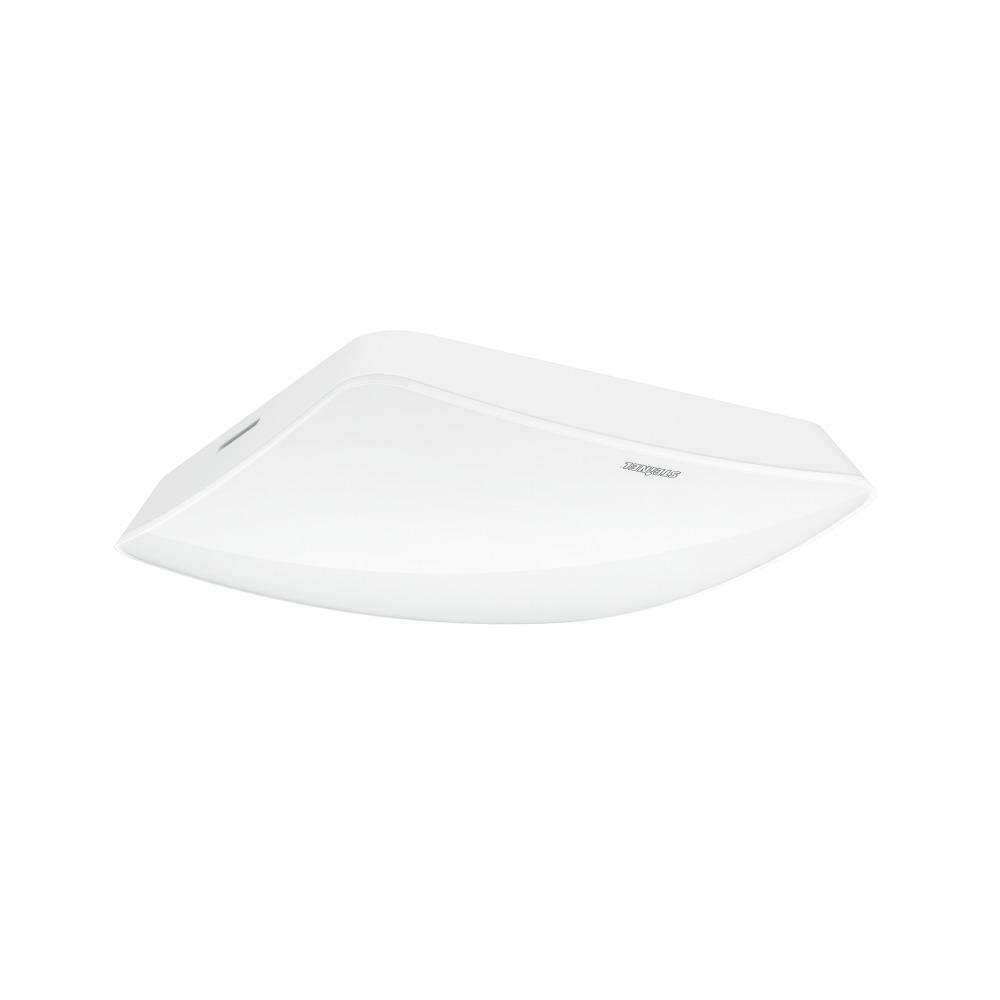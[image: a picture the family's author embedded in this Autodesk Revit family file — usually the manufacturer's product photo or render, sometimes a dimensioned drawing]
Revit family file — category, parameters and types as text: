
# Revit family: truepresence_056339
name_source: partatom
category: Electrical Fixtures
revit_build: Autodesk Revit 2016 (Build: 20151007_0715(x64)
units: mm (PartAtom-declared; Revit-internal decimal feet)

## family parameters
Cut with Voids When Loaded = No
Host = Face
Maintain Annotation Orientation = No
Part Type = Normal
Room Calculation Point = No
Round Connector Dimension = Use Diameter
Shared = No

## types (1)
- True Presence
    Apparent Load = 0 VA
    Default Elevation = 1800 mm
    Description = Type: Presence detector; Dimensions (L x W x H): 31 x 103 x 103 mm; Power supply, detail: KNX bus; Sensor Technology: High frequency; Application, place: Indoors; Application, room: classroom, lecture hall, one-person office, open-plan office, high-bay warehouse, production facilities, conference room / meeting room, hotel room, care room, duty room, recreation room, dining hall / staff restaurant, changing room, kitchenette, sports hall, reception / lobby, WC / washroom, warehouse, Indoors; Installation site: ceiling; Installation: Concealed wiring; HF-system: 7,2 GHz; Electronic scalability: Yes; Mechanical scalability: No; Mounting height: 2 – 12 m; Optimum mounting height: 2,8 m; Detection angle: 360 °; Angle of aperture: 360 °; Sneak-by guard: Yes; Capability of masking out individual segments: No; Reach, radial: Ø 15 m (177 m²); Reach, tangential: Ø 15 m (177 m²); Reach, presence: Ø 15 m (177 m²); True Presence reach: Ø 9 m (64 m²); Twilight setting TEACH: Yes; Twilight setting: 2 – 1000 lx; Time setting: 30 sec – 1092 min; Basic light level function: Yes; KNX functions: Photo-cell controller, Basic light level function, Light level, HVAC output, Constant-lighting control, Light output 4x, Air pressure, Humidity output, Presence output, Day / night function, Dewpoint, Temperature output; With bus coupling: Yes; Settings via: ETS software, Bluetooth, Bus; With remote control: No; Interconnection: Yes; IP-rating: IP20; Material: Plastic; Ambient temperature: 0 – 40 °C; Colour: white; Colour, RAL: 9010; Manufacturer's Warranty: 5 years; Version: KNX - concealed white; PU1, EAN: 4007841056339
    Height = 0 mm  [stored 0 ft]
    Length = 200 mm  [stored 0.656168 ft]
    Manufacturer = Steinel
    ModVariant = No
    Model = 056339
    Number of Poles = 1
    OnlyDefault = No
    Power Factor = 1
    Product Name = True Presence
    Product group = Presence detector
    ProductGroupID = 4
    RLX_Detail_Level = 1
    RLX_LegendID = 3.1
    RlxData = Q
eAHUvXeUVNXbrduAICAioiiCICJNzkjqql1FzhlEktAgOefQBAmSc46SkwoCCip2VRciZgXE
nHPOP0Uxct5n1VzfqW/cc++4/5wxzuE7T8/5znr32muvHehuOb+dK+3y5TT7c/lfJ1j3J783
ppftjy9v7eBdchu286SlzY4aCetwX9yGly9/nef6tKZjRg0YNrr/xGFjRrebNMrcsPGD8ufL
zaY3dksbnzYpbVBambRO5galTTBGp93tkoppNdPqptVLq2P/19A6KqU1stFv0xxSJ5nHssuX
v8tTKK3dsCFDJzYfNWzixEHj08rkYh8Fx6f1TxuY1u+/jcZI5f6XI9m8bNZXpLUfNGForsJu
BLff9P9Fd660K5T+ZAf//+fP/56+a92ux4xNSztpbnSutLQHSrYN3phUMbimz8zYQ8+2D/IU
PxBeXX167JposyD/XxnB3KFzYre8UzxIe6BQ8NnIVbGdO74Jj51xZ+jdTzbHWi/9JNyl9qlw
g5e3xO5qtSPcv0Hn8N7Ku2IFyk8NvzRncujhrXtidevND5f96fPQ1Px7Yj//1iGYV6NNRvO6
WbFlj3YIpuW6LlZjeFZs+fvtg5yuO2Obbp7u9xVnX+/b3N6aVDH+Re+Zfj5x5qP9xlL2G2O/
2lc2+9IcsplDj7vHhtPSPipX8M09sS8joexXJryWkfelpE9reD5WN2Nz7J3wI7FLzdvHxy2e
GGvY6Kb4zTddHc/XYVWsX7WK8Qln2sTrr53MHOK2Jm4OL3zWIF7spubxn26YHpvcf0140JH2
8VJ1JsYeGVYvKL2iRbzBz9NifatVDAbYts1s2+pDL4aKjusQr71uQmxV3QLZD2/pEL80bkJs
zV+fxrZ/9mTspr1bYm9s3RnrGLkjVqjIrti1X8+PDe79XfZzf++OfXJoauzEZ7OyN290xxKb
sz5POseiPESu/hD9GifMOBwv56xy7w1+X2H2pWMMOMYtf6+OrT3aPkivPdEfozvvNv941zNt
gk42/xnr68U7Tm4R/JUnK/ZAwV+yvx3XIZizdkKs5LBrQgO2dAjC4yfEug48Hi7RpH2wddlE
1i2YbNvebts+83qDYGXZ5sHsa6bH7HqL2/UW1/UWt+stxvVm10Pcrocw1wPnhGvsiye3xd61
frsGgi/tGrDrJ27XzxNcP3bNxO2aCXPN/PVTu/jMhw+EexUdEfv3ibbx14/vDx/t2jWWa36b
ePXH9oXzrg/FBv/RLr5/65nbyO99sq3z5Nd/3SY+vsUHMfI7j7eOB7++FyO/599WNk75OPmh
l1raOOlx8m/HNI1P21fP5ctaNImvXlnX5WR8Rj8Zn9HPGIxFzhiMRc4+2Tc5+2Tf5GOK5tnD
XMnxzFX94ZT+sO+38YOU8QM/vs0nSJlP4OdjWZAy/8DP38YIUo438Mdr+wxS1ifw62NzDGIT
1+5lnjbHoEfD43uZp/rd+tsc6Xfrr/ED+m2OjB/Qr/m43ObIfFyu+bucjM/o1/G6nDEYK2V9
XM4+2Te5rWE55sp+C755Wznmqn43V3Ktvx+f8+XH53y5XOfX5Tq/LmeNmSvjsMZ+/p9saRFf
cbJcYPuMvXOoSfymT2s536pWB3ftca1eKNUufmDThzF815pt7BquEMe32dws3j+7vvMoNTmf
04dnO7bHc50wrvKwz60/8P02TuDHMQ38+PZ54Pdr2wV+PjaeO7+MqdzdX+oPyDWO8xrfee3X
eRuP+TjP/ce4mqcbF6/jcrmO13nmy7j0tGuYEV+5JezW8OsHa8RPv9TUeVvj+C9bWjj/9pwd
sR/6tXa+6pTOGUUXt3H+4qYHwhNDyXyhnZOw+t/8sFbwyENNXM8HK8PB2WYZzhc83zQ4t7eG
8/9Y70qdx0vhVkHG8W/DnNMiM1oHC+pudP79RW2C+6v3eYL8q/6tg7eG7uBai51o2CqoMv87
52uubBnMeKNAnLxyvZbBuyevc/4/+VsGhx8u7nzN/7QIfq9Z0vk/3m4RfPZOKee/tjlwnGx7
ckaT4FKD2s4va5QRvL427Hz3L2sEp482dZ7r7mO7/uifdMvX4TdatnL+vgmrw0tWtHY+o8i1
2ZXs+UhPseBorEuFZG7rE2+qbYfEasULn27iep4aFo4vH5Xh/KXHm8YLv1HD+e+T17nz3/Vq
FV+09DN3vP/sbx3/fN5i56dNbxPP983cEPta9Fer+NR/ssP4r/9YEBtfeOF/+QEPL3L974QX
hgd/uPC/vO/hmxf7liUtt8DzHR3g+R4Lj+YV+HwCf6U8yneGbFfA4DPAF5RHr5JHCwn81fJo
YflrTP04+CKqUfYHeL4Lw6NFxXXKyPHXCzw91Cjb4NFiAs+41Cj7Bubre/A3qEZvFPji8uhN
Al/C4HO2LSnwHC81erMopYy8tMF2gL/FYH9lDD8f/K2q0bLyqD92/G2q0XKC77B9D768arSC
PFpR4CvJo5Xl0SoCX1UerSbw1ZXXMPVj4muqRmvJo1yDgK8tj9YRXL++h+vUj4nnWqVG/THi
86tGuUZuN+oa/nzh/TnF11ONlhH4+vIo6w541hrwrDXg/ZrjWWvAs9aAZ30Bz/oCnv3hUdYX
8A3kUdaX+TY0+AwyDD5DQ/LUePtG3n2GBgIfkUf5EQvwjeTRxgLfRB5tKvDN5NHmAt9CHm0p
8K3k0dYC30YebSvw7eTR9gLfQR7tKPCd5NHOAt9FHu0q8N3k0TsEvrs8eqfA95BHewp8L3m0
t8D3kUfvEvi+8mg/gc+UR/sL/AB59G6BHyiPDhL4wfLoEIEfKo8OE/jh8ugIgR8pj44S+NHy
6BiBHyuPjhP48fLoBINrlWuXaxTwE+VRrlHAc13yOdc8NeC5D/DoJIG/XR6dLPBT5FGuXcBz
vfL5TarJ8CVUo1MFvrg8Ok3gs+RRrmnAcx3z+Q2qyfDkgJ8u8Dz/qdHS8ijXPeBLyqNc94Cf
IY/OFHj+vqFGbzboxfs+slkCX1gevUfg+fubGp0t8HPk0e4C38Pgc74HoAZ8QXl0rsAXkEdz
yaPzBJ4/1Py5V+Dny6N9BT7T4E9ugxrw/P2CRxcIfG15dKHAL5JHuccAz33F5/z9RQ14csAv
Fvia8ih/L/IZOlTgq8ijwwV+iTy6VOCryaPVDXrxvo9smcBXlUeXC3wDeZT7FvDjDe7bFcY4
gefeR1fKU+NHSVfJU+NHSFfLU+OHSdfIU+PXqkb9cwy/TjU6SODXy6P+OYnfoBrtL/Ab5dF+
Ar9JHt0sj94l8Fvk0d4Cv1Ue3SaP9hT4++TR7fLonQK/Qx7dKXYpow+/WzW6R+xVRg/+Duk+
eWp8V+l+eWp8Z+kBeWr8QdVoR4G/Xx5tL/APyKMPyqNtBf6QPNpa4A/Loy0F/iF5tLnAH5FH
mwr8UXn0mDzaWOAflkejAv+IPBoI/HF5lHsD8OONscZoY7nAL1M2Up4av1Q6XJ77n+fFYiPT
mG8sMHjODDAWCjw5minP866Pca/AzzN6GHOMuQZZL4Mc8OQofXie3d2M2QJ/j4F2kafGz5J2
kqfGz5R2kG9n2saYbjQzphhTjVZGC2OawJOj9OEjxkRjktHEaGRMFnhylD78ceOEwbkA/Cp5
dILArxD4lQbbcn7ZBvCPyqOPCTzXNDXKtU7vwwafAZ5rC48eNbgeH5KnxnNN49FD8qgfB899
Qo36/XHf+fngeY5QozxfuF95bvAZ4LfLo/TtN/YY9AJ+tzzK84UenhV8Bvi9Bp/tNPy2ePbB
vnnu+bnhH1eN+rXFr1GNrjbo5fnJZ4DnOYtHN8mj6wR+ozy6QaxXRt9agzEA7/fHeWc+rxqp
f04/3ZLLKS3n+umJXw7VjqStrpI9tOiMRLMxlSMvTKoSCw+fkbglLY/rmfP5zES5Q+eDC8ur
ZD/ywKxEvypPBK/VrhIr+v2sxDeT0iNPrKqSvW73jMS06emuH//rusqR87vSwoxz08M2vv1h
/H8+qx8ZvezB0N7XpydK/JE7sn5llWzGfzp+PqCH8Vd3zg4OLqsSYvzKR3a6/I+69ySu+898
549MuCdBb/JP8r8Yep9danls9fo68ehj9yS+3Vw6e+PWnXG2LXZ3/4a3F/wt3iN9VuLzsz9m
31m4eM4DFWYmvsz3b+iRNuk5zPls2YoNhz5dOYc5F3qldHjqiNo5zHn21zeGnskIckpunJ74
q/Ct2Q+dSvb802Z/dvVjST8qq2b22zOb5JzrPj3RsHnZ7D1PtsxhbT/edn3253na53x7Pitx
Zlqp7OP/XHRz2FSuY8P8R5Jza7t3XvipfnXdnK+79sFw+V+rOv/W2r7hwqcaBBzLnMeeDN9/
ZlrAsff78lhoZbudQcpxBRyXjiXCsbzx4tHQ0ocqRziWGw6WDw2c1STC3O4/uSvUoVoQ4Viy
i6eHuk5Od/2b8p17fIqdP7bVcblttSbOf9326tjtWbUjrMlrXwyIvXJr0o/d2zD04qWLbg6T
/96bndkrObf9L0+MNRsy18358Ve+zn708Yg7luNPt8z56cy6hm59DtTO6Zc9LsSYwbHaOWN6
LcvAn59TNOeJTXXCL/acmdhQonjOnSPOhjhfowdmxw99d2UG10bT5jvjg/o8HmIdXl+1M352
eHPn9z60Mz6y3LmT5OrJTulxfm2P7HiPdQXcNXbnLWVyrtu/Njv97RmJostvzPlq9ZAY+2p/
tHbOxedfcPPJfLN+zo/9P8jmuv0pX/ucFQfqZ3BOGxnV068Ijg5uE6m5MCtxtnihYNqBjpEv
92UlRpWeG07xMeeHZCU+a5g33qVll8gfZ4Ynrt+4J6dUk4mR5u9VT4zdVD3R7Nz8yJSX9+Y8
tGJ4gnzf2evij/fLStB/vtTO2KpdWQnGaVl6WXjF3qQv/XPuoOSwZM+0J3ZH2nyb3HbjgurR
Yj8kx7ywc3g0/+C9bl8rBmZFf+t3lZvDzXuyoteV3uDmduP+rOjaQ7PdnNsOz4p2O5gWsN87
3h4eLVB2T4T5fHq5ejQ+sXqUea75d0/ku4eHR8mPHbw6aHF3VpT+PSt3hbvtyooyzzGHlsRO
7036+jcWiL8yKNmzavGenG7PJrf9eED1xJFra7gxOy4bnvj9nb1uX2uPTUg899XqSFaRL4LL
PbMSnz67P/zyF90i/y6enKi5cmr4vSOLI08VnZ74eejfIZ5nF4pnJS5dHBbbU65XJG/VyYnQ
prmxAc2WRRpsmJ7o2u5y7JetGZFflmUlavbPFWduF/4amfg6dDznrZ1XR5acq5go+2TVxC37
7o/89Em1xDtzqyU637oqsmDBgZyLr41IfD3/zkjZZUXiZ16Ynjh+R91I2kcXY7VXJdf/6B/r
YudPTk2MPDAu0v73NbG7rpnizmOjKnNDj/+S7D+2el7o7OFk/zcNloW3FZua2HbNjMhzH38c
/mJdMt+amS/osiTpw9+vjVwzf5Qb8+mfvw//9vOMROnPSkSKTL0vct9X/RMzQ49GrhuVHi30
c8Q9dz/6onK0YscqiVylDkQavzsy+toXyeO65sj0aIHMq+L/XKofef3o5GitlQ/GwoMWRVYF
E6MXS22IfVRyc+RI0enR3YfTYqzhNzdlRR+c1D3MGraoOjm6wK4H1vD4+unRAXY9sIZdlmdF
u5tnDRsXHxUtsf+RCGv4wdcVowMPVI2yhiVurh6d1bpalDV8sdGByHNPjIgy5rBviwTLX5ge
ZQ1Pdv49/ObK5LUxsMnG8JSTU6Os4aPNNoeHFp7iroeb+s/Kzvkl2V9/3fTsdw4n+0+uXhJ7
q9jUKGt45diPYg3XJ/PTB/LGTyxJ+jteWJszc8koN+ao81/Hvv/PjChreMvd9+U0PDQgWmDq
w5Fw2/KJ5RuDaI3CNSPxM5UTNcZVibKGO3NGJmbOOOGO69TCSCL/6huizQvsjryTVSfx6I91
oh0K/hYc//bKROkfW0br9T8YuXXggZyPvh0b/erRo8GPLabk/Nl6XPSpsSMjM77+O5Zr1bTo
3H/7R5bWnxm7It9MN4ch4yKxydGsKNfVjc8uCVe8anqU9b++6Z7w7y/OiPauWSZyw+0Fg8Ov
TYv+fbpPZNlLKyKr2492x1Kx54HI9jvGRFnzadNviD63KeLmtvqm26PvdErOrfcrLaPZD1/p
zsWO/OOiQ248EGnT78Gg88xx0Z9vmRhhbt8cyYr2sPPY5Mr2kRLtsqLffvStu7+ebTAzusXO
+wsbikU6NcqKnltdJcw8ZxeaHl13aLa7Ts7mtuOw5wbrqWeFe57UeCAr+qc9Wxhz48Ks6CXz
XCeD59i+brzBefvOO+r/9u7T164ly3luLHliVDTXujU5XANnPxwdHVbwQA7jf7U+Er1j7o2J
rPrbI7121om2fKFOgvV/8+v80fvmt3TX/O/b9kem/zs2Ub/wo8Hlp6ZGZtUal+AY8z1dICj6
YFaC+SzI/W548ITkc/LrXavD3TrOTGT/WDSydGR6eMGCaYmHtg6MlM2/OlbnxekJ7pfxR9bG
nt+Y/L6m7k/545X/nJbgGn4gc3nO8/NGu3vzoVMHcob2GZPI90fByJjniyUulIsmuE6q/Fon
MWBycp5dG7ZM7LyYP8F1MuDdsYmZQw7kMM8dGeMSt9ebmsM8B47PSjRd92GMdbh/9szEDUft
+rbzGzs9NVE3mjfGmqyoMCPx3Ix5Ya7V9c9MS5w7fjj8c2Y/972Vvv+J5jKT28hjXGHkNfKJ
K03ziwKmBY2rjELG1UZh4xqjiLjWtKi4zhSuN4oZNxg3GsWNm4wSRknjZqOUUdq4RZQxvdUo
a9xm+DEZH8oZ6UZ5o4JR0ahkVDaqGFVFNdPqRg2jplHLqG3UMW436hqMV8+obzQwGhoZRsgI
C76JZNG4CBsZjY0mRlODn8maGy1ES9NWorUptBFtTaGdaG8KHURHU+gkOptCF9HVFLqJO0yh
u7jTFHqInqbQS/Q2hT7iLlPoK/qZQqbobwoDxN2mA41BxmDDH98Q80ONYcZwY4ThjxEdaYwy
RhtjDI7XHys61hhnjDcmGBONScZkMcWUNZhqTDOyjOnGDGOmMctIXQfW4x5jtjHHmGvMM+41
5hsLDL8m6EJjkbHYWGKwPn5t0KXGMmO5scJYaawyVos1ppnGWmOdsd7YYGw0NhmbDdYOthhb
jW3GfcZ2I9PYYew0dhm7jT3GXoP97zP2GweMg8b9xgPGgwbn95Bx2HjIOGIcNY4ZDxuPiOOm
J4xHxWOmjxsnjSeMbCNmxI0cg/VOGKeMJ43TxlPGGeNpg/P2jPGs8ZzxvPGC8aLxktHWGGG8
bJw1zhnnjVeMlkYrw19XXGOQaXAtpl6jeI4RUq9tPOcc/P3AvQHMvZPR3uBaA3wbg3kB/sL/
xdTLZc/A3HaND5+ccfXi7CCt0KaGq65fHWQerxJ6/YUzwXOje4Rv23U4ONjlkfA/1/UJ3hqd
Hf6kx8Zg6tF/w9GJc4KbLxYJLqT1DY73LRRU6z0isKVIW/dk5yDt4PQG49+rFKStXN6w2Kd/
h+uvaBBh+zPHOkSod45rHCn/2bww46Ps/9Ki4uGyuTtE0Cdat4uMubgtxP4q5X0/zP7ea1si
mFm2RgRtnl054vdb5e1abh4L60SDnz4uGlS1fwOYdaRX8EH4Dqc5v70UfrjtuuDQ0wcalr3l
eDD5n7nhJWuzgztsn99seT5gP7t/eCood1Xx0Kxn8gYvHxnckOMnP7r1TKh0yVyhIhVLhul/
rE1NG6dCg5Vr7nTHWm/6zuB0u3fDq/atDOp0uikYcGlR8PO1tYJLaxYE9R6MBOsWznfzoS67
uK/7fGjZkcFD7YpHmF/vGQUj1GfSr4x0/n2Oyx/+dVfwyaR/gr+f2Rj89srXwbl3Dge5/sof
eb382aB699cCzsuKuz4Jehx+KShS8d3gzQUvBO13XRe5ff7ZYM7UUpGqW84GF56pFan0/csB
68z5u6pF8wj9PUe3jlz74fMB68s4x5bUj3A+WVfO54cfVYlwHvt/fj7gPGxcdS4Yf8NvYfbL
ejAf1i9X8XPBF3dOcPPk+B+tnSt5fu04WAeOi3UocuSqCOtw+vZCNq8OweGlWwOuA9aL42X9
OM4b3z7rxuP8cLzsn+vxsatedsp5Yr7LLp0Nnh7fNii54FwwpP/K4M+qNSIv59sc+qp4zcie
206GXmrUPNLqzLrQ+D9qREof+Cr079s1Iu2LFQq/Urakq1HqR078G/D5hgKXA+pS337i6p+H
furq3b+84+r/TH/X1e+sfM3VB8q+7urfmp922vLsaZe/9MYTTi/1eMLldQvtcHWXx7e7etml
Dq5G2V+fY4kw+/8q7ckwdf7Ct7r64N/lXJ2593SIzxvNfDHE56fONXB1ZqW2ri4/Kbn/yf8k
9/9X3mw3foVFyf0PCiX3P/fL5P6/697RfY4y3s2jTyX3F0/uf/bCsq6uOLm823+njU8n93fz
2eT+T0SS9TWdXb17Wyu3jsM+beXW9dCXzZyePtjM5Zm567t6zFv1kn0ZyfUfZsr+P/0suf7P
NEiuf7sSn7r5ldmUXP9Xyr7r6rIPJtf/pZPJ9X+zc3L971+Y3P+FF5P7b9SlWcT+HVc4e2tL
p426lIuEHtgS4nxzXfzeo0Sk9L9bQtdH87nr5Xz/fwPyBwt8EnC9tBr1iauvG/yO00+ffSuo
sHNx6KYXnnc11x81zwmut88ff9Xpud9fdZ+/0fsppzxXttXZHdrZLdvV3QftcMrzJ1J2f4jz
z355fowfdTDE82TlTQfdc+fLUgdC5/vnhPk885ZSTnnuMB7PobQuW0Odbnki5D635xPzyTyb
7uq8S5P7r1vpaTfPUV9mu+M6Py85j1Yrk/N4NrHSzXv/9RMD1ofrgfHurdEuYH1+Wvl7mONb
VTrh9n9peskw6/PRptKuHpsTc/sb++5ut/8u/du59eV5wnx4vhzptTmUWeO2kFObJ+OvqdDa
9fEc4ng2lG/u6i5V6zvlecX6cH3Qz3OM9eG5xvrw/GN9Ti9Nnrep25Lni+cg4/EcZH2arE+e
P55XzOdy+dfc8W0qmtz/0Y9bu3kua9PGXSfj73g74Lopuf0DpxeLfeZ0Spsr3edlCt2cvJ6W
1XTaYEjyOjt+NHmdfdEnOc5smyvjfLTjH6fPDazMvyUMP/fvw07rPZHHjXvy2S7J/S1Y6fTg
i7udnlp/yOnCJcecfnvFcaexZieczt/8qNOuBZ9wGnr2lNOHLj7tNPPsPrffVScuOW1QrJLb
b8WXjjvt1iyf67u7SA+nv65Y6/S2d086vbVncrwFx5Ljtb42uS6/9Eyuy9NffOr60sr+43TE
zwXcegwM3eI0357aTm/468XgnvYbgiXhxcHmoouDtBdfCH558GTAfs5vfSE48upzwTeRU4H9
+9tg+bang3+6JILCtZ8Prou/FGT93ddtNy4oGKzqcVXQbn/BgPmOKTovg/n/Wn9Xxh8dXgrW
v1YgGHfoxeDsvsfDjP/8uArhy72f5++pEPN/Y+muEMdTYXAQYr/lNl7O4HgHdX0og/V49e3n
M9Kav5Wx5pGj4VOrH8l4+vl/wqwXfbML/JFRfuyI8Ozg+4waSxeHWc9BXauHdh7LG2I/aU/l
CjW41CScOSEtdO/29mHW/aNqq0KzP2kZKlzs09Cplv9mFLzvzrB935PRr1Jbdxysw9FjbYNb
174UVOqzMmCN0vYcyRhXcnnAPN5psDtgfNaJebBOH31dO7SidCI4NXFt6Pi4M0HaX1+F7tn7
XDBwwC/h3t/a9vbHvnVzP3Pbt2/O5zEF8ivk0bwCn0/gr5RH8xtsV8DgM8AXlEevMgoZVxuF
jWsMsiKqrzUtapBfZ/hx8NcbbFvMuMFgn2Q3yqPFxU3K6MGXEHh6qFG2waMlBZ5xqVH2DczJ
9+BvVo2WEvjS8ugtAl/G4HO2vVXgy8qjt4lyyuhLN9gO8OUN9lfB8PPBV1SNVpJH/bHjK6tG
q4iqyujDVzOqGzWMmvJoLYGvLY/WkUdvF/i68mg9ga+vvIGpHxPfUDWaIY+GBD4sj3IBQ0QZ
fVHDj4lvpBrlmADf2OB4uWa5RpoYTY1mAt9c4FvIoy0FvpU82lrg2wg8P+MBvp3BuvMzIGsN
eNYc8B0M1ph+1rejQd5JHu1ssMbMoYvqrqbdDOZ7h8Fn0N2g506jh9FT4HvJo70Fvo88epfA
95VH+wl8pjzaX+AHyKN3C/xAeXSQMdgYYgyVR4cJ/HB5dITAj5RHRwn8aHl0jMCPlUfHCfx4
eXSCwE+URycZk40pxlR5dJrAZ8mj0wV+hjw6U+BnyaP3CPxseXSOwM+VR+cJ/L3y6HxjgbHQ
WCSPLhb4JfLoUoFfJo8uF/gV8uhKgV8lj64W+DXy6FqBXyePrjc2GBuNTfLoZoNrdYvRQ+C3
yqO9BJ7rks+3GdSAv08e3S7wO+TRnQK/Sx7NFHiuVz7fbVDvMfYa+1TvNz1gHFR2vzz6gMA/
KI8OFfjhBp8fMqgBTw74wwL/kDx6RB4dKfBH5dHRAn9MHn1Y4B+RR48b9OJ9H9kJgX9UHn3M
eNw4aTwhj2YLfEwenSrwWQafxw1qwOfIowmBPyWPPimPnhb4p+TRMwL/tDw6W+C5f/j8GYP6
WeM543nVL5i+aLyk7GV59KzAn5NHuccAv8Tg8/OqyfDkgH9F4C/Io6/Ko8sE/jV5dIXAvy6P
viHwb8qjbxn04n0f2dsC/448+q7xnvG+0VMe3Sjwm4zNxgcG9/R640NjrfQjeWr8aunH8tT4
ldJP5Knxy6WfylPjP1ONLhX4z+XRxQL/hTy6QOC/NOYbXxnzBP5reXSOwH8jj34rj94j8N/J
ozMF/nt59Ad5dLrA/yiP/iSPThP4n+XR/4hflNGH/1U1elH8powe/GTp7/KTTC8ZE6R/yFPj
x0n/lKfG/6UaHSPwf8ujowT+H3n0X3l0hMBflkeHCTw/aFCjg00An8sYZDa36d2mgM+jGu1v
GeCvUI3mlUf72eeAz6cavcsywF+pGu1tGeDzq0Z7WgZ47pF1xhrjXYF/W9kqeWr8G1Lubzz3
P8+LVwyeWU8bLxo8ZxYaZwX+JeNegz56ZhuzjDMCf9rIMmJGwiCbYZADnhylDz/VmGJkC/zj
xkRjvPGYwJ9QNlaeGv+wdLT8SNPhxmFjgLHLOGAMNYYYDwj8QWOgQR89fYytxnYj0+hr7BR4
cpQ+fAE7DwWNqwS+kDx6tcDb/wiGA3+NwbZFDLYB/LXyaFGBv04evd6gt5jBZ4C/QR690Shu
3CRPjS+hGi0pj/px8DerRv3+Spn388GXVo3eYpQxbjX4DPBl5VH6bjPKGfQCPl0eLW/QU8Hg
M8BXNPiskuG3xbMP9l3Z8HPDV1GN+rXFV1WNVjPorW7wGeBryKM15dFaAl9bHq0jbldGX13D
j4n3++O8Mx/+SNy9YnfTf/1bhf/5WfLfheR23cnvTXxfHm2f/Gx2FPVZyPUnx7vCPJ9dqYwe
n+EZjzqv4T8jw/ssbN735TPn+8no8VlAm8Zjf3x2DZFl9PgMT0ad36BuZPg+n0WVsU4FDPqf
UMYcfEY/21IXNKhPGmT0+YzPyaivMqh5tvg+n/E5GXUhw/f7Pp9dTZv68PQ/SmQZPT7Dk1EX
NqiPGb7PZ2VSMtaN/puUcRw+o59tqYsY1MUNMvp85teedSPz/fRRX6v8RlMy+nyGkqFFDbSY
4ft8hpKh1xno9Ybv8xlKhvK5V9/ns0b2mR+PDPx+mYOvbzBPn58XtT+O1J6K6uN4GYcev1as
Bxm1X2fODRl1CYN9kDE+9S0GGT0+K6nMz4H6ZmV+n2TpKX3sk55dyvy8yEop8/OiLp3Sx9zI
miijj7nRs02Znz/ZFmUcB/PgGMoYHAdz9tltyrieyMoYtxr0kTE36iMGGT0+K6vMz5/6kDL6
mC/Z4ZSMubHPA8qYi8/KKaNmvtT7lNHns73KWL8yBmvczPDnqIw5svIGWRn7yjFQtzB8n88q
KKNmvtQtlXEufeavK641MupKBuNRc1zUrQwy+nxWWRk1x0XdWhl9PquijJpjoG6jjD6fVVXm
j5O6bUofx0pWTRk1x0XdThnj+ay6MmqOi7qGMvp8FlFGH8dKT3tlfj3Iaiqjh2Ol7qiMPp/V
UkbNsVLXVkafz+oqo4/joqezMnp8VkeZP3bq21P6OH6y15XRx7HS86Yyenz2mjL2wXExj3PK
mJ/P6imj5lipX1ZGn8/qK6PmWKlfUkafzxooy6OMumFKRi9ZWJlfN3qeV8a2rBNZhjJqjp/6
jDL6fBZSllsZ9WlleU3ZL/sMlOVTRu2vDTKuGeqowb2Q376SUTcyyFhz1rOxsc4g4xnmsyYp
Gb30bVbGvU8fPU2VUbPu1F2U0eezZsrKKKNurowezgV1B2VlTH3WQhnPCDLqlsrKKqNupew2
ZdT+PueeZlvqNgbHy/1LRt3WICtvX8mo2xlk3G9k1P5+494io/ZzJuNYqDsabMs9Q0bdySCj
5vqh7mr4Pp/5e4v7g4z6bYM+1plrijVeY/jxfLY6JeM6Y/zlyhjLZ92UUXOdUaf2+ewO9VFz
7VGvVMZ4PuuuzF+f1Hem9HGNkvFzCnOmj2uUnlUGmb+OyXoo89cxdU9l9HEtk/GzE9vS18ig
J6LMX+9kvQz6GtnXxgZ1b4OMPp/x85rv4/qmJ6yMHp/1MU8fNdc89V0GGX0+42dA38c1T88m
Iuujx2d9lfn7grqfMvq4N8j4OZRt6eM+oCdDGT0+yzRPn79XqPsTWUYf90umwc9wvo/7hZ4G
yvw9RTbAoM/fU9R3K6OP+4qMn5F9H/cVPTsNMn/vkQ1U5u896kHK6OP+I+Pnd7alj/uPHv6t
Ipm/R8kGE1nm71HqIcro4z4l4+dB38d9Ss9BItvW38tkQ5X5e5l6mDL6uJ/J+H0C29LH/UwP
P3+S+XuebDiRZfRwP1OPMHyfz/jdk+/jHqeHn3fJ6PHZSCLLqLnHqUcZvs9nV2hb+rjH6eHn
Zfro8dloIsuoucepxxi+z2e5tS193M/08HM7ffT4bCyRZf45QD1OGX3c465H29LH/UzPCYNt
/XOAbLwy/xygnqCMPu5xsj+U0cc9Tg+/Y2A8/xwgm0hkmX8OUE9SRh/3PdlvyujjHqeH3y2w
LT0+m0xkmX8OUE9RRh/3PdkvyujjfqaH36uwLT0+m0pkmX8OUE9TRh/3PdnPyujLNOg5ZbAt
PZkGWZZBlmlf+xvU0w3f57MflGWacj/Tw++C6KPHZzOILPPPAeqZyujjHif7Thl93M/08Hsl
tvXPAbJZRJb55wD1Pcro4x4n+0YZfdzP9DynzD8HyGYr888B6jnK6OMen218ZbBf+rif6eF3
YGT+OUA2l8gyerifqecZvs9nXyijj3ucnvPK/HOA7F5l/jlAPT+lj/ue7FNl9HGP08Pv69gv
PT5bQGSZfw5QL1RGH/c92cfK6OMep4ff6bEtPT5bRGSZfw5QL1ZGH/c92YfK6ON+poffD7It
PT5bQmQZNfcz9VLD9/nsfWX0cT/T864y/xwgW6bMPweoG2u/9HGPk71nsI969jVkLDdWGD7j
HqdeTWR99PhspbKwMupVyiLKqEPab0NljLXGYLy69pXxqNcaPuM5Qr2OyPro8Zkf73Zl9Kw3
6CPjOUK9wSBjO58Fmgt9PFvo2WzQR4/PNiproox6U0pGL5n/3qeZebalp772cZMyxt9isI8S
9pU+6q2Gz3hWUW8jsj56fObHK66MnvsM+simGdTbDTK281lDzYU+nmn07DLoo8dnO5S1Uka9
MyWjl8x/79PGPNvuNHYbjHeDfSVj/NSMXuo9hu+brnqvMnp85r9/uUUZPfvUV1oZ9f6UrJ3q
A8qoGY8eP15J8+T0HDSYC1kHg/p+w2czVB9WRo/PHlBGzbOZ+kFl9PnMf59TyjJ66fHjkdFH
dshgvzfbVzLqhwyfzVJ9RBk9PuN3/PQVVkbPUSJl96g+poztfMZ/K6DvamX0PEykbLY56kcM
MrabbZDx3xx83xxz9DxKZH2z7avPjhNZ1l0Z9QkiZbPNkfnvkXqYZ1t6+O8V9F1lX8kY/zGD
rKB9JaN+3PDZXNUnldHjMz9eAWX0PKE+dkUfdXZKxt9F1DFl9PiM/17DfvlKRk+cQtm9qnOU
0eMz/juP75tvjp4niWxbenyWUNZXGfWplIxeMv89UqZ5tj1l8N+vGC+3fSVj/NMGWR37Skb9
lOGzBarPKKPHZ3682sroeVp9ZPxdSf2MMrbzGf/NjH3Qx9+L9DxvkNHjs2eVDVRG/VxKRi+Z
/x5psHm2pecFg/Fq2Vcyxk/N6KV+0fB9i1W/pIwen5XTnGsqo+dl9dVQRn02JRuq+pwyasaj
x49XxTw5PecN5kI23KB+xfDZEtWvK6PHZxeUUS81qF9VRp/P/PdD1Syjlx4/Hhl9ZK8Z7Le6
fSWjfsPw2TLVbyqjx2dltVZVldHzlvrIlqt+Wxnb+ayMtm2gjJ531Ec2VvW7yqjZlh7/vRR9
4w16+O+6zHmCfV1hvGc0UTYuJXvfPH1jlFF/QGQZ2600qJtqW/p89qF5+kYpo/7IIKNnlfGR
4belz2cfm6dvhDLqT4gso2e1QT1K+6XPZ5+ap2+YMurPiCyjZ41Bfbe2pc9nn5unj3qtQT0y
pc9nX1hO3xD7Skb9pUFGvc6gHqFt6fPZV+bpG6SM+msiy+hZb1AP17b0+ewb8/TdrYz6WyLL
6NlgUPtt6fPZd+bp66+M+nsiy+jZaFAP037p89kP5unrp4z6RyLL6NlkUA/VtvT57Cfz9FFv
NqgHp/T57GfL6bvLvpJR/8cgo95iUA/StvT57Bfz9PVWRv0rkWX0bDWoB2pb+nx20Tx91NsM
6n4pfT77zXL6etpXMurfDTLq+wzqbtqWPp9dMk8f9XaD+s6UPp/9YTl9d9pXMuo/DTLqHQZ1
d21Ln8/+Mk8f9U6Dum9Kn8/+tpw+6l0G9V0pfT77x3L6qHcb1L1S+nz2r+X0Ue8xqHum9Pns
suX0Ue81qPuk9PksTdkd6qPOpYyefQa135Y+n/nfLXVVRp1H29Kz36DurYw+n12hrLMy6rzK
6DlgUPdI6fNZPmXUBw3qO1L6fOZ/N9dRfdT8mzDWhZ77Deouyujzmf89YXtl1Ml/lzI7Ss8D
BnUrbUufz65SRv2gQd05pc9n/nebbdVHzb+FYn70HDKoOymjz2f+96ytlVFfoz56DhvUHZTR
5zP/O9+WyqivVR89DxnU7ZXR5zP/++fmyqj590/MmZ4jBnU7ZfT5zP8uvKky6mLqo+eoQe23
pc9nN6iP+phB3VYZfT7zv79vrIyaf+PF/Oh52KBuo6xxSub/W0JUGTX/Boxt2e4Rg7q1Mvp8
5v+7RqCM+mb10XPcoG6mjD6f+f/G0kAZtf+eYbwyavcPoGwuoy1bbvC9hv9ehWyZQe1/PzRS
GbX/fohsqUF9m8GxZdrXBUa61RWVDbB6ocH3tf57ZTL6qH1fH6vvNSpZVlnbks0zqKsq62H1
XKOK1f73u73UR0819ZHRR+37ulk92+BnMv9zHtk9BrX//XgXZdT+Z0myWQa1/718J2XU/udV
spkGtf85uZnVUw1+35FhsFYt7Os0g987+N9lkNFH7fsiVk8y+N1QRNs2snqyEbba/96HjD5q
38d1ccLgfPvrhevAZ4003ipl1KOU0UdO1ljZBGXUTZStUEbdVBnXKftgn81Tskcto/bXPT0+
a6E+6scM6pbK6PNZf2U8E+mlp3NKRh+Zf57yjCWj7qK+h61mW+bh71/uaTJq/zw4qoy6o7bl
2UTOs8U/13jWkVH75yTPTjJqvy0Z+6DuZHAd8Hwmo/bHwd8pzJn5dlXffVaTU/vvQcjoI+um
vm3KqP33Qzss4+84/m7rqz4yxiPz35dsV0bt97HHsv0Gf3/6v3/JGI+sp8Fx7FZG3UvZLmXU
dyljW/5OZyz/vcBO9dHj58f3dRwbx5CpbckeN6gHKqPHZ/7a4Hohox6gvjXKqEemZPSS3a1s
tdVk1P5e2KJt2ecg9W1WRj1Y2SZl1EOUrbOMnHpoSsb8yEakZBsto2dYSrbBMurhytZazbZs
548j1+XLf/xy+fKH9d7kxYffXt7xrcmfxl+XE/8SNVzxaYMVe6by1f2/JV9WXPFX4s/LK/+8
vPzPy/f8a00t/rmcUt5z8fKHbM6fX/o5ufyjkx37v+68t+Xa3cOyrm+5tkyptCXdCnQp02bd
JxXTri9wYbf75yY2O/dn06LtjR7ZUroxxaJkZF//97xM8L+G/381/3O/N6f0sKpuZVOy/27z
WflSEx77eWfnKuxeAJnWyLLyassvRf7PerXihhnJX1Ucsrlf+1mjeO037guv7HVfg7z958QM
599sF7G8VEBuGrfa+ZPpofgTrSo5X2ZznbjhvGVx+8z5Rdc2iXd84dM9KWPG5MPsA9/yy8du
oy85/n1h5oHXfFyP5qAeNwfntS/nNQfnNTf13xfzY3IcjMX4HAfHo32Zv8/ti2Nie3KOiXHx
HBP7w9t8g0ZBlX141smvVdWPT5TjM3LGs/06j/q11X7V4+bjvMZ3Xvt1XvNRv1sf51Nf2Zb6
mqoL/zaJX7VyR3hthTLZa2s0i9v/NMJt+K/qNomfzHkthu+T2ch6bonjnykcip88X915lJqc
z+nDsx3b4+1/lmEP4yoP+9z6g//qP1898OOYBn58+zzw+7XtAj8fGy+olb/qPsZU7uav/oBc
4zhv4zG+89pvMs95jfk4b6+cLMe4mifz9/0cVzJPHq/zzJdx6d98XRA/+UjN4J9tu7Nz3xCJ
N9hXK9j48YvZlsXtM5dbFrfPXP5py1vjH09o4vJO5crG98xs6vL5Bd+MzerQzOXDa74Ve75X
c5fbOSm3vX0LlzfJHFRub5+Wvj+c0h/2/TZ+kDJ+4MdnjinzCfx8yFLmH/j5MwZjcVyMYXN1
+2WfNtcwOfu0uYY5XuYYm3jdPnLmaK/u20eu/lhKf4xc48dTxo+Taz4uZ46sHbnm73LmyFqT
63hdzhxtri5njrZvlzNHm6vLeaWgzdXltrZ7bK6+n/X3/ay/H5/z5ceP+/F1fl2u8+v6bf5c
Dy5njn7+jMG51/HGOffMn31y7rU+cc49OXPktYLkzJF7k3ytvZr105a73Pr/Ur6FjbPbrX+3
21vGY2l7wrXKX8w+0bhVvOL7e8KD614TO5LV2o2DT31dXepr7PpNaBmvN+OdGD2pr7qruLq5
jXNbnDz1dXipr8l7vUSjeINFdVxP6qv0yPiMbVNft8d4jEue+ko+9s88yFNf28c54hjIU1/t
l/rKP9s27LdNfS2g7Svw+0p9dWDqKwVtnoGfZ+prBy0L/HGlvprQxgv8mqS+vjD1tYaprztM
fQ1i6usRU1+baHMP/PoPWtgsiKXdFuc8Xj+kRdCp+9sxd05TXrmY+ipGW5tg5emLe1mf1Nc1
pr7GUeO76yH1VY86loBtU18HmfqaSK2D60l9laTWzeWpr5vUmrs89ZWUOkcuT31t5f6tzcpx
DMwh9dWWqa+81LXhelJfi6lryeWpr87Utefy1Ndrcp6ZN/tKfXXpyOLR+OMbagess2ncauc5
D5wPcs4D5wPPc/j+Ea18Hva59Qe+n/H8OKgfX+fXbavz6+5ZxmuS+flexld/XPNhHOc1vvM2
H/brPM80297nzNP3M3/ndVzOMx414/N5yvUW99cb4/H8oef/63WW/hWWqa+2TH73+v/8nxPK
bR/kMa4Q+LwCz3fH/LnS8N9L4/mumBotIPAF5dGrDHoLGXwG+Kvl0cICf43AFxH4aw36ihp+
HLzfx3Xm/Rzw16tGixlkNxjUgL9RHi1u0HeT4cfBl1CN+mPHl1SN8rMGvaUMPgN8aXn0FoEv
I4/eKsoqo+82w4+D9/vgXDCHcka6wXkDPD+p4P1PLGadr4CxPyjnAfCcA8BXlEdZa8BXkkdZ
f8BXlkf9OcJXUY3684ivqhr15xpfTTXKuQR8dXmU8wt4riXA15BHObeArymPco4BX0se5XwD
vrY8yjUA+DryqL9m8LerRrleAF9XHuVaADzXAeDryaNcB4CvL4+WEfgG8qi/TvANVaNcN4DP
kEf99YYPqUa5ngAflke5xgDP9Qz4QB7l+gN8RB7l+QD4qDzqnyH4RqpR/5zBN1aNNhH4pvIo
v1oFfHN5tIXAt5RHWwl8a3m0jcC3lUfbCXx7ebSDwHeURzsJfGd5tIvAd5VHuwn8HfJod4G/
Ux7tIfA95dFeAt9bHu0j8HfJo30Fvp88minw/eXRAQJ/tzw6UOAHyaODBX6IPDpU4IfJo8MF
foQ8OlLgR8mjowV+jDw6VuDHyaPjBX6CPDpR4CfJo5MFPl0enSLwU+XRaQKfJY9ON+jF+z6y
GQI/Ux6dJfD3yKOz5dE5Aj9XHp0n8PfKo/MFfoE8ulDgF8mjiwV+iTy6VB5dJvDL5dEVAr9S
Hl0lj64W+DXy6FqBXyePrhf4DfLoRrFJGX34zarRLWKrMnrw21Sj9wn8dnm0j8D3Mthuh0Ef
4HfKo7sEfrc8ukce3Svw++TR/QJ/QB49KI/eL/APyKMPCvwhefSwwD8kjx4R+KPy6DGBf1ge
fUQePS7wJ+TRRwX+MXn0cYE/KY8+IfDZ8mg5I7dxhTw1nv50Y5JRXuAnyKMVBJ77nBqtKPA8
F6jRSgI/Sh6tLPAj5NEqAs9zihqtKvBD5NFqAj9IHq0u8HfLozUEnucsNVpT4PvJo7UE/i55
tLbA95ZH6wh8T3n0doG/Ux6tK/B3yKP1BL6rPFpf4DvLow0EvqM82lDg28ujGQLfVh4NCXxr
eTQs8C3l0UDgm8ujEYFvKo9GBb6xPNrI4BqMGf66xcdVo/46x+eoRv19gU+oRv19hD+lGj0m
8E/Ko0cE/rQ8eljgn5JHHxT4M/Lo/QL/tDzqnz/4Z1SjewX+WXl0l8Bvl0d5Lq411hvPCfx9
8mhfge9jrDbY5nmBZ1tqNFPg2XaFwTYvCDy91OgAgc80lhls86LA00uNDhR4tl1ssM1LAk8v
NTpY4Nl2ocE2Lws8vdToUIFn2/kG25wVeHqp0eECz7bzDLY5J/D0UqMjBZ5t5xhsc17g6aVG
Rws8284y2OYVgaeXGh0r8Gw7w2CbCwJPLzU6XuDZdprBNq8KPL3U6ESBZ9uYcYXRRDRTRo7n
HkNbyFPjc6St5Knx3GNoG3lq/ClpO3lq/JPSDvLUeO4xtJM8Nf4paRd5avwZaTd5ajz3GNpd
nhr/jNHL2G5wX5H1MMgBT47Sh59sTDH82uJZb3Iy1jbbOGGUE/jX5NF0gc8S+Nfl0ekCP1Pg
7xH4BfLovQb7PWmcEPjH5B8xZR+Af1gefUPgj8qjDxmHjAfkqfEHVaMH5FE/Dn6fanSP2K2M
PvybqlE/NzzHxuc7DWrA75BHlwv8Vnl0izy6UuA3y6ObxEZl9OE3qEZXCfwagV9nsO+lhp8b
folqlPkDfpE86s/TXPP+POJnGzzD/td/Zkf/2+smk6+VdK9r/DLl1ZOTDmYlhvbs6V7v+OO3
0xOREXNivHovWjYr0efnXHFe6/Zlyispv600NvHND3Nz2hcaE9mZOTqxOdf+nFFPV45Undo8
ka98kUS71zZGFuatnRjya60ErwK858EiiSk3NHf5qkUHcurePDpB/wNV5+dcfmdMgnFSX2G5
r1/e+LgyWe51imOm7IxN/TL5ekS9JtK92rJrz1HhrgeSr0F85MzS8PJvkj2ffvx7uG16ctvU
V15GH5oXeeqasW5fH0X3RZrNTc7hrnJFov2nJedW6s9a0QuXk3NuVKx5tMLh5LEUqzM62ibf
AXeMEy+Oid4z6l537KmvyKxSKiv6H3uNHWtV5Ovp0ZvstXesoV6X6db2voNZ0cP22kRedXfl
d9OjG+31efR8XTYr2tlesce2qa/U/KDs2OjGsvMirM/uEaOjXU7vi7BuG7OaR0+ULRJlnVtO
qB3tuaBWlHU+91CRaIHrm7v80rz9kc9aj47SX+iPeyMVPxkTZZzUV3AePpgvOHVL8vWCRevt
Cvf8MvkKRb021L2ac+uk4bFZB5KvSrw639LYgW+SPU93vBj7Pj25beorO7/4eF7Oofxj3b4e
a7Y/54dumsOtRRIvT0/OreiyWokNo2q7OV8o2jwx+WjyWK7I2z2RceMfkVXfzYmkvu4z9TWg
qa8KTX2FaOprRlNfP5r6WtLUV5emvtI09bWnqa9DTX1NauqrVFNfsZr6GtbU17OmvrZV95q7
BhqvyUoc7vK9uwZ6xqYmWl+cG+a1fXV3zkjsHFrQ/htieuT1JdMT31e7L7whEkTq956caH3V
PbHIn0sivbKzEiuuOB/jNYWprwXcelffxPs/bckZ9tFzkXd+6Ji484vCiYvDqkVq/Z6euKFi
eqJMvnOR198qkej3R3N7ZWmTyK0Htuc8MWFAgldbXqy5IuetFaPdfdGiX5H46XuT99TeZ6+O
/3H19ERWueaRYnl2xrYXTb6KNHxxTWx3LXut4GvDIlfm1A0veSX5GsRbfp0RftReucrrVr98
4KvwjyeSr1NMfc3ioHObI6+u7JtgnhsHF47++G9H99rnUtvSo7d/np646aWXI0evbRZtMPxm
9yrG/q/cHV1UYUdO7KsH/ttrH1NfB2lPwKh/9ulVle61kp/Zq0Fz2z3IK2gfD2VF19grKbm/
uteeHn3FXlXJcfV+bHJ0od2DvOq0xgm7f+3VlqzthRZZ0a52P/Ia2dRXYV71113RCz9sjlzq
/mLk42OdonX/vtrdX32LlY+eH5EeZf4TzpWMHrm6eZTxN1+xIzJr94Bo43rHIgNarIx0HzTa
3Rclil8b9Lg3eU/NqlkoeKTG9Cjn5dVe+8MNYlOii3fOjtz70LJwyYzk/bWoWGbslPUw5gO3
L4k1CaZEf5h3b6TZtb/E7L2uUa6T1NeJZvbbkjP7y7uizPPzF65OLD7aKcr18Pfx9ESfl5Lz
XJHePBE5VtKNWXDHwES9fYsjtWOPR9b8PSbxXsN73TOnXcaIRPVpByK8ltSvsa13IpcV/yeS
2+aVx0CvEHlN8xlXGvmNAkZB4yqjkHG1Udi4xihiXGsUNa4zrjeKGTcYNxrFjZuMEkZJ42aj
lFHauMUoY9xqlDVuM/geLt0ob1QwKhqVjMpGFaOqUc2obtQwahq1jNpGHeN2o65Rz6hvNDAa
GhlGSIRNIRD0AycMuDmAfUAj0dgUmgjmCE1FM1PguKC5aGEKLQXrAq1Ea1NgLaGNaGsKfM8O
nAtoL/z56mC1h6yj0cnobHQxuhp+227m7zC6G3cafK/d0+hl9Db6GHcZfY1+RqbR3/BzHmD+
bmOgMcgYbAwxhhrDjOECzxqUkfo18TrC8pHGKGO0McYYa4wzWNPxxgRjojHJmGxMMaYa04ws
Y7oxw+D79VnGPQbncbYxx5hrzDPuNeYbC4yFBmvFOoFfS78+fq392vtz4c+NP1etbFvw6+LP
LecZ/Ln3x9vMMvDXCscI/lriuoJGoropRIW/Njk+8Neuv5a5tr33n/lev60fy4/dyLYBv28/
Fz83P1c/d39MXjnOVPwaePVr49WvmVe/ll79Gnv1a+/VnxOv/lx5zW/zScWfW6//O9Yo9Zzi
r0hhkfn/W+H/K8fc3PYz/qNPB689tixYtm2+vc5qfjB55JngverHHQ2GnAmeeut0sOPzk8Fr
hRMO/L2vng7OdXgm2DynjduO11ltMNBiy9oE1+a6MlQo/Ht4Uu4SIcbHM+67idphxi7ZrmmI
cVaenhRi3NtnPxZiP2c/vCLMXNjuLeul76NfmobYbrZljHOqQN4w29W0bdguc/jkENt9dPDK
EPNhHhwH81jV+hl3bE/ZHNiesRmPOTA+x8f2zIXxmAvjc3zsi+12FWnM7ZU2pH8Npxk9opEN
5dPDZ16tEvno5O+hR7dVcXWdj290NcrnHSpe4XTPmj8D+ta9/VFA3v+fD129ttS7rn6+51uu
3vbH664eGr3gauZC/4GHYq5mjtTXXHXC1RwD9cuTtiT77dioOW72h1JzHGiZnqfC5Bw3daMP
qria46X+6I33Q3zOOrj65BRXbyiQnMew+5PzeCVvcv/bKyX3v3Jscv8bHk7un3PAOO5c2LjX
V0juv2Kz5P6/Wp/cf6fjyf2ft3PH/tLmJfffqWpy/2WKJve/6elmbh0/WdPUre8/NZu4+sRT
UVdvuyN5PiZNru3q4luS52PdB8nzgTL+kfTk+Ri0PHk+ur+WPB+3XUqej6Xdkueh76/J81A5
I3ke6j2X3P+c9cn9b6uT3P+Nhcn3hQa0aWb7nRKq9eh5O+4poby3v2Lrvi/U9+43nT73zRsu
/7Hkh65+4/AHrt705x+urn3sD1cn57kvlJz3lNB7idpu/BWfcVxTQmdrNXL1e0MbuXrqVcn9
P9Uyuf+0tS3sfE0JNbrY3c7fvlCjsWedfvTFMy4/eqGcrfO+0Ff9b7XzPiX066W4q/u8GnN1
8nztc+eNz/vk2ermd7rdVje/Kz454erSnR519fotcVdXuS7H1acyWrr9lDmT3O+pjGddzetA
2e9bS5P7/e7qHFd3+yq53+R1us9dr+x3S/7kfu1ViG7cpl8m99vnjuR+X9uR3O/w4sn9jslO
rnvThsl1v29oct2v/Cm57tVvTa779Y8k1/2Ny8l1H/toct2T9+u+UPL+nRI6X7CqW+f9Faq6
dX6/MXV66JG+Ls9Qf8Yzf5R0z4ORD+dzuuc2N27GU9t/46/nNLufWJ+MZ4e+7+pH33jT6Tv/
cn3ty7h6xQVXtzlxztXJ+2xfRpvpT7n8i7I5TlfVesx9/sCOx1x99jO3PhlZXVe7WuuXMXZz
V1dnvpzLaZn7nmCdMxr88iDfNqQ1eKCEq8c2vNHVP/3zGn9dppV5jfttX8apG+a6+qNSFVzd
4wru+30ZvJaTvjV9kvPpUjU5nxFbkvPhOcTnRd952GnjLcec7ixxxOmNVR5wuvLD5Lwb5Dxq
46aHKm2gTg/9m7nTfT6eVwnaH12HGUP+097VZ+zVhuQVFyWPp2L0fle3mp08ntnXJI8nc9cb
yfmfnpM8rsnl3XFcOu3uk4yjeVq68zTrzmZOf3vD3U8ZuQsnn+8Xq9XhvGcUrFPNfa77MaPt
0eKu3v1DHqcDSyfP86K7k+d19yvJ83zk2+T5TT7Hbd32JM9voaPJ8/tD/uT+b+6V3P/hBe65
Eipd57xbh9rj33Aai37g9MUh7CfdPQ/QJgWYX3roqx3MOz1U+N7k9jtr1rPjTA/NvivhtPjP
pew8p4dOHc52qudw6MmlOW68zGPJvtlvJbfLX7K063v8dLJff2+EhmxNnp/JTyXPV9rq5Pbj
piTn2adBct5/NkvOt8Co5Hz191+o7qZngp21cwKu2wUrn3Pcb75IroVBx3wLg22J54O6jdfZ
9xAvBF9+2svlvWrkC+LFXwh4hfWlsc8HByYeDbPtKLtmGWfuwekZ3Bcj7RWX1TJPB01XPRXM
uzEe5K7ybPBD+vKg4K/PBw2bt3Svky7+XT63nxkTvwnzumiue8Ya2/RpN7fMrH6hEYNOB40u
vpHBGLNtbOaX9nLRjHO17JrsvKhhxWuWumvwxSItA8aruymffb6m4fZNF8P0jZh7MMz99VG1
Ihmz74pm5O81J5zWvVvGC/V7h9kf8519oW9GPKNlOO3o4Ix64SCc9sOIjG/s70D2x3FxH375
6Tvu/lt8oW8o017LOb7T6RD3sW3fkPv8nTyHG/JcCD07O7SgzLOBvULYXeP2LZz7ud6+jXO/
e8ijGvXfp+LzCnw+gz9XGmwPeL6vxqMFBL6gPHqVQW8hg88Af7U8Wljg+f0B4P33/Hh+n0Af
v1Pw4+D9Pvg9g58Dnt85UKPFDDJ+/0ANeH4GwaP8ToI+fi/hx8HzOwpq1B87vqRq9GaD3lIG
nwG+tDzqf+bDl1GN3irKKqPvNsOPg/f74Fwwh3JGuuF/JsNXUI1WFPhK8mhlga8i8FXl0WoC
z8+E1GgNga8pj/J7FsDXNuoYtxv+50x8PdVofYHn9zDUaEOBz5BHuWgBz0Mc8NxkeJSHLOD5
eRaPNhL4xvJoE4FvavAzGj+/+jnj+RmWGm0p8K3k0dYC30Ye9T+L4tsJfHt5tIPAd5RHOwl8
Z3m0i8B3NboZdxjdBf5OebSHwPeUR3sJfG95tI/A3yXwfeXRfgKfKY/6awPfXzU6QODvNgYa
g4zBAj9EHh1qDDOGGyPk0ZECP0oeHS3wY+TRsQI/Th4dL/AT5NGJAj9JHp0s8FPk0anGNCPL
mC6PzhD4mfLoLIG/Rx6dLfBz5NG5Aj9PHr1X4OfLowsEfqE8ushYbDDPJfLoUoFfJo8uF/gV
8uhKgV8lj64W+DXy6FqBXyePrhf4DfLoRmOTsdnYIo9uFfht8uh9Ar9dHt0h8Dvl0V0Cv1se
3SPw6fLoXoHfJ4/uF/gD8uhBg1687yO7X+AfkEcfFPhD8uhhefQhgT8ijx41jhkPG4/Io8cF
/oQ8+qjAPyaPPi7wJ+XRJ+TRbIGPyaNxgc+RRxPy6CmBf1IePW08ZZwxnpZHnxH4Z+XR58Tz
yujDv6AafVG8pIwe/Muq0bMCf04eXSDw3F9sd96gD/CvyKMXBP5VefQ1efR1gX9DHn1T4N+S
R9+WR08J/Dvy6LvGe8b7xgfy6IcC/5E8+rHAfyKPfirwn8mjn8ujXwj8l/LoVwL/tTz6jcB/
K49+ZzDn740f5NFyRnljsDw1nt50Y7dRQeB3yqOVBH67PFpV4LfJo9UFfos8WlPgN8ujtY3b
jQ3GOnm0nsDzXKNGGwj8Knk0Q+BXyKOBwC+TR6MCv0QebSzwWfJoU6O5sdCYL4+2EPh58mgr
gZ8jj7YR+Hvk0fYCP1Me7Sjw/D1HjXYWeOZHjXY17jCmGJPk0TsFfoI82lPgx8mjvQV+jDza
V+BHyaOZAj9CHu0v8MPl0bsNrsEfDa7D74yfjJ/l0W8E/j/yqL8v8L+oRr8Q+F/l0U8F/qI8
+rHA/yaPfijwv8ujzPNd45Lxhzx6SuD/lEffFPi/5NHXBf5vefSCwJ+TR182njKeMf4R+LPy
6CKBX2CcMk4b/wr8ZXl0qcAvNuLGKcP/0IVnW2p0ucCzbbbBNrnsc8DTi0dXmgCebR832Ca3
1YCnF4+uthrwbPeowTZ5rAY8vXh0rdWAZ7vjBttcYTXg6cWj660GPNsdM9gmr9WApxePbrQa
8Gz3kHHUyGc14K+UR7daDfhNpg8abJPfasCzHR69z2rAs939BtsUsBrw9OLRHVYDnu32G2xT
0GrA04tHd1kNeLb70RhsDDWGGSMN7jfA/ywdLU+N5x5Dx8pT47nH0PHy1HjuMXSiPDX+onSy
PDX+N+lUeWo899s0Y4ZxSeC5x9BZ8tR47jF0tjw1/i/jXuOcwX0125hrkAOeHKUPv8fYa/i1
xbPe5GSs61WmhYyrBb6wPHqNwBcR+Gvl0aICf53AXy/w/E8MUqP8zwiy3xsN9gd4/icC8TcZ
7APwJeRR/if+AM//tB8eLWWUNm6Rp8aXUY3eKo/6cfBlVaO3iXLK6MOnq0b93PAcG5+XN6gB
X0EerSjwleTRyvJoFYGvKo9WE9WV0YevoRrlf44P8LUEnv8dJvZdx/Bzw5+0806NMn/A3y6P
+vNU17w/j/h6Bn8k7vd9djVGqXO7T/xns6OUPqvoPkv25TFPf7oyenyW7E++6vUKy/1n7APv
s4+1LdvlNVA+ow/1WSaRZXyez+CzPgYZPT7rqwy50uCzyhTWx1x9Rj8ZdX6DuqDh+3zG52TU
BQzf7/t8VoI29TEO/dcSWUaPz/Bk1FcZ1BmG7/NZUWXsr5BBfxVljO0z+tmW+mqDuppBRp/P
+JyMurDh+32fz4rQpr5rzPl+Mnp8Vpc29bGN/4yMHp/VoU19rAef1SCyjB6f1VLGOBw7n9VX
xnH4zK8p60FG3dBgvP/B3psAynaVVcIVEgYjyBQEFSQoo8BhD2efvTcGeBfCPIZJJiUJhDCE
KQnzFGYIo4DITBhlUEQc2hkcUFpt21n//v37p1vbRtsBFREVSK+1zz6keHkvuedS975dVSvw
3apvvW+f2lW16qz97ZHv/dow4qfAiPHznTA+EuPjSTA+Xgc2xU0YH4nxkf/Ox7vAprgJu17F
eJ1vhRG/fcVYZsL4yLJ8vC6Mj4dg02tMGB+J8ZHX5uMdYVPchJ1aMb7et8GI361ifL8TxkeW
5SP5yccbwIgxbsIm7vL3wee074AxbnpO/8YVYxx92vUrNj2n/5CKMY4+7SYVm+rAety9YnwN
+rTvrNj0nP49K8Y4+rQbVmx6Tv/kijGOPu27K8a4k6vdu2JTGeI3qtj0nP59K8Y4+rTvqtj0
nP5pFWMcfdoDljDWgfagirF+EzZ9pvz8iNH/Phg/++Pxd/rsHlYx/js/y5vCXnAcwfF+OmE3
I1QxxjLufxACthzzFxW7Ah4Zw3I3rxgfiNG/BR2UnWLo/6+K8YHliH0PHcTxfkWM/i1hxHiv
IUb/VjBi9Hl9+v8bNsVN2K0rxvsPMfpdxaZ60f/rijGO9SA23V94byBG38D4GlNd6f+fijGO
9SVmK8b7DzH6rmLTe6L/dxVjHN8XMV+xq1eMfl+x6b3T/4eKMY7vn1ioGO9/xOgPFaPP90//
HyvGuAmLFeN9jxj9VDH6/Ezo/3PFGDdhuWInVoz+bSv2zRWj/70VYzl+nvT/pWKMm7BTKnbt
itG/XcUYw8+Y/r9WjHETdvuK8f5IjP4dKkaf3wX9f6sY4ybsUMWuWzH6OxWbvkP6/1ExxvE7
I3bHivE+Soz+nSpGn98j/a9UjHETdmrFeL8nRv/OFaPP75b+xRVj3ITdpWLXqRj9u1aMMeQA
/eOOIzgeCz5hdyMEjPdTYvTvDiPGeycx+veAEaNP/tBnzjnFTdg9CSGO90li9O8FI0afnKJ/
xVqWcRN2bzxn3Mn4S4z+fWDE6JN79K9cy568hN0Xzxl3o4rRvx8hYCxHPtJn3jjFTdhphBDH
+y0x+veHEaNP3tJnjjLFTdgDCCGO92xi9B8IIzbxnT7zqSmOnCf2IEKI+278JUb/wTBi9Ml5
+levZRk3Yd+H54z7jorRfwghYNfHX8bRfyiMGH3+XuizfT/FTdjDCCHuePwlRv/hMGL0+Rui
z3xuipuwRxBC3JXwlxj974cRo8/fGn3mEFPchP0AIcRdEX+J0X8kjBj9QzD6zAenuEN4Rux0
GLET8PcQ7HTYGTBih/B3B0Z/Ksu4CTsTzxlH/44w+o+CTdebsDOOGzHG3QnGGOarjGPMhD2a
EDD6/O3SPws2xU3YmbUs4/h7ZgzzKcYxZsIeQwgYff6e6Z8Nm+Im7NG1LOP4G2cM82/GMWbC
HksIGH3+xuk/DjbFTdhjalnG8XfPGOb5jGPMhD2eEDD6vBfQfwJsipuwx9ayjOO9gDHMlxnH
mAk7hxAw+rw/0H8ibIqbsMfXsozj/YEx7CNgHGMm7EmEgNHnPYP+k2FT3ISdU8syjvcMxpxY
McZM2FPwnGXp8z5C/6kwYoybsCfVsozjfYQx7NtiHGMm7FxCwOjz3kL/PNgUN2FPqWUZx3sL
Y9i3xjjGTNj5hIDR572F/tNgU9yEnVvLMo73G8acUDHGTNjT8Zxl6fMeRP8ZMGKMm7Dza1nG
8R7EmCtUjDET9kw8Z1n6vC/RfxaMGOMm7Bm1LON4ryoxFWPMhD0bz1mWPu9V9J8DI8a4CXtW
Lcs43r8Y81UY4xgzYc+tGH3ev+g/r2KMm7BfrRjjeE9jzJcrxpgJe37F6POeRv8FFWPchLFv
hXVhHO9pjPl3GDHGTNgFhIDRP53PYC+ETXGn8xmMRyJMcWfgGWO+RAhlT8ffCXsRIWD0z4TR
fzFsipuwU44bMcY9CsaYLxJCWcZM2EsqRv/RMPovrRjjJuxQvR7jzqoxX6hxjJmwl1WMPu99
9F9eMcZN2Kn1eow7u8b8U41jzIS9omL0ee+j/8qKMW7C7lavx7jH1ZjP1zjGTNiFFaPPex/9
V1WMcRN2r3o9xj2hxvx9jWPMhL26YvR576P/mooxbsLuV6/HuCfWmL+tcYyZsNdWjP6TYPRf
VzHGTdgD6/UY9+Qa8zc1jjET9vqK0X8KjP4PVoxxE8ZjDcgNxj0VxpjPwYgxZsLeUDH658Lo
v7FijJuwR9TrMe68GvNXNY4xE/amitE/H0b/hyrGuAk7vV6PcU+rMX9Z4xgzYW+uGP2nw+j/
cMUYN2HPrde7CTDGMuYvYHy/xBhH7C2wCXtG9d9aMcZM2LOXrvdM4Ix5Z41jzIS9rWL0nwWj
//aKMW7CnlOvx7hn15jpeoyZsHfgOetH/zkw+i+qZRk3Ye/C8+l9MJbXuqDGMea5MMa8G8Y4
lp0wHlFBjHHPgzHmxRVjzIRdhOeMo/982EWw98CIMW7CHlrLMu4FMMa8pGKMmbD34jnL0r8A
Rv+jS3ET9j7gjKP/Qhj998OI8XoT9qBa9gJgL4IxZroeYybsA3jOsvRfDKP/QRgxxk3YafV6
jHsJjDEfqRhjJuxH8Jxl6b8URv9DMGKMm7B717KMexmMMS+rGGMm7MN4zrL0Xw6j/xEYMcZN
2N1rWca9AsaYD1eMMRP2UTxnWfqvhNH/URgxxk3YnWtZxl0IY8yHKsaYCfsxPGdZ+q+C0f/g
UtyEfQw44+i/Gkb/x2HEeL0J26llGfcaGGM+UDHGTNjH8Zxl6b8WRv8nYMQYN2G3q2UZ9zoY
Y95ZMcZM2CfwnGXpvx5G/71LcRP2k8AZR/8HYfR/CkaM15uwXMsy7g0wxryvYoyZsJ/Gc5al
/0YY/Z+BEWPchHEcZ4p7E54x5v0VY8yE/Sc8Zxz9H4LR/1kYMcZNmK1lGfdmGGOm6zFmwn4O
z1mW/g/D6L+nlmXchP08njOO/ltg9C9aipuwXwDOOPpvhdF/91LchP0icMbRfxuM/ruW4ibs
l4Azjv7bYfTfsRQ3Yb8MnHH03wGj/2swYnwfE/bJitF/J4z+p2BT3IRxnI4Y494F+xSM43nE
GDNhv0II2CMqRv9XCVWMscSmNubD8JxlGfP0ej3W+d0w1vftFePrTtiv4zmvR/8iGP23LsVN
2KeBM47+e2D0fwNGjNebsOl9XATsvTDGvKVejzET9pt4zrL03wej/6aluAn7DHDG0X8/jP5/
hhHj9SaMY6RT3AfwjDFvrBhjJuy38Jxx9D8Io//bMGKMmzCOxU5xP4JnjHlDxRgzYb+D54yj
/yEY/dcvxU3YfwHOOPofhtH/XRgxXm/COB48xX0EzxjzuooxZsL+K54zjv5HYfR/D0aMcRN2
81qWcT8KY8xrK8aYCft9PGdZ+j8Go/8HMGKMm7Cb1rKM+xiMMdP1GDNhf4jnLEv/x2H0/whG
jHETduN6PcZ9HMaY11SMMRP2x3jOsvR/Akb/T2DEGDdh31XLMu4TMMa8umKMmbA/xXOWpf+T
MPoXLsVN2J8BZxz9n4LR/39gxHi9CTu5lmXcT8MY88qKMWbC/huesyz9n4HR/39hxBg3YZzb
MMX9JzxjzCsqxpgJ+3M8Zxz9n4XR//9gxBg3YdevZRn3czDGTNdjzIT9dzxnWfo/D6P//8OI
MW7COB9jivsFPGPMyyvGmAn7LJ4z7sb4S+yzsOfVOGKMJfY/YYw7AX+J/w/YMsY4+pwzwrib
4u/TYH8B+0vYhJ1X/f9VsZvhkRj9v1rCnlr9/12xm+ORGP3PLWFPrv5fV+wWeCRG/2+WsCdW
//9U7HvwSIz+3y5hT6j+31XslngkRv/vl7DHVf8fKnYrPBKj//kl7Ozq/2PFbo1HYvT/aQk7
q/r/XLEOj8Tof2EJe1T1/6Vit8EjMfpfXMLOqP6/VszgkRj9Ly1hj6z+v1XM4pEY/X9fwr6/
+v9RMYdHYvS/vIQ9vPpfqZjHIzH6X13CHlr9iyvW45FY8SuHiH0f/x3+NHYSKkZ/6uci9iAY
/eNr2aFi9E9Ywh4AnP4VKxbhE6N/pSXsNGD0p7GOBJ8Y/avUOGL3hdGfxjVyxehP/ZjE7g2j
P41h3LZi9K8K4++D2D1h9Kfxiu+tGP1vqXHE7g6jP41NnFIx+teoccTuCqM/jTncrmL0p35q
YneG0Z/GF25fMfonwVg/YneC0Z/GEu5QMfpTvzyxHRj95b7/XwTG+8MZMF6P94wJ+7aK0f8l
GP1HLcVN2HRf472OGH3OCeP16P8yjP5ZFWPchE33WN53idG/QY2j/0kY/bMrxrgJm+731ABi
9G9Y4+h/Ckb/cRVj3IRN2vMTFaN/oxrHmF+B0X9CxRg3YZNe/njF6H93jWPMr8LoP7FijJuw
Sbt/rGL0b1LjGPNrMPpPrhjjJuymFftoxejfrGKM+XUY/acuxU3YzSv24RpH/xYVY8ynYfTP
W4qbsKl99cEaR/+WNY4xvwGj/7SKMW7Cpjbh+ytG/9Y1jjG/CaP/zIoxbsK6ir2nYvRvU7F3
VYz+1G4nxlhiU5v6h+B/Bsb8a8oh3riEDcDJ03dWjDG+Yj8AjDj9KV8gxusRSzWO1/vPMOaM
0/V+cAm7bY1jOcYxJlbsdPjE6U/XI8Y4YqfUOF7vt2DMc6frvXYJu32NYznGMeZ7K3YmfOL0
p+sRYxyxQzWO1/tt2O3gT9d79RJ2xxrHcoxjzB0q9mj4xOlP1yPGOGKn1jhe73dgO/Cn671y
CbtLjWM5xjHmThV7DHzi9KfrEWMcsbvVOF7vv8DuDH+63suXsHvUOJZjHGPuWrHHwidOf7oe
McYRu1eN4/V+F3Z3+NP1XrqE3afGsRzjGHPPij0ePnH60/WIMY7Y/Wocr/dfYfeGP13vxUvY
/WscyzGOMfet2DnwidOfrkeMccQeWON4vd+DnQZ/ut4Ll7AH1ziWYxxjHlCxJ8EnTn+6HjHG
EXtIjXsh/N+HPQj+dL3nL2EPq3EsxzjGfF/FngKfOP3pesQYR+wRNY7X+wPYQ+FP13vuEvYD
NY7lGMeYh1fsXPjE6U/XI8Y4YqfXOF7vD2HfD3+63rOWsOfUOJZjHGMeWbHz4ROnP12PGOOI
PbfG3RE+9ZZ6fGbFTq0Y/UctYdRW+o+u2F3gE6N/1hL2y8DoP6Zid4NPjP7ZSxg1k/5jK3YP
+MToTxpK7FMw+o+vcfeqGP0nLGG/Apz+ORW7D3xi9CdtJEbdo/+kGne/itF/8hJGjaP/lIrd
Hz4x+pPmEft1GP1za9wDK0b/vCWM2kX//Io9GD4x+pOWEfsNGP1n1LiHwadGPR3+syr2kBrH
mGcuYYyjP8U9Az6/82cDm/jy9CVs4sFPA/sF2PMQ9/J6vRvDJ07s+RWj/0cw+q9cipuwF1Ts
JjWO/gUVe3bF6L+wYiz3xzD6P7wUN2Evqthzahz9F1fseRWj/5KKvaBi9F9asZdVjP6Hl+KI
E3vZEvYSYPQ/UjG+35+D8TN5RcV+Ej7rzfd/YcU+UTH6r1rC/gQ4/VdXjOUm7M0V+3jFGPOa
in2sYvR/sGIfAUb8tfBfV7EPVYz+6yv2IxWjP5Ulxtel/4Ya94GK0X9jxd5XMfpvqth7K0b/
h5awPwVO/y0V4/UnbHpvfL/E6E/fL79bYvR/pJa9qGK81lsr9u6K0X9bxV4DjDj9ty9hvB6x
DyxhbwfGmHcsYW8DRv+dFXsdy8Hov2sJeysw+u9ewt4CjP5FS9gPA6P/niXszcDov7dir4dP
jP77KvaGitF/f8VeBYzvg+/hgxW7sGL0p8+KGD9D+h+qca+oGP1ljr8IOLn80Rp33Al/vbjf
CX9w2kWfOe6iq/zBe7/8uov/9WL+Hyeof5VHpuP//3Hxu9978wsv9f8vfPXifywnqOPvC77y
yfeixPgfntzg06dd/zdPu/5dn8r/f5r/P+k3X/sXNx8Pa//Yhy78yM0v/Aj+lv+/90MXfted
TzuJ/3/pmTd/0Ql3v/lrT37Qi05aXPPG97jmX1/l/lc9CTWe/jvnve8/9Ku/faMd+nyH43+X
nIQ+IUd+3L+4Gxz5BY+CXgn4eAL7GLB/9TpKBSo8vu414F188eeOv9riAc964plPPufUc894
xuOedPbTf8sWijA5+Zc/uvbtP/zOm96ez69Ygk+swXc541FnHc/LXczlM5//4n1+6fHv+Hm2
Hxb/8PJzTll+ftEd/vi2h+OIv90Uw+dnvu0+t2MMrzM9p3/iBXwNvASW3iy/Bur1Sz/6zzdk
m2Pxz2f9xC8+9i475fk/vPxvf+ETb7vP9Px7p+eIOWWKQdnbTWWX68Frja/HF7xiue7n3vWG
U6bX+MLf/kN5/qp8u19cfv7Bu9661J31mJ5//bWuQHcxXYvPjxx35QWufcoUx+fT67D+R8OX
Y6brsuz0nK83/Xfi9KQ8Xnzx3x1/wuJO93rwPfmF42f/df96lSXvpf/ytkO0JQiUsGwfLn7m
n79yykf+cdzk7HD/scdRNi+4w2inl59vJRdDd/HfuMDrkkBea3EI/4ddALsI9inYZ2ELXP8a
sJNhBnYIdj8YX/cpsAtgr4C9HvYW2EWwD8E+DvtZ2Kdgn4H9HuzPYJ+FfQ72ediXYJybegLs
KrCrwq4BOwl2Pdj1YSfDbgy7OexWMAPrYQl2CuwQ7FTY3WD3gt0P9kDYQ2CPgJ0OezTssbBz
YE+BnQ97Juy5sAtgL4K9BPYy2CtgF8JeDXst7PWwN8DeBHsz7C2wt8HeAXsX7CLYe2Hvh30Q
9iHYR2A/CvsY7OOwT8B+CvYzsJ+F/TzsF2G/DPsU7Fdhvw77DdhnYL8F+x3Y78J+D/YHsD+C
/Qnsz2D/DfbnsP8O+yzsf8L+EvZXsM/B/gb2t7C/h30e9k+wL8C+CPsS7N9hX4Z9Fcb+xuNg
V4AdDzsBdkXYlWBXhl0F9k2wE2HfDLsq7Gqwb4FdHXYN2DVh14JdG3YS7Dqwb4VdF3Y92LfB
vh32HbDrw24A+07YDWEnw24E+y7Yd8NuDLsJ7Kawm8FuDrsF7Htgt4TdCnZrWAe7DczALMzB
PKyHBdgAi7AEy7Dbwr4XdgrsdrDbwziX+RBsB3ZH2J1gp8LuDLsL7K6wu8HuDrsH7J6we8Hu
DbsP7L6w+8FOg90f9gDYA2EPgj0Y9n2wh8AeCnsY7OGwR8C+H/YDsEfCToedATsT9ijYo2Fn
wR4DOxv2WNjjYI+HPQF2DuyJsCfBngx7CuypsHNh58HOhz0N9nTYM2DPhD0L9mzYc2DPhT0P
9nzYC2AX3GlxAWzxQjzCFi/CI2zxYjzCFi/BI2zxUjzCFi/DI2zxcjzCFq/AI2zxSjzCFhfi
EbZ4FR5hi1fjEbZ4DR5hi9fiEbZ4HR5hi9fjEbb4QTzCFm/AI2zxRjzCFm/CI2zxQ3iELd6M
R9jih/EIW7wFj7DFW/EIW7wNj7DF2/EIW7wDj7DFO/EIW7wLj7DFu/EIW1yER9jiPXiELd6L
R9jifXiELd6PR9jiA3iELT6IR9jiR/AIW3wIj7DFh/EIW3wEj7DFR/EIW/woHmGLH8MjbPEx
PMIWP45H2OLjeIQtfgKPsMUn8Ahb/CQeYeU/3Z91f74CuHA87ATYFWFXgl0ZdhXYN8FOhH0z
7Kqwq8G+BXZ12DVg14RdC3Zt2Emw68C+FXZd2PVg3wb7dth3wK4PuwHsO2E3hJ0MuxHsu2Df
Dbsx7Cawm8JuBrs57Baw74HdEnYr2K1hHew2MAOzMAfzsB526s4Hrnzqzpu/89SdPz/11J2X
PfvUnY988tSdM0+6887vPfPOO9f/uzvvnPfUu+xc9Up33bnRR++688XT77bzJze7+861FvfY
ueLf3GPnmn91z533fOFeO7f81vvs3Pqe9925zZvut/Ppfzxt53WPfsBO+rsH7jzz1Q/eue6d
HrLzN9d82M6f/tvDd/7kP74f7YzTv85u+8BH7OS3PHjnLcNpO391s3vtXHDWXXee+dd33Hnu
x26/82s/ftudL39u2Dn0YL9zlS/cZucGn7zVzpt+6hY7v/77N925/Uk33vnMs26085DFDXeu
/sHr7/SP+/Yde7fr7bxu51t3vviAk3Zu+vxr7Xzpl6+x8/DrXH3ntAuutvP5r37zziNef+LO
7/hv2nnx566884c/dqWd6734iju/cPYJO/bhx+984RFX2HnNOcftXPjKxc7xZ1986CZ/9JVD
n37olw+d8q//fujvP/pvh+79jC8dGu8B+tv2JyBOi9NtM3R+7cRpcXo+a9ouIU6L020zdH7t
xGlxej5r2i4hTovTbTN0fu3EaXF6PmvaLiFOi9NtM3R+7cRpcXo+a9ouIU6L020zdH7txGlx
ej5r2i4hTovTbTN0fu3EaXF6PmvaLiFOi9NtM3R+7cRpcXo+a9ouIU6L020zdH7txGlxej5r
2i4hTovTbTN0fu3EaXF6PmvaLiFOi9NtM3R+7cRpcXo+a9ouIU6L020zdH7txGlxej5r2i4h
TovTbTN0fu3EaXF6PmvaLiFOi9NtM3R+7cRpcXo+a9ouIU6L020zdH7txGlxej5r2i4hTovT
bTN0fu3EaXF6PmvaLiFOi9NtM3R+7cRpcXo+a9ouIU6L020zdH7txGlxej5r2i4hTovTbTN0
fu3EaXF6PmvaLiFOi9NtM3R+7cRpcXo+a9ouIU6L020zdH7txGlxej5r2i4hTovTbTN0fu3E
aXF6PmvaLiFOi9NtM3R+7cRpcXo+a9ouIU6L020zdH7txGlxej5r2i4hTovTbTN0fu3EaXF6
PmvaLiFOi9NtM3R+7cRpcXo+a9ouIU6L020zdH7txGlxej5r2i4hTovTbTN0fu3EaXF6Pmva
LiFOi9NtM3R+7cRpcXo+a9ouIU6L020zdH7txGlxej5r2i4hTovTbTN0fu3EaXF6PmvaLiFO
i9NtM3R+7cRpcXo+a9ouIU6L020zdH7txGlxej5r2i4hTovTbTN0fu3EaXF6PmvaLiFOi9Nt
M3R+7cRpcXo+a9ouIU6L020zdH7txGlxej5r2i4hTovTbTN0fu3EaXF6PmvaLiFOi9NtM3R+
7cRpcXo+a9ouIU6L020zdH7txGlxej5r2i4hTovTbTN0fu3EaXF6PmvaLiFOi9NtM3R+7cRp
cXo+a9ouIU6L020zdH7txGlxej5r2i4hTovTbTN0fu3EaXF6PmvaLiFOi9NtM3R+7cRpcXo+
a9ouIU6L020zdH7txGlxej5r2i4hTovTbTN0fu3EaXF6PmvaLiFOi9NtM3R+7cRpcXo+a9ou
IU6L020zdH7txGlxej5r2i4hTovTbTN0fu3EaXF6PmvaLiFOi9NtM3R+7cRpcXo+a9ouIU6L
020zdH7txGlxej5r2i4hTovTbTN0fu3EaXF6PmvaLiFOi9NtM3R+7cRpcXo+a9ouIU6L020z
dH7txGlxej5r2i4hTovTbTN0fu3EaXF6PmvaLiFOi9NtM3R+7cRpcXo+a9ouIU6L020zdH7t
xGlxej5r2i4hTovTbTN0fu3EaXF6PmvaLiFOi9NtM3R+7cRpcXo+a9ouIU6L020zdH7txGlx
ej5r2i4hTovTbTN0fu3EaXF6PmvaLiFOi9NtM3R+7cRpcXo+a9ouIU6L020zdH7txGlxej5r
2i4hTovTbTN0fu3EaXF6PmvaLiFOi9NtM3R+7cRpcXo+a9ouIU6L020zdH7txGlxej5r2i4h
TovTbTN0fu3EaXF6PmvaLiFOi9NtM3R+7cRpcXo+a9ouIU6L020zdH7txGlxej5r2i4hTovT
bTN0fu3EaXF6PmvaLiFOi9NtM3R+7cRpcXo+a9ouIU6L020zdH7txGlxej5r2i4hTovTbTN0
fu3EaXF6PmvaLiFOi9NtM3R+7cRpcXo+a9ouIU6L020zdH7txGlxej5r2i4hTovTbTN0fu3E
aXF6PmvaLiFOi9NtM3R+7cRpcXo+a9ouIU6L020zdH7txGlxej5r2i4hTovTbTN0fu3EaXF6
PmvaLiFOi9NtM3R+7cRpcXo+a9ouIU6L020zdH7txGlxej5r2i4hTovTbTN0fu3EaXF6Pmva
LiFOi9NtM3R+7cRpcXo+a9ouIU6L020zdH7txGlxej5r2i4hTovTbTN0fu3EaXF6PmvaLiFO
i9NtM3R+7cRpcXo+a9ouIU6L020zdH7txGlxej5r2i4hTovTbTN0fu3EaXF6PmvaLiFOi9Nt
M3R+7cRpcXo+a9ouIU6L020zdH7txGlxej5r2i4hTovTbTN0fu3EaXF6PmvaLiFOi9NtM3R+
7cRpcXo+a9ouIU6L020zdH7txGlxej5r2i4hTovTbTN0fu3EaXF6PmvaLiFOi9NtM3R+7cRp
cXo+a9ouIU6L020zdH7txGlxej5r2i4hTovTbTN0fu3EaXF6PmvaLiFOi9NtM3R+7cRpcXo+
a9ouIU6L020zdH7txGlxej5r2i4hTovTbTN0fu3EaXF6PmvaLiFOi9NtM3R+7cRpcXo+a9ou
IU6L020zdH7txGlxej5r2i4hTovTbTN0fu3EaXF6PmvaLiFOi9NtM3R+7cRpcXo+a9ouIU6L
020zdH7txGlxej5r2i4hTovTbTN0fu3EaXF6PmvaLiFOi9NtM3R+7cRpcXo+a9ouIU6L020z
dH7txGlxej5r2i4hTovTbTN0fu3EaXF6PmvaLiFOi9NtM3R+7cRpcXo+a9ouIU6L020zdH7t
xGlxej5r2i4hTovTbTN0fu3EaXF6PmvaLiFOi9NtM3R+7cRpcXo+a9ouIU6L020zdH7txGlx
ej5r2i4hTovTbTN0fu3EaXF6PmvaLiFOi9NtM3R+7cRpcXo+a9ouIU6L020zdH7txGlxej5r
2i4hTovTbTN0fu3EaXF6PmvaLiFOi9NtM3R+7cRpcXo+a9ouIU6L020zdH7txGlxej5r2i4h
TovTbTN0fu3EaXF6PmvaLiFOi9NtM3R+7cRpcXo+a9ouIU6L020zdH7txGlxej5r2i4hTovT
bTN0fu3EaXF6PmvaLiFOi9NtM3R+7cRpcXo+a9ouIU6L020zdH7txGlxej5r2i4hTovTbTN0
fu3EaXF6PmvaLiFOi9NtM3R+7cRpcXo+a9ouIU6L020zdH7txGlxej5r2i4hTovTbTN0fu3E
aXF6PmvaLiFOi9NtM3R+7cRpcXo+a9ouIU6L020zdH7txGlxej5r2i4hTovTbTN0fu3EaXF6
PmvaLiFOi9NtM3R+7cRpcXo+a9ouIU6L020zdH7txGlxej5r2i4hTovTbTN0fu3EaXF6Pmva
LiFOi9NtM3R+7cRpcXo+a9ouIU6L020zdH7txGlxej5r2i4hTovTbTN0fu3EaXF6PmvaLiFO
i9NtM3R+7cRpcXo+a9ouIU6L020zdH7txGlxej5r2i4hTovTbTN0fu3EaXF6PmvaLiFOi9Nt
M3R+7cRpcXo+a9ouIU6L020zdH7txGlxej5r2i4hTovTbTN0fu3EaXF6PmvaLiFOi9NtM3R+
7cRpcXo+a9ouIU6L020zdH7txGlxej5r2i4hTovTbTN0fu3EaXF6PmvaLiFOi9NtM3R+7cRp
cXo+a9ouIU6L020zdH7txGlxej5r2i4hTovTbTN0fu3EaXF6PmvaLiFOi9NtM3R+7cRpcXo+
a9ouIU6L020zdH7txGlxej5r2i4hTovTbTN0fu3EaXF6PmvaLiFOi9NtM3R+7cRpcXo+a9ou
IU6L020zdH7txGlxej5r2i4hTovTbTN0fu3EaXF6PmvaLiFOi9NtM3R+7cRpcXo+a9ouIU6L
020zdH7txGlxej5r2i4hTovTbTN0fu3EaXF6PmvaLiFOi9NtM3R+7cRpcXo+a9ouIU6L020z
dH7txGlxej5r2i4hTovTbTN0fu3EaXF6PmvaLiFOi9NtM3R+7cRpcXo+a9ouIU6L020zdH7t
xGlxej5r2i4hTovTbTN0fu3EaXF6PmvaLiFOi9NtM3R+7cRpcXo+a9ouIU6L020zdH7txGlx
ej5r2i4hTovTbTN0fu3EaXF6PmvaLiFOi9NtM3R+7cRpcXo+a9ouIU6L020zdH7txGlxej5r
2i4hTovTbTN0fu3EaXF6PmvaLiFOi9NtM3R+7cRpcXo+a9ouIU6L020zdH7txGlxej5r2i4h
TovTbTN0fu3EaXF6PmvaLiFOi9NtM3R+7cRpcXo+a9ouIU6L020zdH7txGlxej5r2i4hTovT
bTN0fu3EaXF6PmvaLiFOi9NtM3R+7cRpcXo+a9ouIU6L020zdH7txGlxej5r2i4hTovTbTN0
L7W7+OL3ffabFg84/6zHPemsc652oj/5aicamB/419LS9OyOZz3jrLOf9qSzz3viWec8+qxz
T77zuY8547zzACDqfnc6+X73v+/Jd7//yac9aOeBD8TTu50K2Bjj+4wnDzz3aWed/JRzzzrv
rCc96qxHnn/WeecDPPWM85/2RDxaU17iKH/5b8tWKsVSFZ/8nXPOOfusM88942mPeux5Z5/z
5ceec8YTn3LW1U6MloWfSeMf08WAh6lweeHqT5hjWAnNrPoUQpgfTw/jJQZYhCUY48rr2FIb
hlrGWgbb8oIMt4y3LGBZwvHSjiUcSziWcCzhWMKxhGMJxxKOJTxLeJbwpTos4VnCs4RnCc8S
niU8S/Qs0bNEzxJ9eQcs0bNEzxI9S/QsUb6qwBKBJQJLBJYILBFYIrBEYInAEoGvUbgysMTA
EgNLDCwxsMTAEgNLDCwxsETka0SWiCwRWSKyRPlyIktElogsEVmisDCxRGKJxBKJJRJfI7FE
YonEEoklMl8js0RmicwSmSUyS2SWyCyRWaJ80xMPWcYaFrKGpaxhMWtYzhoWtIYlrWFRa/hq
tn79pawtZUcGjBQYOWBL2ZEFIw0KD2whgi1MsIUKtnDBFjLYwgZb6GALH2whhC2MsIUStnDC
FlJYX+pcaGELL2whhi3MsIUatnDDFnLYwg5b6GELP2xf3m9hiC0UsYUjtpDEFpbYQhNbeGIL
UWxhii1UsYUrtpDFFrbYQhdb+GLHm0thjC2UsYUztpDGFtbYQhtbeGMLcWxhji3UsYU7tpDH
FvbYQh87/rgLgWxhkC0UsoVD9VZWWGQLjWzhkS1EsoVJtlDJFi7ZQiZb2GQLnWzhky2EsoVR
tlDKFk7ZQipbWGULrWzhlSt3NmfIDVd45QqvXOGVK7xyhVeu8MoVXrnCK1d45cp9xRVeucIr
V3jlCq9c4ZUrvHKFV268v4w3mHqHISfdeI8ZbzLjXWa8zYz3mfFGU3jlCq9c4ZUrvHKFV67w
yhVeucIrV3jlCq9c4ZUrvHKFV67wyhVeucIrV3jlCq9c4ZUrvHKFV67wyhVeucIrV3jlCq9c
4ZUrvHKFV67wyhVeucIrV3jlCq9c4ZUrvHKFV67wyhVeucIrV3jlCq9c4ZUrvHKFV67wyhVe
ucIrV3jlCq9c4ZUrNydXeOUKr1zhlSu8coVXrvDKFV65witXeOUKr1zhlSu8coVXrvDKFV65
witXeOUKr1zhlS+88oVXvvDKF175witfeOULr3zhlS+88oVXvvDKF175witfeOULr3zhlS+8
8oVXvvDKF175witfeOXL/coXXvnCK1945QuvfOGVL7zyo4KNEjZqWBUx3q/8KGOjjo1CNirZ
KGWFV77wyhde+cIrX3jlC6984ZUvvPKFV77wamyA+MIrX3jlC6984ZUvvPKFV77wyhde+cIr
X3hFISm/XdYTxrtjUTY8Fs3BY9GAElgUoAhAuQ+XW2lRjnLzL7pRZIMl1ALAJ8jPSi0AfAhq
Aex7C8B1tTWFR0j9YKD6fmwc8J9iPwzZRuDlxwpoGJJFayz1cWwOAYo5o6UV0A4a20mA8hAz
7sY5T+Vw0+zj0EPlwtg0cx3uWzkHP6BtMbYYAUXjU4yDx71ovG10vYEexZhNHpuerut9yjGg
6GDGdiigmFGLgFqYsXnpugAxjg76YvLYcgIEH+KJVsbYcnLdAHVFMyqwGuXmBCihPYFbuTGj
plvXxd7jXZuEdzQ2/lyXTI5QdZQdxrYVoGR6NFZx7dpMcl0OAZ8m7sa4fLnP+c7g/cYY0WId
Jcv6DiwP0OiIdk9tl3Zo2JhgQo6pvkXfQbEy2p5oetT2psdHk6GKvUUtxmaY7wIajvggTISM
lnusx3vMPvoYDd5Y+Uw93lDq84CCZmxToRIp+pygeyb3Y1N+bPHyR3jJM5SMJgwQQ7zi+M2i
Fqg/vrCU89gAwcVMDAnqH/FljO1PfIZ4Mz0+oGhr4xtf2oCvx0CHQh5b6K6zCZTAp9ajrVFe
1nZgH75rg7ffj9mF7QaQC8kH6GbGr9aCE/jQ8a4DPp3yJm2HRmMIeOOQ/bE5a7qco8GHP8Qw
fhLIfUEOfEeGBBrzmA5UD2mIaCfXpqzpejSekHuA9GnMCgx+Gnh5tHjxcY/NedPh20DzMGU7
jFlS7vDB47XxVQ8gdUnB8IKoOOqaocjlLeZuCGZIPdoHJqUi7hlfYxzQLMRng2h+ELnzeMv4
7GOEEJemXMYPz/T40shy8LpEIc+IOeHnGfpQflS5A2fBGnwX+Jfy2aQu4/NFruM9PpvSCEwd
KpDQqCOdQ2nBJLCEXxki+Rb54SR88gZtVuMjPtrSKkv4UeGHH1ATfJulSZQ6fDJoW+JiCekK
3zYg/PzxVaC5gd8Hf2kJP39UEcTPPb6N8fKoAO4j+C2Ag6VJkvAtZtwOClFB4FIQpMI1Mr4x
EyuE36bBnasPCbcmfhIJPzS0WxJuU/i5lEZj7FAftMjwkwLtS1sTEH9O+LIz7jGlmRzxO8bt
AF8EiDjeOQDh/eAmF0EDsAKXB2TwZZfPKiO+QLi94beB9iK+yNJEZOtH1u5ngFu7xE/iJ/GT
+K1C/ErmK/GT+K2F6Ev8lPkhuZP4SfzWU/yYhyHNu5zMj4nlnjI/ZpHK/DY0g5X4Sfwkfur2
VLenuj3XIltbZTeyxE/iJ/GT+K1I/Nan23McptOQ34YmdbvRSGmftE/aJ+3bOu3TfJd256Hs
RrhWESPxk/hJ/CR+Er8j93pqyG+DM0OJn8RP4rfV4jcuMljNSoeD7/Xc3XyXUcO00kHZ3nLG
KPGT+En8tlr8xlVxqxG/sqVMgysd9jzZcyyoZX4bORdG4ifxk/hJ/FbU7Snx0xr39ckuJX4S
P4mfxE/id+QxP2V+GvPT7mba3axopHY3K9t0anez9drdTN2ey2Ndej5mp8r8lPkp81Pmt7aZ
3z5PeNFsT2V+yvyU+Snz077W2tda+1qvz5je5WW4yvyU+SnzU+a3tpnfeM7D5W3tqaUOlycE
2/jvEj+Jn8RP4rfh4qcxv20Ut8t7zxI/iZ/ET+In8dNsz41cy3dZAijxk/hJ/CR+KxK/g9/h
Rd2emzMGd1lCtR//JvGT+En8tlr82CWog9x1kPv2iajET+In8dtq8dvz9mZ9Uc0Qg+1DNP3g
nD34HV72eanDERa5M9fE8bbGOR+H4FxOYTweKQ59GLTDy/qIqMRP4ifxk/itqNtT4ifxk/jl
IWZvTM6GbSdIrLexR9PI9UPwbK0R6m3OwQ82RcO2E6FofIoR7aevRfXGoUsiZpONH4N6n3IM
KDoYw9YnyvUxu5iD9c7YCgXnh+gcrz3UOgT4LiCmH+rrDS5I/PAJ+i5Fn5O3zuTecORm/BjL
Z3nJH99phxft8NIbH9N67fCyyqUOyvz2Y/ztWFwTwuHIjPJoExax2hR8rNrgQuyHIduoRe5a
5F40UuIn8WtK/A6+25OvqG7PYyFWq35NiZ8yP2V+6vZcUbenZnuq21Pdnur2ZDKdQ0Ae7fse
nbulL9F3Bt28MUbrksslv/addTY4oM4gjFm47xz6H4MJOabas+s7b2K2mFXgne1rwd5kl/ve
2iHn0pXsu2AH5O3BRJdNyeh9N7jso0fKlpytUbFPfR5Q0KCbc3xFdXu68tmbbjBDSEO02Mgq
lx5f0/VuwDeC7nZ8bsr8msr8+HWkTju8rDor2obrKfNT5qfMT5nfijK/g5/wsjvxY7smdssn
ubPNB4RNSTR0slY6rE/CtipdlvZJ+6R90r6t074k8du6DV0OF02Jn8RP4ifxk/hpd7OtE0OJ
n8RP4ifxk/hJ/CR+WumAaSEeIwHGOF/XgMTeD1rpUDRSKx003+Uy5rtosqcme67P2KEyP2V+
yvyU+a0o8zt48Tv4ZX5s/WiZ3+HjZ+voS/wkfhI/id+KxG99Jntqwsv6ZGj7JawSP4mfxE/i
t+Hit8rdzbTBy36J0UFfV+In8ZP4SfwkfprwogkvmvCiCS9lL5pLdrO+5Jn2tdYGL66/jAkv
6vbUhJf16U5V5qfMT5mfMr8VZX4HP+Flrxu8aMxvfURqv7pDJX4SP4mfxG9F4nfwmd/uZnte
enezvYufZnvulxgd9HUlfhI/iZ/Eb23Fb3eZ3yonvEj8Dlqk9uv1JH4SP4mfxE/ipwkvmvCi
CS+a8KIJLzrRCMcExT7H3rhofQyRHYepw5nWaznhZZWZn5Y67FcmdtDXVeanzE+ZnzK/FWV+
mvCi2Z7rM5FG4ifxk/hJ/FYkfgc/4WV3Y36rnPCizO+gM7T9ej2Jn8RP4ifx23DxW2W3pya8
7JcYHfR1JX4SP4mfxE/ipwkvmvCiCS+a8KIJL5rwslkTXlbZ7anM76AztP16PWV+yvyU+Snz
U+anzE+ZnzI/ZX7K/JT57S3z02xPzfbUbM88xOyNydmwxwH5pbexj0Pv+iF4zpci1Nucgx9s
iiZXKBqfYhy8/1oUVhoNOcZssvFjUO9TjgFFB2PKpsuu62N2MQfrnbEVCs4P0Tlee6h1CPBd
QEw/1NcbXFDmp8xPmZ8yP2V+yvyU+SnzU+anzG9vmV+rSx0023O/xs3W+boa81Pmp8xPmd+G
Z36rnPCidX7rLHjLdZf4SfwkfhK/DRe/VWZ+Er9lAVnn5xI/iZ/ET+K3IvHThBdNeNGEF014
4ZSeHEIK3vc9pvWUgTTfGUzwiTFal1wus258Z50NDqgzCOOcHt85C8eEHFOd0+M7b2K2/eC8
s30t2Jvsct9bO+RcJhH5LtjBY+aPiS4bNndxrcFlH32MBoOZNSr2qc8DCho3TjXyXYo+J4+X
zb3RmJ/G/PY25teq+K0y89M6v3XO9pbrrsxPmZ8yP2V+K8r8Wp3wssoxP4nfsoCs83OJn8RP
4ifxW1vxY19G6kzKBvPU+5Cs80zzAGG5VEypj+goyRK/dRap/aq7xE/iJ/GT+K1I/Frt9lyl
+GnCy36J0UFfV+In8ZP4SfxWJH7b0O0p8Ttokdqv15P4SfwkfhK/DRe/VU54kfjtlxgd9HUl
fhI/iZ/ET+Kn7c20vZm2N9P2ZlrqoKUOe1vqoG5PrfPTOj+t89M6Pxuxy3gsqw1dh53IY296
G60dFzNiN/IB+44bz/WMvu5ZbhP2OsfqyN5FXzYot1223MTcYJljb3hvtbYbsGu6NaHHksRx
z3Lb9d6mhNWNAasg2S+FKGdSCFjg6E1I5VqmyzkaLLIcYhhXPJouYtdzrMU03Bm9rLE03WCA
DNFG1KWW692AlZfYUB3rIznT3ZrO8eVt9lhWGUpjwXRYdelQjWwHW/Zgzx0WWOK1saRzwG7t
XJyZ8YKoOOqafT++xdwNwQyp924wKXm+xYzlmnFwWB0aDKJZidx5vGUThhg9asdK5M5F02Nx
Jrdvx4btBbJ4yzk5n0IfyhLO3GEbd6wOxXeBfymfTeoyPl/bYz4kPpthnByJCiSHT3qIQ3C8
fOpiz68MkXyL/HASPnnjehSM+Ggzv7PUBXyYfUBN8G3aVsVP3Z4H3aW4Dq+nbk91e6rbU+Kn
bk91e6rbU92e6vZUt6cyv71lflrqoG5PdXuq21Pdnur2VLcnOqhL5yj6u3v0QHt0kQ61v5S7
/hns65d7dEKPvarod/XouR7QJRvD2PeK/fZwvGfZhw/785VroS8d18joqDaxQvMXubNaEf3S
6CZHF3fGkaFDncaZQg7ofkb3+3gQaERW7PA+ckTnN/rCS8Fk0MVdeogz4guE00oDDiLF9Uyy
bAWsQ8/fNtdRvZ7q9VSvp3o9N7zXU2vct1nkjvbeJX4SP4mfxG/rxE+J39YnptI+aZ+0T9q3
4dqnuZ5HS362GZf4SfwkfhI/iZ+G/LYuE5T4SfwkfhK/tRU/zj65/DMdlPltc4Z3tPcu8ZP4
SfwkfisSPy100GTP9ZnkKvGT+En8JH4SP3V7qttTS9y1xF1L3LXEfbOWuK+y25NLDbHyT8v8
1l4slfkp81Pmp8xvRZmfdvZUt6e6PbW/i/Z30f4uW7e/S6tjfqvM/LTBy9EmkKwbrsxPmZ8y
P2V+G575aYOXdROmg6ivxE/iJ/GT+En8NOFl7cfw5gqmxE/iJ/GT+G24+Knbc64wbEO8xE/i
J/GT+En8lPkp89NSBy110FIHLXXYrKUOex7zG1NGnWi0kcKozE+ZnzI/ZX5rm/ntbnuzPYvf
WFDiJ/Hj7H03DMla51MfezaLCOGYR4sjKG2f+75CWuqgpQ5a6rB1Sx1aXecn8duGMby571GZ
nzI/ZX7K/NY28xuPdp9/jnvSeX4bmc3NEUCJn8RP4ifxk/hpwsvWiaHET+In8dtq8WOXYFqR
+B38Di+7G/PTUoc5GdG2xEr8JH4Sv60WPwrD+orf7ro99yx+Y0FNeNnIrFDiJ/GT+En81jbz
22fx02xPNI02NROU+En8JH4Sv60TP8132VhN261WS/ukfdI+ad+KtK/VlQ577vVU4qfEbxgM
aUCp1DI/fgzJ5Oh6CucQ6yeTkumtc/2QbeJNAFE5hBS87/vgh7Jriu+MH2yM0brkMhuf1nfW
2eCAOoOwEXIWjgk5JmPKyknfeROz7QfnHZZTjlG9yQ4rKy1qkTnuj2sFO/iYg4kuG/7iAQ0O
q818jAY719So2Kc+DyhonKnXStHn5PGyuTfa4EUbvKzLBi+7m+8yalhOWI3c4ycF2u9ypYOG
/HAT2W0mtW5xyvyU+RWJlPi50vAwHdp5QeK3LuKnIb/NFaf9FlOJn8RP4qduT3V7apnfxmZ4
RxNRiZ/ET+In8VuR+B38Mj9lfsr8jiZul4dL/CR+Ej+J39qKn8b8JH6XJ3JH+3eJn8RP4ifx
W5H4aban95iVZpJlDny0m67wNj4biZ/ET+In8VuR+K1Pt6eW+W29Nkv7pH3SPmnf1mnfLlc6
jEsktLnZRgqlxE/iJ/GT+En8NNlzIwXusnqYJX4SP4mfxG9F4nfwQ36a79LG8NlliUyr/ybx
k/hJ/CR+ayt+u1vpsOcNXtTtucHzdiR+Ej+Jn8Rvw8VPW3u2mn0dy3pJ/CR+Er+tFj8mN6s6
ze/guz2V+anbc68CKvGT+En8tlr8mBVJ/AZNeNGEF2NxDEEsO/3jBIcQ+wGHFEQd6jAk7APv
Tc92MloMOtQhj8d8+A4nWeAkCZ9yBl346eDkihiSwzpfY/tYjpZwXcQJFT1OvYjWjidXuA4n
VLhkPA+v8H78WG2yOeMojN5FXw6zsB3YF3I2ONOiN+WsDNsNA863MKHH+RND+T5s13ucpIGj
LAKOvCgnV9gOG/eHgNMsvAmpXMt0OUeDEzWGGMbjLUwX84BdrCV+a9vtubsJL3vu9hwLaqnD
RgqjMj9lfsr8JH5rK3676/bcs/hpwgtapXvtVmy9nMRP4ifxk/hJ/NTtubEidzQRlvhJ/CR+
Er8NF78xgdvDWbbK/JT5acxPY35FI3EefBi8DTg6XmN+vc1+8HEc6TSdyc5h6DHbwRqOYeYu
4x8xXpTckGIZR88YZMRgJcYns+/HYc3cDcEMqfcO2yEnz2HN3AUMs7s+YDwU0RywzJ3HMCc+
+xg9TtplZ1/uXDR9Tj5i6NQ59uzlzmKYMyfnU+iD4ch97jBOPTiP8Vf8SxkPTV3GmKrtjfcY
Dx1YcNMnvKjb82jZzzbjyvyU+SnzU+a3tpnfPk94UeaHptGmCqTET+In8ZP4rUj8Wj3UQd2e
mypg38j7kvhJ/CR+Er8Vid/BL3I/+MyPXc4Ra53Qxx2H4FxOYTweKQ49hgR0nN/aZIoSP4mf
xE/iJ/Hb9WxPid83km21VFbiJ/GT+En81lb8Dn6dn8SvJQH7Ruoi8ZP4baX4lamQVlu8rP10
z4Pv9+Qrqt/zG1GdVspK/aR+W6l+vIVJ/Fa91qHVGS9a69CK4LRUD4mfxE/ip35P9XvuetBP
mV9LAvaN1EXiJ/GT+En8Nlz8tNbhGxGJTS0r8ZP4Sfwkfmsrfhrz29xV6PstuhI/iZ/ET+K3
tuK3u+meyvz2W0jW8foSP4mfxE/ityLxO/gJL7vL/CR+6yhO+11niZ/ET+In8VuR+B38Fi/K
/NTtuVeRlPhJ/CR+Wy1+zIpWdazDwWd+exW/cUuy7J3th2jzsOvJnlrkvletaa2ctE/aJ+3b
au3bhiON9tzrOa4PxLFUQ8w5usHFpJUOrYnYXusj8ZP4Sfwkfhve66k17nsViE0uJ/GT+En8
JH4rEr9Wez0vLX577vVU4rcpeijtk/ZJ+6R9W6d9SeK3NicP7ZfYSvwkfhI/id+Gi9+eh/zG
ghry20ihlPhJ/CR+Er8Vid82LHTQZM/9ysQO+roSP4mfxE/it+Hid+khv713e0r8Dlqk9uv1
JH4SP4mfxG9F4rc+810kfloaL/GT+En8JH4rEr9Wuz1Xmflptud+ZWIHfV2Jn8RP4ifxk/jt
eoMXid9Bi9R+vZ7ET+In8ZP4ra34UYpSZ1I2xqY+JOs80zxA3oeYUh9tn7Nme+6XgKzzdSV+
Ej+Jn8RvbcVvdzt7rrLbUxNe1lnwlusu8ZP4SfwkfhI/dXtu5Fq+ZbE7/LnET+In8ZP4bbj4
rbLbU5nf4SKyrr7ET+In8ZP4bbj4rbLbUxNe1lXsDq+3xE/iJ/HbavFjVrR9p/ntfZ2fxO9w
EVlXX+In8ZP4bbX4jZMjU++TiyEPcQhunEUS+xx746L1McRRIofBuL43PqYQsi+qGWKwfYim
H5yzB7/IXbM9tVh9r+Ir8ZP4Sfy2WvxWmfmtzyL3PR/qoCG/vWpNa+WkfdI+ad9Wa98qE79W
tW+V813U69maiO21PhI/iZ/ET+K3dfNdlPht3cKGwzVS2iftk/ZJ+7ZO+zTdRSOFEj+Jn8RP
4rci8Tv46S7jzJzL29xMCx0Oz3rk47bnOkdmlEebMJfLpuAj+wQKFPthyDYCZ685oWFIFtvn
Ycu8fioYc7beYcpX7vsahTlj2RuT81TO29jHoXf9EDw7zXEp39ucgx9siqa+oI/GpxgH7Mo3
RWG22ZBjzCYbTi5DOcxKy5iVlsNgTH29PmYXc0AtjK1QcH6IzvHaQ617gO8CYvqhvt7ggsQP
H6rvUvQ5eetM7g1vYePHWD7LS/74LkYTBm/DMH2zvuuts/jCUs4ulJK+MzEkl2zElxErSfCF
YeJgb6O1vn4dnB2YjA8G0wbrV2sTKJFD6F305WVtB/bhuzbeoDhHlKztBpDLmgC6mfGrteCE
TclEF5ztC71s5wwmJEYfvQmpXMt0OUcTQS9MTyxBposgR0gSvxWJX6tDfhI/id2lM92icKOm
QL0kfq4bkrPeO2vMuEEuPqHYe0g+Wpcesjl+WMnk6HoKJ2aGVyjh3u6g7hn34RHCbRxNCd/3
kPhJFyD2uP9al1wuCuw7iEdwQJ1BGAv6zkGFKAoxVX33He7+2UIvULW+FuxNdmhvWNQil5u5
7wJ0CK0AyEA2RXZ8N7gMBYBq4Y3VqNinPg8oaCB24ytK/Fz57E2Hdl5IQ7QRQlxFs3cDvhE0
uvC5MdWwBk1GaK/NHh/3KPmmw7fhoMHZDra003KHDx7Ci696QIuOH3SG2kK1QZDs+1HfczcE
M2CdgRtMSp7Myfga4+DAmmAQzUrkzkPv0fCI0aN2rETuHJYXoMXCJh4adQWy0Puc0DYNfShf
be7AWbAGDRH8S2kYpC6jcWGxXsGjYTCw4KpW+bUqfvxqY5cTWsc9flKgvbo9Ly0G2yaQEj9l
fkVuJX4Sv298lV+r4qfMb9uEbTfvV+In8ZP4qdtzw7s9lfntRgy2LUbiJ/GT+En8Nlz8lPlt
m7Dt5v1K/CR+Ej+Jn8RPBxpt3bo/iZ/ET+In8Vtb8eMUrn08x31MGTFpCROMMcVtcJgGVSbP
JIPZTWUX1JwC5zLFDpPZMRPaY1aawUxnQLvJPhRz7D4niZ/ET+In8VuR+PGWnzrMg3UDtrvG
7EpoxghhpRPmHHushxrqfticBG0wzTn3WHjCQbmE6atYiMSZz1huE8YVfJiOjJVPZVoypiuX
KKyfwTUyVjeZUYouX/xW2e3JSsRO4nfsRGtVDQaJn8RP4ifxW5H4abanMr/1EUWJn8RP4ifx
23Dx02zPVWVLm3QdiZ/ET+In8dtw8Vtlt6fG/DZFACV+Ej+Jn8RP4qfZnls3QUfiJ/GT+En8
Nlz8Lt3tOU7QzNwsEFvZZWwfPNSUDpM3A7aZwx6z46bAmNyiyZ6bkuwtvw9pn7RP2ift23Dt
U6/n8k1fz8c5ORI/iZ/ET+K3IvE7+JUO4+IHnWgkQZs/yVTiJ/GT+En8JH7q9tSQn47z04lG
5fClcpjPYX90nJ9ONHI9jkKKOCmxLlXHWnbbB5ythMMZrZb5aZnf/AzsWGWtyvyU+SnzU+a3
4ZnfCue7aH+XY6VVq35daZ+0T9on7VuR9h184re7nT1XOd9F4rdqETpW15P4Sfy2UvzG8+sN
zlUfcGy71G9t1U8TXtanm/FYqdzRXlfqJ/XbSvVjymAlfiYMTIvS2orfwad+dTWgDnVY+wky
Ej+Jn8RPmd/ait/uMr9Lj/klLXJfe/E6Wka3W1ziJ/GT+En8Nlz8Vjnop8xvt+LSepzET+In
8ZP4Sfy0zm/rMkGJn8RP4ifxk/hJ/CR+WuSuRe5a5J6w1zEOCc9lkb/psK+xs673qdci9+1a
5D72l2pj640URmV+yvyU+SnzW9vMb3ezPTXhpfXxt2NRP4mfxE/iJ/FbW/Hb3WxPTXg5FuLS
+mtK/CR+Ej+J34rEr9VTHZT5tS5Ex6J+Ej+Jn8RP4rci8Tv4/c12l/lJ/I6FuLT+mhI/iZ/E
T+K3IvE7+Mxvd2N+6vZsXYiORf0kfhI/iZ/Eb23Fb3eZn8TvWIhL668p8ZP4SfwkfhI/rfPb
yOUMlyXAEj+Jn8RP4rci8Wt1zG+VmR9zzdglbWy99mIp8ZP4SfwkfhI/ZX5rL2aXleUd6d8k
fhI/iZ/Eb0Xi1+qElz3P9hxTRu3wspHCKPGT+En8JH5rK36a8KLDbI+U1e0Gk/hJ/CR+Er8V
id82jPnpSKPdCMs6xEj8JH4SP4nfisTv4Ls9lfkp89ur0Er8JH4SP4nf2orf7ha573nMbyyo
MT+N+Z1IqRyGZK3D6S6x52gwoZiz9S7YPvflDBhAeYjZG5OzIX0Q5G3s49C7fgiehCXU25yD
H2yKJlcoGp9iHLz/WlRv3JBjzCYbPwbhaJkcA4oOxtTX62NGLQJqYWyFgvNDdI7XHmodAnwX
ENMP9fUGFyR+Ej+J39qKnzI/ZX7K/CR+J1rfBTt4tAJMdNmUtonvBpd99DEaHFRYmh2+iziX
Lg+9tcaNzQ7fpehz8hZ+b9h5NbYhSkPikj8oGU0YvA3D1KzxXW8dXhQNkuxCKek7E0NyyUa0
RGJtIaG1EnvT22itr22RfkDbxPhgQva1XWNxhh5aNaF30ZeXtV22bOgYb1CcQ0rWdgNaVtYE
tLXM2K6xXe9tSnjXwdm+vEnbOZNCwBv3JqRyLdPlHE1E2yqG8ZMwXUTLKCSJ39aJH1u/scse
fMHZjRnt64G8wQK+FHJIpHMeW82AcJ4jGvgRpzrikMcxSsv81j4ZZN425W/BpmHQWbY6y1ba
p7NsT0xoIbG54qL1MUS2VxJaHWa7zrLl25b44UPYa3LVcjmJn3o91eupxG/rEr+0u8yPiYHE
T+KHT4BSqSE/fgzJoBOkp3AOpVFMKKFTz2FMM6MDbvyw0H+Xgvd9j4HNqUMQQ5zoeLMuuVzG
HX2HXsPggDqDMBb0nUP3I3sDY6qjmr5Dt19GD41jP00t2JvsMMpqUYtc+zPV66lez5wwIh/6
UDq0c4cBbrAGPdAh5tIjnLqMXmXbG+/RIzzw/p5WJH4Hv9KBvE+dSdmgz6oPCbMRxjeEdxdi
wswE/FzymMDlhDkBPX5S6OyX+G1mNjcn01Tmp8xPmZ8yv7UVv73Od9ld4neEXk++IHJBDfmt
fU+otE/aJ+2T9m2d9u0y8TuC+Gm+y5zkquVYiZ/ET+In8dtw8dtzr6fED3luywL2jdRN4ifx
k/hJ/CR+WumwsSJ3NIGU+En8JH4SvxWJHyd1pQ7LL90QsDgzWayOGyHscIEFlx77YAyZSzoT
drjAlBxM9Mo91lwyw0rYLAMbUHDuF1aahnEwD8tOseNFWY6KZaolCktHcY2MXS1MrJDmuxzt
Bi/86JmrxE/iJ/GT+K1I/A5+sude57tozO/oorAtginxk/hJ/CR+KxK/VjO/cbXeHlY6HGHM
T7M9N0UcJX4SP4mfxG9F4tdq5qcJL5siWKt8HxI/iZ/ET+K34eK3ysxPSx1WKUDH8loSP4mf
xE/ityLx24ZuT4nfsRSsVb62xE/iJ/GT+G24+Knbc5WisSnXkvhJ/CR+Er8NF79VdntqwovE
T0fZal/rIps6za9sWW467DLucKhgtoMtpy5nHBaHYw17bGE+4HxmLnjLOD4QxxBi4/Ps+/HA
wtwNwQyp924wCafIlahg4+CwG3owiOZRhLnzOMAQu1DH6EMaeAPOWBZnehzByAObcURzgSwO
MNS+1mWr6+V9rSV+myJYq3wfyvyU+SnzU+a3tpnfPh/qcISlDhrzW6UAHctrSfwkfhI/id+K
xO/glzrsTvxWmflJ/I6lYK3ytSV+Ej+Jn8RvbcVPO7xop5a9CqLET+In8ZP4Sfy0sbU2tsZx
yMGXwfmiixGnQGeMvg+Gvd+EdJC7DnK3AUfHj4zwnSa8aMJLwNSbwTl78N2eu8v8tNRhr9nR
JpdT5qfMT5mfMj9lfsr8lPkp80vOeu8wr9x5jpOjeYDTWJDv4tgUj/btCCWctKKlDkU2lfkp
81Pmd2Ls4tCHwXsc2mSSJSc2OWvahPemzE+ZnzI/ZX4ryvx4y9+o8/y01GGDRVziJ/GT+En8
ViR+rY75aanDJmRqq34PEj+Jn8RP4ifx05jf1nXTSvwkfhI/id+Gi59me646a9qE60n8JH4S
P4nfhoufuj03QaxW/R4kfhI/iZ/ET+Knbk91e2qpg5Y6lKn7PEvAHvbHdzHiZAGvRe6dC33u
bfYDDm7QUodjt9RBe3tqScVeM0Jlfsr8lPkp81tR5qelDlrntz5iLPGT+En8JH4rEr+DX+qw
u8xPE172mh1tcjmJn8RP4ifxW1vxO/i9PfmKsUsGJxfHITiXU+A5xdrhZe3GDCV+Ej+Jn8Rv
w8VvlbM9JX6bkg1K/CR+Ej+Jn8RPsz3XLnP7RkVY4ifxk/hJ/FYkfprwogkvmvCSh4gzEMx0
6pvrvI09tj13/RA8B6mhuh5TxXPwg03RsNecUDQ+xYi90b8W1Rs35BizycaPQb1POQYUHYwp
c/Fd18fsYg7WOzNOz3ddcH6IzvHaQz2KIcB3ATH9UF9vcEHiJ/HbavHjjyOtSPwOfsLL7sb8
VtntybuXxvy+0ayrhfLK/CR+Er+tFj8Kg8QPDeyhyhomsISEBjb+K81mKF3v0JjHIWaDi0lj
fi0I1yrqIPGT+En8JH7K/HYtfsr8ViE8LVxD4ifxk/hJ/DZc/Fa5zk+ZXwvCtYo6SPwkfhI/
id/aih/zsNSZlA02ZuxDss6P/bgG8wZiSn20PbovyzhdTpgU0CdjjEOBEfIOJ69Hm4/S7TkO
FqrbcyNngkr8JH4SP4nf2orf7ia87Fn8xoISP4kf52O6YUgWzSs0qXo2iwhhLBhNqoAmVl9n
XzrN9uQnk0NIwfu+x5zWsvux7wxmt8YYrUsulymnvrPOBgfUGYTxI/Wds3BMyBHN1PKR+s6b
mNFIdWyq1oK9yQ4fubUDvoCxYLDYaTkHE1025evx3eCyjx47UmPH7hoV+9TnAQXRBK7XStHn
5PGyuTelqoftaV1roY2tebe1Rhtbh8zJ16kLET/8aWPrg1/qsM+Z3xHEj6+o2Z6r6HY81tdQ
5qfMT5mfMr8Nz/zG3ss9dHseQfw05nesRWtVry/xk/hJ/CR+Gy5+o4atRvyU+a1KfI71dSR+
Ej+Jn8Rvw8Xv0pnf7ua7KPFDH++x1qj9en1pn7RP2iftW5H2HfyQ3+7mu1xa+3Y52fMI4qfE
b7/E6KCvK/GT+En8JH4rEj/tbqatPdcnU5T4SfwkfhI/id+uN3jRfJeDztD26/UkfhI/iZ/E
b8PFT/Nd9ktA1vm6Ej+Jn8RP4ifx23XmpzG/dRa85bpL/CR+Ej+J34aL354nvIwFv26DF4nf
soCs83OJn8RP4ifx2zrx2/NKB2nfOuvdct2lfdI+aZ+0b+u0Tysd1mdS5rJgrfK5xE/iJ/GT
+En8NOS3sWvZjyaYEj+Jn8RP4ifxk/hJ/HAmVsCpANy4Hqc1hNgPQ7ZxGAwnCxPSmQ78GJLJ
0fUUziHWTyYl01vnenxeiWt9EaUzHfrIGQP4KCIOqOjxAUVrx4MrXIcDKlwynmdXeJ4PgCib
bM741HoXfTlFwnZgX8jZ4EiL3pSP1XbDgOMtTMARImYoH77teo8PHSdZBJx4wUEZazuc2BYC
DrPwJqRyLdPlHA0O1BhwDEEJMl3Mw4BzN0wfsyuXMh2oHhIOeIuoSy3XuwGnbPQ4yAQzH3h1
nekQjnimwzascdcyv6NlUuuG44bj6u0JJxIliJzEz1mPU4Nw3mU5FJM37t5D8nH6pTf9pHQS
v7E55DsoPk5R8ilntJWoDDi1KYbkko3GSvwgl8kNKZYGZYbaQrUh1Nn3o77nbghmSL13g0nJ
Uz5yF9DedDgGKxhEU4Fz56H3Jgwxekgzb8AZJ4mZHqdQRbQhXPkV585C73PCeWOhD+WsqtyB
szgGC98F/qU0DFKX0biwPQ57RcNg4M8/bXjmx19t7LSttcb5lgVa4qduz6JXOs1PmZ9Djo2O
jOCorQltPibrkEkfQ+neSMi5jeuhmhFJ9ZFO89uGzE+zPZcFZJ2fS/wkfhI/dXtueOY3rtZb
zvy00mHrhvgO12lpn7RP2ift23Dt23Ov5yiaX7fEXUN+h4vIuvoSP4mfxE/it7bixz7I1GE4
3mCyQh+SHQfqAXkfYko9xjYxg0pDfvgE1lWk9qveEj+Jn8RP4rci8dNpfjrQaH1EVuIn8ZP4
SfxWJH4HP99Fmd/6iM1+ZXB7va7ET+In8ZP4bbj47XnMbyz4dWN+muy5V7FprZzET+In8ZP4
bbj4rXLMTxNeWhOxvdZH4ifxk/hJ/CR+u97dTOK3V7FprZzET+K3leJXdj/BLmXa3kw7vPTY
yy4Pu1Y/9Xu2pmJ7rY/UT+q3lerHW5jEb1u2N1tlv6fEb69i01o5iZ/ET+Knfs+17fccd2K7
vIV+e57xcoRV7hK/1kRsr/WR+En8JH4Svw0XP2V+exWITS4n8ZP4SfwkfhI/jflt3RYwEj+J
n8RP4ifxk/hJ/HSeX9J5fpwMUs5xPeyP72LECXDehgHny3IgBYf36Ty/coqh6Ux2DmfqZjtY
w8N5c5dxGJDO8+PumzjFuMe5wj5YHPbMDyd1vseRg8ENucfRwuRSwgGFweM84gFnDcYwjuY5
HJwJwhk8mjRCOCQS18g4ftjECu3bmJ9WueOL2dSuT2V+yvyU+SnzU+anzG9jRe5o4i3xk/hJ
/CR+Gy5+e57tqcxPmR9OcCYNKJXDkCwODsFhIT3nUBGKOVt0V+DwkL70kwHCidDZGzN1jrnO
o98jDr3rh+DLGitAvcVpI36wKY5rjgFF41NEP4f/WhTOksYC1JjR7cHuErxe71PGmdM5DMbU
1+vRBxJzQC3M2F/nuuD8EJ3jtYda9wDfoWPFoOtlvNTggsRP4ifxW5H4tXqsg8TvaNnPNuPK
/CR+Ej+J34rE7+CPddjdOr9LL3XQSe5b18t5uM5L+6R90j5p39pqHzuR9vEwW61xx+d7uGhs
ii/xk/hJ/CR+ayt+u0v89tzrKfGT+GnIb0iYTe0xWDiOFSZMwHY9hXOIE5QMJv1jTDPbxN4f
tCtyCCl4TunG8CMh3xkMccYYrUsul3FH31lnObs7OoOwMcpZOCbkmOqopu+8iRnTxJ13GFod
o3rMrccoK+aJY8x1hIIdPMY+TXTZlBFZ3w0OE+49lihgCUeNin3q84CCnEA+FkzR5+Txshmz
zAkdtsihuFrpgHUL/HBM5wIGuG32+LiDVjqEiF+Gc7bVIb9L93omdXtubEa328xUmZ8yvyLK
Ej9XGh6mw9SukLDPf0w2F8k3Xe8GNEcwzwqNBolfb3xMIdTVeiFiotskfusz5Ld38SMBYpcM
1nTGITiXUxiFFNP5sATWo4VqUmkG7PYmrLhj07Uq8ZP4SfzU7bm23Z77PObHBhGUDq0fzGiP
aAOhSSTxwyewCYIt8ZP4SfwkfisSv4Pv9tyd+I0alhOWQvUYSUBv/94zP4nfJggf34PET+In
8ZP4ra347W7Ci8b8NkWwVvk+JH4SP4mfxG9F4rcNY37K/FYpQMfyWhI/iZ/ET+K3IvE7+G5P
ZX6bMf52LERQ4ifxk/hJ/NZW/PZ5zE/r/DZkcsuRxFXiJ/GT+En8ViR+6vbUUof1yUQlfhI/
iZ/Eb23Fb3eZ354nvCjzU+anHV60w0vRSJ1lq0XuW77IXRNejtSFuI6YMj9lfsr8lPkp8zvy
WbbK/JT5KfNT5qfMT9ub4T7g+svI/LZhtqe2N1vHLO9IdVbmp8xPmZ8yv7XN/Ha31EE7vBzp
5r/tmMRP4ifxk/htuPjtecKL9vZUt6e6PdXtqW5PdXteXrdnq0sdlPlte5Z3pPevzE+ZnzI/
ZX4bnvlJ/I508992TOIn8ZP4SfxWJH6tTnjZs/hptqe6PdXtqW5PdXuq23Nduz015rftWd6R
3r8yP2V+yvyU+a0o89OYn7Y30/ZmGScfe2NyNuxxgMR6G/s49K4fguceCYR6m3Pwg03R5ApF
41OMg/dfi+qNG3KM2WTjx6DepxwDig7G9BWK2cUccFalsRUKzg/ROV57qHUI8F1ATD/U1xtc
kPhJ/CR+Gy5+yvyOlPlsO6bMT+In8ZP4bbj4acxv24XuSO9f4ifxk/hJ/FYkfq1OeFHmd6Sb
/7ZjEj+Jn8RP4rci8dOYn8b8NOanMT+OauYQUvC+7zGyyUax9Z3BGGeM0brkchl49J11Njig
ziBsjHIWjgk5pjqs6TtvYrb94LyzfS3Ym+xy31s75FzGUX0X7OAx+Gmiy4bNXbzi4LKPHscx
JGdrVOxTnwcUNG4cbfVdij4nj5fNvSlVLUOnh/3xnU510KkOl7G3Z6vit8rMT3t7bkrGqMxP
mZ8yP2V+a5v5sTmXOpOyMTb1IVnnqXSAMGkuptRHtBXznsf8xoKpd5jAl6MbXEwSP4lfH/uS
WrgO8ywz5lkGsKyvUy2dMj9lfjZi6m2sJMH03Nib3kZrx/TWdUhjXTKeGa6vE3ltwgRg5Mu9
i75QyXbZcmavQeLbGyYW1nYD7kTWBNDNjBN5bdd7mxLy3YC8uKS3tnMmhYCU15uQyrVMh/uX
Qdo9xDDmwKaLmAqM7Nz0mC5csm7TDQbIEG1EXWo53PuQi2OWMTJmZX6Xkfm1Oua3SvEjvWKX
jHM+DsG5nAJ7YmKHyewB89TRPWOS5SexKSKxqe9DmZ8yP2V+Er8Nz/xW2e0p8dsUMZT4Sfwk
fhI/id+RD7M9QrenxE/ip25P11M4h1i6y1yHbrfeOqziz+iBY/+cJryo2zOiyxVzmwbs3MC+
sYx+VvTXgiDZ92PPbu6GYIbUe4fesuTJnIx5S3FwmCYVDKLZ95o7j55eE4YYPTpl2feaMd5g
esxS4lYO2LyhQBY9vTk5n0Ifylym3GFLB0yTQhc0/qV0Cacuo1vZovfSo0t4YMG0tuLHT+Ly
x/yU+W2KYK3yfSjzU+anzE+Z34aL3yrH/DThZZUCdCyvJfGT+En8JH4SP3V7bt0EHYmfxE/i
J/Fbkfitz2zPcYJm5qpZzOzN2D54qIN5mLwZ0P2MWcfjpsCY2bm80kFDfscyWVvla0v7pH3S
PmnfirSv1TXuq+z1lPitUoCO5bUkfhI/iZ/Eb23Fj1Kk+S5aUrgXEZX4SfwkfhK/tRU/TfaU
8O1F+FhG4ifxk/hJ/DZc/NTtuVeB2ORyEj+Jn8RP4re24qduT2V+exVoiZ/ET+In8Vtb8dvn
bs9xcbxme27kKgiJn8RP4ifxW1vx213mp27PvWZHm1xO4ifxk/hJ/FYkfuuzzC9pnd9GZnNz
xFriJ/GT+En8ViR+ra7z09aec0RhW2IlfhI/iZ/ET+K36x1etLXnpoijxE/iJ/GT+K2t+O1u
zE+Z36YI1irfh8RP4ifxk/hJ/Had+VFudZD7KkXoWF1L4ifx20rxK2fdWYPj9YYhJKmf1E/q
t3UzYKR+Ur+tVD824CV+23KYrdY6HKv0quXXlfhJ/CR+yvzWNvPb6yp3LXXYukTvcB2W9kn7
pH1brX1MitLWad/e1/lptufhIrKuvsRP4ifx22rx40zITRe/VfZ6SvzWVewOr7fET+In8ZP4
bXjmt0rx02zPw0VkXX2Jn8RP4ifx23Dx0zq/dRWo/ay3xE/iJ/GT+En8tNJh6ybASPwkfhK/
rRY/TXgZos3DrsVPY377mY0d5LUlfhI/id9Wi992TnjRSoetS/QO11Vpn7RP2ift27peT2mf
tM91jg2/ooE2DYOxKfhIZhQo9sOQbQTOvhFCw5CsdT71sZ8Kxpytd8H2ue9rVB5i9sbkPJXz
NvZx6F0/BF+21nCd723OwQ82xXGrKUDR+BTj4P3Xonrj0CERs8nGjxfvfcoxoOhgTH29PmYX
c0AtjK1QcH6IzvHaQ617gO8CYvqhvsHBBWmftE/atyLta/U0P013OTzpkV8VblI6iR/UfUjO
eu+sMc5XdY+9h+SbBDnvq44mk6PrKZxDnKBkeuug7tkmnmqGa+WATSO973tIPO8L1ncGYh9j
tC65XBTYd9bZ4IA6g7Axylk4JuSYqr77zpuYbT84VK2vBXuTHdobFrXIpUHhu2AHNF2CiS6b
UnvfDS776GM0eGM1KvapzwMKGjc2O3yXos/J42Vzb0pVSxvisD++w2XC4G3AK47NGt/hTeNF
0SDJLkxvMobkko1oicTpM8Sb6fEBRWvHN+k6vBmXjOf79LVdYxPaQ/jUehd9eW3boemFho7B
2+9N+VhtN6BlZU1AW8uM7Rrb9R4fOt51wKdT3qTtnEkh4I1j/65UrmW6nKPBhz/EMH4S2tgT
3ya/oE1f5cf3GLuc0Dru8ZMC7bXE/WrK/JT5QToCE9B6/5X4SfxCwgyICCGuotm7Ac0R9Dig
0cDZDtgR1FF7bQZt4ij5pkNTxEGDsx1s6aTIHVodEF60cwZ0Z7DFkrGNNlQbQp19P+p77oZg
htR7N5iUPPU9ow0TB4cmUzCIZiVy56H3kKoYPWrHSuTORdOjxcL+DfRoFMhC73NCx0zoQ2nX
5A4NNjSZ0BDBv5SGQeoyGhe2N95vy8aeEj9lepcW+9K3iZ9NeVTmp8xPmR96+CV+TAZjz2Qd
Mkl9Z5dEQs5tXA/VjEiqM1uLqQtIo/sAGUYebw/+HHem+alDImcwYNOHhBGZMZWFtIeYMDqD
jpLM2u8p8xtVEw0YdDagr2dwaBKVayWDlk4cgnM5BbZrYodRHfSKeHTPGPR6AJLgtP0ZSPw0
5le6Y9Xt6UqXs+kkfo6JpcQPHfClVx1H90n8NlHIJX4SP4mfJrysaMLLwWd+o05fXua3525P
ZX4bnMFK/CR+Ej+J39aJ39hTmTl9bN4Kd/V6bkoSKO2T9kn7pH1bp317n+wp8ZP4aZmfVjoU
2dRKh7K+Q5M9j8l8l33u9RwnymjIbyPn7ijzU+anzE+ZnzK/XW/sqcxPmZ8yP2V+yvy0zO8Y
r3RQ5tf2aoKWhVKZnzI/ZX7K/FaU+bEDOHVY/e8GiCI2VMHquBHC5obYa8djSeBQ1wdy3yOD
nY1yj+12xlWELmLvQW52hE2Gwihr2HEImx2WnYiwQ1G5FnYNwjUyNjQ0sUL7NtlT3Z6a7Kmt
PbW7WdFI7W7GG7A2eGlmjfvuMr9Rw1azu5m6PVvO5ubUTZmfMj9lfsr8VpT5bdwyP2V+yvyU
+SnzU+anrT3b291MmZ/G/OZke8uxyvyU+SnzU+a34Znfnrs9j7DBC+UWG55pa8+1X/4g8ZP4
Sfwkfhsufnve3Uzdnur2VLenuj3V7aluz/a6PTn9ZB8PdZD4SfwkfhI/iZ/Erz3x292YnzK/
5bEuPR/HSdXtqW5PdXuq23Ntuz13l/mtUvw05rcp4inxk/hJ/CR+exE/HjC/JmfZSvw2RbBW
+T4kfhK/rRQ/w51HsFg94rzSkKR+e1G/Jk5y312/556ne2rQT4N+GvTToF8RSW3xwruttnhZ
sy1eVpn6aYuXVaZfx/JaSv2U+m1l6sdbmDI/b8JAYUgbnvntWfzGgjrTaO0X9R1JZCV+Ej+J
n7o9JX4602gjBe5IojdhEj+Jn8RP4rfh4qcxv+mGr8dL9oOT+En8JH4Svw0Xvz13e2rCiya8
aMKLJrwUjdSEF0146Y2PazbhRZmfMr5LMr7ps1Dmp8xPmZ8yP2V+GvPTmJ+xKfhy/nLRxdgP
Q7ZRmZ8yP2V+2t9sXfc3U+Y3ZTt6vCQDVOanzE+ZnzK/FWV+sSyb6HPvhhADjk4fSjs6db2N
vY/eB9sPeVwd7/s+mOCG3AdrqU6pczF4B8j2JoZx+bozSMm8NXg0aYRsH3GNHLMzsUImZYNm
ex+SdX5cu2HwYjGlPto+Z435SfQuEb3ps5D4SfwkfhK/FYnf+hzlzh1+Ype9gxpHmwf1eqrX
U72eyVmPn4QxYxMSrQO0WQf1eqrXU72e7fV67vPG1lrjrsmeGvKT+En8JH6XJ36t9nruechP
4ifxk/hJ/CR+Er91FT8N+U3DXHq8ZOhPQ34a8tOQn4b8NnzIb8+Z31jw67b25KSb2CXjnI9D
cC6nMI4fxqEPg/cYQzTJMgeW0LT9GUj8JH4SP4nf2orfPo/5HUH8dKjDpoi6xE/iJ/GT+K1I
/A5+zG934rfKzE/iJ/HrY8+edKpnzNlieQ7W0/Q83ZlQxvoeb0zOhrwD4rHOB/0Crh+CJ30I
9RYLcPxgUxyPFgUUjU8R63r816J6g5VAMWYs8+HyIJTrfcpYQ5TDYEx9vR5rfmIOqIWxFQrO
D9E5XnuodQjwHRYSGSw1Gi81uCDxw4fquxR9Tt5iNRWWWPHDKR/jYX98p93NtLvZZexudvDi
N6780zK/TRGkg3wfFKpw8gL/XfDJK/BhccEd+Pfiw//76sX8t0/Srrr074zlf8fBlouM17ng
kxeXciXkUn+uUstM//Cdt+Azvv5ovCZt8svTXf257wKve+UHLM5fnLV43OJJ+HsOEdrVz12c
sXj04pFAz1g8Ef/yyIVZhMWw8PhfZsSJU8Rh+HQFPh6/g2jDZ9c6D9c4E1c5UqkOr/to1AJx
33Knxc7i1MNerVs8fvGUxdn892vfD1d4MqKftngCStijRzL6cLvODl7pHFyJdWFNnrZ41OKx
i/OAnLP4ysWPxV++26fg31H6ipN33nSd45+5eObiZHpXqI98fvV+4YDGRY+/Fu/XLD2GqWwr
j8efh8/ta9/zymp1XLnS1RcnHIF5xx0F+8vnj/8w/ft1D4v7HH9jF338B6596Ov/oeCLhXlZ
xT/PuGP6363w6teaUYO3IHYH9nrYFUu5Q4deUh7Hewd+y588H/4ROHyZWLlE/cOyl/ffNS4v
4Cj/fsUr8R+m7+3BS1H3KM8vuTst35W6pbjy9AaHA/CPw3/jRwLn+AsWJ1+B7/jE8/HLfNJh
v/ZD/5e694ySqmq3tgEFSSKiKIIgIg1IzqGrdhU5ZxRJQoPknEMTJEjOOUpOKkgQUOyqLkTM
Cog5Y87pURQj332tmuu8dcYXxvfnjPG+jHP1nPese6+99tqB7pbzbOsob/CHp6T/c1WOXDly
z8xZKHlNNrS4gj5K7cr5X2fs/+/18z/Td72b26jROXKcNDfSFvXhEm2CNydUCK7rNT326HPt
gquK7QuvrDo1dl20aZD3r/Rg9uBZsdveLRbkeLhg8NnwFbHt274Jj552T+i9TzbGWi3+JNy5
5qlw/Vc2xe5tuS3ct36n8O6KO2L5yk0OvzxrYujo5l2xOnXnhsv89Hloct5dsZ9/ax/MqdY6
vVmdzNiSE+2DKTlviFUbmhlb+kG7ILvL9tiGW6f6fcXZ1wc2t7cnVIh/0XO6n0+c+Wi/sZT9
xtiv9pXFvjSHLObQ7b7R4Rw5LpbN/9au2JeRUNar415Pz/1y0udocD5WJ31j7N3wY7HLzdrF
xywcH2vQ8Jb4rbdcG8/TfkWsT5UK8XFnWsfrrZ7IHOK2Jm4OL35WP170lmbxn26aGpvYd1V4
wKF28ZK1xsceG1I3KLWsebz+z1NivatUCPrZtk1t26qDL4WKjGkfr7lmXGxFnXxZRze1j18e
My626q9PY1s/eyp2y+5NsTc3b491iNwdK1h4R+z6r+fGBvb8Luv5v3fGPjkwOXb8sxlZG9e7
Y4nNWntVGseiPESu/hD9GifMOBwv56xiz3V+X2H2pWMMOMZNf6+MrT7cLkirOd4fozvvNv94
lzOtg442/2lr68Y7TGwe/HVVZuzh/L9kfTumfTBr9bhYiSHXhfptah+Ex46Ldel/LFy8cbtg
85LxrFsw0batbds++0b9YHmZZsHM66bG7HqL2/UW1/UWt+stxvVm10Pcrocw1wPnhGvsi6e2
xN6zfrsGgi/tGrDrJ27Xz5NcP3bNxO2aCXPN/PVT2/j0o/vCPYoMi/37ZJv4G8f2hg936RLL
Obd1vOrje8K514ZiA/9oG9+7+cwd5A881cZ58hu/bh0f2/zDGPk9x1rFg1/fj5Hf/29LG6dc
nPzAyy1snLQ4+bejmsSn7Knr8iXNG8dXLq/jcjI+o5+Mz+hnDMYiZwzGImef7JucfbJv8lFF
rtrFXMnxzFX94ZT+sO+38YOU8QM/vs0nSJlP4OdjWZAy/8DP38YIUo438Mdr+wxS1ifw62Nz
DGLjV+9mnjbHoFuDY7uZp/rd+tsc6Xfrr/ED+m2OjB/Qr/m43ObIfFyu+bucjM/o1/G6nDEY
K2V9XM4+2Te5rWFZ5sp+8791R1nmqn43V3Ktvx+f8+XH53y5XOfX5Tq/LmeNmSvjsMZ+/p9s
ah5fdrJsYPuMvXugcfyWT2s437JGe3ftca1eKNk2vm/DRzF8l+qt7RouH8e33tg03jernvMo
NTmf04dnO7bHc50wrvKwz60/8P02TuDHMQ38+PZ54Pdr2wV+PjaeO7+MqdzdX+oPyDWO8xrf
ee3XeRuP+TjP/ce4mqcbF6/jcrmO13nmy7j0tG2QHl++KezW8OtHqsVPv9zEeVvj+C+bmjv/
zqxtsR/6tHK+8qRO6UUWtnb+0oaHw+NDyXy+nZOw+t/6qEbw2KONXc+Hy8PB2abpzuc/3yQ4
t7ua8/9Y73Kdx8vhlkH6sW/DnNPC01oF8+qsd/6DBa2Dh6r2epL8q76tgrcHb+Naix1v0DKo
NPc756svbxFMezNfnLxi3RbBeydvcP4/eVsEB48Wc776f5oHv1cv4fwf7zQPPnu3pPNf2xw4
TrY9Oa1xcLl+TeeXNEwP3lgddr7rl9WC04ebOM9197Fdf/RPuO3r8JstWjr/4LiV4UXLWjmf
Xvj6rDvt+UhP0eBwrHP5ZG7rE2+ibQfFasQLnW7sep4eEo4vHZHu/OUnmsQLvVnN+e+T17nz
3/VoGV+w+DN3vP/sbRX/fM5C56dMbR3P883sEPta8FfL+OR/ssL4r/+YFxtbaP5/+X5HF7j+
d8PzwwM/mv9f3vfwzQvfB/JTMeCvEnh+HqBG+bYO8HwDCfhr5FG+Q2O7fAafAT6/PFpAHuWn
bMBfK48Wkr/O1I+D5zteapT9AZ7vwvAo38nDDYbvwd8o8HxOjbINHi0q8IxLjbJvYK6+B3+T
apSffwBfTB69ReCLG3zOtiUEnuOlRm8VfHvte0qZZzvA32awr9KGnw/+dtVoGXnUHzv+DtVo
WZGmjD58OdVoeXmU78QBzy8y8GhFebSSwFeWR6sIPD9L0FfN8GPiq6tGa8ij/prE11SN1hJc
u76Ha9SPiec6pUb9OuDzqka5TmobdQx/vvD+nOLrqkZLC3w9eZR1BzxrDXjWGvB+zfGsNeBZ
a8CzvoBnfQHP/vAo6wv4+vIo68t8Gxh8BukGn6EheWq8fSPvPkMDgY/Io/yIDviG8mgjgW8s
jzYR+KbyaDOBby6PthD4lvJoK4FvLY+2Efi28mg7gW8vj3YQ+I7yaCeB7yyPdhH4u+TRuwW+
qzx6j8B3k0e7C3wPebSnwPeSR+8V+N7yaB+Bz5BH+wp8P3n0PoHvL48OEPiB8ugggR8sjw4R
+KHy6DCBHy6PjhD4kfLoKIEfLY+OEfix8ug4g2uVa5drFPDj5VGuUcBzXfI51zw14LkP8OgE
ga8tj04U+EnyKNcu4Lle+fwW1WT44qrRyQJfTB6dIvCZ8ijXNOC5jvn8JtVkeHLATxV4nv/U
aCl5lOse8CXkUa57wE+TR6cLPH/fUKO3GvTifR/ZDIEvJI/eL/D8/U2NzhT4WfJoV4HvZvB5
AYMa8Pnl0dkCn08ezSmPzhF4/lDz5wGBnyuP9hb4DIM/uQxqwPP3Cx6dJ/A15dH5Ar9AHuUe
Azz3FZ/z9xc14MkBv1Dgq8uj/L3IZ+hgga8kjw4V+EXy6GKBryKPVjXoxfs+siUCX1keXSrw
9eVR7lvAjzW4b5cZYwSeex9dLk+NHyFdIU+NHyZdKU+NHyJdJU+NX60a9c8x/BrV6ACBXyuP
+uckfp1qtK/Ar5dH+wj8Bnl0ozx6r8Bvkkd7CvxmeXSLPNpd4B+UR7fKo/cI/DZ5dLvYoYw+
/E7V6C6xWxk9+Lule+Sp8V2ke+Wp8Z2k++Sp8ftVox0E/iF5tJ3APyyPPiKPthH4A/JoK4E/
KI+2EPhH5dFmAn9IHm0i8Ifl0SPyaCOBPyqPRgX+MXk0EPhj8ij3BuDHGqONkcZSgV+ibLg8
NX6xdKg89z/Pi4VGhjHXmGfwnOlnzBd4cjRDnuddL+MBgZ9jdDNmGbMNsh4GOeDJUfrwPLvv
MmYK/P0G2lmeGj9D2lGeGj9d2l6+rWlrY6rR1JhkTDZaGs2NKQJPjtKHjxjjjQlGY6OhMVHg
yVH68MeM4wbnAvAr5NFxAr9M4JcbbMv5ZRvAn5BHHxd4rmlqlGud3qMGnwGeawuPHja4Hh+V
p8ZzTePRA/KoHwfPfUKN+v1x3/n54HmOUKM8X7hfeW7wGeC3yqP07TV2GfQCfqc8yvOFHp4V
fAb43QafbTf8tnj2wb557vm54Z9Qjfq1xa9Sja406OX5yWeA5zmLRzfIo2sEfr08uk6sVUbf
aoMxAO/3x3lnPq8ZqX9OP9OCyylH9o1TE78cqBnJsbJS1uAi0xJNR1WMvDihUiw8dFrithxX
uZ5Zn09PlD1wPriwtFLWYw/PSPSp9GTwes1KsSLfz0h8MyEt8uSKSllrdk5LTJma5vrxv66p
GDm/I0eYcW45auPbH8b/57N6kZFLHgntfmNqovgfuSJrl1fKYvxn4ucDehh/ZaesYP+SSiHG
r3hou8v/qHN/4ob/zHX+0Lj7E/Qm//BfLP2fmYmskktjK9fWikcfvz/x7cZSWes3b4+zbdH7
+jaonf+3eLe0GYnPz/6YdU+hYtkPl5+e+DLPv6HHWqdlM+ezZSo0GPxMxWzmXPDVUuHJw2pm
M+eZX98cejY9yC6xfmrir0K3Zz16KtnzT+u9WVWPJP2IzOpZ70xvnH2u69REg2ZlsnY91SKb
tf14y41Zn1/VLvvb85mJM1NKZh3755Kbw4ayHRrkPZScW5vdc8JP96nj5nzD9Y+Ey/1a2fm3
V/cOFzpVP+BYZj3+VPihM1MCjr3Pl0dCy9tuD1KOK+C4dCwRjuXNlw6HFj9aMcKx3LS/XKj/
jMYR5vbQyR2h9lWCCMeSVSwt1GVimuvfkOfcE5Ps/LGtjsttqzVx/us218ZqZ9aMsCavf9Ev
9urtST96d4PQS5cvuTlM/Ht3VkaP5Nz2vjI+1nTQbDfnJ179OuvEExF3LMeeaZH905k1Ddz6
7KuZ3SdrTIgxgyM1s0f1WJKOPz+rSPaTG2qFX+o+PbGueLHse4adDXG+RvbPih/47pp0ro0m
zbbHB/R6IsQ6vLFie/zs0GbO7350e3x42XMnydWTldLj/OpuWfFua/K5a+ye20pn37B3dVba
O9MSRZbenP3VykEx9tXucM3sSy+86OaT8Va97B/7fpjFdftTnnbZy/bVS+ecNjSqpl0dHB7Y
OlJ9fmbibLGCwZR9HSJf7slMjCg1O5ziY84Pykx81iB3vHOLzpE/zgxN3Lh+V3bJxuMjzd6v
mhi9oWqi6bm5kUmv7M5+dNnQBPmeszfEn+iTmaD/fMntsRU7MhOM06LUkvCy3Ulf6udcQYkh
yZ4pT+6MtP42ue36eVWjRX9Ijnlh+9Bo3oG73b6W9c+M/tangJvDrbsyozeUWufmdvPezOjq
AzPdnNsMzYzetT9HwH7vfmdoNF+ZXRHm8+mVqtH4+KpR5rnq312R744OjZIf2X9t0Py+zCj9
u5bvCN+1IzPKPEcdWBQ7vTvp692cL/7qgGTPioW7su96Lrntx/2qJg5dX82N2WHJ0MTv7+52
+1p9ZFzi+a9WRjILfxFc6Z6Z+PS5veFXvrgr8u/CiYnqyyeH3z+0MPJ0kamJnwf/HeJ5dqFY
ZuLypSGxXWV7RHJXnpgIbZgd69d0SaT+uqmJLm2vxH7ZnB75ZUlmonrfnHHmduGv4YmvQ8ey
395+bWTRuQqJMk9VTty256HIT59USbw7u0qi0+0rIvPm7cu+9PqwxNdz74mUWVI4fubFqYlj
d9eJ5Lh4KVZzRXL9D/+xJnb+5OTE8H1jIu1+XxW797pJ7jw2rDQ79MQvyf4jK+eEzh5M9n9T
f0l4S9HJiS3XTYs8//HH4S/WJPPNGXmCzouSPvz96sh1c0e4MZ/5+fvwbz9PS5T6rHik8OQH
Iw9+1TcxPXQicsOItGjBnyPuuXvxi4rRCh0qJXKW3Bdp9N7w6OtfJI/rukNTo/kyCsT/uVwv
8sbhidEayx+JhQcsiKwIxkcvlVwXu1hiY+RQkanRnQdzxFjDb27JjD4yoWuYNWxeeWJ0nl0P
rOGxtVOj/ex6YA07L82MdjXPGjYqNiJafO9jEdbww68rRPvvqxxlDYvfWjU6o1WVKGv4UsN9
keefHBZlzCHfFg6Wvjg1yhqe7PR7+K3lyWujf+P14UknJ0dZwxNNN4YHF5rkrodb+s7Iyv4l
2V9vzdSsdw8m+0+uXBR7u+jkKGt4zeiLsQZrk/npfbnjxxcl/d0vrs6evmiEG3PE+a9j3/9n
WpQ1vO2+B7MbHOgXzTf5aCTcplxi6fogWq1Q9Uj8TMVEtTGVoqzh9uzhienTjrvjOjU/ksi7
8qZos3w7I+9m1kqc+LFWtH3+34Jj316TKPVji2jdvvsjt/ffl33x29HRr04cDn5sPin7z1Zj
ok+PHh6Z9vXfsZwrpkRn/9s3srje9NjVeaa7OQwaE4lNjGZGua5ufm5RuEKBqVHW/8Ymu8K/
vzQt2rN66chNtfMHB1+fEv37dK/IkpeXRVa2G+mOpUL3fZGtd4+KsuZTpt4UfX5DxM1t5S21
o+92TM6t56stollHr3HnYlveMdFBN++LtO7zSNBp+pjoz7eNjzC3bw5lRrvZeWx8TbtI8baZ
0W8vfuvur+fqT49usvP+4rqikY4NM6PnVlYKM8+ZBadG1xyY6a6Ts7nsOOy5wXrqWeGeJ9Ue
zoz+ac8Wxlw/PzN62TzXycBZtq+bb3LevvOO+r+xe/W2a8lynhuLnhwRzblmVTbXwNmPRkaH
5N+XzfhfrY1E7559cyKz3tZIj+21oi1erJVg/d/6Om/0wbkt3DX/+5a9kan/jk7UK3QiuPL0
5MiMGmMSHGOeZ/IFRR7JTDCfebneCw8cl3xOfr1jZfiuDtMTWT8WiSwenhaeN29K4tHN/SNl
8q6M1XppaoL7Zeyh1bEX1ie/r6nzU954xT+nJLiGH85Ymv3CnJHu3nz01L7swb1GJfL8kT8y
6oWiiQtlowmuk0q/1kr0m5icZ5cGLRLbL+VNcJ30e290YvqgfdnMc1v6mETtupOzmWf/sZmJ
Jms+irEOD82cnrjpsF3fdn5jpycn6kRzx1iTZeWnJZ6fNifMtbr22SmJc8cOhn/O6OO+t0qu
58xoTjO5jKuMq43cRh5xjWlekc80v1HAKGhcaxQyrjMKi+tNi4gbTOFGo6hxk3GzUcy4xShu
lDBuNUoapYzbRGnT240yxh2GH5PxoayRZpQzyhsVjDuNikYlo7KoYlrVqGZUN2oYNY1aRm2j
jsF4dY16Rn2jgZFuhIyw4JtIFo2LsKHRyGhsNDH4mayZ0Vy0MG0pWplCa9HGFNqKdqbQXnQw
hY6ikyl0Fl1M4S5xtyl0FfeYQjfR3RR6iJ6m0Evcawq9RR9TyBB9TaGfuM+0vzHAGGj44xtk
frAxxBhqDDP8MaLDjRHGSGOUwfH6Y0VHG2OMscY4Y7wxwZgoJpmyBpONKUamMdWYZkw3Zhip
68B63G/MNGYZs405xgPGXGOe4dcEnW8sMBYaiwzWx68NuthYYiw1lhnLjRXGSrHKNMNYbawx
1hrrjPXGBmOjwdrBJmOzscV40NhqZBjbjO3GDmOnscvYbbD/PcZeY5+x33jIeNh4xOD8HjAO
Go8ah4zDxhHjqPGYOGZ63DghHjd9wjhpPGlkGTEjbmQbrHfCOGU8ZZw2njbOGM8YnLdnjeeM
540XjBeNl4yXjTbGMOMV46xxzjhvvGq0MFoa/rriGoMMg2sx9RrFc4yQem3jOefg7wfuDWDu
HY12Btca4FsbzAvwF/4Ppm5Oewbmsmt86MT0axdmBTkKbmiw4saVQcaxSqE3XjwTPD+yW/iO
HQeD/Z0fC/9zQ6/g7ZFZ4U+6rQ8mH/43HB0/K7j1UuHgQo7ewbHeBYMqPYcFthQ51jzVKcix
f2r9se/fGeRYvrRB0U//DtdbVj/C9meOtI9Qbx/TKFLuszlhxkfZ/+UFxcJlcrWPoE+2ahsZ
dWlLiP3dmfuDMPt7v03xYHqZahG0WVbFiN9vpXdquHnMrxUNfvq4SFDZ/g1g5qEewYfhu51m
//Zy+GibNcGBZ/Y1KHPbsWDiP7PDi1ZnBXfbPr/Z9ELAfnb+8HRQtkCx0IxncwevHBrYgOMn
P7z5TKhUiZyhwhVKhOl/vHV1G6d8/eWr7nHHWnfq9uB02/fCK/YsD2p1vCXod3lB8PP1NYLL
q+YFdR+JBGvmz3XzoS6zsLf7fHCZ4cGjbYtFmF/Pafkj1GfSrol0+n2Wy4/+uiP4ZMI/wd/P
rg9+e/Xr4Ny7B4Ocf+WNvFHubFC16+sB52XZvZ8E3Q6+HBSu8F7w1rwXg3Y7bojUnns2mDW5
ZKTyprPBhWdrRO78/pWAdeb8FWjeLEJ/95GtItd/9ELA+jLOkUX1IpxP1pXz+dHFShHOY9/P
zwech/UrzgVjb/otzH5ZD+bD+uUsdi744p5xbp4c/4maOZPn146DdeC4WIfChwpEWIfTtQva
vNoHBxdvDrgOWC+Ol/XjOG9+56wbj/PD8bJ/rsfHC7zilPPEfJdcPhs8M7ZNUGLeuWBQ3+XB
n5WrRV7JszH0VbHqkV13nAy93LBZpOWZNaGxf1SLlNr3Vejfd6pF2hUtGH61TAlXo9SPHf83
4PN1+a4E1CW//cTVPw/+1NU7f3nX1f+Z+p6r313+uqv3lXnD1b81O+20xdnTLn/5zSedXu72
pMvrFNzm6s5PbHX1ksvtXY2yv15HEmH2/1WOp8LUeQvd7ur9f5d1dcbu0yE+bzj9pRCfnzpX
39UZd7ZxdbkJyf1P/Ce5/79yZ7nxyy9I7n9AKLn/2V8m9/9d1w7uc5Txbh15Krm/eHL/M+eX
cXWFieXc/juufya5v1vPJvd/PJKsr+vk6p1bWrp1HPJpS7euB75s6vT0/qYuz8hVz9Wj3q6b
7EtPrv8QU/b/6WfJ9X+2fnL92xb/1M2v9Ibk+r9a5j1Xl3kkuf4vn0yu/1udkuv/0Pzk/i+8
lNx/w85NI/bvuMJZm1s4bdi5bCT08KYQ55vr4vduxSOl/t0UujGax10v5/v+G5A/ku+TgOul
5YhPXH3DwHedfvrc20H57QtDt7z4gqu5/qh5TnC9ff7Ea07P/f6a+/zNnk875bmypdbO0Pa7
slzddcA2pzx/ImX2hjj/7Jfnx9gR+0M8T5bfst89d74suS90vm92mM8zbivplOcO4/EcytF5
c6jjbU+G3Of2fGI+GWfTXJ17cXL/de58xs1zxJdZ7rjOz0nOo+Xy5DyeSyx389574/iA9eF6
YLwHqrUNWJ+flv8e5vhWlEq4/V+eWiLM+lzcUMrVo7Njbn+j39vp9t+5b1u3vjxPmA/Pl0M9
NoYyqt0RcmrzZPxV5Vu5Pp5DHM+6cs1c3blyPac8r1gfrg/6eY6xPjzXWB+ef6zP6cXJ8zZ5
S/J88RxkPJ6DrE/jtcnzx/OK+Vwp97o7vg1Fkvs//HErN88lrVu762Ts3e8EXDcltn7o9FLR
z5xOan2N+7x0wVuT19OS6k7rD0peZ8cOJ6+zL3olx5lpc2Wci9v+cfp8/4r8W8Lw8/8edVr3
yavcuCef65zc37zlTve/tNPpqbUHnM5fdMTpt1cfcxpretzp3I0nnHbJ/6TT0HOnnD566Rmn
GWf3uP2uOH7Zaf2id7r9Vnj5mNO7muZxffcV7ub012Wrnd7x3kmnt3dPjjfvSHK8Vtcn1+WX
7sl1eeaLT11fjjL/OB32cz63Hv1DtznNs6um05v+eim4v926YFF4YbCxyMIgx0svBr88cjJg
P+c3vxgceu354JvIqcD+/W2wdMszwT+dE0Ghmi8EN8RfDjL/7u22GxPkD1Z0KxC03Zs/YL6j
isxJZ/6/1tuR/kf7l4O1r+cLxhx4KTi754kw478wpnz4Ss8X+HsqxPzfXLwjxPGUHxiE2G/Z
9VfSOd4BXR5NZz1ee+eF9BzN3k5f9djh8KmVj6U/88I/YdaLvpn5/kgvN3pYeGbwfXq1xQvD
rOeALlVD24/kDrGfHE/nDNW/3DicMS5H6IGt7cKs+8UqK0IzP2kRKlT009CpFv+m53/wnrB9
35Pe58427jhYh8NH2gS3r345uLPX8oA1yrHrUPqYEksD5vFu/Z0B47NOzIN1uvh1zdCyUong
1PjVoWNjzgQ5/voqdP/u54P+/X4J9/zWtrc/9q2b+5nbvn1z/ipTIL9aHs0t8HkE/hp5NK/B
dvkMPgN8fnm0gFHQuNYoZFxnkBVWfb1pEYP8BsOPg7/RYNuixk0G+yS7WR4tJm5RRg++uMDT
Q42yDR4tIfCMS42yb2BOvgd/q2q0pMCXkkdvE/jSBp+z7e0CX0YevUOUVUZfmsF2gC9nsL/y
hp8PvoJq9E551B87vqJqtJKorIw+fBWjqlHNqC6P1hD4mvJoLXm0tsDXkUfrCnw95fVN/Zj4
BqrRdHk0JPBheZQLGCLK6Isafkx8Q9UoxwT4RgbHyzXLNdLYaGI0FfhmAt9cHm0h8C3l0VYC
31rg+RkP8G0N1p2fAVlrwLPmgG9vsMb0s74dDPKO8mgngzVmDp1VdzG9y2C+dxt8Bl0Neu4x
uhndBb6HPNpT4HvJo/cKfG95tI/AZ8ijfQW+nzx6n8D3l0cHGAONQcZgeXSIwA+VR4cJ/HB5
dITAj5RHRwn8aHl0jMCPlUfHCfx4eXSCMdGYZEyWR6cIfKY8OlXgp8mj0wV+hjx6v8DPlEdn
CfxseXSOwD8gj8415hnzjQXy6EKBXySPLhb4JfLoUoFfJo8uF/gV8uhKgV8lj64W+DXy6Fpj
nbHe2CCPbjS4VjcZ3QR+szzaQ+C5Lvl8i0EN+Afl0a0Cv00e3S7wO+TRDIHneuXznQb1LmO3
sUf1XtN9xn5lD8mjDwv8I/LoYIEfavD5AYMa8OSAPyjwj8qjh+TR4QJ/WB4dKfBH5NGjAv+Y
PHrMoBfv+8iOC/wJefRx4wnjpPGkPJol8DF5dLLAZxp8HjeoAZ8tjyYE/pQ8+pQ8elrgn5ZH
zwj8M/LoTIHn/uHzZw3q54znjRdUv2j6kvGyslfk0bMCf04e5R4D/CKDz8+rJsOTA/5Vgb8g
j74mjy4R+Nfl0WUC/4Y8+qbAvyWPvm3Qi/d9ZO8I/Lvy6HvG+8YHRnd5dL3AbzA2Gh8a3NNr
jY+M1dKL8tT4ldKP5anxy6WfyFPjl0o/lafGf6YaXSzwn8ujCwX+C3l0nsB/acw1vjLmCPzX
8ugsgf9GHv1WHr1f4L+TR6cL/Pfy6A/y6FSB/1Ee/UkenSLwP8uj/xG/KKMP/6tq9JL4TRk9
+InS3+UnmF42xkn/kKfGj5H+KU+N/0s1Okrg/5ZHRwj8P/Lov/LoMIG/Io8OEXh+0KBGB5oA
PqcxwGwu0/tMAX+VarSvZYC/WjWaWx7tY58DPo9q9F7LAH+NarSnZYDPqxrtbhnguUfWGKuM
9wT+HWUr5Knxb0q5v/Hc/zwvXjV4Zj1jvGTwnJlvnBX4l40HDPromWnMMM4I/Gkj04gZCYNs
mkEOeHKUPvxkY5KRJfBPGOONscbjAn9c2Wh5avxR6Uj54aZDjYNGP2OHsc8YbAwyHhb4/UZ/
gz56ehmbja1GhtHb2C7w5Ch9+Hx2HvIbBQS+oDx6rcDb/wiGA3+dwbaFDbYB/PXyaBGBv0Ee
vdGgt6jBZ4C/SR692Shm3CJPjS+uGi0hj/px8LeqRv3+Spr388GXUo3eZpQ2bjf4DPBl5FH6
7jDKGvQCPk0eLWfQU97gM8BXMPjsTsNvi2cf7Lui4eeGr6Qa9WuLr6warWLQW9XgM8BXk0er
y6M1BL6mPFpL1FZGXx3Dj4n3++O8Mx/+SNy9YnfTf/1bhf/1WfLfheRy3cnvTXzfVdo++dnM
KOqzkOtPjne1eT67Rhk9PsMzHnVuw39GhvdZ2Lzvy2PO95PR47OANo3H/vjsOiLL6PEZnow6
r0Hd0PB9PosqY53yGfQ/qYw5+Ix+tqXOb1CfNMjo8xmfk1EXMKh5tvg+n/E5GXVBw/f7Pp9d
S5v68PSfILKMHp/hyagLGdRHDN/ns9IpGetG/y3KOA6f0c+21IUN6mIGGX0+82vPupH5fvqo
r1d+sykZfT5DydAiBlrU8H0+Q8nQGwz0RsP3+QwlQ/ncq+/zWUP7zI9HBn6/zMHXN5mnz8+L
2h9Hak8F9XG8jEOPXyvWg4zarzPnhoy6uME+yBif+jaDjB6flVDm50B9qzK/T7K0lD72Sc8O
ZX5eZCWV+XlRl0rpY25kjZXRx9zo2aLMz59skzKOg3lwDKUNjoM5++wOZVxPZKWN2w36yJgb
9SGDjB6flVHm5099QBl9zJfsYErG3NjnPmXMxWdllVEzX+o9yujz2W5lrF9pgzVuavhzVNoc
WTmDrLR95Riomxu+z2fllVEzX+oWyjiXPvPXFdcaGfWdBuNRc1zULQ0y+nxWURk1x0XdShl9
PqukjJpjoG6tjD6fVVbmj5O6TUofx0pWRRk1x0XdVhnj+ayqMmqOi7qaMvp8FlFGH8dKTztl
fj3Iqiujh2Ol7qCMPp/VUEbNsVLXVEafz+ooo4/joqeTMnp8VkuZP3bq2il9HD/ZG8ro41jp
eUsZPT57XRn74LiYxzllzM9ndZVRc6zUryijz2f1lFFzrNQvK6PPZ/WVXaWMukFKRi9ZWJlf
N3peUMa2rBNZujJqjp/6jDL6fBZSlksZ9WlluU3ZL/sMlOVRRu2vDTKuGeqowb2Q176SUTc0
yFhz1rORscYg4xnms8YpGb30bVTGvU8fPU2UUbPu1J2V0eezpspKK6NupowezgV1e2WlTX3W
XBnPCDLqFsrKKKNuqewOZdT+PueeZlvq1gbHy/1LRt3GICtnX8mo2xpk3G9k1P5+494io/Zz
JuNYqDsYbMs9Q0bd0SCj5vqh7mL4Pp/5e4v7g4z6HYM+1plrijVeZfjxfLYyJeM6Y/ylyhjL
Z3cpo+Y6o07t89nd6qPm2qNerozxfNZVmb8+qe9J6eMaJePnFOZMH9coPSsMMn8dk3VT5q9j
6u7K6ONaJuNnJ7alr6FBT0SZv97Jehj0NbSvjQzqngYZfT7j5zXfx/VNT1gZPT7rZZ4+aq55
6nsNMvp8xs+Avo9rnp4NRNZHj896K/P3BXUfZfRxb5Dxcyjb0sd9QE+6Mnp8lmGePn+vUPcl
sow+7pcMg5/hfB/3Cz31lfl7iqyfQZ+/p6jvU0Yf9xUZPyP7Pu4rerYbZP7eI+uvzN971AOU
0cf9R8bP72xLH/cfPfxbRTJ/j5INJLLM36PUg5TRx31Kxs+Dvo/7lJ79RLatv5fJBivz9zL1
EGX0cT+T8fsEtqWP+5kefv4k8/c82VAiy+jhfqYeZvg+n/G7J9/HPU4PP++S0eOz4USWUXOP
U48wfJ/Prta29HGP08PPy/TR47ORRJZRc49TjzJ8n89yaVv6uJ/p4ed2+ujx2Wgiy/xzgHqM
Mvq4x12PtqWP+5me4wbb+ucA2Vhl/jlAPU4ZfdzjZH8oo497nB5+x8B4/jlANp7IMv8coJ6g
jD7ue7LflNHHPU4Pv1tgW3p8NpHIMv8coJ6kjD7ue7JflNHH/UwPv1dhW3p8NpnIMv8coJ6i
jD7ue7KfldGXYdBzymBbejIMskyDLMO+9jWopxq+z2c/KMsw5X6mh98F0UePz6YRWeafA9TT
ldHHPU72nTL6uJ/p4fdKbOufA2QziCzzzwHq+5XRxz1O9o0y+rif6XlemX8OkM1U5p8D1LOU
0cc9PtP4ymC/9HE/08PvwMj8c4BsNpFl9HA/U88xfJ/PvlBGH/c4PeeV+ecA2QPK/HOAem5K
H/c92afK6OMep4ff17Ffenw2j8gy/xygnq+MPu57so+V0cc9Tg+/02Nbeny2gMgy/xygXqiM
Pu57so+U0cf9TA+/H2Rbeny2iMgyau5n6sWG7/PZB8ro436m5z1l/jlAtkSZfw5QN9J+6eMe
J3vfYB917WvIWGosM3zGPU69ksj66PHZcmVhZdQrlEWUUYe03wbKGGuVwXh17CvjUa82fMZz
hHoNkfXR4zM/Xm1l9Kw16CPjOUK9ziBjO58Fmgt9PFvo2WjQR4/P1itrrIx6Q0pGL5n/3qep
ebalp572cYsyxt9ksI/i9pU+6s2Gz3hWUW8hsj56fObHK6aMngcN+simGNRbDTK281kDzYU+
nmn07DDoo8dn25S1VEa9PSWjl8x/79PaPNtuN3YajHeTfSVj/NSMXupdhu+bqnq3Mnp85r9/
uU0ZPXvUV0oZ9d6UrK3qfcqoGY8eP14J8+T07DeYC1l7g/ohw2fTVB9URo/PHlZGzbOZ+hFl
9PnMf59T0jJ66fHjkdFHdsBgv7faVzLqRw2fzVB9SBk9PuN3/PQVUkbPYSJl96s+ooztfMZ/
K6DvWmX0HCVSNtMc9WMGGdvNNMj4bw6+b5Y5ek4QWd9M++qzY0SWdVVGfZxI2UxzZP57pG7m
2ZYe/nsFfQXsKxnjP26Q5bevZNRPGD6brfqkMnp85sfLp4yeJ9XHruijzkrJ+LuIOqaMHp/x
32vYL1/J6IlTKHtAdbYyenzGf+fxfXPN0fMUkW1Lj88Synoroz6VktFL5r9HyjDPtqcM/vsV
4+Wyr2SMf9ogq2VfyaifNnw2T/UZZfT4zI9XUxk9z6iPjL8rqZ9VxnY+47+ZsQ/6+HuRnhcM
Mnp89pyy/sqon0/J6CXz3yMNNM+29LxoMF4N+0rG+KkZvdQvGb5voeqXldHjs7Kac3Vl9Lyi
vmrKqM+mZINVn1NGzXj0+PEqmSen57zBXMiGGtSvGj5bpPoNZfT47IIy6sUG9WvK6POZ/36o
imX00uPHI6OP7HWD/Va1r2TUbxo+W6L6LWX0+KyM1qqyMnreVh/ZUtXvKGM7n5XWtvWV0fOu
+shGq35PGTXb0uO/l6JvrEEP/12XOY+zr8uM943GysakZB+Yp2+UMuoPiSxju+UGdRNtS5/P
PjJP3whl1BcNMnpWGBcNvy19PvvYPH3DlFF/QmQZPSsN6hHaL30++9Q8fUOUUX9GZBk9qwzq
+7QtfT773Dx91KsN6uEpfT77wnL6BtlXMuovDTLqNQb1MG1Ln8++Mk/fAGXUXxNZRs9ag3qo
tqXPZ9+Yp+8+ZdTfEllGzzqD2m9Ln8++M09fX2XU3xNZRs96g3qI9kufz34wT18fZdQ/EllG
zwaDerC2pc9nP5mnj3qjQT0wpc9nP1tO3732lYz6PwYZ9SaDeoC2pc9nv5inr6cy6l+JLKNn
s0HdX9vS57NL5umj3mJQ90np89lvltPX3b6SUf9ukFE/aFDfpW3p89ll8/RRbzWo70np89kf
ltN3j30lo/7TIKPeZlB31bb0+ewv8/RRbzeoe6f0+exvy+mj3mFQ35vS57N/LKePeqdB3SOl
z2f/Wk4f9S6DuntKn8+uWE4f9W6DuldKn89yKLtbfdQ5ldGzx6D229LnM/+7pS7KqK/StvTs
Nah7KqPPZ1cr66SMOrcyevYZ1N1S+nyWRxn1foP67pQ+n/nfzXVQHzX/Jox1oechg7qzMvp8
5n9P2E4ZdfLfpcyM0vOwQd1S29LnswLKqB8xqDul9PnM/26zjfqo+bdQzI+eAwZ1R2X0+cz/
nrWVMurr1EfPQYO6vTL6fOZ/59tCGfX16qPnUYO6nTL6fOZ//9xMGTX//ok503PIoG6rjD6f
+d+FN1FGXVR99Bw2qP229PnsJvVRHzGo2yijz2f+9/eNlFHzb7yYHz1HDerWyhqlZP6/JUSV
UfNvwNiW7R4zqFspo89n/r9rBMqob1UfPccM6qbK6POZ/28s9ZVR++8Zxiqjdv8AyuYy0rKl
Bt9r+O9VyJYY1P73Q8OVUfvvh8gWG9R3GBxbhn2dZ6RZXUFZP6vnG3xf679XJqOP2vf1svoB
407LKmpbsjkGdWVl3ayebVSy2v9+t4f66KmiPjL6qH3fXVbPNPiZzP+cR3a/Qe1/P95ZGbX/
WZJshkHtfy/fURm1/3mVbLpB7X9Obmr1ZIPfd6QbrFVz+zrF4PcO/ncZZPRR+76I1RMMfjcU
0bYNrZ5ohK32v/cho4/a93FdHDc43/564TrwWUONt0IZ9Qhl9JGTNVI2Thl1Y2XLlFE3UcZ1
yj7YZ7OU7IRl1P66p8dnzdVH/bhB3UIZfT7rq4xnIr30dErJ6CPzz1OesWTUndV31Gq2ZR7+
/uWeJqP2z4PDyqg7aFueTeQ8W/xzjWcdGbV/TvLsJKP225KxD+qOBtcBz2cyan8c/J3CnJlv
F/U9aDU5tf8ehIw+srvUt0UZtf9+aJtl/B3H32291UfGeGT++5Ktyqj9PnZZttfg70//9y8Z
45F1NziOncqoeyjboYz6XmVsy9/pjOW/F9iuPnr8/Pi+jmPjGDK0LdkTBnV/ZfT4zF8bXC9k
1P3Ut0oZ9fCUjF6y+5SttJqM2t8Lm7Qt+xygvo3KqAcq26CMepCyNZaRUw9OyZgf2bCUbL1l
9AxJydZZRj1U2Wqr2Zbt/HHkvHLlj1+uXPmo7lu8Y/XbK9u+NfnT+OtK4l+iBss+rb9s12S+
uv9b9GWFZX8l/ryy/M8rS/+8cv+/1tT8nysp5f2XrnzE5vz5pY+TKz862bb36067W6zeOSTz
xharS5fMseiufJ1Lt17zSYUcN+a7sNP9cxObnfuzYcHWho9tKtWIYkEysq//My8T/K/h/1/N
/9rvrSk9rKpb2ZTsv9s8Vr7cmMd+7pk5C7mXMuZoaNmdassrRf73erXiumnJX1UcsLlf/1nD
eM03Hwwv7/Fg/dx9Z8UM599qG7G8ZEBuGrfa+ZNpofiTLe90vvTGWnHDecvi9pnzC65vHO/w
4qe7UsaMyYfZB77Fl4/fQV9y/AfDzAOv+bgezUE9bg7Oa1/Oaw7Oa27qfzDmx+Q4GIvxOQ6O
R/sy/6DbF8fE9uQcE+PiOSb2h7f5Bg2DSnvwrJNfq8ofHy/LZ+SMZ/t1HvVrq/2qx83HeY3v
vPbrvOajfrc+zqe+si31NVUX/m0cL7B8W3h1+dJZq6s1jdv/NMId+K/qNI6fzH49hu+V0dB6
bovjny0Uip88X9V5lJqcz+nDsx3b4+1/lmEX4yoP+9z6g//qP1818OOYBn58+zzw+7XtAj8f
Gy+okbfyHsZU7uav/oBc4zhv4zG+89pvMs9+nfk4b6+cLMu4mifz9/0cVzJPHq/zzJdx6d94
QxA/+Vj14J8tO7Ny3RSJ199TI1j/8UtZlsXtM5dbFrfPXP5pi9vjH49r7PKOZcvEd01v4vK5
+d+KzWjf1OVDq78de6FHM5fbOSm7tV1zlzfOGFB2d68Wvj+c0h/2/TZ+kDJ+4MdnjinzCfx8
yFLmH/j5MwZjcVyMYXN1+2WfNtcwOfu0uYY5XuYYG3/DHnLmaK/u20Ou/lhKf4xc48dTxo+T
az4uZ46sHbnm73LmyFqT63hdzhxtri5njrZvlzNHm6vLeaWgzdXltra7bK6+n/X3/ay/H5/z
5ceP+/F1fl2u8+v6bf5cDy5njn7+jMG51/HGOffMn31y7rU+cc49OXPktYLkzJF7k3y1vZr1
0xY73Pr/Uq65jbPTrf9dtVvEYzl2hWuUu5R1vFHLeIUPdoUH1rkudiizlRsHn/q6utTX2PUZ
1yJed9q7MXpSX3VXYWUzG+eOOHnq6/BSX5P3RvGG8foLarme1FfpkfEZ26a+bo/xGJc89ZV8
7J95kKe+to9zxDGQp77aL/WVf7Zt2G+b+lpA21fg95X66sDUVwraPAM/z9TXDloW+ONKfTWh
jRf4NUl9fWHqaw1TX3eY+hrE1Ncjpr420eYe+PUfML9pEMtxR5zzeOOg5kHHru/E3DlNeeVi
6qsYbW2C5acv7WZ9Ul/XmPoaR43vrofUVz3qWAK2TX0dZOprIrUOrif1VZJaN5envm5Sa+7y
1FdS6hy5PPW1lXs3Ny3LMTCH1Fdbpr7yUteG60l9LaauJZenvjpT157LU1+vyXlm3uwr9dWl
w4tF40+sqxmwzqZxq53nPHA+yDkPnA88z+GHhrX0edjn1h/4fsbz46B+fJ1ft63Or7tnGa9x
xue7GV/9cc2HcZzX+M7bfNiv8zzTbHufM0/fz/yd13E5z3jUjM/nKddb3F9vjMfzh57/r9dZ
+ldYpr7aMvnd6//9f04ol31wlXG1wOcWeL475s81hv9eGs93xdRoPoHPL48WMOgtaPAZ4K+V
RwsJ/HUCX1jgrzfoK2L4cfB+HzeY93PA36gaLWqQ3WRQA/5mebSYQd8thh8HX1w16o8dX0I1
ys8a9JY0+AzwpeTR2wS+tDx6uyijjL47DD8O3u+Dc8EcyhppBucN8OXkUf8HX14FynkAPOcA
8BXkUdYa8Pz0g0dZf8BXlEf9OcJXUo3684ivrBr15xpfRTXKuQR8VXmU8wt4riXAV5NHObeA
ry6Pco4BX0Me5XwDvqY8yjUA+FryqL9m8LVVo1wvgK8jj3ItAJ7rAPB15VGuA8DXk0dLC3x9
edRfJ/gGqlGuG8Cny6P+esOHVKNcT4APy6NcY4DnegZ8II9y/QE+Io/yfAB8VB71zxB8Q9Wo
f87gG6lGGwt8E3mUX60Cvpk82lzgW8ijLQW+lTzaWuDbyKNtBb6dPNpe4DvIox0FvpM82lng
u8ijdwn83fJoV4G/Rx7tJvDd5dEeAt9THu0l8PfKo70Fvo88miHwfeXRfgJ/nzzaX+AHyKMD
BX6QPDpY4IfIo0MFfpg8OlzgR8ijIwV+lDw6WuDHyKNjBX6cPDpe4CfIoxMFPk0enSTwk+XR
KQKfKY9ONejF+z6yaQI/XR6dIfD3y6Mz5dFZAj9bHp0j8A/Io3MFfp48Ol/gF8ijCwV+kTy6
WB5dIvBL5dFlAr9cHl0hj64U+FXy6GqBXyOPrhX4dfLoerFBGX34jarRTWKzMnrwW1SjDwr8
Vnm0l8D3MNhum0Ef4LfLozsEfqc8ukse3S3we+TRvQK/Tx7dL48+JPAPy6OPCPwBefSgwD8q
jx4S+MPy6BGBPyqPPiaPHhP44/LoCYF/XB59QuBPyqNPCnyWPFrWyGVcLU+Npz/NmGCUE/hx
8mh5gec+p0YrCDzPBWr0ToEfIY9WFPhh8mglgec5RY1WFvhB8mgVgR8gj1YV+Pvk0WoCz3OW
Gq0u8H3k0RoCf688WlPge8qjtQS+uzxaW+DvkUfrCPzd8mhdge8ij9YT+E7yaH2B7yCPNhD4
dvJousC3kUdDAt9KHg0LfAt5NBD4ZvJoROCbyKNRgW8kjzY0uAZjhr9u8XHVqL/O8dmqUX9f
4BOqUX8f4U+pRo8I/FPy6CGBPy2PHhT4p+XRRwT+jDz6kMA/I4/65w/+WdXoboF/Th7dIfBb
5VGei6uNtcbzAv+gPNpb4HsZKw22eUHg2ZYazRB4tl1msM2LAk8vNdpP4DOMJQbbvCTw9FKj
/QWebRcabPOywNNLjQ4UeLadb7DNKwJPLzU6WODZdq7BNmcFnl5qdKjAs+0cg23OCTy91Ohw
gWfbWQbbnBd4eqnRkQLPtjMMtnlV4OmlRkcLPNtOM9jmgsDTS42OFXi2nWKwzWsCTy81Ol7g
2TZmXG00Fk2VkeO5x9Dm8tT4bGlLeWo89xjaWp4af0raVp4a/5S0vTw1nnsM7ShPjX9a2lme
Gn9Gepc8NZ57DO0qT41/1uhhbDW4r8i6GeSAJ0fpw080Jhl+bfGsNzkZa5tlHDfKCvzr8mia
wGcK/Bvy6FSBny7w9wv8PHn0AYP9njSOC/zj8o+Zsg/AH5VH3xT4w/Loo8YB42F5avx+1eg+
edSPg9+jGt0ldiqjD/+WatTPDc+x8fl2gxrw2+TRpQK/WR7dJI8uF/iN8ugGsV4Zffh1qtEV
Ar9K4NcY7Hux4eeGX6QaZf6AXyCP+vM027w/j/iZBs+w/+c/M6P/7XWTyddKutc1fpny6skJ
+zMTg7t3d693/PHbqYnIsFkxXr0XLZOZ6PVzzjivdfsy5ZWU3945OvHND7Oz2xUcFdmeMTKx
Mefe7BHPVIxUntwskadc4UTb19dH5ueumRj0a40ErwK8/5HCiUk3NXP5igX7suvcOjJB/8OV
52ZfeXdUgnFSX2G5p0/u+JjSme51iqMmbY9N/jL5ekS9JtK92rJL9xHhLvuSr0F87Mzi8NJv
kj2ffvx7uE1actvUV15GH50Tefq60W5fF6N7Ik1nJ+dwb9nC0b5TknMr+WeN6IUryTk3LNos
Wv5g8liK1hoZbZ1nnzvG8ZdGRe8f8YA79tRXZFYqmRn9j73GjrUq/PXU6C322jvWUK/LdGv7
4P7M6EF7bSKvurvmu6nR9fb6PHq+LpMZ7WSv2GPb1FdqflhmdHR9mTkR1mfnsJHRzqf3RFi3
9ZnNosfLFI6yzi3G1Yx2n1cjyjqfe7RwNN+NzVx+ec7eyGetRkbpL/jHA5EKn4yKMk7qKzgP
7s8TnLot+XrBInV3hLt/mXyFol4b6l7NuXnC0NiMfclXJV6bZ3Fs3zfJnmc6XIp9n5bcNvWV
nV98PCf7QN7Rbl+PN92b/cNdmsPthROvTE3OrciSGol1I2q6OV8o0iwx8XDyWK7O3TWRfvMf
kRXfzYqkvu4z9TWgqa8KTX2FaOprRlNfP5r6WtLUV5emvtI09bWnqa9DTX1NauqrVFNfsZr6
GtbU17OmvrZV95q7Bhqtykwc7Py9uwa6xyYnWl2aHea1fXW2T0tsH5zf/htiWuSNRVMT31d5
MLwuEkTq9ZyYaFXg/ljkz0WRHlmZiWVXn4/xmsLU1wJuvrd34oOfNmUPufh85N0fOiTu+aJQ
4tKQKpEav6clbqqQliid51zkjbeLJ/r80cxeWdo4cvu+rdlPjuuX4NWWl6ovy3572Uh3XzTv
Uzh++oHkPbX7uWvjf1w7NZFZtlmk6FXbY1uLJF9FGr60Krazhr1W8PUhkWuy64QXvZp8DeJt
v04Ln7BXrvK61S8f/ir84/Hk6xRTX7M44NzGyGvLeyeY5/qBhaI//tvBvfa55Ja0aO3P0xK3
vPxK5PD1TaP1h97qXsXY99X7ogvKb8uOffXwf3vtY+rrIO0JGPXPPr2q0r1W8jN7NWguuwd5
Be0ToczoKnslJfdX15pTo6/aqyo5rp6PT4zOt3uQV51WO273r73akrW90Dwz2sXuR14jm/oq
zAJ/3Ru98MPGyOWuL0U+PtIxWufva9391btouej5YWlR5j/uXInooWubRRl/49XbIjN29os2
qnsk0q/58kjXASPdfVG82PVBtweS99SM6gWDx6pNjXJeXuuxN1w/Nim6cPvMyAOPLgmXSE/e
XwuKZsROWQ9jPlx7UaxxMCn6w5wHIk2v/yVm73WNcp2kvk40o8+m7Jlf3htlnp+/eG1i4eGO
Ua6Hv4+lJXq9nJznsrRmiciREm7M/Nv6J+ruWRipGXsisurvUYn3Gzzgnjlt04clqk7ZF+G1
pH6Nbb0TOa3435FcNq+rDPRqkds0j3GNkdfIZ+Q3ChgFjWuNQsZ1RmHjeqOIcYNxo1HUuMm4
2Shm3GIUN0oYtxoljVLGbUZp43ajjHGHwfdwaUY5o7xRwbjTqGhUMiobVYyqRjWjulHDqGnU
MmobdYy6Rj2jvtHASDdCImwKgaAfOGHAzQHsAxqKRqbQWDBHaCKamgLHBc1Ec1NoIVgXaCla
mQJrCa1FG1Pge3bgXEA74c9Xe6s9ZB2MjkYno7PRxfDb3mX+bqOrcY/B99rdjR5GT6OXca/R
2+hjZBh9DT/nfubvM/obA4yBxiBjsDHEGCrwrEFpqV8Tr8MsH26MMEYao4zRxhiDNR1rjDPG
GxOMicYkY7Ixxcg0phrTDL5fn2Hcb3AeZxqzjNnGHOMBY64xz5hvsFasE/i19Ovj19qvvT8X
/tz4c9XStgW/Lv7ccp7Bn3t/vE0tA3+tcIzgryWuK2goqppCVPhrk+MDf+36a5lr23v/me/1
2/qx/NgNbRvw+/Zz8XPzc/Vz98fkleNMxa+BV782Xv2aefVr6dWvsVe/9l79OfHqz5XXvDaf
VPy59fo/sUap5xR/dQoLzP+fCv+vHLNz2c/4J54JXn98SbBky1x7ndXcYOLwM8H7VY856g86
Ezz99ulg2+cng9cLJRz4B147HZxr/2ywcVZrtx2vs1pnoEWXtA6uz3lNqGD49/CEXMVDjI9n
3PcSNcOMXaJtkxDjLD89IcS4tWc+HmI/Zz+6Osxc2O5t66Xv4i9NQmw30zLGOZUvd5jtqts2
bJcxdGKI7S7uvybEfJgHx8E8VrR61h3b0zYHtmdsxmMOjM/xsT1zYTzmwvgcH/tiux2FG3F7
5RjUt5rT9G7RyLpyaeEzr1WKXDz5e+jElkqurvXxza5G+bx9haud7lr1Z0DfmncuBuR9//nI
1atLvufqF7q/7eotf7zh6sHRC65mLvTvezTmauZIfV2B467mGKhfmbAp2W/HRs1xsz+UmuNA
S3c/FSbnuKkbfljJ1Rwv9cU3PwjxOevg6pOTXL0uX3IeQx5KzuPV3Mn9b70zuf/lo5P7X3c0
uX/OAeO4c2Hj3lg+uf8KTZP7/2ptcv8djyX3f97OHfvLMSe5/46Vk/svXSS5/w3PNHXr+Mmq
Jm59/6ne2NXHn466esvdyfMxYWJNVxfblDwfaz5Mng+U8Q+lJc/HgKXJ89H19eT5uONy8nws
vit5Hnr/mjwPFdOT56Hu88n9z1qb3P+WWsn931yIfE+oX+umtt9JoRonzttxTwrlrv2qrfue
UO/73nL6/DdvuvzHEh+5+s2DH7p6w59/uLrmkT9cnZznnlBy3pNC7ydquvGXfcZxTQqdrdHQ
1e8PbujqyQWS+3+6RXL/OVY3t/M1KdTwUlc7f3tCDUefdXrxi2ddfvhCWVvnPaGv+t5u531S
6NfLcVf3ei3m6uT52uPOG5/3umqzm9/ptpvd/K7+5LirS3U84eq1m+KurnRDtqtPpbdw+yl9
JrnfU+nPuZrXgbLftxcn9/vdtdmuvuur5H6T1+ked72y3015k/u1VyG6cZt8mdxvr7uT+319
W3K/Q4sl9zsqK7nuTRok1/3Bwcl1v+an5LpXvT257jc+llz3N68k1330ieS6J+/XPaHk/Tsp
dD5/ZbfOe8tXduv8QSPqtNBjvV2erv70Z/8o4Z4Hw4/mcbrrDjdu+tNbf+Ov5xx2P7E+6c8N
/sDVJ958y+m7/3J97Um/dtkFV7c+fs7VyftsT3rrqU+7/Isy2U5X1Hjcff7wtsddffYztz7p
mV1Wulrrlz56YxdXZ7yS02npB59kndPr//II3zbkqP9wcVePbnCzq3/653X+usxR+nXutz3p
p26a7eqLJcu7utvV3Pd70nktJ32reiXn07lycj7DNiXnw3OIz4u8e9Rpo01HnG4vfsjpzZUe
drr8o+S862efsHHTQneuo04L/Zux3X0+llcJ2h9dh+mD/tPO1Wfs1YbkFRYkj6dC9CFXt5yZ
PJ6Z1yWPJ2PHm8n5n56VPK6J5dxxXD7t7pP0w1e1cOdpxj1Nnf72pruf0nMVSj7fL1WpxXlP
z1+rivtc92N6m8PFXL3zh6uc9i+VPM8L7kue152vJs/zoW+T5zf5HLd125U8vwUPJ8/vD3mT
+7+1R3L/B+e550qoVK3zbh1qjn3TaSz6odOXBrGfNPc8QBvnY35poa+2Me+0UKEHkttvr17X
jjMtNPPehNNiP5e085wWOnUwy6mew6GnFme78TKOJPtmvp3cLm+JUq7vidPJfv29ERq0OXl+
Jj6dPF85Via3HzMpOc9e9ZPz/rNpcr75RiTnq7//QnU2PBtsr5kdcN3OW/684yHzhXPODzrk
mR9sSbwQ1Gm0xr6HeDH48tMeLu9RLU8QL/ZiwCusL49+Idg3/nCYbUfYNcs4s/dPTee+GG6v
uKyScTposuLpYM7N8SBXpeeCH9KWBvl/fSFo0KyFe510se/yuP1MG/9NmNdFc90z1ugmz7i5
ZWT2CQ0bcDpoeOnNdMaYaWMzvxyvFEk/V8OuyU4LGlS4brG7Bl8q3CJgvDob8tjnqxps3XAp
TN+w2fvD3F8XqxROn3lvND1vj1nhHF3vSn+xXs8w+2O+My/0To+ntwjnODwwvW44COf4YVj6
N/Z3IPvjuLgPv/z0XXf/LbzQO5Rhr+Uc2/F0iPvYtm/Aff7uVQcb8FwIPTczNK/0c4G9Qthd
4/YtnPu53r6Nc797uEo16r9PxecW+DwGf64x2B7wfF+NR/MJfH55tIBBb0GDzwB/rTxaSOD5
/QHg/ff8eH6fQB+/U/Dj4P0++D2DnwOe3zlQo0UNMn7/QA14fgbBo/xOgj5+L+HHwfM7CmrU
Hzu+hGr0VoPekgafAb6UPOp/5sOXVo3eLsooo+8Ow4+D9/vgXDCHskaa4X8mw5dXjVYQ+Dvl
0YoCX0ngK8ujVQSenwmp0WoCX10e5fcsgK9p1DJqG/7nTHxd1Wg9gef3MNRoA4FPl0e5aAHP
Qxzw3GR4lIcs4Pl5Fo82FPhG8mhjgW9i8DMaP7/6OeP5GZYabSHwLeXRVgLfWh71P4vi2wp8
O3m0vcB3kEc7CnwnebSzwHcx7jLuNroK/D3yaDeB7y6P9hD4nvJoL4G/V+B7y6N9BD5DHvXX
Br6varSfwN9n9DcGGAMFfpA8OtgYYgw1hsmjwwV+hDw6UuBHyaOjBX6MPDpW4MfJo+MFfoI8
OlHgJ8mjk40pRqYxVR6dJvDT5dEZAn+/PDpT4GfJo7MFfo48+oDAz5VH5wn8fHl0gbHQYJ6L
5NHFAr9EHl0q8Mvk0eUCv0IeXSnwq+TR1QK/Rh5dK/Dr5NH1xgZjo7FJHt0s8Fvk0QcFfqs8
uk3gt8ujOwR+pzy6S+DT5NHdAr9HHt0r8Pvk0f0GvXjfR/aQwD8sjz4i8Afk0YPy6KMCf0ge
PWwcMY4aj8mjxwT+uDx6QuAfl0efEPiT8uiT8miWwMfk0bjAZ8ujCXn0lMA/JY+eNp42zhjP
yKPPCvxz8ujz4gVl9OFfVI2+JF5WRg/+FdXoWYE/J4/OE3juL7Y7b9AH+Ffl0QsC/5o8+ro8
+obAvymPviXwb8uj78ijpwT+XXn0PeN94wPjQ3n0I4G/KI9+LPCfyKOfCvxn8ujn8ugXAv+l
PPqVwH8tj34j8N/Ko98ZzPl74wd5tKxRzhgoT42nN83YaZQX+O3y6J0Cv1UerSzwW+TRqgK/
SR6tLvAb5dGaRm1jnbFGHq0r8DzXqNH6Ar9CHk0X+GXyaCDwS+TRqMAvkkcbCXymPNrEaGbM
N+bKo80Ffo482lLgZ8mjrQX+fnm0ncBPl0c7CDx/z1GjnQSe+VGjXYy7jUnGBHn0HoEfJ492
F/gx8mhPgR8lj/YW+BHyaIbAD5NH+wr8UHn0PoNr8EeD6/A74yfjZ3n0G4H/jzzq7wv8L6rR
LwT+V3n0U4G/JI9+LPC/yaMfCfzv8ijzfM+4bPwhj54S+D/l0bcE/i959A2B/1sevSDw5+TR
V4ynjWeNfwT+rDy6QODnGaeM08a/An9FHl0s8AuNuHHK8D904dmWGl0q8GybZbBNTvsc8PTi
0eUmgGfbJwy2yWU14OnFoyutBjzbnTDY5iqrAU8vHl1tNeDZ7pjBNldbDXh68ehaqwHPdkcM
tsltNeDpxaPrrQY82z1qHDbyWA34a+TRzVYDfoPpIwbb5LUa8GyHRx+0GvBs95DBNvmsBjy9
eHSb1YBnu70G2+S3GvD04tEdVgOe7X40BhqDjSHGcIP7DfA/S0fKU+O5x9DR8tR47jF0rDw1
nnsMHS9Pjb8knShPjf9NOlmeGs/9NsWYZlwWeO4xdIY8NZ57DJ0pT43/y3jAOGdwX800Zhvk
gCdH6cPvMnYbfm3xrDc5GetawLSgca3AF5JHrxP4wgJ/vTxaROBvEPgbBZ7/iUFqlP8ZQfZ7
s8H+AM//RCD+FoN9AL64PMr/xB/g+Z/2w6MljVLGbfLU+NKq0dvlUT8Ovoxq9A5RVhl9+DTV
qJ8bnmPj83IGNeDLy6MVBP5OebSiPFpJ4CvLo1VEVWX04aupRvmf4wN8DYHnf4eJfdcy/Nzw
J+28U6PMH/C15VF/nuqY9+cRX9fgj8T9vs+uxih1LveJ/2xmlNJnFdxnyb6rzNOfpowenyX7
k696vdpy/xn7wPvsY23LdrkNlM/oQ32WQWQZn+cx+KyXQUaPz3orQ64x+KwihfUxV5/RT0ad
16DOb/g+n/E5GXU+w/f7Pp8Vp019jEP/9USW0eMzPBl1AYM63fB9PiuijP0VNOivpIyxfUY/
21Jfa1BXMcjo8xmfk1EXMny/7/NZYdrUd505309Gj8/q0KY+tvGfkdHjs1q0qY/14LNqRJbR
47MayhiHY+ezeso4Dp/5NWU9yKgbGIzHsd9gkIcNMtbXZygZeqOBFjV8n89QMpTP0eaG7/NZ
MWWMc5NBHlHGNj5D2Ra92UAbGn4fPkPJUMZGGxu+z2dNlbG/Wwzylso4Xp+hbItyfaIlDTL6
fOavXe4PPJQw6POeuqwy+qjhVmXeU3dTRh81pCnzc2AerZSxD2oopcx76jbK6KOG25R5T11a
GX3UcIcy+kqLdsr8Nv8Xe28CKN1Rl3l3SAIhbAngDhqUJQgcajl1qgpZ3gthFSFhk01JgBCW
ACEJqwhhh7CKiIAsISyyKCIu4w7ujqLjrt+M33zM6DjguOCIO5LveerUIc2b903uufS9b3X3
8yb/213/+6/T1d3PPb/616k6Rf8tqm96zvIDq49xLNO+sfqm5yyfVX2MY5n24CUf20B7aPWx
fZNv+kz5+dHH8rfD+Nkfj5/TZ/fI6uPv+VneGvbC4+gcz6eT7zZ0VR9jGfc/6IJvOebPq+9a
eGQM651efXygj+XbsoC6UwzL/6v6+MB69H0zC4jj+Yo+lm8Ho4/nGvpYvj2MPpZ5fJb/N2yK
m3x3qD6ef+hjuau+qV0sf6b6GMd20DedX3huoI9lA+NrTG1l+f9UH+PYXvps9fH8Qx/Lrvqm
98Ty31Qf4/i+6PPVd6PqY7mvvum9s/x31cc4vn/6QvXx/Ecfy0P1scz3z/LfVx/jJl+sPp73
6GM5VR/L/ExY/ofqY9zky9V3cvWxfKfqu171sfwt1cd6/DxZ/sfqY9zku3P13aT6WL5L9TGG
nzHL/1x9jJt8d60+nh/pY/lu1ccyvwuW/7X6GDf5DlXfV1UfyzvVN32HLP979TGO3xl9d68+
nkfpY/ke1ccyv0eW/6P6GDf5zqg+nu/pY/me1ccyv1uWr6g+xk2+e1XfV1Qfy/euPsZQAywf
dxyd47bgk+8+dMHH8yl9LN8XRh/PnfSxfD8YfSxTPywz55ziJt+30oU4nifpY/n+MPpYpqZY
PrHWZdzk+zY8Z9xp+Ekfyw+A0ccytcfydWrd05Z8D8Rzxt2i+lg+ky74WI96ZJl54xQ3+c6i
C3E839LH8oNg9LFM3bLMHGWKm3wPpgtxPGfTx/JDYPRNemeZ+dQUR83T91C6EPdN+Ekfyw+D
0ccyNc/yjWpdxk2+b8dzxn1d9bH8cLrguxl+Mo7lR8DoY5l/Lyyzfz/FTb5H0oW44/GTPpYf
BaOPZf4Nscx8boqbfI+mC3HXxk/6WP4OGH0s82+NZeYQU9zk+066EHciftLH8mNg9LF8CMYy
88Ep7hCe0Xc2jL4T8PMQ7GzYOTD6DuHnDozlqS7jJt9j8ZxxLN8dxvLjYNPxJt85x40+xt0D
xhjmq4xjzOR7PF3wscy/XZbPhU1xk++xtS7j+PfMGOZTjGPM5HsCXfCxzL9nls+DTXGT7/G1
LuP4N84Y5t+MY8zkeyJd8LHMv3GWnwSb4ibfE2pdxvHvnjHM8xnHmMn3ZLrgY5nnApafApvi
Jt8Ta13G8VzAGObLjGPM5DufLvhY5vmB5afCprjJ9+Ral3E8PzCGYwSMY8zkexpd8LHMcwbL
T4dNcZPv/FqXcTxnMObk6mPM5LsAz1mXZZ5HWH4GjD7GTb6n1bqM43mEMRzbYhxjJt+FdMHH
Ms8tLF8Em+Im3wW1LuN4bmEMx9YYx5jJdzFd8LHMcwvLz4RNcZPvwlqXcTzfMOaE6mPM5HsW
nrMuyzwHsfxsGH2Mm3wX17qM4zmIMdeqPsZMvufgOeuyzPMSy8+F0ce4yffsWpdxPFeVmOpj
zOR7Hp6zLss8V7H8XTD6GDf5nlvrMo7nL8Z8AcY4xky+51cfyzx/sfzd1ce4yfdL1cc4ntMY
8/nqY8zke0H1scxzGssvrD7GTT6OrbAtjOM5jTH/BqOPMZPvErrgY/lsPoO9CDbFnc1nMG6J
MMWdg2eM+Re6UPds/Jx8L6YLPpYfC2P5JbApbvLd+bjRx7jHwRjzT3ShLmMm30urj+XHw1h+
WfUxbvIdqsdj3Lk15nM1jjGT7+XVxzLPfSy/ovoYN/nOqMdj3Hk15v/WOMZMvldWH8s897H8
qupj3OS7Tz0e455UYz5b4xgz+S6tPpZ57mP51dXHuMl3/3o8xj2lxvxtjWPM5HtN9bHMcx/L
r60+xk2+M+vxGPfUGvPXNY4xk+911cfy02Asv776GDf5HlKPx7in15i/qnGMmXxvqD6WL4Cx
/D3Vx7jJx20NqA3GPQPGmE/D6GPM5Htj9bF8IYzl760+xk2+R9fjMe6iGvOXNY4xk+9N1cfy
xTCWv6/6GDf5zq7HY9wza8xf1DjGTL43Vx/Lz4Kx/P3Vx7jJ9/x6vFvBx1jG/DmM75c+xtH3
Ftjke3Ytv7X6GDP5nrd0vOfAz5h31DjGTL63VR/Lz4Wx/APVx7jJ9131eIx7Xo2ZjseYyfd2
PGf7WP4uGMsvrnUZN/neiefT+2Asj3VJjWPM82GMeReMcaw7+bhFBX2M+24YY15SfYyZfJfh
OeNYfgHsMti7YfQxbvI9otZl3AthjHlp9TFm8l2O56zL8iUwlj+8FDf53gM/41h+EYzl98Lo
4/Em30Nr3UvgezGMMdPxGDP53ofnrMvyS2Asvx9GH+Mm31n1eIx7KYwxH6o+xky+H8Rz1mX5
ZTCWPwCjj3GT79tqXca9HMaYl1cfYybfB/GcdVl+BYzlD8HoY9zku2+ty7hXwhjzwepjzOT7
MJ6zLsuvgrH8QzD6GDf57lnrMu5SGGM+UH2MmXw/jOesy/KrYSy/fylu8n0Efsax/BoYyz8C
o4/Hm3w7tS7jXgtjzPuqjzGT76N4zrosvw7G8o/C6GPc5LtLrcu418MY847qY8zk+xiesy7L
b4CxfPlS3OT7MfgZx/L3wFj+cRh9PN7ky7Uu494IY8x7qo8xk+8n8Jx1Wf5eGMs/CaOPcZOP
13GmuDfhGWPeW32MmXz/Cc8Zx/L3wVj+KRh9jJt8ttZl3JthjJmOx5jJ99N4zrosfz+M5XfX
uoybfD+D54xj+S0wli9bipt8Pws/41h+K4zldy3FTb6fg59xLL8NxvI7l+Im38/DzziWfwDG
8tuX4ibfL8DPOJbfDmP5l2H08X1Mvo9XH8vvgLH8CdgUN/l4nY4+xr0T9gkYr+fRx5jJ94t0
wffo6mP5l+iqPsbSN/UxH4nnrMuYZ9Xjsc3vgrG9P1B9fN3J9yt4zuOxfBmM5bcuxU2+X4Wf
cSy/G8byr8Ho4/Em3/Q+LoPvchhj3lKPx5jJ9+t4zrosvwfG8puW4ibfb8DPOJbfC2P5P8Po
4/EmH6+RTnHvwzPGfG/1MWby/SaeM47l98NY/i0YfYybfLwWO8X9IJ4x5o3Vx5jJ90k8ZxzL
H4Cx/IaluMn32/AzjuUPwlj+HRh9PN7k4/XgKe5DeMaY11cfYybff8FzxrH8YRjLvwujj3GT
7/Ral3E/BGPM66qPMZPv9/CcdVn+YRjLvw+jj3GT79a1LuM+AmPMdDzGTL4/wHPWZflHYCz/
IYw+xk2+W9bjMe6jMMa8tvoYM/n+CM9Zl+UfhbH8xzD6GDf5vrHWZdzHYIx5TfUxZvL9CZ6z
Lss/BmP50qW4yfen8DOO5R+Hsfz/wOjj8SbfabUu434CxphXVR9jJt9/xXPWZfknYSz/Nxh9
jJt8nNswxf0nPGPMK6uPMZPvz/CccSz/FIzl/xdGH+Mm381qXcb9NIwx0/EYM/n+O56zLss/
A2P5/4PRx7jJx/kYU9zP4hljXlF9jJl8n8Jzxt0SP+n7FOy7axx9jKXvf8IYdwJ+0v8/YMs+
xrHMOSOMuzV+PhP257C/gE2+i2r5f1XfbfBIH8t/ueR7Ri3/7+o7HY/0sfzpJd/Ta/kz1Xdb
PNLH8l8t+Z5ay/+n+r4Zj/Sx/NdLvqfU8t9U3+3wSB/Lf7vke1It/1313R6P9LH82SXfebX8
99V3BzzSx/L/XfKdW8v/UH0dHulj+XNLvsfV8j9W3x3xSB/L/7TkO6eW/7n6DB7pY/lflnyP
qeV/rT6LR/pY/rcl33fU8r9Xn8MjfSx/fsn3qFr+j+rzeKSP5S8s+R5Ry1dUX49H+kq5aoi+
b+fvUZ6unYTqY3ka56LvoTCWj691h+pj+YQl34PhZ/nE6oso08fytZd8Z8HH8nStI6FMH8sn
1Tj6HghjebqukauP5Wkck75vg7E8XcO4U/WxfH0Y/z7o+1YYy9P1im+pPpZvWOPouy+M5ena
xJ2rj+VTahx994axPF1zuEv1sTyNU9N3TxjL0/WFu1YfyzeFsX303QPG8nQt4W7Vx/I0Lk/f
Dozl5bH/n4OP54dzYDwezxmT72uqj+Wfh7H8uKW4yTed13iuo49lzgnj8Vj+BRjL51Yf4ybf
dI7leZc+lm9e41j+OIzl86qPcZNvOt+TAfSx/A01juVPwFh+UvUxbvJN7PnR6mP5FjWOMb8I
Y/kp1ce4yTfx8keqj+VvqnGM+SUYy0+tPsZNvondP1x9LN+qxjHml2EsP736GDf5bl19H64+
lm9TfYz5FRjLz1iKm3ynV98HaxzLt60+xvwqjOWLluIm39S/en+NY/l2NY4xvwZj+ZnVx7jJ
N/UJ31t9LN+hxjHm12EsP6f6GDf5uup7d/WxfMfqe2f1sTz12+ljLH1Tn/r7UP4NGPOvKYf4
3iXfAD91+o7qY4yvvu+Ej36Wp3yBPh6PvlTjeLz/DGPOOB3ve5Z8d6pxrMc4xsTqOxtl+lme
jkcf4+i7c43j8X4Txjx3Ot7rlnx3rXGsxzjGfEv1PRZl+lmejkcf4+g7VON4vN+C3QXl6Xiv
WfLdvcaxHuMYc7fqezzK9LM8HY8+xtF3Ro3j8T4J20F5Ot6rlnz3qnGsxzjG3KP6noAy/SxP
x6OPcfTdp8bxeL8NuyfK0/FeseS7X41jPcYx5t7V90SU6Wd5Oh59jKPv/jWOx/sd2H1Rno73
siXfA2oc6zGOMd9afU9GmX6Wp+PRxzj6zqxxPN5/gX0bytPxXrLke1CNYz3GMeaB1Xc+yvSz
PB2PPsbR95Aax+P9LuwslKfjvWjJ97Aax3qMY8yDq+9pKNPP8nQ8+hhH38Nr3ItQ/j3YQ1Ge
jveCJd8jaxzrMY4x3159F6BMP8vT8ehjHH2PrnE83u/DHoHydLznL/m+s8axHuMY86jquxBl
+lmejkcf4+g7u8bxeH8A+w6Up+M9d8n3XTWO9RjHmMdU38Uo08/ydDz6GEff82vc3VEmb8nj
x1bfGdXH8uOWfGQry4+vvnuhTB/L5y75fgE+lp9QffdBmT6Wz1vykZksP7H67ocyfSxPDKXv
EzCWn1zj7l99LD9lyfeL8LN8fvU9AGX6WJ7YSB+5x/LTatyZ1cfy05d8ZBzLF1Tfg1Cmj+WJ
efT9CozlC2vcQ6qP5YuWfGQXyxdX38NQpo/liWX0/RqM5WfXuEeiTEY9C+XnVt/DaxxjnrPk
YxzLU9yzUeZ3/jz4Jr08a8k36eAn4PtZ2Hcj7hX1eLdEmX76XlB9LP8hjOVXLcVNvhdW361q
HMuXVN/zqo/lF1Uf6/0RjOXvX4qbfC+uvu+qcSy/pPq+u/pYfmn1vbD6WH5Z9b28+lj+4FIc
/fS9fMn3UvhY/lD18f3+NIyfySur78dQZrv5/i+tvo9VH8uvXvL9Mfwsv6b6WG/yvbn6Plp9
jHlt9X2k+lj+nur7EHz0vw7l11ffB6qP5TdU3w9WH8tTXfr4uiy/sca9r/pY/t7qe0/1sfym
6ru8+lj+viXfn8DP8luqj8effNN74/ulj+Xp++V3Sx/LP1jrXlZ9PNZbq+9d1cfy26rvtfDR
z/IPLPl4PPret+T7AfgY8/Yl39vgY/kd1fd61oOx/M4l31vhY/ldS763wMfyZUu+74eP5Xcv
+d4MH8uXV98bUKaP5fdU3xurj+X3Vt+r4eP74Ht4f/VdWn0sT58VffwMWf5AjXtl9bG8rPEX
w08tf7jGHXfCZxZnnvD7Z132G8dddtLvX/7511/xz1fwf+yg/gVumY7///2Kd11++qVX+f9z
X7ji78sO6vj5wv/4+OWoMf7Dk5v/6lk3+/WzbnbvZ/D/X+X/N/311/356eNm7R/5wKUfOv3S
D+Fn+f/yD1z6jfc866b8/2WPPf3FJ9z39Ned9tAX33Rx6i3vd+pnTnrQ9W+KFk//zr/8vYd+
6bduscMy3+H478qd0CfPkR/3L+7mR37Bo3ivDf+4A/sYsH/tOkoDqnt83VNQOumSZ/2mLYpg
LvKPf3iTu37wHbe+K5+fuDj5kuMZfwXXx3z2nx7w809++8+wg7D4u1ecf+fl55fd7Y/udLgf
8XeZYvj8sW97wF0Yw+NMz1keXwMvgbU1y6+Blvz8D/3DN7BTsfiHc3/05554r53y/O9e8dc/
+7G3PWB6/i3Tc8TceYpB3btMdZfbwWNd+Z5OLMf99DvfeOfpNT73139Xnr863+Xnlp+//953
KG1nO6bnX3qsa7G4mI7F50eOu84Cx77zFMfn0+uw/UfzL8dMx2Xd6Tlfb/p38vSkPJ5SgIu/
5y/xnrRUetk/vu0QbcmFL9+y47f4yX/4jzt/6O/Hu5cdXn7iceThJXcb7ezyd1llxNBd/BtX
bl0ZyGMtDuF/2CWwy2CfgH0KtsDxT4GdBjOwQ7AzYXzdC2CXwF4JewPsLbDLYB+AfRT2U7BP
wH4D9ruwP4V9CvZp2Gdh/wLjpNMTYCfBrg87BXZT2FfDbgY7DXZL2Omw28MMrIcl2J1hh2Bn
wO4Duz/sTNhDYA+HPRp2NuzxsCfCzoddALsY9hzY82GXwF4Meyns5bBXwi6FvQb2OtgbYG+E
vQn2ZthbYG+DvR32TthlsMth74W9H/YB2IdgPwT7COyjsI/Bfhz2k7Cfgv0M7OdgvwD7BOyX
YL8C+zXYb8B+E/ZJ2O/Afhf2+7A/hP0x7E9h/xX2Z7D/DvsU7H/C/gL2l7BPw/4K9tewv4V9
FvZ/YZ+D/RPsX2D/Bvs87AswDiQeB7sW7HjYCbATYdeGXQd2Euy6sJNh14NdH3YD2A1hN4Kd
AjsVdmPYTWA3hX0F7CthXwX7atjXwL4W9nWwm8FuDvt62DfAToPdAvaNsG+C3RJ2K9itYbeB
nQ67LeybYbeD3R52B1gHuyPMwCzMwTyshwXYAIuwBMuwO8G+BXZn2F1gd4VxkvIh2A7s7rB7
wM6A3RN2L9i9YfeB3Rd2P9i3wu4P+zbYA2APhJ0JOwv2INiDYQ+BPRT2MNi3wx4OewTskbBH
wR4N+w7Yd8IeAzsbdg7ssbDHwR4POxf2BNh5sCfCngR7MuwpsPNhT4U9DfZ02AWwZ8AuhF0E
uxj2TNizYM+GPQf2XNjzYN8Fez7su2EvgL0Qdsk9FpfAFi/CI2zxYjzCFi/BI2zxUjzCFi/D
I2zxcjzCFq/AI2zxSjzCFq/CI2xxKR5hi1fjEbZ4DR5hi9fiEbZ4HR5hi9fjEbZ4Ax5hi+/B
I2zxRjzCFt+LR9jiTXiELb4Pj7DFm/EIW3w/HmGLt+ARtngrHmGLt+ERtvgBPMIWb8cjbPEO
PMIW78QjbPEuPMIWl+ERtng3HmGLy/EIW7wHj7DFe/EIW7wPj7DF+/EIW/wgHmGLD+ARtvgg
HmGLD+ERtvgwHmGLH8IjbPHDeIQtPoJH2OJH8AhbfBSPsMWP4hG2+BgeYYsfwyOs/NP5Wefn
a0ELx8NOgJ0IuzbsOrCTYNeFnQy7Huz6sBvAbgi7EewU2KmwG8NuArsp7CtgXwn7KthXw74G
9rWwr4PdDHZz2NfDvgF2GuwWsG+EfRPslrBbwW4Nuw3sdNhtYd8Mux3s9rA7wDrYHWEGZmEO
5mE97Iyd913njJ03f/0ZO392xhk7L3/eGTsf+vgZO4+96T13fvc599y52d/cc+eiZ9xr5/rX
vvfOLT58751/Ovs+O398m/vu3Hhxv50T/+p+O6f+5bfuvPtz99+53Vc+YOcO3/rAnTu+6cyd
X/37s3Ze//gH76S/ecjOc17zsJ2vusfDd/7q1Efu/Mm/Pmrnj//9O9DPOPtL7E4PefROfsvD
dt4ynLXzl7e5/84l59575zmfufvO8z9y151f/pE77Xz+08POoYf5nZM+d8edm3/89jtv+vHb
7vzK79165643veXObzz3FjsPX3zDzo3ef7Od/klfu2Pv89U7r9/5yp1/evBNd279ghvv/Msv
nLLzqK+40c5Zl9xg57NfuN7Oo99w8s4n/XV3XvLp6+z8wQ9fe+erX3Lizs+ed8KOfdTxO597
9LV2Xnv+cTuXvmqxc/x5Vxy61R/+x6FffcTnD935n//t0N9++F8Pfduz/+XQeA7Qz7Y/AWla
mm5bofNbJ01L0/NV03YNaVqabluh81snTUvT81XTdg1pWppuW6HzWydNS9PzVdN2DWlamm5b
ofNbJ01L0/NV03YNaVqabluh81snTUvT81XTdg1pWppuW6HzWydNS9PzVdN2DWlamm5bofNb
J01L0/NV03YNaVqabluh81snTUvT81XTdg1pWppuW6HzWydNS9PzVdN2DWlamm5bofNbJ01L
0/NV03YNaVqabluh81snTUvT81XTdg1pWppuW6HzWydNS9PzVdN2DWlamm5bofNbJ01L0/NV
03YNaVqabluh81snTUvT81XTdg1pWppuW6HzWydNS9PzVdN2DWlamm5bofNbJ01L0/NV03YN
aVqabluh81snTUvT81XTdg1pWppuW6HzWydNS9PzVdN2DWlamm5bofNbJ01L0/NV03YNaVqa
bluh81snTUvT81XTdg1pWppuW6HzWydNS9PzVdN2DWlamm5bofNbJ01L0/NV03YNaVqabluh
81snTUvT81XTdg1pWppuW6HzWydNS9PzVdN2DWlamm5bofNbJ01L0/NV03YNaVqabluh81sn
TUvT81XTdg1pWppuW6HzWydNS9PzVdN2DWlamm5bofNbJ01L0/NV03YNaVqabluh81snTUvT
81XTdg1pWppuW6HzWydNS9PzVdN2DWlamm5bofNbJ01L0/NV03YNaVqabluh81snTUvT81XT
dg1pWppuW6HzWydNS9PzVdN2DWlamm5bofNbJ01L0/NV03YNaVqabluh81snTUvT81XTdg1p
WppuW6HzWydNS9PzVdN2DWlamm5bofNbJ01L0/NV03YNaVqabluh81snTUvT81XTdg1pWppu
W6HzWydNS9PzVdN2DWlamm5bofNbJ01L0/NV03YNaVqabluh81snTUvT81XTdg1pWppuW6Hz
WydNS9PzVdN2DWlamm5bofNbJ01L0/NV03YNaVqabluh81snTUvT81XTdg1pWppuW6HzWydN
S9PzVdN2DWlamm5bofNbJ01L0/NV03YNaVqabluh81snTUvT81XTdg1pWppuW6HzWydNS9Pz
VdN2DWlamm5bofNbJ01L0/NV03YNaVqabluh81snTUvT81XTdg1pWppuW6HzWydNS9PzVdN2
DWlamm5bofNbJ01L0/NV03YNaVqabluh81snTUvT81XTdg1pWppuW6HzWydNS9PzVdN2DWla
mm5bofNbJ01L0/NV03YNaVqabluh81snTUvT81XTdg1pWppuW6HzWydNS9PzVdN2DWlamm5b
ofNbJ01L0/NV03YNaVqabluh81snTUvT81XTdg1pWppuW6HzWydNS9PzVdN2DWlamm5bofNb
J01L0/NV03YNaVqabluh81snTUvT81XTdg1pWppuW6HzWydNS9PzVdN2DWlamm5bofNbJ01L
0/NV03YNaVqabluh81snTUvT81XTdg1pWppuW6HzWydNS9PzVdN2DWlamm5bofNbJ01L0/NV
03YNaVqabluh81snTUvT81XTdg1pWppuW6HzWydNS9PzVdN2DWlamm5bofNbJ01L0/NV03YN
aVqabluh81snTUvT81XTdg1pWppuW6HzWydNS9PzVdN2DWlamm5bofNbJ01L0/NV03YNaVqa
bluh81snTUvT81XTdg1pWppuW6HzWydNS9PzVdN2DWlamm5bofNbJ01L0/NV03YNaVqabluh
81snTUvT81XTdg1pWppuW6HzWydNS9PzVdN2DWlamm5bofNbJ01L0/NV03YNaVqabluh81sn
TUvT81XTdg1pWppuW6HzWydNS9PzVdN2DWlamm5bofNbJ01L0/NV03YNaVqabluh81snTUvT
81XTdg1pWppuW6HzWydNS9PzVdN2DWlamm5bofNbJ01L0/NV03YNaVqabluh81snTUvT81XT
dg1pWppuW6HzWydNS9PzVdN2DWlamm5bofNbJ01L0/NV03YNaVqabluh81snTUvT81XTdg1p
WppuW6HzWydNS9PzVdN2DWlamm5bofNbJ01L0/NV03YNaVqabluh81snTUvT81XTdg1pWppu
W6HzWydNS9PzVdN2DWlamm5bofNbJ01L0/NV03YNaVqabluh81snTUvT81XTdg1pWppuW6Hz
WydNS9PzVdN2DWlamm5bofNbJ01L0/NV03YNaVqabluh81snTUvT81XTdg1pWppuW6HzWydN
S9PzVdN2DWlamm5bofNbJ01L0/NV03YNaVqabluh81snTUvT81XTdg1pWppuW6HzWydNS9Pz
VdN2DWlamm5bofNbJ01L0/NV03YNaVqabluh81snTUvT81XTdg1pWppuW6HzWydNS9PzVdN2
DWlamm5bofNbJ01L0/NV03YNaVqabluh81snTUvT81XTdg1pWppuW6HzWydNS9PzVdN2DWla
mm5bofNbJ01L0/NV03YNaVqabluh81snTUvT81XTdg1pWppuW6HzWydNS9PzVdN2DWlamm5b
ofNbJ01L0/NV03YNaVqabluh81snTUvT81XTdg1pWppuW6HzWydNS9PzVdN2DWlamm5bofNb
J01L0/NV03YNaVqabluh81snTUvT81XTdg1pWppuW6HzWydNS9PzVdN2DWlamm5bofNbJ01L
0/NV03YNaVqabluh81snTUvT81XTdg1pWppuW6HzWydNS9PzVdN2DWlamm5bofNbJ01L0/NV
03YNaVqabluh81snTUvT81XTdg1pWppuW6HzWydNS9PzVdN2DWlamm5bofNbJ01L0/NV03YN
aVqabluh81snTUvT81XTdg1pWppuW6HzWydNS9PzVdN2DWlamm5bofNbJ01L0/NV03YNaVqa
bluh81snTUvT81XTdg1pWppuW6HzWydNS9PzVdN2DWlamm5bofNbJ01L0/NV03YNaVqabluh
81snTUvT81XTdg1pWppuW6HzWydNS9PzVdN2DWlamm5bofNbJ01L0/NV03YNaVqabluh81sn
TUvT81XTdg1pWppuW6HzWydNS9PzVdN2DWlamm5bofNbJ01L0/NV03YNaVqabluh81snTUvT
81XTdg1pWppuW6HzWydNS9PzVdN2DWlamm5bofNbJ01L0/NV03YNaVqabluh81snTUvT81XT
dg1pWppuW6HzWydNS9PzVdN2DWlamm5bofNbJ01L0/NV03YNaVqabluh81snTUvT81XTdg1p
WppuW6HzWydNS9PzVdN2DWlamm5bofNbJ01L0/NV03YNaVqabluh81snTUvT81XTdg1pWppu
W6HzWydNS9PzVdN2DWlamm5bofNbJ01L0/NV03YNaVqabluh81snTUvT81XTdg1pWppuW6Hz
WydNS9PzVdN2DWlamm5bofNbJ01L0/NV03YNaVqabluh81snTUvT81XTdg1pWppuW6HzWydN
S9PzVdN2DWlamm5bofNbJ01L0/NV03YNaVqabluh81snTUvT81XTdg1pWppuW6HzWydNS9Pz
VdN2DWlamm5bofNbJ01L0/NV03YNaVqabluh81snTUvT81XTdg1pWppuW6HzWydNS9PzVdN2
DWlamm5bofNbJ01L0/NV03YNaVqabluh81snTUvT81XTdg1pWppuW6HzWydNS9PzVdN2DWla
mm5bofNbJ01L0/NV03YNaVqabluh81snTUvT81XTdg1pWppuW6HzWydNS9PzVdN2DWlamm5b
ofNbJ01L0/NV03YNaVqabluh81snTUvT81XTdg1pWppuW6HzWydNS9PzVdN2DWlamm5bofNb
J01L0/NV03YNaVqabluh81snTUvT81XTdg1pWppuW6HzWydNS9PzVdN2DWlamm5bofNbJ01L
0/NV03YNaVqabluh81snTUvT81XTdg1pWppuW6HzWydNS9PzVdN2DWlamm5bofNbJ01L0/NV
03YNaVqabluh81snTUvT81XTdg1pWppuW6HzWydNS9PzVdN2DWlamm5bofNbJ01L0/NV03YN
aVqabluh81snTUvT81XTdg1pWppuW6F7ad0VV1z+qesuHnzxuU962rnn3+Bkf9oNTjYwP/Cn
paXp2d3Pffa55z3zaedd9NRzz3/8uReeds8Ln3DORRfBgagz73HamQ964Gn3fdBpZz105yEP
wdP7nAG3Mcb3GU8ecuEzzz3tggvPvejcpz3u3MdcfO5FF8N5xjkXP/OpeLSmvMRRfvJ3y1Ya
xVrVP5V3zj//vHMfe+E5z3zcEy867/zPP/H8c556wbk3ODlaVn4OjT9MFwMfrlp/Op7jr0tk
Zsv5lL+im59OD+MRBliEJRjjysvY0hiGWsZaBltGW4ZbxltWsKzheGhXjs0ajjUcazjWcKzh
WMOxhmMNzxqeNXxpDmt41vCs4VnDs4ZnDc8aPWv0rNGzRl/eAWv0rNGzRs8aPWuUbyqwRmCN
wBqBNQJrBNYIrBFYI7BG4GsUqQysMbDGwBoDawysMbDGwBoDawysEfkakTUia0TWiKxRvpvI
GpE1ImtE1igiTKyRWCOxRmKNxNdIrJFYI7FGYo3M18iskVkjs0ZmjcwamTUya2TWKN/0JEPW
sYaVrGEta1jNGtazhhWtYU1rWNUavpqtX3+pa0vdUQGjBEYNjCIYVTDKoOjAFiHYogTrSt2i
BVvEYIsabJGDLXqwRRC2KMIWSdiiCVtEYX1pc5GFLbqwRRi2KMMWadiiDVvEYYs6bJGHLfqw
fXm/RSG2SMQWjdgiEltUYotMbNGJLUKxRSm2SMUWrdgiFlvUYotcbNGLHc8tRTG2SMYWzdgi
GltUY4tsbNGNLcKxRTm2SMcW7dgiHlvUY4t8bNGPLQKyRUG2SMgWDdUzWVGRLTKyRUe2CMkW
JdkiJVu0ZIuYbFGTLXKyRU+2CMoWRdkiKVs0ZYuobFGVLbKyRVeunNicoTZc0ZUrunJFV67o
yhVduaIrV3Tliq5c0ZUr5xVXdOWKrlzRlSu6ckVXrujKFV258fwynmDqGYa6cuM5ZjzJjGeZ
8TQznmfGE03RlSu6ckVXrujKFV25oitXdOWKrlzRlSu6ckVXrujKFV25oitXdOWKrlzRlSu6
ckVXrujKFV25oitXdOWKrlzRlSu6ckVXrujKFV25oitXdOWKrlzRlSu6ckVXrujKFV25oitX
dOWKrlzRlSu6ckVXrujKFV25oitXdOWKrlzRlSu6ckVXrpycXNGVK7pyRVeu6MoVXbmiK1d0
5YquXNGVK7pyRVeu6MoVXbmiK1d05YquXNGVK7pyRVe+6MoXXfmiK1905YuufNGVL7ryRVe+
6MoXXfmiK1905YuufNGVL7ryRVe+6MoXXfmiK1905YuufNGVL+crX3Tli6580ZUvuvJFV77o
yo8EGxE2MqxCjOcrP2Js5NgIspFkI8qKrnzRlS+68kVXvujKF135oitfdOWLrnzR1dj/8EVX
vujKF135oitfdOWLrnzRlS+68kVXvuiKICl/u2wnjGfHQjY8FubgsTCgBBYClJN4OQ+XU2kh
RwFH4UbBBmuoB4BPkJ+VegD4ENQD2PcegOtqbwqPQP1gQH0/dg74q9gPQ0b3YRh7eXANQ7IW
cOvj2B2CK+aMnlZAP2jsJ8GVh5hxNs55qoeTZh+HHpQLY9fMdThv5Rz8gL7F2GOEKxqfYhw8
zkXjaaPrDXgUYzZ57Hq6rvcpx4Cqgxn7oXDFjFYEtMKM3UvXBcA4OvDF5LHnBBfKgCd6GWPP
yXUD6IpuVGAzyskJroT+BE7lxoxMt66Lvce7NgnvaOz8uS6ZHEF11B3GvhVcyfTorOLYtZvk
uhwCPk2cjXH4cp7zncH7jTGixzoiy/oOKg9gdES/p/ZLO3RsTDAhx1Tfou9ArIy+J7oetb/p
8dFkULG3aMXYDfNdQMcRH4SJwGg5x3q8x+yjj9HgjZXP1OMNpT4PqGjGPhUakaLPCdwzuR+7
8mOPl3+EVz5DzWjCABjiFcdvFq1A+/GFpZzHDggOZmJIoH/ElzH2P/EZ4s30+ICirZ1vfGkD
vh4DDoU89tBdZxMkgU+tR1+jvKztoD581wZvvx+zC9sNEBeSD8jNjF+thSbwoeNdB3w65U3a
Dp3GEPDGgf2xO2u6nKPBhz/EMH4SSH0hDnxHhgIa85gOUg9piOgn166s6Xp0npB7QPRpzAoM
/jTw8ujx4uMeu/Omw7eB7mHKdhizpNzhg8dr46seIOqSguEF0XC0NYPI5S3mbghmSD36Byal
AveMrzEO6Bbis0E0P4jcebxlfPYxAsSlK5fxh2d6fGlUOXRdopBnxJzw5xn6UP6ocgfNQjX4
LvCb8tmkLuPzRa7jPT6b0glMHRqQ0KmjnEPpwSSohF8ZIvkW+eEkfPIGfVbjIz7a0itL+KPC
H35AS/Btli5R6vDJoG+JgyWkK3zbcOHPH18Fuhv4++BfWsKfP5oI4ece38Z4eDQA5xH8LUCD
pUuS8C1mnA6KUCHgUhGiwjEyvjETqwt/mwZnrj4knJr4SST8oaHfknCawp9L6TTGDu1Bjwx/
UpB96WvCxT8nfNkZ55jSTY74O8bpAF8EhDieOeDC+8FJLkIGUAUOD5fBl10+q4z44sLpDX8b
6C/iiyxdRPZ+ZO1+Bji1C36Cn+An+K0CfiXzFfwEv7WAvuCnzA/JneAn+K0n/JiHIc27hsyP
ieWeMj9mkcr8NjSDFfwEP8FPw54a9tSw51pka6scRhb8BD/BT/BbEfzWZ9hzvEynS34bmtTt
hpFin9gn9ol9W8c+zXdpdx7KbsC1ihjBT/AT/AQ/we/Io5665LfBmaHgJ/gJflsNv3GRwWpW
Ohz8qOfu5ruMDNNKB2V7yxmj4Cf4CX5bDb9xVdxq4FduKdPgSoc9T/YcK2qZ30bOhRH8BD/B
T/Bb0bCn4Kc17uuTXQp+gp/gJ/gJfke+5qfMT9f8dHcz3d2sMFJ3Nyu36dTdzdbr7mYa9ly+
1qXnY3aqzE+ZnzI/ZX5rm/nt84QXzfZU5qfMT5mfMj/d11r3tdZ9rdfnmt41ZbjK/JT5KfNT
5re2md+4z8M13dpTSx2uCQTb+HvBT/AT/AS/DYefrvltI9yu6T0LfoKf4Cf4CX6a7bmRa/mu
DoCCn+An+Al+K4Lfwd/hRcOem3MN7upAtR+/E/wEP8Fvq+HHIUFt5K6N3LcPooKf4Cf4bTX8
9nx7s75QM8Rg+xBNPzhnD/4OL/u81OEIi9yZa2J7W+Ocj0NwLqcwbo8Uhz4MusPL+kBU8BP8
BD/Bb0XDnoKf4Cf45SFmb0zOhn0nINbb2KNr5PohePbW6OptzsEPNkXDvhNd0fgUI/pPX4zq
jcOQRMwmGz8G9T7lGFB1MIa9T9TrY3YxB+udsdUVnB+iczz2UNsQUHYBMf1QX29wQfDDJ+i7
FH1O3jqTe8MrN+PHWD7LK3/4Tnd40R1eeuNjWq87vKxyqYMyv/24/nYsjglwOCqjPNqERaw2
BR8rG1yI/TBkG7XIXYvcCyMFP8GvKfgd/LAnX1HDnscCVqt+TcFPmZ8yPw17rmjYU7M9Neyp
YU8NezKZziEgj/Z9j8HdMpboO4Nh3hijdcnlkl/7zjobHLzOIIxZuO8cxh+DCTmmOrLrO29i
tphV4J3ta8XeZJf73toh5zKU7LtgB+TtwUSXTcnofTe47KNHypacrVGxT30eUNFgmHN8RQ17
uvLZm24wQ0hDtLiRVS4jvqbr3YBvBMPt+NyU+TWV+fHrSJ3u8LLqrGgbjqfMT5mfMj9lfivK
/A5+wsvu4Md+TeyWd3Jnnw8ediXR0cla6bA+CduquCz2iX1in9i3dexLgt/W3dDlcGgKfoKf
4Cf4CX66u9nWwVDwE/wEP8FP8BP8BD+tdMC0EI8rAcY4X9eAxN4PWulQGKmVDprvcjXzXTTZ
U5M91+faoTI/ZX7K/JT5rSjzO3j4HfwyP/Z+tMzv8Otn61gW/AQ/wU/wWxH81meypya8rE+G
tl9gFfwEP8FP8Ntw+K3y7ma6wct+weigjyv4CX6Cn+An+GnCiya8aMKLJryUe9FceTfrK5/p
vta6wYvrr2bCi4Y9NeFlfYZTlfkp81Pmp8xvRZnfwU942esNXnTNb30gtV/DoYKf4Cf4CX4r
gt/BZ367m+151bub7R1+mu25XzA66OMKfoKf4Cf4rS38dpf5rXLCi+B30JDar9cT/AQ/wU/w
E/w04UUTXjThRRNeNOFFOxphm6DY59gbF62PIXLgMHXY03otJ7ysMvPTUof9ysQO+rjK/JT5
KfNT5reizE8TXjTbc30m0gh+gp/gJ/itCH4HP+Fld9f8VjnhRZnfQWdo+/V6gp/gJ/gJfhsO
v1UOe2rCy37B6KCPK/gJfoKf4Cf4acKLJrxowosmvGjCiya8bNaEl1UOeyrzO+gMbb9eT5mf
Mj9lfsr8lPkp81Pmp8xPmZ8yP2V+e8v8NNtTsz012zMPMXtjcjYccUB+6W3s49C7fgie86Xo
6m3OwQ82RZOrKxqfYhy8/2IUVhoNOcZssvFjUO9TjgFVB2PKTZdd18fsYg7WO2OrKzg/ROd4
7KG2IaDsAmL6ob7e4IIyP2V+yvyU+SnzU+anzE+ZnzI/ZX57y/xaXeqg2Z77dd1snY+ra37K
/JT5KfPb8MxvlRNetM5vnYG33HbBT/AT/AS/DYffKjM/wW8ZIOv8XPAT/AQ/wW9F8NOEF014
0YQXTXjhlJ4cQgre9z2m9ZQLab4zmOATY7QuuVxm3fjOOhscvM4gjHN6fOcsCibkmOqcHt95
E7PtB+ed7WvF3mSX+97aIecyich3wQ4eM39MdNmwu4tjDS776GM0uJhZo2Kf+jygonHjVCPf
pehz8njZ3Btd89M1v71d82sVfqvM/LTOb52zveW2K/NT5qfMT5nfijK/Vie8rPKan+C3DJB1
fi74CX6Cn+C3tvDjWEbqTMoG89T7kKzzTPPgwnKpmFIfMVCSBb91htR+tV3wE/wEP8FvRfBr
ddhzlfDThJf9gtFBH1fwE/wEP8FvRfDbhmFPwe+gIbVfryf4CX6Cn+C34fBb5YQXwW+/YHTQ
xxX8BD/BT/AT/HR7M93eTLc30+3NtNRBSx32ttRBw55a56d1flrnp3V+NuIu47GsNnQd7kQe
e9PbaO24mBF3Ix9w33HjuZ7R13uW24R7nWN1ZO+iLzcot122vIm5wTLH3vDcam034K7p1oQe
SxLHe5bbrvc2JaxuDFgFyXEpRDmTQsACR29CKscyXc7RYJHlEMO44tF0EXc9x1pMwzujlzWW
phsMPEO0EW2p9Xo3YOUlbqiO9ZGc6W5N5/jyNnssqwyls2A6rLp0aEa2gy33YM8dFljitbGk
c8Dd2rk4M+MF0XC0Nft+fIu5G4IZUu/dYFLyfIsZyzXj4LA6NBhEsxG583jLJgwxerSOjcid
i6bH4kzevh03bC8ui7eck/Mp9KEs4cwdbuOO1aH4LvCb8tmkLuPztT3mQ+KzGcbJkWhAcvik
hzgEx8OnLvb8yhDJt8gPJ+GTN65HxYiPNvM7S13Ah9kHtATfpm0Vfhr2POghxXV4PQ17athT
w56Cn4Y9NeypYU8Ne2rYU8Oeyvz2lvlpqYOGPTXsqWFPDXtq2FPDnhigLoOjGO/uMQLtMUQ6
1PFS3vXP4L5+uccg9DiqinFXj5HrAUOyMYxjr7jfHrb3LPfhw/35yrEwlo5jZAxUm1hd8xe5
s1kR49IYJscQd8aWoUOdxplCDhh+xvD7uBFoRFbs8D5yxOA3xsJLxWQwxF1GiDPiiwu7lQZs
RIrjmWTZC1iHkb9tbqNGPTXqqVFPjXpu+Kin1rhvM+SO9t4FP8FP8BP8tg5+Svy2PjEV+8Q+
sU/s23D2aa7n0ZKfbfYLfoKf4Cf4CX665Ld1maDgJ/gJfoLf2sKPs0+ueU8HZX7bnOEd7b0L
foKf4Cf4rQh+WuigyZ7rM8lV8BP8BD/BT/DTsKeGPbXEXUvctcRdS9w3a4n7Koc9udQQK/+0
zG/tYanMT5mfMj9lfivK/HRnTw17athT93fR/V10f5etu79Lq9f8Vpn56QYvR5tAsm5+ZX7K
/JT5KfPb8MxPN3hZNzAdRHsFP8FP8BP8BD9NeFn7a3hzgSn4CX6Cn+C34fDTsOdcMGxDvOAn
+Al+gp/gp8xPmZ+WOmipg5Y6aKnDZi112PM1vzFl1I5GGwlGZX7K/JT5KfNb28xvd7c32zP8
xoqCn+DH2ftuGJK1zqc+9uwW0YVtHi22oLR97vvq0lIHLXXQUoetW+rQ6jo/wW8bruHNfY/K
/JT5KfNT5re2md+4tfv8fdyT9vPbyGxuDgAFP8FP8BP8BD9NeNk6GAp+gp/gt9Xw45BgWhH8
Dv4OL7u75qelDnMyom2JFfwEP8Fvq+FHMKwv/HY37Lln+I0VNeFlI7NCwU/wE/wEv7XN/PYZ
fprtia7RpmaCgp/gJ/gJflsHP8132Vim7ZbVYp/YJ/aJfStiX6srHfY86qnET4nfMBjKgKjU
Mj9+DMnk6HqCc4j1k0nJ9Na5fsg28SSAqBxCCt73ffBDuWuK74wfbIzRuuQyO5/Wd9bZ4OB1
BmGjy1kUTMgxGVNWTvrOm5htPzjvsJxyjOpNdlhZadGKzOv+OFawg485mOiy4V88XIPDajMf
o8Gda2pU7FOfB1Q0ztRjpehz8njZ3Bvd4EU3eFmXG7zsbr7LyLCcsBq5x58UZL/LlQ665IeT
yG4zqXWLU+anzK8gUvBzpeNhOvTzguC3LvDTJb/NhdN+w1TwE/wEPw17athTy/w2NsM7GkQF
P8FP8BP8VgS/g1/mp8xPmd/R4HZNfsFP8BP8BL+1hZ+u+Ql+1wS5o/1e8BP8BD/Bb0Xw02xP
7zErzSTLHPhoJ1352/hsBD/BT/AT/FYEv/UZ9tQyv61ns9gn9ol9Yt/WsW+XKx3GJRK6udlG
glLwE/wEP8FP8NNkz40E3NWNMAt+gp/gJ/itCH4Hf8lP813auHx2dZBp9XeCn+An+Al+awu/
3a102PMNXjTsucHzdgQ/wU/wE/w2HH66tWer2dexbJfgJ/gJflsNPyY3q9rN7+CHPZX5adhz
rwAV/AQ/wW+r4cesSPAbNOFFE16MxTYEsdzpHzs4hNgP2KQgalOHIeE+8N707Cejx6BNHfK4
zYfvsJMFdpLwKWfIhZ8Odq6IITms8zW2j2VrCddF7FDRY9eLaO24c4XrsEOFS8Zz8wrvx4/V
JpsztsLoXfRlMwvbQX0hZ4M9LXpT9sqw3TBgfwsTeuw/MZTvw3a9x04a2MoiYMuLsnOF7XDj
/hCwm4U3IZVjmS7naLCjxhDDuL2F6WIecBdrwW9thz13N+Flz8OeY0UtddhIMCrzU+anzE/w
W1v47W7Yc8/w04QX9Er3OqzYej3BT/AT/AQ/wU/DnhsLuaNBWPAT/AQ/wW/D4TcmcHvYy1aZ
nzI/XfPTNb/CSOwHHwZvA7aO1zW/3mY/+Dhe6TSdyc7h0mO2gzW8hpm7jF/ielFyQ4rlOnrG
RUZcrMT1yez78bJm7oZghtR7h9shJ8/LmrkLuMzu+oDroYjmBcvceVzmxGcfo8dOuxzsy52L
ps/JR1w6dY4je7mzuMyZk/Mp9MHwyn3ucJ16cB7XX/Gbcj00dRnXVG1vvMf10IEVN33Ci4Y9
j5b9bLNfmZ8yP2V+yvzWNvPb5wkvyvzQNdpUQAp+gp/gJ/itCH6tbuqgYc9NBdiX874EP8FP
8BP8VgS/g1/kfvCZH4ecI9Y6YYw7DsG5nMK4PVIcelwS0HZ+a5MpCn6Cn+An+Al+u57tKfh9
OdlWS3UFP8FP8BP81hZ+B7/OT/BrCWBfTlsEP8FvK+FXpkJa3eJl7ad7Hvy4J19R455fDnVa
qSv6iX5bST+ewgS/Va91aHXGi9Y6tAKcltoh+Al+gp/GPTXuueuLfsr8WgLYl9MWwU/wE/wE
vw2Hn9Y6fDmQ2NS6gp/gJ/gJfmsLP13z29xV6PsNXcFP8BP8BL+1hd/upnsq89tvkKzj8QU/
wU/wE/xWBL+Dn/Cyu8xP8FtHOO13mwU/wU/wE/xWBL+Dv8WLMj8Ne+4VkoKf4Cf4bTX8mBWt
aluHg8/89gq/8ZZk2TvbD9HmYdeTPbXIfa+saa2e2Cf2iX1bzb5t2NJoz6Oe4/pAbEs1xJyj
G1xMWunQGsT22h7BT/AT/AS/DR/11Br3vQJik+sJfoKf4Cf4rQh+rY56XhV+ex71VOK3KTwU
+8Q+sU/s2zr2JcFvbXYe2i/YCn6Cn+An+G04/PZ8yW+sqEt+GwlKwU/wE/wEvxXBbxsWOmiy
535lYgd9XMFP8BP8BL8Nh99VL/ntfdhT8DtoSO3X6wl+gp/gJ/itCH7rM99F8NPSeMFP8BP8
BL8Vwa/VYc9VZn6a7blfmdhBH1fwE/wEP8FP8Nv1DV4Ev4OG1H69nuAn+Al+gt/awo8oSp1J
2Rib+pCs80zz4PI+xJT6aPucNdtzvwCyzscV/AQ/wU/wW1v47e7Onqsc9tSEl3UG3nLbBT/B
T/AT/AQ/DXtu5Fq+Zdgd/lzwE/wEP8Fvw+G3ymFPZX6HQ2Rdy4Kf4Cf4CX4bDr9VDntqwsu6
wu7wdgt+gp/gt9XwY1a0fbv57X2dn+B3OETWtSz4CX6C31bDb5wcmXqfXAx5iENw4yyS2OfY
GxetjyGOiBwG4/re+JhCyL5QM8Rg+xBNPzhnD36Ru2Z7arH6XuEr+Al+gt9Ww2+Vmd/6LHLf
86YOuuS3V9a0Vk/sE/vEvq1m3yoTv1bZt8r5Lhr1bA1ie22P4Cf4CX6C39bNd1Hit3ULGw5n
pNgn9ol9Yt/WsU/TXXSlUPAT/AQ/wW9F8Dv46S7jzJxrurmZFjocnvWojNOe6xyVUR5twlwu
m4KPHBMortgPQ7YRfo6a0zUMyeL2ebhlXj9VjDlb7zDlK/d9jcKcseyNyXmq523s49C7fgie
g+Y4lO9tzsEPNkVTX9BH41OMA+7KN0VhttmQY8wmG04uQz3MSsuYlZbDYEx9vT5mF3NAK4yt
ruD8EJ3jsYfa9oCyC4jph/p6gwuCHz5U36Xoc/LWmdwbnsLGj7F8llf+8F2MJgzehmH6Zn3X
W2fxhaWcXSg1fWdiSC7ZiC8jVpHgC8PEwd5Ga339Ojg7MBkfDKYN1q/WJkgih9C76MvL2g7q
w3dtvEF1XlGythsgLmsC5GbGr9ZCEzYlE11wti/ysp0zmJAYffQmpHIs0+UcTYS8MD2xBJku
QhwhCX4rgl+rl/wEP8HuqpluIdzIFNBL8HPdkJz13lljxhvk4hOKvQfy0bv0wOb4YSWTo+sJ
TswMr66Ec7sD3TPOw6MLp3F0JXzfA/ETFwB7nH+tSy4XAvsO8AgOXmcQxoq+c6AQoRBT5bvv
cPbPFrxA0/pasTfZob9h0YpcTua+C+AQegHAQDYFO74bXAYBQC28sRoV+9TnARUNYDe+ouDn
ymdvOvTzQhqijQBxhWbvBnwj6HThc2OqYQ26jGCvzR4f94h80+HbcGBwtoMt/bTc4YMHePFV
D+jR8YPOoC2oDYFk3498z90QzIB1Bm4wKXkqJ+NrjIODaoJBNBuROw/eo+MRo0fr2IjcOSwv
QI+FXTx06orLgvc5oW8a+lC+2txBs1ANOiL4TekYpC6jc2GxXsGjYzCw4qpW+bUKP361scsJ
veMef1KQvYY9rwqDbQOk4KfMr+BW8BP8vvxVfq3CT5nftoFtN+9X8BP8BD8Ne274sKcyv93A
YNtiBD/BT/AT/DYcfsr8tg1su3m/gp/gJ/gJfoKfNjTaunV/gp/gJ/gJfmsLP07h2sd93MeU
EZOWMMEYU9wGh2lQZfJMMpjdVO6CmlPgXKbYYTI7ZkJ7zEozmOkM126yD8Ucu89J8BP8BD/B
b0Xw4yk/dZgH6wbc7hqzK8GM0YWVTphz7LEeaqj3w+YkaINpzrnHwhNelEuYvoqFSJz5jOU2
YVzBh+nIWPlUpiVjunKJwvoZHCNjdZMZUXTN8FvlsCcbETvB79hBa1UdBsFP8BP8BL8VwU+z
PZX5rQ8UBT/BT/AT/DYcfprtuapsaZOOI/gJfoKf4Lfh8FvlsKeu+W0KAAU/wU/wE/wEP832
3LoJOoKf4Cf4CX4bDr+rDnuOEzQzbxaIW9ll3D54qCkdJm8G3GYO95gdbwqMyS2a7Lkpyd7y
+xD7xD6xT+zbcPZp1HP5pK/n45wcwU/wE/wEvxXB7+BXOoyLH7SjkYA2f5Kp4Cf4CX6Cn+Cn
YU9d8tN2ftrRqGy+VDbzOeyHtvPTjkaux1ZIETsl1qXqWMtu+4C9lbA5o9UyPy3zm5+BHaus
VZmfMj9lfsr8NjzzW+F8F93f5VixatWvK/aJfWKf2Lci9h184re7O3uucr6L4LdqCB2r4wl+
gt9Wwm/cv95gX/UB27aLfmtLP014WZ9hxmNFuaO9rugn+m0l/ZgyWMHPhIFpUVpb+B186ldX
A2pTh7WfICP4CX6CnzK/tYXf7jK/q17zS1rkvvbwOlpGt1u/4Cf4CX6C34bDb5UX/ZT57RYu
rccJfoKf4Cf4CX5a57d1maDgJ/gJfoKf4Cf4CX5a5K5F7lrknnCvY2wSnssif9PhvsbOut6n
Xovct2uR+zheqhtbbyQYlfkp81Pmp8xvbTO/3c321ISX1q+/HYv2CX6Cn+An+K0t/HY321MT
Xo4FXFp/TcFP8BP8BL8Vwa/VXR2U+bUOomPRPsFP8BP8BL8Vwe/g72+2u8xP8DsWcGn9NQU/
wU/wE/xWBL+Dz/x2d81Pw56tg+hYtE/wE/wEP8FvbeG3u8xP8DsWcGn9NQU/wU/wE/wEP63z
28jlDFcHYMFP8BP8BL8Vwa/Va36rzPyYa8Yu6cbWaw9LwU/wE/wEP8FPmd/aw+zqsrwj/U7w
E/wEP8FvRfBrdcLLnmd7jimj7vCykWAU/AQ/wU/wW1v4acKLNrM9Ula3G5/gJ/gJfoLfiuC3
Ddf8tKXRbsCyDjGCn+An+Al+K4LfwQ97KvNT5rdX0Ap+gp/gJ/itLfx2t8h9z9f8xoq65qdr
ficTlcOQrHXY3SX2vBpMV8zZehdsn/uyBwxceYjZG5OzoXwQ5G3s49C7fgiegqWrtzkHP9gU
Ta6uaHyKcfD+i1G9cUOOMZts/BiErWVyDKg6GFNfr48ZrQhohbHVFZwfonM89lDbEFB2ATH9
UF9vcEHwE/wEv7WFnzI/ZX7K/AS/k63vgh08egEmumxK38R3g8s++hgNNios3Q7fRexLl4fe
WuPGbofvUvQ5eYtybzh4NfYhSkfiyh+oGU0YvA3D1K3xXW8dXhQdkuxCqek7E0NyyUb0RGLt
IaG3EnvT22itr32RfkDfxPhgQva1X2Oxhx56NaF30ZeXtV227OgYb1Cdl5Ss7Qb0rKwJ6GuZ
sV9ju97blPCug7N9eZO2cyaFgDfuTUjlWKbLOZqIvlUM4ydhuoieUUiC39bBj73f2GUPvWDv
xoz+9UDdYAFfCjkkyjmPvWa4sJ8jOvgRuzpik8cxSsv81j4ZZN425W/BpmHQXrbay1bs0162
Jyf0kNhdcdH6GCL7Kwm9DrNde9nybQt++BD2mly1XE/w06inRj2V+G1d4pd2l/kxMRD8BD98
AkSlLvnxY0gGgyA9wTmUTjFdCYN6Dtc0Mwbgxg8L43cpeN/3uLA5DQjiEicG3qxLLpfrjr7D
qGFw8DqDMFb0ncPwI0cDY6pXNX2HYb+MERrHcZpasTfZ4SqrRStyHc/UqKdGPXPCFfnQhzKg
nTtc4IZqMAIdYi4jwqnLGFW2vfEeI8IDz+9pRfA7+JUO1H3qTMoGY1Z9SJiNML4hvLsQE2Ym
4M8ljwlcTpgT0ONPCoP9gt9mZnNzMk1lfsr8lPkp81tb+O11vsvuEr8jjHryBZEL6pLf2o+E
in1in9gn9m0d+3aZ+B0BfprvMie5ajlW8BP8BD/Bb8Pht+dRT8EPeW7LAPty2ib4CX6Cn+An
+Gmlw8ZC7miAFPwEP8FP8FsR/DipK3VYfumGgMWZyWJ13OjCHS6w4NLjPhhD5pLOhDtcYEoO
JnrlHmsumWEl3CwDN6Dg3C+sNA3jxTwsO8UdL8pyVCxTLVFYOopjZNzVwsTq0nyXo53g5T96
5ir4CX6Cn+C3Ivgd/GTPvc530TW/o0NhW4Ap+Al+gp/gtyL4tZr5jav19rDS4QjX/DTbc1Pg
KPgJfoKf4Lci+LWa+WnCy6YAa5XvQ/AT/AQ/wW/D4bfKzE9LHVYJoGN5LMFP8BP8BL8VwW8b
hj0Fv2MJrFW+tuAn+Al+gt+Gw0/DnquExqYcS/AT/AQ/wW/D4bfKYU9NeBH8tJWt7mtdsKnd
/Moty02Hu4w7bCqY7WDLrssZm8VhW8MetzAfsD8zF7xlbB+IbQhx4/Ps+3HDwtwNwQyp924w
CbvIlahg4+BwN/RgEM2tCHPnsYEh7kIdow9p4Ak4Y1mc6bEFIzdsxhbNxWWxgaHua11udb18
X2vBb1OAtcr3ocxPmZ8yP2V+a5v57fOmDkdY6qBrfqsE0LE8luAn+Al+gt+K4HfwSx12B79V
Zn6C37EE1ipfW/AT/AQ/wW9t4ac7vOhOLXsFouAn+Al+gp/gpxtb68bW2A45+HJxvnAxYhfo
jKvvg+HoN13ayF0buduAreNHRfhOE1404SVg6s3gnD34Yc/dZX5a6rDX7GiT6ynzU+anzE+Z
nzI/ZX7K/JT5JWe9d5hX7jyvk6N7gN1YkO9i2xSP/u3oSthpRUsdCjaV+SnzU+Z3cuzi0IfB
e2zaZJKlJjY5a9qE96bMT5mfMj9lfivK/HjK36j9/LTUYYMhLvgJfoKf4Lci+LV6zU9LHTYh
U1v1exD8BD/BT/AT/HTNb+uGaQU/wU/wE/w2HH6a7bnqrGkTjif4CX6Cn+C34fDTsOcmwGrV
70HwE/wEP8FP8NOwp4Y9tdRBSx3K1H3uJWAP++G7GLGzgNci986FPvc2+wEbN2ipw7Fb6qB7
e2pJxV4zQmV+yvyU+SnzW1Hmp6UOWue3PjAW/AQ/wU/wWxH8Dn6pw+4yP0142Wt2tMn1BD/B
T/AT/NYWfgd/b0++YuySwc7FcQjO5RS4T7Hu8LJ21wwFP8FP8BP8Nhx+q5ztKfhtSjYo+Al+
gp/gJ/hptufaZW5fLoQFP8FP8BP8VgQ/TXjRhBdNeMlDxB4IZtr1zXXexh63PXf9EDwvUoO6
HlPFc/CDTdFw1JyuaHyKEfdG/2JUb9yQY8wmGz8G9T7lGFB1MKbMxXddH7OLOVjvzDg933XB
+SE6x2MPdSuGgLILiOmH+nqDC4Kf4LfV8OMfR1oR/A5+wsvurvmtctiTZy9d8/tys64W6ivz
E/wEv62GH8Eg+KGDPVSsYQJLSOhg41/pNoN0vUNnHpuYDS4mXfNrAVyraIPgJ/gJfoKfMr9d
w0+Z3yrA08IxBD/BT/AT/DYcfqtc56fMrwVwraINgp/gJ/gJfmsLP+ZhqTMpG9yYsQ/JOj+O
4xrMG4gp9dH2GL4s1+lywqSAPhljHCqMLu+w83q0+SjDnuPFQg17buRMUMFP8BP8BL+1hd/u
JrzsGX5jRcFP8ON8TDcMyaJ7hS5Vz24RXbgWjC5VQBerr7MvnWZ78pPJIaTgfd9jTmu5+7Hv
DGa3xhitSy6XKae+s84GB68zCONH6jtnUTAhR3RTy0fqO29iRifVsataK/YmO3zk1g74AsaK
weJOyzmY6LIpX4/vBpd99LgjNe7YXaNin/o8oCK6wPVYKfqcPF4296Y09bB7WtdW6MbWPNta
oxtbh8zJ16kLEX/4042tD36pwz5nfkeAH19Rsz1XMex4rI+hzE+ZnzI/ZX4bnvmNo5d7GPY8
Avx0ze9YQ2tVry/4CX6Cn+C34fAbGbYa+CnzWxV8jvVxBD/BT/AT/DYcflfN/HY330WJH8Z4
jzWj9uv1xT6xT+wT+1bEvoO/5Le7+S5XZd8uJ3seAX5K/PYLRgd9XMFP8BP8BL8VwU93N9Ot
PdcnUxT8BD/BT/AT/HZ9gxfNdznoDG2/Xk/wE/wEP8Fvw+Gn+S77BZB1Pq7gJ/gJfoKf4Lfr
zE/X/NYZeMttF/wEP8FP8Ntw+O15wstY8Utu8CL4LQNknZ8LfoKf4Cf4bR389rzSQexbZ94t
t13sE/vEPrFv69inlQ7rMylzGVirfC74CX6Cn+An+OmS38auZT8aMAU/wU/wE/wEP8FP8MOe
WAG7AvDG9ditIcR+GLKNw2A4WZgu7enAjyGZHF1PcA6xfjIpmd461+PzSlzriyjt6dBHzhjA
RxGxQUWPDyhaO25c4TpsUOGS8dy7wnN/AETZZHPGp9a76MsuEraD+kLOBlta9KZ8rLYbBmxv
YQK2EDFD+fBt13t86NjJImDHC16UsbbDjm0hYDMLb0IqxzJdztFgQ40B2xCUINPFPAzYd8P0
MbtyKNNB6iFhg7eIttR6vRuwy0aPjUww84FH154O4Yh7OmzDGnct8ztaJrVufpxwXD09YUei
BMgJfs567BqE/S7Lppg8cfceyMful970E+kEv7E75DsQH7so+ZQz+kokA3ZtiiG5ZKOxgh9w
mdyQYulQZtAW1Aaos+9HvuduCGZIvXeDSckTH7kL6G86bIMVDKJJ4Nx58N6EIUYPNPMEnLGT
mOmxC1VEH8KVv+LcWfA+J+w3FvpQ9qrKHTSLbbDwXeA3pWOQuozOhe2x2Ss6BgP//NOGZ378
q42dbmut63zLgBb8NOxZeKXd/JT5OeTYGMgIjmxN6PMxWQcmfQxleCMh5zauBzUjkuoj7ea3
DZmfZnsuA2Sdnwt+gp/gp2HPDc/8xtV6y5mfVjps3SW+wzkt9ol9Yp/Yt+Hs2/Oo5wjNL1ni
rkt+h0NkXcuCn+An+Al+aws/jkGmDpfjDSYr9CHZ8UI9XN6HmFKPa5uYQaVLfvgE1hVS+9Vu
wU/wE/wEvxXBT7v5aUOj9YGs4Cf4CX6C34rgd/DzXZT5rQ9s9iuD2+txBT/BT/AT/DYcfnu+
5jdW/JJrfprsuVfYtFZP8BP8BD/Bb8Pht8prfprw0hrE9toewU/wE/wEP8Fv13c3E/z2CpvW
6gl+gt9Wwq/c/QR3KdPtzXSHlx73ssvDrumncc/WKLbX9oh+ot9W0o+nMMFvW25vtspxT8Fv
r7BprZ7gJ/gJfhr3XNtxz/FObNe00G/PM16OsMpd8GsNYnttj+An+Al+gt+Gw0+Z314Bscn1
BD/BT/AT/AQ/XfPbulvACH6Cn+An+Al+gp/gp/38kvbz42SQso/rYT98FyN2gPM2DNhflhdS
sHmf9vMruxiazmTnsKdutoM13Jw3dxmbAWk/P959E7sY99hX2AeLzZ754aTO99hyMLgh99ha
mFpK2KAweOxHPGCvwRjGq3kOG2dCcAaPJo0ubBKJY2RsP2xide3bNT+tcscXs6lDn8r8lPkp
81Pmp8xPmd/GQu5o8Bb8BD/BT/DbcPjtebanMj9lftjBmTIgKochWWwcgs1Ces6hoivmbDFc
gc1D+jJOBhd2hM7emGlwzHUe4x5x6F0/BF/WWMHVW+w24geb4rjmGK5ofIoY5/BfjMJe0liA
GjOGPThcgtfrfcrYczqHwZj6ej3GQGIOaIUZx+tcF5wfonM89lDbHlB2GFgxGHoZDzW4IPgJ
foLfiuDX6rYOgt/Rsp9t9ivzE/wEP8FvRfA7+G0ddrfO76pLHbST+9aNch7OebFP7BP7xL61
ZR8HkfZxM1utccfnezg0NqUs+Al+gp/gt7bw213it+dRT8FP8NMlvyFhNrXHxcLxWmHCBGzX
E5xDnFzJYNI/rmlmmzj6g35FDiEFzynduPxIl+8MLnHGGK1LLpfrjr6zznJ2d3QGYWOUsyiY
kGOqVzV9503MmCbuvMOl1TGqx9x6XGXFPHFccx1dwQ4e1z5NdNmUK7K+Gxwm3HssUcASjhoV
+9TnARU5gXysmKLPyeNlM2aZ03XYIodS1EoHrFvgh2M6F3CB22aPjztopUOI+MtwzrZ6ye+q
o55Jw54bm9HtNjNV5qfMr0BZ8HOl42E6TO0KCff5j8nmgnzT9W5AdwTzrNBpEPx642MKoa7W
CxET3Sb4rc8lv73DjwKIXTJY0xmH4FxOYQQppvNhCaxHD9Wk0g3Y7UlYccdmaFXwE/wEPw17
ru2w5z5f82OHCKRD7wcz2iP6QOgSCX74BDYB2IKf4Cf4CX4rgt/BD3vuDn4jw3LCUqgeVxIw
2r/3zE/w2wTw8T0IfoKf4Cf4rS38djfhRdf8NgVYq3wfgp/gJ/gJfiuC3zZc81Pmt0oAHctj
CX6Cn+An+K0Ifgc/7KnMbzOuvx0LCAp+gp/gJ/itLfz2+Zqf1vltyOSWI8FV8BP8BD/Bb0Xw
07CnljqsTyYq+Al+gp/gt7bw213mt+cJL8r8lPnpDi+6w0thpPay1SL3LV/krgkvRxpCXEef
Mj9lfsr8lPkp8zvyXrbK/JT5KfNT5qfMT7c3w3nA9VeT+W3DbE/d3mwds7wjtVmZnzI/ZX7K
/NY289vdUgfd4eVIJ/9t9wl+gp/gJ/htOPz2POFF9/bUsKeGPTXsqWFPDXte07Bnq0sdlPlt
e5Z3pPevzE+ZnzI/ZX4bnvkJfkc6+W+7T/AT/AQ/wW9F8Gt1wsue4afZnhr21LCnhj017Klh
z3Ud9tQ1v23P8o70/pX5KfNT5qfMb0WZn6756fZmur1Zxs7H3picDUccgFhvYx+H3vVD8LxH
Al29zTn4waZocnVF41OMg/dfjOqNG3KM2WTjx6DepxwDqg7G9NUVs4s5YK9KY6srOD9E53js
obYhoOwCYvqhvt7gguAn+Al+Gw4/ZX5Hyny23afMT/AT/AS/DYefrvltO+iO9P4FP8FP8BP8
VgS/Vie8KPM70sl/232Cn+An+Al+K4Kfrvnpmp+u+emaH69q5hBS8L7vcWWTnWLrO4NrnDFG
65LL5cKj76yzwcHrDMLGKGdRMCHHVC9r+s6bmG0/OO9sXyv2Jrvc99YOOZfrqL4LdvC4+Gmi
y4bdXbzi4LKPHtsxJGdrVOxTnwdUNG682uq7FH1OHi+be1OaWi6dHvbDd9rVQbs6XM29PVuF
3yozP93bc1MyRmV+yvyU+SnzW9vMj9251JmUjbGpD8k6T9LBhUlzMaU+oq+Y93zNb6yYeocJ
fDm6wcUk+Al+fexLauE6zLPMmGcZoLK+TrV0yvyU+dmIqbexigTTc2NvehutHdNb1yGNdcl4
Zri+TuS1CROAkS/3LvoiJdtly5m9Bolvb5hYWNsNOBNZEyA3M07ktV3vbUrIdwPy4pLe2s6Z
FAJSXm9CKscyHc5fBmn3EMOYA5suYiowsnPTY7pwybpNNxh4hmgj2lLr4dyHXByzjJExK/O7
msyv1Wt+q4Qf5RW7ZJzzcQjO5RQ4EhM7TGYPmKeO4RmTLD+JTYHEpr4PZX7K/JT5CX4bnvmt
cthT8NsUGAp+gp/gJ/gJfkfezPYIw56Cn+CnYU/XE5xDLMNlrsOwW28dVvFnjMBxfE4TXjTs
GTHkirlNA+7cwLGxjHFWjNdCINn348hu7oZghtR7h9Gy5KmcjHlLcXCYJhUMojn2mjuPkV4T
hhg9BmU59ppxvcH0mKXEWzng5g3FZTHSm5PzKfShzGXKHW7pgGlSGILGb8qQcOoyhpUtRi89
hoQHVkxrCz9+Etd8zU+Z36YAa5XvQ5mfMj9lfsr8Nhx+q7zmpwkvqwTQsTyW4Cf4CX6Cn+Cn
Yc+tm6Aj+Al+gp/gtyL4rc9sz3GCZuaqWczszbh98FAv5mHyZsDwM2YdjzcFxszO5ZUOuuR3
LJO1Vb622Cf2iX1i34rY1+oa91WOegp+qwTQsTyW4Cf4CX6C39rCjyjSfBctKdwLRAU/wU/w
E/zWFn6a7Cnw7QV8rCP4CX6Cn+C34fDTsOdeAbHJ9QQ/wU/wE/zWFn4a9lTmt1dAC36Cn+An
+K0t/PZ52HNcHK/Znhu5CkLwE/wEP8FvbeG3u8xPw557zY42uZ7gJ/gJfoLfiuC3Psv8ktb5
bWQ2NwfWgp/gJ/gJfiuCX6vr/HRrzzlQ2JZYwU/wE/wEP8Fv13d40a09NwWOgp/gJ/gJfmsL
v91d81PmtynAWuX7EPwEP8FP8BP8dp35EbfayH2VEDpWxxL8BL+thF/Z684abK83DCGJfqKf
6Ld1M2BEP9FvK+nHDrzgty2b2Wqtw7FKr1p+XcFP8BP8lPmtbea311XuWuqwdYne4RwW+8Q+
sW+r2cekKG0d+/a+zk+zPQ+HyLqWBT/BT/DbavhxJuSmw2+Vo56C37rC7vB2C36Cn+An+G14
5rdK+Gm25+EQWdey4Cf4CX6C34bDT+v81hVQ+9luwU/wE/wEP8FPKx22bgKM4Cf4CX5bDT9N
eBmizcOu4adrfvuZjR3ksQU/wU/w22r4beeEF6102LpE73Cuin1in9gn9m3dqKfYJ/a5zrHj
Vxho0zAYm4KPVEZxxX4Yso3wc2yErmFI1jqf+thPFWPO1rtg+9z3NSoPMXtjcp7qeRv7OPSu
H4Ivt9Zwne9tzsEPNsXxVlNwReNTjIP3X4zqjcOARMwmGz8evPcpx4CqgzH19fqYXcwBrTC2
uoLzQ3SOxx5q2wPKLiCmH+obHFwQ+8Q+sW9F7Gt1Nz9Ndzk86VG5Em4ineAHug/JWe+dNcb5
SvfYeyDfJOC8rxxNJkfXE5xDnFzJ9NaB7tkm7mqGY+WAm0Z63/dAPM8L1ncGsI8xWpdcLgT2
nXU2OHidQdgY5SwKJuSYKt99503Mth8cmtbXir3JDv0Ni1bk0qHwXbADui7BRJdNab3vBpd9
9DEavLEaFfvU5wEVjRu7Hb5L0efk8bK5N6WppQ9x2A/f4TBh8DbgFcduje/wpvGi6JBkF6Y3
GUNyyUb0ROL0GeLN9PiAorXjm3Qd3oxLxvN9+tqvsQn9IXxqvYu+vLbt0PVCR8fg7femfKy2
G9Czsiagr2XGfo3teo8PHe864NMpb9J2zqQQ8MZx/65UjmW6nKPBhz/EMH4SurEnvk1+QZu+
yo/vMXY5oXfc408KstcS9xso81PmB3QEJqD1/Cv4CX4hYQZEBIgrNHs3oDuCEQd0GjjbAXcE
dWSvzZBNHJFvOnRFHBic7WDLIEXu0OsAeNHPGTCcwR5Lxm20QW2AOvt+5HvuhmCG1Hs3mJQ8
+Z7Rh4mDQ5cpGESzEbnz4D1QFaNH69iI3LloevRYOL6BEY3isuB9ThiYCX0o/ZrcocOGLhM6
IvhN6RikLqNzYXvj/bbc2FPwU6Z3VdiXsU382ZRHZX7K/JT5YYRf8GMyGHsm68Ak+c4hiYSc
27ge1IxIqjN7i6kLSKP7AAwjj7cHv4870/zUIZEzuGDTh4QrMmMqC7SHmHB1BgMlma3fU+Y3
UhMdGAw2YKxncOgSlWMlg55OHIJzOQX2a2KHqzoYFfEYnjEY9YBLwGn7MxD8dM2vDMdq2NOV
IWfTCX6OiaXghwH4MqqOrfsEv00EueAn+Al+mvCyogkvB5/5jZy+psxvz8Oeyvw2OIMV/AQ/
wU/w2zr4jSOVmdPH5q1w16jnpiSBYp/YJ/aJfVvHvr1P9hT8BD8t89NKh4JNrXQo6zs02fOY
zHfZ51HPcaKMLvlt5NwdZX7K/JT5KfNT5rfrG3sq81Pmp8xPmZ8yPy3zO8YrHZT5tb2aoGVQ
KvNT5qfMT5nfijI/DgCnDqv/3QAo4oYqWB03unBzQ9xrx2NJ4FDXB/K+RwZ3Nso9brczriJ0
Efce5M2OcJOhMGINdxzCzQ7LnYhwh6JyLNw1CMfIuKGhidW1b5M9NeypyZ66tafublYYqbub
8QSsG7w0s8Z9d5nfyLDV3N1Mw54tZ3Nz2qbMT5mfMj9lfivK/DZumZ8yP2V+yvyU+Snz0609
27u7mTI/XfObk+0txyrzU+anzE+Z34Znfnse9jzCDV6IW9zwTLf2XPvlD4Kf4Cf4CX4bDr89
391Mw54a9tSwp4Y9NeypYc/2hj05/WQfN3UQ/AQ/wU/wE/wEv/bgt7trfsr8lq916fl4nVTD
nhr21LCnhj3Xdthzd5nfKuGna36bAk/BT/AT/AS/vcCPG8yvyV62gt+mAGuV70PwE/y2En6G
dx7BYvWI/UpDEv32Qr8mdnLf3bjnnqd76qKfLvrpop8u+hVI6hYvPNvqFi9rdouXVaZ+usXL
KtOvY3kspX5K/bYy9eMpTJmfN2EgGNKGZ357ht9YUXsarf2iviNBVvAT/AQ/DXsKftrTaCMB
dyToTT7BT/AT/AS/DYefrvlNJ3w9Xnk/OMFP8BP8BL8Nh9+ehz014UUTXjThRRNeCiM14UUT
Xnrj45pNeFHmp4zvyoxv+iyU+SnzU+anzE+Zn6756ZqfsSn4sv9y4WLshyHbqMxPmZ8yP93f
bF3vb6bMb8p29HhlBqjMT5mfMj9lfivK/GJZNtHn3g0hBmydPpR+dOp6G3sfvQ+2H/K4Ot73
fTDBDbkP1pJOqXMxeAeX7U0M4/J1Z5CSeWvwaNLosn3EMXLMzsTqMikbdNv7kKzz49oNgxeL
KfXR9jnrmp+gdyX0ps9C8BP8BD/Bb0XwW5+t3HmHn9hl70DjaPOgUU+NemrUMznr8SdhzNiF
RO8AfdZBo54a9dSoZ3ujnvt8Y2utcddkT13yE/wEP8HvmuDX6qjnni/5CX6Cn+An+Al+gt+6
wk+X/KbLXHq88tKfLvnpkp8u+emS34Zf8ttz5jdW/JJbe3LSTeyScc7HITiXUxivH8ahD4P3
uIZokmUOLNC0/RkIfoKf4Cf4rS389vma3xHgp00dNgXqgp/gJ/gJfiuC38Ff89sd/FaZ+Ql+
gl8fe46kk54xZ4vlOVhP03N3Z7oy1vd4Y3I21B08Hut8MC7g+iF4yoeu3mIBjh9siuPWonBF
41PEuh7/xajeYCVQjBnLfLg8CPV6nzLWEOUwGFNfr8ean5gDWmFsdQXnh+gcjz3UNgSUHRYS
GSw1Gg81uCD44UP1XYo+J2+xmgpLrPjhlI/xsB++093NdHezq7m72cHDb1z5p2V+mwKkg3wf
BFU4bYF/l3z8WnxYXHI3/rzi8H9fuIK/+zjt+ku/Zyz/HQdbrjIe55KPX1HqlZCr/Dip1pl+
8fW35TO+/mg8Jm0sLz8W59X8eOACr3udBy8uXpy7eNLiafh5Pj20G128OAeex8DOWTwVv3nM
wizCYlh4/JcZcfIUcZh/OgIfj99BtOGzG1+EYzwWRzlSrQ6v+3j8BnE3vMdiZ3HGYa/WLZ68
uGBxHn9/kzMXFy6ejuhnLp6CGvbokYw+3L5iB690Po7EtlyId/bMxeMWT1xcBM/5i/+44on4
yXd7AX6P2idOpYum4xz/nMVzFqexdK36yOc36hcO3rjo8dPi/ZqlxzDVbeXx+IvwuX3xe15Z
q44rR7rR4oQj6O24o/j+4gXjL6bff9VhcZ/m39hlH/3Omxz60l8U/2JhXl79n2XcMf13e7z6
jWe04C2I3YG9AXZiqXfo0EvL43juwN/yxy9G+QgavlpfOUT9wbrX9O+Uawo4yu9PvDZ/MX1v
D1uKul95fuXZaTpL0d0txZWnNz/cgfJx+Dd+JF/85W6/3/2Ju+kX23HFFZ85/oaLe1/49Gde
cOY5F57z1HMvPvfCr8ZXePgnzTP29O/Kt3IdgOMrq3s5Yor80seRMl/qu7J0s/L0yJ8yf3XK
Jfxurq5d5QDTj8P+aH/7k/e/629/8pN3mX59eBl/lIcWi9Nge/nHVo//Tn/oFX96xacWp9zv
Xve9V/neb3fc7dDq/7a4x+L4a/Effx6Pfydc+wT+O+na1z7x2tc96eSTr3vSda978vVvdP2T
r3fD6133ujc49QY3vNEpp5x6ysnXv/FNbnzKTfD8FB7kONY8/oSTUPGU6133evDO/HfFJxan
nnT8p/HfcacurnXqccefetwVv7K4GZq6OP7/Z+89wJrK9oXvHQLBQhVQOhl0EFCQGHpnhuLM
EBkGQiygDFFKkN5Dl1FDx7HRBAY0QCIgUkLoKm0QiBACSpfeQg8ltG9zzj33nHOfO/fOe577
fu/3Ph/7geyVtVfWyv6ttf7///qvlbUPmunf7gOAcEA5uWDcR8GrhgIQAAKFwDhgRzi5OKEH
acCrgpxcJ75CGFn+7AUTinz4W6ew7EXkNz95F592ePuFW+Rbq1/PGGOXVO8uR4E5nPynrP9S
BoQDjBcXPLgAHv9eLCAIOch0vw/gAQviEIQKAgbAXn7E3xMchg4JHBI4JHBI4JDAIYFDAocE
DgkcEjgkcEjgkMD/vwnwBfcx5TIclYeJctpmYhuGWspuHxAbNq7kJifBXSNiQVleZjFuUD8o
M0llH1DrQW/mJSoahbexMhfMduyP9KW27FhbPId/vvyp26yf4h6SjWVHuUk4JrJUWWYzyZnD
wHSOy/TcVIB3eCpieZwvxjW7Yii7gqTTMC72v4M7NO16qSpbXKMInZo73yk5Ln0y1xXH8kHU
zE7vlFos6hnRBOvFmu1v8YyqHBR/3pyu093WsJFgP+xhR6a07lpJkca2o7KHPlXJBDumVruk
h7zt9HCdwW172Ul7ZX6SUmdpBw8o3cjOZwo1D/Bm/U/fgm78S0rBzKqTWewzLdTN+5npUVOz
VO/d36v8qYUkaluUnwDv4+YfnQR4cpIv/lvZRwkZnrxPWeKxNwPwlSHI9wN8acHXMWb9A4W6
WKElbpOaElzYerv1XkpbuKFvf+/0gneducVq6M0BiVEHLEIr4sf/wXtwrcsrIVI0igZiFBLe
8Kf1XXdfL1G/4ziYUZdaZJCkW+9GuaRBF424E3GLJ+vv3kQA4kwi+6T5oY33gfMjUifXE94M
s6uGREzDK7Sd+9XMhmZGQ1zIbIs28BIxoVbIztpi1WoXG6HtNljmj8RNqDWvdBgdOJL/Jw4+
qZyyUvaRwe0PNfLRE1OfZJDknlk1it5t9mrf6Sf6P/ICxZJGtQTYdIQT0AoBfZ7/eMA0p4o8
3SlkxrVt8ZgdYkCdp29/HzsmbGVQZCv0KlgXxbnke63KlmNxze8J2m5zqpRAy7DoDLpmpqfG
P+bzL4aPoq3pQmgrQcEmRzz0Xd+NJCd1VaEvGmE3VQJ9kNbtaPM2mlhKxsUjgLqlpLEHkcuN
mNLklSjGmcYODjlX556yyhnvnphZmFqHQsKLCzst2M9O7wMT8OKCj7TdQcSUKKzVtcTWcXDb
L8iah+KoOSLwz9+TI7BZ4LY7s/+mn3+lrmw+gRtVk/8q5x7ayodl1fwlwvd6v/U+QM4l6bqk
722CF19mU/dKrdg5wAyR5Bo/qxiTU33ZyPCf8/xffeczy6oM5a27mlcklZ/gF2So7+Ts5mb6
8fnve1KvlrLPZmZ6egHARYJgOupkjsZZsQlzn4dX8YMmHSedY72Gn9+U52RLfci8xkKjh/He
X13+dcAzOrf1zKnpYpn7RZstiOeqZtpOexd5HBsRmznwJt9i5PNPKYv3jjns5u9JzT3eB9Zp
C1Gk2L5Wl+jCGOWGpsDQqyLprq+c/BdY+XuBDcFblzSaFOPoCMTIf7yvM3fpSONFS2u63kz6
JY3+PvEPXu922vzJiRsgqDJvTbti1A3VDggdlEXntq+vgR1gBbxgEjvsh4+pfiHxH7P7X3gv
bUPvf+obVJLb2D9Q9zTTIEnffXe7j1yC3/29MH8O3gBAHOSMLa6qYWZfmbJCiEGNBlqWvVgz
lEwDVYeuO+nEzi7H5Je5aziPJQzAxc9191ovEZOXm5yG4e/IFNKUf1FgnBPeKb1F5np11IWr
/qcF/fOWWi7GljUsx+BWX9h44Rm2ytdSQ1zSd85O8qWeK7E1tlKl3ffSn+EidVsc3TCHZhTw
VjqpZ5Otdh4lPoAjC8paKy+Y4WpfbbN3OK/0dFocX58rG7N21Fuut2GD2qVdpNHyCzzrHwlc
AiI8AcDceA3Wjy9AFVV1Y6TF2oJfSKmvN5ESq4kxYx+E9oHaet/+fhvcF/9238AmOZD0zZyq
dT9hY9r3uf5h8GEhIbHov09h/GPu/10Ycq+/fL4/jeIaI58b19ai7+PCNgqwTNM+309pdZ1A
37CLHIuSB8Xw8gTYb4OMoaKxqaQau+ezbiupVNQNu5wxg5pl6XsFevEiFUOEoeZjltfchwvn
lzOk4OL7QN59LhXZ+qwI4plvpRpVeKZrvAmNah06FqKClfE3p3L6zfeB70Qq03rcw+TXlzKf
NYihBN8nID/A6T4mOCe80gKDpuqZ+UAFO8uy2WucLtSxTdDfhM6odW704WeWc+fM6iWUhksC
Fhbo+h8d/+FGIW0ngsGJDzBGqXLh2jZpNmetrV7bjYlyqw2QrdjDhRnOUMr3gUH69l8Ft/p6
YUytkLdz5mRcSBCUFPt0wdRtgFixaP6vWAGa6/e76Xdmkf4Fc49kbAZ8Mh9DJ8r6zaxK3T1u
kIWNd6+dfgxNhTw2lAc8CamkdGM/mI1vr5+fqUuq22pM8GbrZsJM2rXvA5wberdlqa4k8qMa
60kjWRUY5xVhwBBQUVA5PgmDqMC0orSVbXPmMYjtI/2mpLxt6/DmB+silc9NUrfajDebDF4j
B4lYhGbCrt5Ir8937oviTLr1nvPUIqwoe4CyoR0zs0SeM2v7tgdXsDuRXKjTadBlcs3PXy4A
R3Iml1lGw6aTSUghofG/U5UGIuwBlb/OiJkdbfPMWOLtYfV9sFXoxiQwLm8s8JGDcbsGQThQ
s7hsRRGHPncx3k2o9a/GNdeDdgnedUBpONupPHA7suLvef6JkIC0XPdaTOzV4qzkwlorn+eI
ieF1Wfda/8oFu0J320IcKb+trcPR+pLJbaAFkHNIjibH0RSx6VG5qOxClqX3xpEEy65kwU7/
3ZP5LBu9N+d+zU/JgDtcBJR1CMfseSARP2r6QoGDAFAPcNDVLLWy86OXktxyrbwzywQxiQob
9RpWJAqmry2oKdz+TjTFJx6ZqUDb4CS1n5J1TibmzZ3gFXF2Jvq4u1IMPujqDfyCpRZQ1l2z
x/1JGres2XY2e3uNrbpeyRv16te7P1HFsieQTFjbVNzfbv0sHIDG/fssopxsEJiuLqx38EZh
csJDDL8n2GzdbsvgnKky7ZfPjoDWk3v0NlMPNJiit6DEoa5O24kwhcwpdl2FtgspNUe1zTzg
z9tMsOc2ZIucMo2yU7Ix2GF9Af6nfWkBlkXt5Ktl2PJAxtSK4Kp+Ev6HN3piHxmFfX2VSpbm
nrkG1/KZAt0/SA49cAvNmTl5t6CGTL+chiKnT88z1musvQuLxKnN93WIhfr3RB4D3GJk75gA
MrNLd+8bndLKY87RNfjCkNmHV3FqOp2z801MAb47TnF3R8BVOKJcyQINMdgIDo5kQJgHgCsk
ZHMkL0EBLNxQ3SqMaRCLP/1iGdanFvgFjZS2DQ9PVqfjGV4dmf0bW1EK2elOmqsTizBypYSG
E77Kum3P+Yv+5iivUFZhgrraKXmmSKjz1o6xBXs7HDd4CrvlJLSQmUxe++C7VGPivw9Ye25E
uWko9a67Rq9Hwf9SN/z24PnoX8NgBFxeuN36MksEbb5B9NqGZg919fTvA9dwCQxjiwMtSPHW
ZzeqBXZqboKWoL96YczOAnsYg8FtghLl9V8y/O9eIJNMFCX387L6TCOY869nfwmKmvDDt5uW
zw91D6TmvvAl6hj7Ci5Jp4XH6Oh09uXcvpPmU+pf9nmA4tCGukIKMuPz+cL7deBQwj5wXwfb
ZRcq/Sg8ujKmCIOsc3I0uZpNmJlDvAs391xEtgwiDW6SOlGqVsJW5lYoBIEQZ/ytEpLA1WT0
hOw3TPbvPYbvXdki6Ulou2rrBPfK6iosRKF3TQJyyxCtcJsk2yP26GZ7c0gEGOA5BqFliUIB
L676M4F3Rw3BzgT8qAKICjR7mXN0on29svNzW43Kn6NapoRpiQqbUDdt0lmmcXO60zhvKQNX
ayU0YbANR1U63Q9czwA6b9CKMWIlgmMW/J/Ec83wiZWgNhQxtReduu6uX0ZSDktp2DFk3xZe
qvprrcH63PuL5nuFmDBDAJzx5QT47AP/vTMBEVkR0GPTMVkSpRI/7d0dv16FRn/KEDJfHlxO
TNL/NWaaamybnQf2GgSi5z/ayv9ZZUHF54iDSDs/E1W6WEpKg6F+AI79HTqouITokvt4cE7f
rvrtqvZu2CMnlwVX//vEWPW8aFLlHFkgb4eCY7vNaGxGFVKnNzaDiaSh1JTBbrfjmTYxp2m5
v5iJMRkhjr29bKE9iXmLb/PY1k7Xy5TNlst6c+Y6ghoFN7Ef4lgpKEZbYhHB9ClczJPQbhW3
Y1RlkUPNTx4iOiQ83lgVnG7r66THOMjVDsIxX394MkjG58NEF2RHeI5xjOUdCLh56CdAdJ47
SRkARZ0o+EZe2t6L4zScYxuCAGqQEbJgLFf9ReJEH1bQdqx0ZQN6W5w0M2WOff9gHfaJYWng
+iA9/MoW9BYaV2u7c9Zg4GiZ+VJ0osII7yl1vxjqZ0LKHFhppikfB3IW/EToX6wdubCqrsw9
iYDT77zgj/JJibX0gZzqMYT0x9umpMZwx/FgIwpCNxcO6RbgB/5hthxc5eBKdQdtnDf+j6fd
Q8V39gGO/C8Gv4YZsjXTl/+EdPOeK0945tTPSo3ZpH3O1mfcMNxCvSxjXTd9hdF5mvOkIkN6
aIX/2VpaV0HmdFOCn3h+6oL55QlSEEPJ0SYAO7I2FMPG7Mnhpvsyns5euDMYK1Tjama8MFAl
pRkmupyhl61VFD23Nvjkjb97w8e+z1VnzVx/IJaIEgcrGoJoQYvIpqs9xf1HXmWdSghwycVT
Z1a5wxIdGegbb9Ymsa+ajxn72daZpIbaJSB7frP1EbKedLp4XLj+/vwx93rleX+BBn9hQoQG
lkPitYJqZOXRqoQIcwfDetF60SWO0wTRURjEq4H/K55j5uCyI5XjCaBKtsUmGDYbqoCrdurv
c+nW1yOJVY+XYqakIt88R/muEtY99+o/XyZFf7EOHptYAcdIZba+65eETIQ2i6fqRW07r1U1
VVkzxgjcateVe3zcyU+ntnBbUUe7XJ23a0zUNtGim1Fi5Ktm/V2TOnQtwUS6ktWBVt+1HrFp
vXCtaH4gd4hn054frheRDvbAvx5gXYoX9kfHRX38VPWTW5uzn1roDZvZlImdOnhw/d8S/dFZ
1408w/tc7o6LhvvQhFqYeJg3f3JN2Hr2+FCdN2mOnN6iMtEstmQdFD4urmfTuQ+o953Mr8Gf
3bRGN6VZShZLOTXUqWT6zUHlF2JaTyMJsA/q5BqdcqxBO/3zKjf55ce+YtPdDsGhoJavd60Z
Ek/H/AnTp9PR0FHYxa8EYFy2kEgeQCFhr5PP0Jhj7LWcLB5CSPjmkTkheZHjIdiLPKHvDEdk
l4Wb63ksfpTVvjtWCIGfAuM5xhp4QDuiAlwJkzzWcEoApgkhjMMgj9FoA0dqovPFWIoCc6F5
nvfxLCmxTGgp6U68SSW1ETTSEtGY883N61CGJeYIKWUJFpuGtMDoCG81YNdhMeUo1V1Gf/ly
11nEsuAv06y10Ng1zBdrexuhtT79oUd4nU6tTagYg2421E/1YFlF3L5MbAxxqbIoFWtoaHJw
CIk0/BtlQxXeUwXGDSPSHU19j/CnzfLJm6XN3aRwyZC3cxF/S/SfnqF22+u+PUTW9kMT4dUU
7jY3i0seuI1XLkhc21LKDjrkN8ux7JiIiwSudzw5vzgGQotQv1HDHNxNmUKbwVsbK9z5J+dn
5McEkV2ZyYWuveQaG1yGVOR9XaDBUFSgiYtTRXHE8EeeI1i4vZXUW8+vIs2PYBv4ATgfOB6K
cb+Lrf+WI7leUBTgA9FKb3LYn+oDRKfBPjDA48WVzFl/wRAOWm66kWfhS/Jri51VqUxHWhm5
Bj95d7y/u/25Uv/jayStRTQKKSjY6hjoKIdMfniu8yPeqNj/lZWOhqsz6/r6TJVFfh3KRxUt
qMogZFgJCQn1mQQ0WsKLExVgXt5TUylLGfBWtVOnc/mP1qvTX83YhBYLrcB8Z90YHaeHI5xE
rpK0LBa3IbNMRmtFkiu1pHQDqfYpOz+jqjjJh1Fc+rldtdd4g5gPI5WjZsOmrtqG5cXUGr7z
Tfs+wQo3Huxg9MuueoKGKhpbgzxx+ijDBPTrMWVIKZE28Tcy6kr8IW+ULTGKM5nOB/40cKES
Bxbe6R1NzCuMTk5Ob2g2DIX93udVQJktbDNhn54zm0xY4jf8T6vx3yIhb0vXm5450mOmwuab
GRSh5v4+yAp+8DdSn0aoY3at4LpLYonFrznPhSGWDpCHRGT2IBpNNdFh+DMno7o75wcu7w4X
YK5mWK6IMHwsTZIHSpqK2le4lazULrOsHp6A/wTUK3OqKESowHQhXvOc9Qcy6ewAjAtBEBAW
9BoQkgaweeTIo2At+0KlNiOrRhWqmPVClySy7HkCIWCniQClWHOEdD3Ea4S7XpiHw57HEfK+
zI2JL2V0NFW9zLEURqvPdFvpPMEkkmtUl2N8aIIPZZ6xUdPPNh+Eo/wba7jIrLk88kxflTbJ
He1Pws6aeNmptvVFkwLuWBnT3zkW7M7E5G1tdbnqSXXia37LLdzr7AsotEIWFts9f/YidXZo
mPgcVeng3mbc1otQpTczGaqd3jmdn1MHUUUmSq56ImuJaJNrSsWmMQudPTeqxK+W4RyqOrGo
9CGik3p+nEevNaNKlS7cZlRnsafIfM6lY7pHxs1kN6XmEduf/+YYzRhI/qJF7O4npsrlx/Ua
2KQ0IjQUi2Z/u/ldcV2j0uU3TaSFrk+CL/eBC5RTaqpsdjYJq1OMUOtE1RVopbqkpa2KtiO0
CCZF/pkW6yI1elXsbTxTys+k6LpjjVTrHL3XR+LpAruCJE/Vyp01X/RKkPyx6PLUi9qEvpq1
4KoAp86AYB/vArSgzcYdp8yIou/lzsZddsDXX4yL0iysa9e3ahAz6ZuZSHTi/yRGJ1ElVxdh
Xq8SiqVHnMRjfTpOfzZQcarBFe6NIHBBaItqUHm4LHS4X6VgZolnxM996hOfWpA1MG8Lq6fb
vKd0DGWzpIpt7MWnbs0pbIsP37a+JXr5AY7eeqd3Cgm8c2Mqak1T6lCePI4sdthQzFqQVdJ3
PVdzmY2+YSRHiAtjhjThD3l8s0S3sBP8Fmhka16mAgdWhVemsdg/rQeX6prtIwSw7Z6XKs3N
L5oqUC2OzTAN4H4Rf9z6ofX9N5I6MipL8ZKoli92HcElfbpGq2g02q89QDGVRPJBIlNSuAj1
gOJ5w4uEL196bklpu4n072BVrXqCzHeS8OxQqedqFSkE4ulh/W+Ka/JJdfnuGi6wOKe4yAi7
j7a+UOm/aIJ63o+Iep5LomMRGoYNzQIIg24eC7jK8UTAHFJVz2PP4yVwoMrlRefqefw5TkeI
LigkBsYm/ArT9BZOBq1m1EcNr/cVv/ykUAV3bxEda+HxgmbJi0LFoMmiUElgkMNllD+9f+/u
fGjZK7qbtirbTb8E5e/O8Jkun8u1FDKnU/FySDtEMuk0IiafiD8qHVa0o7AWbmeHjzfNtUJt
U3IsvcmqfWDHtnIn++4D/N7OX1B+Do5yhYjUXP/0I6uF+8A98Xala+LqMi/oOV13ZgttS17k
mrkrpD1ZTivByIyat1+lqrYtxw8OF9S4SLv3rcnQdZ6R6TO++O/V3dr1bM5f77zJoqyhO0Jv
9ylWqWe7VtXYsFopc3Hmoc5Um2k8XsZIvZze44Lrx8ffePatq4VdvM3TDmKBXtWOhhvdnZH2
6GQ+Md3RoSKGeHbWNJB72HkNbwd72vHAJJeSS59h0nEMsm+j6vXs5EbVBrMjBELDN+d8zSIu
SNdXgIPFLCEAKxnEsdj7Ae/Jkz3h1T8YcVs89uE+sNgm1lRYWCcKsyQnFMu8vhiPEqKP8mSz
qPvAKrxqnd1mlgkgcIXX3/C4drkUhlapoqfML6mh36yJ+HT1r8Z48qLv2GVi2JorJHtx9zvX
fb0o6JbEY1vBrQ+J/m6W636YsQ4H7LqI0pXeaQ/TXJR/2hOrjpT4gWb7ULlHaNPCNrtsuZQJ
NLIjhQkf+ONGurK+0A32fjq+Ch0uvXgs/Kl2N3/ClFYGvFjU2vpHLtNWJQba0twKiXHeB4aA
tbVgZUcHcmcqtRHRarBRyW+aX0aMc5DLm5HMmTz3dKJ1gYG0vmvPg81SPsMDSciyPyUJ8TwC
A5oBxEe+q1zQLGkAUs9jKJHlcGBCwuYhlUdVR3jMvjrKNSn/VeQlqBSnrT2fPccWpBtifqQC
FOvAIFeDL9RfB1LFkZwooIGNkKgGm6R8i8Sjj0LeQXfdL0m8OV4FL74kus6xECn4kYfDHDgO
fkyFsyESPMGPRCdYqRyvwVwjhrx1qBx73Fxx8oJtAnW95UKXcuD228c48vxRjexCNavmdwYV
Smr9KeM8zMUr1LlXpniMRSB3rvuEhnPMdHrDvw3R/xOMLozZAuc11qzHZYVs5NQI//0e3MJc
mdqsh0UPKdDse+wLQzVjjojjgsj5KeRHM5tn3wZYIqqEUAap2MTX0h2PjHDtEp2Cgh24jDoV
pwAr4aaJ5AYLrTlZai4e9BtlgTeWYF9dERkNBQxF0++ORUjUAvanAqoj45Ye8n6UTdIIbiEu
EkShvryfoQAkAhwGR6hwmgZFRtia8QFpWe6sFsFLcpy2gMKuseZUG7r5wVd8oOrjGMuSFhUx
FGj+EYIFjAMBxSWB9WP2pxpO2J+w/5ajEBISscShAzqomgM5sLKiCYYOOsfcIwlgIZ/A/49y
GXD3eoksLEHokhz8hGNqIAP+ARWmWOSdTiPoKekyTiEkiUj4zH/C6i9R3M3MXfIa0yyvBLN0
nsYTpli1EzlhDIVDnlf52ZK9Ux1JVWYW+q2JGLM3FXS7xQKMJvH0L0FmLBO818nStdG86OQd
xIc+3lMeGP9AGuDaHKEMgD6biiQNI4fTn2CcWpAxOFZ08jii+0giANQLSgPVkbIAmGAZ7Kv1
Vv6cGvhx68EkxAjsYFAK1MLBkWoDKPJ8eYfqUbISbxQiEA/BgQ4oYWW5QKnKsW3INRMJMYSf
qj9hLwTUGpolSRse5GV/NBH40fyI8THQZwTwRUAS4L7QCODR+2QVElPwAyEefYMU5Mmt1r+Z
bjx5S/opjY7GJdoF37Nq5cI/dWtH1FiHusz0QUr/gBL3gxk5BlutKOsTeZOCnWv7y7DkKQFm
aN6ARdJ+Mbu6wu34yOlGXQw5OjszcV2Q6VKqXrpmKqtA1G4Le1dCzY/Berdha+xuSe44BrYI
AhUtyouveYcMK7jqo+E1WpEq3AlAE7aBtxMjVQ+OH0CjN6He/pvT9Whw2Afe27cA9rUox+kD
7dIWyOEeWanoTtPlGKuQg58EZiIBkMxH0DAGLxuKxnlDOZQXCRLZaVnml0STEIjuU0KSv8iC
VhUR4gUkc87CwJZkC0kUsLUAO7ycNmhiBUJaDevlAQ5PrmZ7zRYOFVIlNk8lrUQ3h6MMbU1D
iKKtjR1NXIar8ooYLjOpue8fQ7s671TeYYhgpMs33iXhy+dNhOqsF9FLiXC3P+AH+VBatr7u
/7TAJMTpifAergr6ZfEGNa/Kbo6BQvdqpXBOiGVYdkvccSm6mZl/WWGHYcaUMpqbLkdV+Xmg
kHa/TyFpw12cAW19xaJf0Jb0F8c6vSc+lKQSQyJlUxYORs+QwBHwPua5OCNssRVEYBQUOsej
OWRDODVuWflDAgJZUN9vwbMJauhAqWbUOxiDViriIzh4UOFWsQXb3PtcuMrRCtiipHEkKKwI
2AYeT+F6ZW3QvwWJ0PLlAnhAOaYLELgAUBAeSxaot+IoPJ3BiQCMDYna46c45M6CpRKgUlk8
l7UgKkcR3TxOmXCshlKz7RbUDpP7BBEpikKjO7zPSY6Ithsy/HfVx+KWYddC+XKu7vxQol7g
07b6ULrp0bcmJNlYa3yldod+2TdVztmpp/0JDVD4H1AV7UWrWqn1WoMevJSUCQH+mH6J72te
klJHHc/3t12PZg53GH1wZHwY9ruMXbU4sjeb+MMPb2ba0D5zDDpi+xt+m6GMweT235tXmg3m
FTFhjhpKDVYWzrC8aEHP4wmShlyEGeCYsaEy0GSsojgaNML70e4TVxMnohtNEASatDlAly13
EjnyBBw91Q02WIF60QSHtOJFztSQiIP+zB0BdmcsOB1tWA96BFVgp19LFMPdp5JET0hkJych
9H5RUayPIGoeqRhRIDzkgUSaBxIq5mE6YNt2MAalwXxkNAc4CswCOznoVQRE5By0G6DihZ2S
FVG2gylfBAV45ByDOowQwKMIrOYyTIQhKOkEdNb574aRLYwZ1uvTpzs751PdGCJDe0pDgwoi
s/3FwqOkvTLLVm3DP57M5s9YS7zpP78PPJ1BJAS40vi7+M9ZlLi0oYaL9JAfPgMs+RL3RgR6
NjuTzy/c/rbENwzBKsfoHN3ZDKT+R9lx2/RGL+Sk7NL8cQLXkrBAXDhbcQzgaLikPE8wNpQX
5TAKgwMwHY4RPt16aO5RqNTbwLv+zcCVVQDQBerlOZ4DUKkGudOS9ryfMmSJ85GVsDP8zlIA
VwRwIOB4QOKQ6HlAdOR4xIG4bMAmSQINoHNPIssYEvFdhDlHQyBEsgLMvRrgag4Ecy8k5SUU
z8NEbuS+BOcchPypc6D4fY/suAVo3gKwSKAJB4ulzFBaA2lHYB8ktPfIIrNybtdpx8KFoz53
TTuXGFu5J2IsHvRlqvhZoVRNmQhQ4P1BUwSgj5xd9WNd/YclKJqWojQKsOTQrl5bNruMbPJp
yucouGWV6ru2MHV/bTllPcqcoXbZleRoGAeVbzjyGTX3sLW6Xt0qn6SJNr+kbpVH0V09ce42
EnXT0cHoKcQBbjKukMBx4TWgbQhkBRs2gz2QowVUgxnwinnwVzuEaBFjLogxIoKLE5xsHCNy
mQcekIpANByNQH2UA0VgGw8Agxg2S6twC/yoF8ExcoRw0DLtTwn2GNYLikGlIF6fTrgkmR+M
QM8A31GNfUiQX4ZzdWVviaJmp0qhx4i4MTVQt4LDUXAAmx4p53lUzR9WudAomJIMq7Ke9Stz
n8l/PlRGOxKBT1V6hqP1EPVuh7qjW3UjpzsdU88GP7cb/6+mwIP6Zs8RJ/wszj0URIXWPXu/
HTXphx6gD6deMG6+w7JWqJEaidJ2TZhGxlQbPbY+fuL4CcUp2fOXkERWqxbGoELdilyoz0DI
ltNJFN1R7Ojp2xpuNMURsWbloGWOkMiQeuAnA09LAFjimj76Pk+eI8M+CDgG41SBHTgL5e9r
gzMuyppBkAjNS6CukXzrVS/0ixfXgS4+0AyEWU4wGNBw4OMKgApFnOExs/9Rm2OLg6MBAL4G
F3M05YHtiyJJdGoxFcr7QsjV9z53tM47yNzs8ZF3jqTa7rZtE0MgSdfAUy/CKUkuxAjZINr+
jQqp9g2vfnkVg12gR6ViHhj6z5TrMhA2pHwqZpwYaJYe1UMhZsc4pBAavImnBc45y/9RswPj
zzSghVCWQkLvHIymXMuV4u2o2YjoHTXvRIUpYAv1W7F/RntKYbsaxnWFsas4XiZpsx6vyphd
NO4vWmGIWvZ7YFCWtNGoUI2ZDOoldROvLpAxT0m3MM/d8ZOQwLuNaDOF5AN/j7LZWMrSw+un
MbaeqaBnrfw5WqgjOlKscc5ns2akQ5EYZH7pvKmJrYWn3dCK7MKGcIM9jx/XLExriateDuKo
E5kIaGBfy80Hgk4P2DSomD/yRXhD//IDveP1fFm+HYZcoIEMzkH+tZ8j9AybQCsdyJAEHXxU
4zB5zrSeseoose6wa0ZxQ4VBDpw/q6Ex2lPSDgf2pmDC2SzRWUV7foGLMCNkPWDe7PldcsTP
6NCpCK3ZOqT19TLzXtsVwigfWUKWtRVT9qQdQWN00vr1IHMza6ArrMpE0EQvf+8NH4FARAiC
Su6/PDin3hlNzdXIfL7Gdrzg4hKdUdqkLxnzcAS3C6O6qs2332lewXzYB0I/XFrxE5eiljjt
kU3QvmZjv5meLC+oXsAgTezIcd9xu9XYqXlnehvVphVjFIzeKNIkYz7IKpvY3m1oW4NdWeYi
RIoZChxPsrxq0jr2xEe6U4yeVyWTOHJOkzHAvHQx/pYfZSHJSZxsR4q4jdq2aq1Yr0fGTGeg
G7aNnjoE2YP6GrgEcGwbQTyPRmgErkADss7Q4RVJ5hyRcaABVmvPgW04JQ1wbEW+hxuCNmlc
L9jt9UYe+Q9YiOcAGbXD5rTXQjOqa8Rborty+RPGR5o8BjKsEu1fOU74dORvEFIW4bd4NiMz
RgCFj4YCAtYpo18lmceEQOSwWYjU1zyKVMEMON0mG0f2ZojYFobzIpJ8P32+FrsqRKZSZZid
TUV31rgLiB/76PQqd0K29lgcLT2KmOpCRJjb/8PSsz+qB8jbV5+Cz9mZN+5KVdOuYU9YfsHV
cGWnpK67l1dZdaXm3u1OPGf5pgb+mZpW6WFnHKYYvsGt6kwpc4iO8aDbgYt9mhui3vSUD3qB
PUf/J6NO1KwTifdxr0UgzOsmQXlJGc8xfuqr2YZme9sYD1Nj2xgqh5yR91cPMXmxQhG3Tykm
oM2DTa7U+Z9l0qrFTLM3pjah8gzbhIf69sVkcoFqlDxjHxjbvLurrN25zMW2DftuI1KcZKBk
2Kpms41egM6crA6tr/uuTM9p4PharN240MzJKlrFqb+8CvX2zWR6ni0qGz0+x1wHQ13yzB/P
zMoa8ESuZe6EC1i8oI1vRq6l7gNKsme7lP1fCPUO7AxDfnIfyGzUr0exV9fHTZG6gXdpyXDy
dovYRmRyvWSDJiQJSQcgJ2CGHUBHSESLRP2ji+fEBDVqZV8wBk641quQFrQbDNXwswuM2fnr
pAm7/DjCbHHx4lDyc7v24R3/TVo5/hjLt0/iGj7ArRNVwbTQWk3ypaNUmxTiwHUcf+rgs7vc
9hE3irV8QbkR1IFAMiMC+4q+UXdrY7yg+lhgflnaULq0wpKOZTLPSqnNqgk3f5dusbd9zIwL
H/9bDtnn+m817iHgugM9034dm/YO4YG4ddoJPpKaNYMBLqDp1BzlGa1IupIn5ggJeHM8kyDG
1aK8dPByy0oWDIj4AMVt38KPUQVoEIyese22YYug7r2rGSswI2+YPc8m4RaapglN0AVocFl8
JDhTyAkZ53TKun8G0PYWFmgBAFCs6BbX80yayNkLBROEMEli0EDj1Iq7qKsiGjl5KqmjkMKq
broYKS/yRLv2c3AhXddnEnaVdgzbx7er/z4mNxjj7U6byJ2lL07J1uhoX7dxGciOccldoYsm
LvCCA27Cn+Z4ABtROHhKYYBqomalpxhXr9vulCMhcb1p8tdUxZ1uz2QFaZN94JtzOQm0PnRn
X9rD5GsP3wY74M1y9oHyXEtzP4qu0ydPr46PNUSyD4ZY44jNYOke0T7P1AGfH29HDHlBmMlF
m9yMEbzuUmPOAj38U3nK+8BBr1hSNvI+nh554nj18ZoBnrtT1ZEnFBePUKGyKfOy4zwxVCjc
KUvZGDmqOImPrKn/5oyVyleZgeQTX6XHeEBqIk+esabZ27Kg+nAPe567TnnKoDrAE5wafnLi
kDNBdnHKGWlUmnM4XlRAcsgFTsGbbtmI2DaLwYpu1thMkHCFhd1Nt8xQBSlF3aHVVxNlCjCV
XHjx0GhiWUyh1Zziok/i+2cL/N+kWVsliDWfX4PZ/6lG+fdEKlQcoy/AvZ9YwbR2hEzidk99
Sq1m3IhJVcxsNDt6zexZ+Ee8S9u0f3x/aH5RnMjp+4s5tQ9nfFStXC3Nw642PE744Vn501+9
yJ83mJsL44RSt2CkThmmSo8UZ9EQRYx3qxy7Z6kAttQ1i1GYl7/2pYsxbx0qFo7XjP7l733y
AV6JIXhV/a2jeaeCG9BDkTyR1cczdIEhrqGEIOEhgaF64tql2HRINczEblpgaF6h+quaPsOh
Wc7e0YNghr1HYGTNKGxD0CqQd95HYEhEo35YYHiZc5hzeFlEbjxAMG6IAMvvbuiYECPlTwg3
3ZJgTpfH7wMlTgyz4EfNg5JG/Vh7s2NlGBJVr7YthAtv4+t/3qrKfVC1GYcVBBfg2Q8KCooS
Gjgi/g7tT4eOIoREk7mVwSUbg9bmNzuvknX3Cs+O8F/cB34LFp9fvEqciN4Hmm98hTPLDPhY
c/tVRyxu0T+2FKSaxt9lp7FbU9XdfO3c2IKm1lxVaWndTkFaHmWMmvlJlF4233xsbjCDYdy8
YNTpYedYwS5reCGR321pEAvvuGDMgll6QxymbO8uRsm/4t0HBOzA/xfo0YMmnKTxNiBiKEKj
2jAmqnEIGlx9dxGku244LDwEDfw2nEDcvL8kMeLR7IkCP6Ox6Zkk9xq1pPFWYzsmbVMQJMqZ
1illdO9aDDbBXpSOn5hpymAEaIdecwyDz5W88X+5g7LudMycTKe9f9Ag1aMnVSIkgnPv9Q9x
ElxITDbLwZrlgrrPkaHa/Iu9zTToxDWF/wnF90fEIdkLsWbhi6XlZNpk9hnp0H3ARF1kD/kb
MSa3QAhx7tKXqmnTxL3em/klUzrD1J+0yGsGuP5Mdmi+Y8U+8Ltxw84xVczr0DNlrY2xn3Yo
iO108XMl5fOhCy3dDlqgd0gGGmXOPFZw+cKVGg/W9WR4azyZmCFdnr7+O2zWr5w0Yfu9UTrO
Zecjz+iOhQJX7Mfjcw5GoR6ECwXLXKwk7lcJI7VvdCLn4PxXpUZO9QRGzp2ukC7RM2QlcQ5M
c78izHIXLHOyHg7wX+EuSBjJqKq+ix8W0PNw4WQNwTPqGkQ7snWijjLoQvHTNPs7lMsllprF
L6tuhD+TqdAumLcrCJbotsQZpBbqj/j1rTk67QOPXpFC5OOOLRS/LndL0M8+l8Fa3n07iKqU
J8TIE5rByY0/ovjn4zlTHfIaLYWkXkj2+jt21G30SYg41VS0aCnjL7xW9vlcnu1UgFTd6/pJ
a25NB4teP23psTaUOVsar8YWIe4DZi64vNVBMlvYuegj87aBTzmSPb/zIl+ctHbdw3JdrfL7
nY0c9iXTynLuF77eZcSi1gWDQE2V549mpHTXb6HZ7p0G3V96hF70l4bWPAz/XGVQmi4+tdOa
SHnjV7wPLJPCneFNfuIxYT2xaGl/3JaABZEhg2vvC2G2CXzXp74PCLcFvYXu0FAZGi4bSQZt
awM1fvor3FsZabuzoeP8q0oa22vBLVZgAsnFzkX4ZTo9vMZshxAX3q5Kb2UhmbKv3I6jvYiv
toxgXqTCWuErNZgZinWU/HO/cKzjnFPzNGOHoG5F7GPtxj/JX++s2o66rXPOg6Grftu6edUu
Z9LTPaeTWeXDtCJS2IXme51nuU3qTPxYoesfyyxmsnG7S4IMj06Ubuhe+S7t/E8/aRfgdd64
rdLbab3Wrefe9MSaOSCcfsAlKtpLZMtqgs7sP19rfyrlmQYLzWgY0rFttQz8xQMrwsISu5sW
vhyhZ5K5Dk46xHGw024yLffB5Xqx/mNPhJtfnxKU/MefS/ypQg4THRI4JHBI4JDAIYFDAocE
DgkcEjgkcEjgkMAhgUMChwT+byTAvf95f//FD5zAP+2WerD9LviDmP+P7ZZ6vII/6592SwUX
ggJQgAPcL/Xf0R85egzGzQHl4jzYTRX/l/1SOTgBriP8vCeOc3Lx/m031SNHBU8IfYUoE9Y0
svQKiHwoIgs+3uOnn33v/fpbccnbd2Knkd94+/g/eZr9nt59UvSMlQ3mioPf3Uc5L16+KW3o
PPW1qsa31s5RxK5xs0vYx8Ympuhbjr/c/yKnNnZWXuH2khNYtvA/fKl/+3YHsYJ//6p/i/2n
HVbLVP79Vg4DhwQOCRwSOCRwSOCQwCGBQwKHBA4JHBI4JHBI4JDAIYFDAocEDgkcEjgkcEjg
kMAhgUMChwQOCRwSOCRwSOCQwCGBQwKHBA4JHBI4JHBI4JDAIYFDAocEDgkcEjgkcEjgkMAh
gUMChwQOCRwS+N9BwGof0McnWkrYtrkHB/OB++68cjsWYuy2+dkn3yoX/WB0honUDD+HXuR/
v7Sjz2rY0sfWc+K3znWDz5CrpmbsA7wVBkPcv98gDu9OtG1sur3dW9L/ngXugrSo7FT33p1/
I3IFk0/ZB4J89PYkPMOr+X+tQdVtf0hZXOqP2h0JeTLrBj5owJYWfn9AZpEbRm3z0Oyh8F7/
flFq84Mp1fTWDMPliXv8TxdnPsTs2H5K09d4H1sr07opVX3h+O/9FVq0/5mCoeNFVh57K5PB
O+oj+0CgDvlRqFW+km3zfFrw/Q3xi/6s9u8Z4rs6rX7aa62+VJIeGn3j1c5C2kOc4rKPFHlp
RzRhd/KM8p3/HdVzmOcfE4CFash0KjD0dorYYUZZf+4piH+c2+GVf4XA/7k6kKkPC658+hz7
IdxAfHh2gS4TZrS6opFBe7+oFVxiWtxPG0MyrTZmuVs+jMkc8d3bKxol0pqYU8t9k0pStdpv
l1a1MibIFuS3tEmJ+4F05o3BCmGLwUr+D7qfvYsFkbofPIt+Z3ooaYff556kdpxSPFnrmqIs
bjEbYCp1Ez9iILLgH2TavFWL9edZZ6Pc28On26Kmbvks/t50IVysTbmLTFmrTi0MzzGPmrjt
JzmeKVQXP7aQiPGYuXKVEv6xBL6FwWetKDnWcdRqWyJ3iQOMucQEhCPky1beDrhX402DHeSr
8DPc2bX5O3H0yTEl9m57GWlP1z4s+LmNlkzOZCD5+c1Z/8mczXlDA7WOVyGPOld1v+lRDsv1
cNzT8eT/PYAc/vX6HtZv4Vxd/seLBpKGBlJDRdXp/VvxFgF2u6b3MOCT5TYXWHETfMNtV4Yx
4ZbZ/TsBWTIJi1cLrdx2moZH9Ya7nTfrEhUhW8p+eRPXopmXm0ef0MiXn+Tu6X7ifjDJWCne
NVzGrJMv79ly/1/5jtOPNOHgRFnlaryyLZIbrsw9Xdbz4IlEpkbpZooH65rpqdG2pLAPdre2
LlFX8TcF3MLIpsWbb87IvOm9csOiMGRwcM6Vde1rg5j5KFbf7PLvBbS0Xg10HcNZw0C4xcCu
sCDkqe1WwVRR/67N8O871i0G6Fryzq+YVdtLDLc9svtU2Lmf+DvN0DfMXLcKz09asgso+WHn
TvB3epCcZFk0XAXdf5hBdsMNx4obMXe6w8C98ooy98R6DH6FfnYicctuiQQKe3UNWKxvB9hk
62sX28tYSeQNn9kKrcbI+OKC9wHUuzbK3pNk7u7mqbFHcRlDF5LtXkrtA8RbGI9dRXsZU5pO
SPbwVgJWXTiAHerYLjNjDl3vnxJ6vF2HbEvkxbKuZ/Jl1nnKEDPubGEKk0laT77cdFnfSHgu
tIwaCX7lY/UBhgq7IJG8d8quMPwH0yX6bGbMBej8qBf97rUHHj96xWLHN1YDn7+PvhkeM6Lf
pCFQzufkYbkYXxdel9Y464/bZkBnrvb66iZu6ZdEBdR13bLEDIG4A5QGc9+XeafOrM9kLPHD
/xWJ9H/gM1KY5svOmhIf7j9csYrV2eD+vs5/YKCRrkRL7L441r4F7k46R9LZ0tUiZMuFXcvj
ur56tkcoZnuPvB0cIY66zm28RNT/fryxOv6mXGIM+Uqn3k6xxQPMr3LKZk8hGto3V081SDtQ
w7r9LivMlZfFN5ZvcDFlfUJQJ4tuOWzGatzpxcsTiK6L/hPSwlZSo4NIvdklUlLyv4iBRhxj
f62dW/dkH7BoUT35L+by338Mygg/d+pkJv85OUZqaNWTRsSG0ZKa/tdLY8ZEHLiFafmSbKbu
BK5cyTi07Ee+r5+0m53X1MAVp7R5HJ8H97gsGBhkh6qZvdUIjhp3XM1pteFEYbYSvkxYynT5
7QQPT6Pho6l1lkPfrV1KaQfFrs/bVXYit8aFJXXcAv+DcJLH6ZM5NbWqdjUs+f5rpeEv44FN
/AOboR9eZztJBLrz7A016Q//nlu3eSlL0sqggFtRM6DaRr971NHPgH7eRdTSYrOt0mkBOjHh
VzRRnrCX/aXoxML2DQ1+juGhD3ky0J/mgt5VWRrIaspUrjh9Yl3+LR5b17dpPyYm5YOYqbJ2
WHnvPVHXxfAJahSxqBKM0qtVCRnIoGozvPRzJkqOdW9La/j1+iw6/MQfmceqHq35lPlQV7Av
kD6PzzWQ2wc8ypYgTUWsV5Nh5BLNAd0vflVhjWozfff8zN6LFQ+Pco+0zOm139vMFCnXdE0c
Zt94mKJX269stOzDrvOJTxESZSd8fLs4/+ljdnD4L4VZXukLJN2V2wNL815REsf0f20CH8Rq
0IRlGPjK3N0HrIaCVgyMxwo+retbebiohufEAjuPWbCpXE+Muudmf8WKa+bZqAe5DnSD0fl6
vSerR7sxPmZr6jtj+saYfeDHsjSP0WVVQ907C3wvt2qmJK5N4nbQuxdO3ySdHU0Ksu1ip07S
v9jRqRl15ttqVwdEjHfrA6994bccbJTJvLOgN7RUN1c6+7TWQEKFX3FLcWrRy2zN4yhl0hw9
xXL3QwwPLlPsZT7oqWmN/L6F0+TPPJBuOLafzMwtQwO32mfpLNvcd7mRfsbhblTVGKfR9Kyw
9MtPdlZv9Y4MjUzEXWG7Vj37Pnl3EvUTf1V0l076fMaQzh236sv7AL1sW6ifqQsPDQlLCBm6
wRy7qP51Yq8a+dFefAr3Ylnng9TtTA3qpiso/2udRhuSwlLx53ws0Qhk7SbGfNuKNKu3N3lE
r0dbwUcPHfqm4sG7bd9gf5bUN9TN3GP6m/pNF4wzNDH9jOqbn3pq6kQ8Lk4NUy7pEw2M+c6g
9wHFsdo+CnvoUVhdnS10o2/ar5K0K5P8XC6x2+3Dk9AdAvcc5WOvTWZn0JOGXJbO9/n7wJ2I
sNhQnkKUQcaqEQq0ed5sN7N3oLRVnnAmuFP53XDWyPrnaad4833A2EfHv2KP7tgoE65ttHbe
V7uvdB9oDYpmuO6aDlDMhluSwubs+Df9ZHKWp7x62fGyjQZhVLDATqFfHrI1xDf8bua/a8pd
vmSAkjqh+bVMtteDEDQ77crDHcmoYTPjWo7m9mWncAuqpuXOEb3SNdTErL5HjK1xpvc6T3hJ
VL+F8Z5tHaph4YwF9VGkzHzWakKMZHmw7vejttspyTK/QyakhIOc1wMfNgzvBVvsXeKf97Wc
SPs8qiFUt7VrsCVqUJf88sNZVuNoOPN+5k4cf9tPE4nsUa9v199b7JlyTyp4N+96af62/XPu
PnAauipMvbVXUW2x+5q+DzyM2tqK0X2zLWk6GrAPGBwk4F7By690znvJRNftrGfuJEkjO799
WoeN1v1hH5hSAZXsO/zZlS/sG3JecnoDr/jHs5bI2QHgPu0vRxMFsYN1UQbz9SxGJzJCaFXS
ZpQnuOyLxRKw1tt5NvIRW+ZUwEBw6Rfa0o/8NJ9sDVjumjLSQzscHR9r8BDY6dX+yrM83Ggs
YTaXdc1f7WYCaIat6X16EhbZvItPZEyDmrHXXub+PvBtKEfRlsZF8Xsy5L41zMabLJm7tfet
UXbMVSO06jb6TuHqXh2wF/Zz4m5e3ZLFXrU0+TnPimy49qT/oOVueVtqeP8L6djnvGWE3eMp
5tp16NLZxHUq93jVxzl/s2nJBheRvSL3wdzFW5cMePcIkt/l1uVXMMsLw6gvb1lukJJCqjOi
JT1y6vI23xaDsk19yK6uxj0rJC4hxradjrlzWXbp3YT+YPu3P2aHyb/Pk06ZJrfrGrd5DInQ
uuMxlnvfHNz6PqDWHdIx9+U5rXt2qy6RD7JZtOY+Odo7jU+or2HHO+6Ev0wEtoLsvgpqaV4c
LQ3NfdTPtqkyDtjGu3A3ts9817F+IVzwPa8OkrIW35zbHE6puaQfMGnr83kXa7CsnrjzSiZ1
0Tws6M7OMIe3E0t74Rlm6PekMDw+aLU9B63hFShTcR4tQ2zs9pILDwozYu757f3WH2bwW0VA
Y6ygxe4PZ2XrYhttk/B1yQkv+lA0EaybjwwOu1eQWMCQkRJU4Q+I7J6yYOrzq4oOVg+h3hrq
qXkovxRH06QeVmw9LFHdB3ouqv2e+yVm6rVeHc2sW8Otee2mYEVBonDQrl18WO3QYjwFzjKz
TAhcS8uQXZRkkTEKq52PiD+jMe9FPqVwM8sY0IxYRF+Ctm0mgzkoW1cXC9/dlEJrjb0vetcy
OinnG6q0SyEah8c2E41+V8HXrcZGC4qJ36e1M3cNviUs7vFVGq0XsztWf3aUVXYrlLjJpqjG
VSyuUz35Bz0KnFS97JABD3bOkxIdFehq4o5hMjY0D4Lkg8tzPk3nLGW+rkCUeDt9ZqnboBP2
ATe0/bhojdeGlKB04cQHVJU+LWZgQ2l3Bxe55jyXZm1s0oEZdfqcGlDkQZ0FQpnIwpONVYIr
ThHi6+e39V/2nh/333a1efs7Qvvzyq6tGXkT3XAOOb+ZFojR32UbrTFZ5An3vESx15q55rTM
8me55mZbAaPcX3Wx362E5hlftmPOEDdWm2yiRfz3AS7/197ml8m2SeMNqAX5WdGa3dh+nx8z
hl0cs0J1w/JsY8cxqMrACZQIZjxRjKKGk9Xryz1VGmI/oe1kEJKG6xRxWD1aJr9UPZRfc0Pj
i0vuay2YhqZt3oQxqvBWhYtF+ExazrFhNgYuc9N88vozJdxUdOfmPvA+ZDvDAyrhN2KXGZP2
hu967mL8E7Ix+qUHr9DFs+2a7Hvk53s9+dyfyvCM2RAdDWeqBQVlidiATP73hs7/2ymgZPDR
jxtQqlfnGHq0Z7e+y8OOooHw7TvbPDWxLfMc2zk0YTlcigrNJiyuMIyDjDC6LawHo8Qdls3A
BKgh9uzXrm13rlxXlm9hLHYy6dLXNQfHqs2txhQTz9C9U7gtPU8nXcZRyxljoXNPkWuhp2yo
ly/bMAcp7u0Dfbglp6ar2bUbK0TnjLXecQomqs/9p6O328zMM3iX+B9JbVesF8R/67u4e+64
kH5BuCVVNbDK5s0r9JOTiOnMU7hEIdTMymaAjnlzXHKS140H2z1NyiujiXxFt3o1yvSQFj3F
r9qtRho1e92v1libpco5KTdYUPr0sq57/muQkTMVe9GX8xcnwukrvOBj0P4HD4MnaJRwux9D
mC4dlMIU4H9A9hiMz7JUm6uifUPPz6Vp4ePTEDJu1tBfJn2utu5lek+kD2ErfsYx85l2lRR3
7gegHWERv7gBafJLCN7S/ThDqh76ed2tJZc2qzuMpr096ZCf5NlWmLcTh0VZN0vIsazbGhoL
qGSLcO9QVF+YilcBlpwrh7+thr5XsaFegJjM5TeqMadRx6qvaPpbXKvFMDct49/vyd9ITiGk
lg7qxzjN7gMf5MJGNIeKexZ/eepC8uU7ujDfWveDWErFp079+U4NHeiDcb+2whBFLy0Hom7d
OXT7xHB16JU4mSY+HbJf3ajSLC7+eES/z4miro4bReFypwdjnCkDkjrnCjCqAbii7qrj99bl
U7ZusB1/s7OUsQm93hcGD5GyeGWmsbXW5tDUTHcMocdmY6ybN6+XRT1wZKGm0pRZmPPLTzu+
FgnSRcdTXqJUtx/dUEOHfgwhsaN9OqnK7ESZeDZzm7FVMDIT6D+X6X3+UzRH4TmWzBCa/vBe
VcXus+EPMrKzDDcrAy4CEajKYan0uBBa6EGpbdlU5hCzIKzSaTAloR7TeupHqS2zHdd3C2em
6D408Vq0//Z28UNv/Wm9zUEEdeIDgdTL4a2wuIu80cUErYBHwHalwfd8/iz9oYIvTU9ebIWz
HUffkimbEhTIB0+8mo/bM0ENlrv0F/PtU6z0aOYev3hW6B33mBBar3cmepn73noBrR0lngCS
WMLHyIapeNcgs/mFlBtCUsYKPzVmOiJKq2N3a/tIkI1ltrgTWnC21vHV9UynxvmtosXJLv6S
l76a/T24fSBhK6Hbe2ZxsrFfGEvzWHzjDn0ysvb9CKoi8Vfb68PPpj6nCT5w2j2nFjV3bTq3
dc1qa0Og4qX1tu/sNT/EhucLmfDvp+da+TIFxfwWn1tQMrzLKhUW9461A+OfQuWpp5sIsQOq
3SvbwRqUkyEB2z+URs1cn/FoKahI2BFIndRLpSgXbb6pgia5PNfZUupyOH3q2S5HHXf7bNpn
LYN7VRhP7/OXf9D67h0hVrdiab1wmO4rGVw3Q4ezbba+n7gxqM+rW+b5BrvtlpnLMJDs4+6j
a0Lr40/KqoYdu3P+SG77rBvlgSulrz/CW1fvSYnvJqG+75q6qllaw8i1HErjJf2X6ea24Vv6
amS72l8JuYvQ/+Kxx3/Us6GdwdzcZ+tIKvN2i1NLzEa7PZWQVzXxb8qOJNM+s+XMLTKbXdZd
F5e7+HTyPaER7DZz3I7Qp6udmEyGjgffYng5Bb7JWHnWWtMaIk7Ffblltl5lYBG9OdpiAMPI
Sb6caGgcstUMALXO9XDxYbaqoT4shz73SOknuYtBof3WoDFKbpwPfzuQ+1pzYuFZeuzNQvIT
z4upOPKMhlyRuRlV8EmfPjyMJ+OJbuLN6Fjbs+3Ni/P9A6mP17ddV/ij8tbuj/eryyFK3Xpz
N9a9QC8Uc+9E6tumi9rnVwrwExglD3f5T9GrlqbkSNXm/p/Ndz+G7GRE71AxQrP6csuyBwPN
sxxTQ40vJIOtpqPenys2+Gpzhrp8MGR9lhhO6WMYarYvgCYn+rIBclV472nq+s2gTUdkziJ0
0tFXc8DXmB2VPKi+ti0YfMe2bOMNjluUUXnGq7YNvXI8dltCOfwHMf9VRNV2LW/V88jmhbUr
k8RBfRGJ4XsUpxlnht+RzKp7Avzxeb5+k9t8cl7kT59XpZv0KbYglKOOSV5KZi9v6l7RCPl/
qHvzuKau9H8ca5VWBYoIVBRwYAoVBGQHgdBWFqsEpBD2gAUNECQsgYQdLbWyCNEqAmHTUAMk
EEQIIQSIyL4EjCGAIWEPyJKEHcLmL7bTGefz+3zm1XZmvq8Z/uHAPfck97nnnvfzvJ/3c663
8cdn1w4lYv1gQD10YtsoJmEMYO9qNxK12Ogh+EBfvWnvfvlslv9Gjp6U1Iz7nExlyVuxtNrg
Vi+NYGHR1x1UOIn86YY6f18QcO7aT04jbVL6URGMabTW/PoE4FQUvRVWtA2oq5iG8S0n1pf7
Os+tBVW3NyWo7dvNeBy3yktr/KlrEjbWTnHYVUrISQEnHvGu1JN6nM5ULbgT8wZHMGLEoP3r
6cjgWX3Z+K+zW1O2H3G3XF33wiK2fPVW1hOKdWfyyiVP54j8GrDYlNw5BhwEKTw43TUeL9wK
QtvHOQjgvvs6V2Ekc79KoCVN/KARLNgHm2deVuZWCG/GCa6E53mTPURvwcCTA9oogB4Wh+mJ
oty+bCqXNigT4MPboYevlF0RxjVi2EbPqIzKgJPUw+UobeTplP4ov5ZY2Vhd/xMfLMSz0V92
GCQ8Yz+BIs2PcE4kx9gheePTAZtrthRhL7Bz+8a0m6IL+U89WI2OiR+KkvQXfIbR3/ckJlVd
Nj14r7/qRwmYIKV5svdAHXXH+37JBGN9sHIWVScZWPyOeim2c03vQUp9LqKty4I219UnyKBT
U+cc9LwoQRsNDo/DBLfPpY8a30ypCw0BLTkhrp5kOLApcBes5ivirrEeup6ByoRNObB6kv7P
d0j/X0/vv+P/+/FR3J7R/cJw+qTLxMje81faHExQK6M0p6Ewi8sTDhgq8kGK21aDrM+Lqd0g
ae4BMFx1QD3VU8D0hGdxpITf04MEtp1xHaR7+JHiTi4W4NFrHCWQObbZVdRpwMZ+yaj/eEod
3QiLTB5F9wISMjFzG6c7uzjDNWuz5Fygo9Vmt8HgyJ4XTWYEvfNwbjEW2HVVDtXtA9T2io5Z
U6LkiKIqY0+K8nPycpB3FbAbod2eBJAz0nnILGA6jTs5byIDcwoGzT5w358Shrzm2FJwTABQ
8iIEFMPfKPyAGm8vSOloJ/SDlF3MAW/FxE7LPJFcp1ab0llbwfrWJtt4+/5qOzQOT4L6K5Wh
zWLhxmHBTsNz3239MUvvKwS2r16MdEjU3Cu8G3DmZGLMeMjCrgaz4CQ/mPp4zvEe0DXcsEFy
He+LV5Lwlj3GqspKAxnSnKxa4eG+KuiipsJDancXX5uYWz1nCIYnALPDaH6ka72mfDXw4F4m
NM37SFy5iwByDRgZBZ55kTqbwZAeE5p1hP/TG3OKT/YNGKRrpFBw0OyoCCsk+pkOA6Y6jrty
UsZj2iELTL5nkpuEijvH0GmPXnKPLTpIS3Cw7GIi/nzyvOcM/j7vg1SCP1zmGaEVkOgI1c2x
/NBtcTpBLPR6b2leuq+1t86dwXBocX2UEWIEz91QKwtI2Wx6QRJ3a7y8Gsgrdh/1EGSR4i2t
SbbNu9IxL00eFg90Z3U7g84ZH9q8nek666cxIGnuQDGY8uIt7b85Fx/+VGuUkH7iYV7aeuLX
SE0EA1rxQ2roHGp0f2pQfMhmWkJqESz0BOzKoKW+aV3DTgkK8TlmMPHOSXWdcnVDd2mQybb+
DyZ0QCDpiT/IOb7majtbXHJwi7jypMyqLb++WuIwFR2xS033CdnzzX00QY6/KJweUNOdm8TG
DYbHKQS20iOGDe22HSeWJhJOxeAmpRwbT7nau+TXRy0VykYHCqXO5eM0BGu6GLT/hPh6Oaq/
EMm+Y8ej9nhHgFGA+AaoVk+8hwBRPHk3MXh1eaYC4b2W4PohcSd3w3wjUtFJktm5AdndLLyj
DL8w69h38ElsKyQUL36xqFPIh0wycMUTVTF1jWOmNYX0olw7lkpZPvx2lIzlk44BPYjfjpLh
ZclLmFW76Q9240nyslHxSbaJANlostMwm9Ba0SgZmPRy2INsZ1/cUyBn4d3jxsocSd6+Xrev
08D+tuclpcTdn6aVXXsz9q4rUoJkOnd3tx9Nu1nICENJdnE/TvgfDemrMtJ7qmXLaS07ibJ6
M9pllGmxskJar+IKhs08qhyahK1pV6ZNwBrRSq3Y09QXcexOFGRvqh/jz9N5JXm+KII9df9L
fHPTmFoWInZjL70fXqU6QU2oFddtmup7QANkY9u1dkwJqlsJnNYGS8WuPyvHXuRWZYEPCVAv
N8Wb088JCptbWLVG0M1Zoti0R0I/iwXUtcmsqS47F7hiA1CkhCkHfSJVCjRgSAN1paVFycJH
f+xR/kdnSc0Udp4SCinwEGgE7dzDpOJrLcKJPS15lQQT8U8GomPHlCZz8pubJG7ikAUrczTi
rcTu3V2yeFPX1HbmyS5Ibn3NYm924ayn56H+vWX2/rQgCwvh2cFAXN6ID4JTgu+bM6WmWH74
mmx7JSx294xQvsE2KeS7wesODE92XXWf4BlkX7sh7J5Xzpwz89PYWPisEyCwZZDA1OVHvamV
VL1Hd83sLpB1295ONYL411vNxcQ7M9bMYtKoHHElZoxqKGRNX0H5OBL7mXcLd9L3qlXcMXpI
rQnC57wZHBx5ZcUUZIAUXtReEBzyBZQ75iru9Z+MBb2JbVxg6GPC3op92Y0fulMuuW7u0Awc
zr/ZrB+jAbeA8hIeT4gfCdey2ikbLJkZJlQgCh17bIf3o6ANikIqoxRdaZmdbu9Hs1cjgfUt
x4MvS8rmvBouuH4pk2F7IKATk7LsVVW7Wpra0JGXjZ+8ETcXLTvT9+2gi0tWE2fyZrh5lfe9
QigXbrkXHAP5gkTaesjrOzSgndlDkJArru61aECgVdk4VGbhd1/uFGXkW9dGj/v0I/tOLPrm
CJznHUu8sRajICfn/ZyU/vYCsP5KblxkT04RF6JnANRbbdn1OZ6uJ+n4aA0642CbnH4+JuDc
TIj5DG/Hw+yt2PIqS1yndd6aBrGQBnIeN5/MQTHAr+CiCa1/+gZcS6p8Rlb3DdZYff86Nt5x
xSmp5OqE1fY9n3TeUoepi7IX9SEm//xDn8wcYcyCQOqMbT82tJ4aLDajYOuZ8LE3JmdwU5QO
mds1+JbT0pm8oUZ5uL3zBVfB1Z3vHHl4yd/4epiqHTZuIzwi7+Ib1KI7iLn9El5ujBv8s2m/
tbv55f4IYaGFqRn8Ms5vRxY9drLqizmdTntuAQupXH0J4D269IO2t9RWK3of7ayQwnU6l41r
1/PSRR2myRt7S9Q1avBbknID8i6Nt01jcnNDkk+EuGCoOXhxUGWCOhutcTf8nCaGqwuuw+D8
aboWE19O/aOn4t94bD++drKn70NTOL3IVeSjMFZjswLQSxFb0NzXwvhi0oxJP5LshcxOwZNu
OkQt4pKXvyMI783LtiquzOWTu6dv7bx4w9wommqLNFo2jO0XmlczlgfCKO23ZKQnoStAQ8ap
2YIPlxVp/sboVrMVl/Z+A5q8K+HOnfJRSog3uiogGxN3DR0kSNSGpFIYXrapheJNudUdWice
NuawyeEbcxaxl+nUXNooasxLqF/hjqW46Ni+c1LU3zkpdFknkLceT1+fNXPl0mUxseOzbJAn
t6/E3sXbTiQuuL73eVsI1L8p1aCjX4UH4Br6gRQnWSUKfzAR+a9Sp+ybb0hoMyRT7sVwcKp9
oEhrXeUjSbdggHOLtv6gMT5fdyH+KGGXAjW7LaMQu+1T4HUjNB5eALhcs1ZHmFmRrSQwHB76
iYOKjBI+qhzv2RGb553HJapGOTONopoTjepi22+iSIb2K5bfBLVjczabnkf2Vp3EzrrL+Dm8
rE0pY7BivZtf6ZaQ9izVOD4N4h+xLWCbwHRYKSvvKKcuvUOIjjyycP3zQkTwJn/0WNJ3cxbh
kfiaaYMMz7OV+HWNTk7kaPLm6ZYiQdIN6G5Q9I8dHYQI+5Oho4eV/LiBHS29HWSHjaVMa/31
R+NmaXiSaQynroQRuVvxCOgNXeUdZMIdyHM5FOWTF0wgrt94R28ciBhPbH74BNxdNcawkUsr
dieUrhe1TDIsdp/HTCYrXtjgdPYyNuTPsjKN/UQhrsbAaaLu2ueV0ratYkt7SALm5DeplWvp
N9uC7dF7LjjkAfeaQDxn7ZpzS9L6txFNM1lmz9EmJ0QvtrazYiaGBrrsfLo+rdG52DgTCqfJ
F1GNt57UBfXm3yvqEb6hDczj/DhLcgRbjrgO/ZzayuF7sTWTE1lSZ88IAZ6H+DBQYpC3Rcn2
oxkTC4lIzwdWc3Hdvm4VpIdngjUqbNtdrilHnWR88ebWC3bM6XR6uyKzxFXZ0EQBATjpQJal
8UdPJmXN7sqR3Vsp1gu02ZaeoeLpclfcFTqMinzektqocbN3lXCffT9w1do0zoy5ZoqycPdM
M8opXHT9/EZ4gxR29M+5MQuc5+/gvVSklaSzMhDBlkEJu2Eb+2iLZHPueQfM55XdIRIayRmj
hbw4M8YSm6Qn6fNoEf69p0tqMC9BliehlAqA5ElIySupslM/z3jORehWLpUsRQ1osTCWl6x1
7eIuSwX8Gxeb/zm0FGjn+nWcube9Bb5/V6tLRWTcCdaM+OYl8hvcCHccQWeWVkyX9tJ1K1q2
GxWPSv4pq0tcw706Sp58fTxTd5g0Y+Z6qH8nwjNFXGKwLiLcqXZ75+6YZIp//cbeja7uprdi
rg1fmBAevyq8t8OC5MFkZ8bshLh2dsydnsTvRRnRpHnF49HA/orNBa3EZBYQ4NNbaXjHQxT0
K6aFV9RJ6uAjvh4Dz2mkH07LFUhSfcNnm0U44pvrsr1zZew1R0KL1p05W9/DBJILH5AS/Ted
pNeCio3Mdsv2pwRxPtnEo6ydakxGiYaHJqf9LB06m1M2IKgTwxN3Q+tH0nYGfemGbpw4/Z7s
Xa18HyO1hNGj2eIfDcZchpN+AqdFnTR+RayDxEZFmaUdTPWb20tEsHefhw3nWwgXXmc1XpgI
dQrzHSUpXarzLk2JmYq9j0rANZ5K/HwYfLHmwSAq5acV1WJH37jjeRcNu4JtySDqO/ie3FmJ
/8rEFRY0EHWvtUE7LcEDxzZaDmmJrcqx9olQPi+OUzavNXQcTmckpKqpBVBJ1biJilL9uZDD
E3fhNOUy0Rp+rS6A1j6Erm4vKKPJ8fQBghQqDDBm+sPNAQYqahCCtP14/eDjEOqPeR/RmvEk
CnievrGvNzSGO+10jFEa3geZEpprlMGERZxsbOjc9tgMWt0z49CUJxapLo6skYCvOCbFymir
stHzRJH6QO9lTOfyffzIkkdGZovi0cLZHJZh6uxbMel74RW1ksgkptm9+o7itqWM9c9ACNTB
PTbT/P4aJC8GAzgL58kUeF9GHqiDjcFlK3nW3m53ePZ3Tm/6vhW7qbuYhObxr5hIUGDAfHwb
7VYZO4VnELh9X0qlpDCIKK/2Za9ula5+cOuCOd6Y14emgFodl55bPP+fk/ff+ff+MpPxHuqH
0SJUdpuYFqEylE83nBizdoq11Kle35lRyNjQzFiRNkQsBgqUZJ3bH8hG9tx2a1QXoJx5vd7V
ytPyNhUNymr6sySR/d5RB4UPq9JHuRhf82DvQGzdVUWd541W0eXT2+7pQtwkVAGRjh+0sXFZ
5AwKgO7Vdo5CbnZFww4Zrd5g2BJFXow7TrmgJSPC5Dhy+LYIk53pb8VyeT+Dsu47UDbSsb0J
kNNWfg+UZX4G5RsiI+2zyvdcd1hR7/WuKmuFG8B2ZewGZourEUVNRBO4NJ95G+TN++bw4zH7
dXJLwccLSqdGU333Joc9YMUJ2QV7EsND/a7hovXuGxwOdePkmz9k9X8aupVvOw0aAI/2TAWd
a5M8gPOrH8y8Z43ztWBhTynCRW+875a8heADyntsJSoFQwWDZ5h1Z7E8GR5QOhwqWNxPIIl/
k3FhfcBqwj9s1L6DwoIAbGdzhNUOIbwFN4KI/Kpnc65Em7/09b/YPeL5Y+w6DxuQoDO+l0q+
qphYEUkay7DAFQctJsZB5X0BLnnbtdkRPbvuGO47gCasAcjnWocjnYrCX99Oh68Sr/LrKtqb
gSYP4hcjRyoG8Dl38IOA86HbPwx9uhbXAm7qpSIKERUgJ7vdn/ZXkJRdvCOJ3fe8c6kRYKpD
wopNLunpfMpWId0AXFgnqeVjbr4d9hU3BpbZussrGcF3ghr2H0yTV6US58ycmcpiloV/2nog
0Pi8nXq75yEestHVMhWXR4bGbke6LlcqLayLk5SLQyxy21bnkJvqhKs+DVwcvxT/rRvFda7B
MQHdeBZuQXqlmUcL5xjO5cZeD57F99k/qfAgBG7EA+WLRMtOgwzmtm6O6bG28Ql/yae60+ZE
3yn/a14ogUYbSblR3JKxpTAHogM9KvSGBjR2DU22L+IrF0Eu1yyjTr4V++oNqskrNqJtelJu
vY+sbOgikWd3oTBcEyMIyfiSVrNhs+dYHXQf/k3vaN2q3caioQSEdqy9f+92JTThjelI4avR
e/UfY+pqdbxBiGk1jQ62xxPwzBzjuK7d9n3Fm32rCReE1i/LGUGHsyxuhZ9etpoOGHg2M55L
9+owxXLGbPevf7/p6ZDkecK6YHd7dhgpJfLmEvOHb8C94ryuXwoLklFiolVpwDqV7M1HSi//
0Lz+150kPt4foSXjigmGsgCSwbLRsx3tmCmHJucLJkoV3Tpa20kqZQ3wrL0Tc8dlo9XW7ZlN
5PDERlx/H0dE75APT82HDeNGHnf3vqySjZ7ZfzTUfywvpiR7c18TvM4l3DQLFtA+LulyrCeO
k95Z2tO+aZdaxN//XVD8cSGQqbPJswRPqKEcsohlFj4KdZbtfl74jefj6A0rb6mrnjijdgXj
h4VeOzT3zVryPaUFR6BoMTi5/zv/VcN+3nAOw/RhK9Un5DPj9UwXv8liPWq95IHyVYdpzRMq
fiFhZrfdN5dGucvL+pUwh43qSS8RkfU9X+lu3OSbmrkK4Kuahw0gANRgF4FWq4AzDViojCsn
VXWw7RYKB5yn34o9hxUBu0VUqLccsdibkLM+2TIFeueYlg5xvjaSjbwyuyWlqwA2Uu3DMso2
szc0K/VtW08t7sVkPMpTLdoznwiRNUAHFgKmiAlvxbJYOTTMo/hyZVyi+Tlva/lwEwqqlFXU
56cPm2084M1zWXD0EdwcOod0H7l+try1vpzYHPyVX5+3zb0soNOelHby9o0Fxf0EUVVNG9EO
lrEvePerKdtu0M1yn2ZsfAeB887BzOc11sZqajQOU7I4IcBiaiFwsGzGISSE2G2UsGm2/8L8
+a62+G2EoeLjlnT9ZiF+MKLe7GHJRpw3SJQGvmAmZTdX2rEeXxfUOdELyXfeu68Ogzrp8mkU
2XaOuG+A+XJ4ElnLKVZkXL/X2FqBdCHOMcm12d5WBKnPTfdeTzqIG5dFeRqnmRl7pxRwVmmx
8prdvASkV1I2HSx/OpU3CHRmclNSBEf/n4hxI1EnhJljKG20QdBJr9GthDTQnFq9l9ShEP9r
69mo3rDyjZ8DW9zpdxgqyq1fBo3qKfqZ5DfsOpFMo19aZgcrNa7G5fSf/hVDUQ8r07egENU2
5jQ6CPPlq7wjUw7okZC17NE6rNHjm0Vza/R7mfXGkdsMl2CZYwnREM13cW2KABimpB2nfBD2
zWErbgXWQduLGoPyZlajRBMMObkpD7ALGjhNaE2jj/XdSr/NJQYRI6ydma53KFY96+Thjo9D
pX4GvQ9Kzo1fryXhFvHJ2Zsy+vdQpW/IOY7SLHOwS4jfcM6KMA5m106+/JnlRc68zeJUlf/E
YL6pe2yIpiM9XMRVDaP1gihQ9ra3RNqACqD4yqUbf2jxOL7KTrQqdt5Yps4KD373/HeMoazs
M+J5PnCSmVmHdEEVuWHMmPDLvUSUtS6vZ9DZaj9+rTEi+uLwukZH37TZbdJpjFnPt0FDwszd
8lQ8LuFUZEYl0+FHCY20++mtdxrsueTspahYpKPAuZ0I6j7mBBDcGlK8ViYqL8iSxNdUx99q
ibfBqfmmzjW9qILOMFPySnGqHKz63P5yw17ypxE+5KDg5dGYtcItM+EwVgsE4NXpQpM3NcU9
+No15k3cqR4eTD50264tu/ABjZibg7AgMBkJTMt6cU9YQrn57Pxaq4f32suaKaTAYDY3Ua42
e52KKW2wjDhpM2PqtbuUgFs0gJ0JO+xM1mfhjAbOTHqJMlorJyJAYnvM5oKiHTucAc8JBt9X
5klV3g1b9hCJy1zqc9ISTyatB8afFU4OaGJqx/LZUG3m8mD4Gs9oMGn0NS6nY3FPA/Ll0Jat
TUFwpKYBmzZQi3wC0h0Jng46bghS/ibO3rBj+9ECmPLyrViyqVEgHhEmCAkkQQAe+WY21Fw7
h/7crDM9O5clXwxbSNUc1OnLUjY+WCpS6szR5HrF7+8tcxcRcrfoWZkSmip56ZdCl2Tcsard
fjourSRo4vPJn9enGP9L9rYGAnlQ3AlKbji7pTXa7LYTvr6dBDSV/hkXh+qMP/P6KcCltOpW
d5YUn2GHSOl5WXaNuciMQU8nnIXvEl/AZBe6nYde7+iz0LJ15g/o2DdDQ9UMvnWd6lMRQ8qw
1gUatFhFq6iY3/1l6v+OWfbv77q5NdDLMvuR44KUZNLXLkW2Q0toTcQEdU7q7N1IflGXscZW
xW3T+trFVziCHS2STnxaPujcVwDBabVsbDU0DW5tAGEXSHJWXP9QZYdKeHVLTJJz3wuMiA4N
9N09Fv88VKv7lcz9dATHOTDGfmG4yhXdYAwmkIvZayDjoskboYr+GB+xCtGs2pDdvHkrPAFS
xnr6rFSUh6kMorZJUvrrFLhOk5p04UOiz0MIpz7/iQEC5atWB1enUsZEZBENKXKo3MiyNmyR
Q7V2JAr1mXv08VqS/3ZXGN9peyySPz37WW9G0lsxfnkRiaScRdpxr5ikL74VswbeDTtcnwaf
bT5BnGP5i5MeFiYkL4+81OddBWejgvqROFyCWFTvxNylpxN3esptszlKvZbdVpC4XExLbDVY
+DUKYbZ/9dtItZmi4EETmbZdG81KgARiZRUM2O3IXtfIHVoDjY7zJVtfxrStIIteYwcepz1d
6ypFafXsyvFkQfytgt2SzUcnt23nI1vnP41wrDXRrFoJL5rmj09f8x0uDE+dXmgfvgBYV/aK
b7UN+fFk7SypgSpD5ntsbzL3ZwY31uZaqq0yKMKYAYNhi53MWcp3A8FOyqVk3574lwgCff54
F2CiU+RNpzca1VvZxm49RMHWSgtL5zxJ+M3ZG8iC1pncB/aqniRv1vT+ADp4/h6Uk+6qPwXe
ms/hHWME6Wm5OvcIVauj4zPG+DvXy66zY/QWl7V8KhGFh9Ie4lNLcBa12ct2+1n/xil6jpRR
Twu9lCVxKJJwRlCmqMFF4MgpWLprRr9+bLSZW3txQ2R7dDKaYn1sA3UI59d1iDKtXoaU3aDi
1jfEEGvlKUWD+tbnGoMNrs1tBAimcGj/hjsJqxspWBWe4wx26sI5n5uiKQDuPUg8seHU3h8a
ke5Rp8MNUeTci/HXS0m1NCdOmmsK4QYOXUzpiZmmRQj3VLW957mr4dzut2Ilazyfr/dCNhCW
N+FTjQ2+6DI3itKRTbehBE8XCsgKBARtdlf3JQyaRe/Tjhu5IL76i6U+QZZpd1bAl1NcJoi6
djyJzuK5LHVSdK5rHOQkYw3go8F+KxYrNreXbMaCm0S38E8ybZMUbKpulQ/j/Kd33X3xhla2
/WsSIkU/SKzq1B+y/h9CvTitSaqRpeRqKnFXVN4cASRiHZ2dXCAVJR4tVbJ268mLfKYdMocn
rbjdoUI9ulURjmyeq/Cd9axyHSHXaEfhFoI5evgHVtthiSrB7oRCvHVkvP3YndgVwsFKJDOq
XndMW8k4MLu1d5CYWhHlONxprFtGtw3RqZQv5ohbhUgS8rh8GL0IplhZPaFev3P7ZbCXQGlw
9erodsHl0FQyeeat2B0lxXKZ1LhLzGJqknNwXmz2igwv8YthzBWlyIk1febsIt9vxSzXrr0A
Z3ygI3v70ZrtgbpUQa1QvGQh4dz0604h3qNBIR8vm4ALh6BV+xY6AL03X/Xl8+AqTMqOauVP
Q2Ru3p3dRAdsqiXIWh5H3n6O+CGF7p/Dnq/BDZD6JCO6ZR1mGiUTrm332/ZjREnd4u1Ncf8A
jsSKxpKrsbieS/B6dm7N0/WywRGLbCw32nGYg1Zni0Pe7MoII9uJtp189TD5cwuIxWJ5VXGF
VGoDXmGqJTFOsudlnf0y8Cc30RLSTPPxxGXzjOEbcsGyoDX//g0tEXO8UE7qyFKnfNP66ZaP
9rberoFtQP6lDwwVGhWeYaf6mk8tpFc0jUgvxPimZ76gPSbNpgikn7yJqr03usdPFtfGZmNV
0L4qqp3SYns3/tB8+n93klRfbnHgVmaO6FkNWy53+DF4lAiM6GvSHVJEEsJbuxHTHeScWpN9
zeXn1RYQFaqq1791jRFV1SXIc8T3Mc9FLXuWXR3MzOreGyWBE76+40k26Y875kEB6i5+AZC0
vTRivQzF1dWeAMqCRFqyGKK00pSNa0itpDq57vxyUIU7biDrMb+cDPIOQkMawutKNyxA8iIM
i7RZfHP7xcIwuEb8pLE9KlydGu9n395fmr1O8chLGBFkscW/Eoyk1bcFGE5dvQ4UVBl7f4Yz
13Th+zQUT3vju5crYXUaRKX2hyFxX7yp3/t4Zabr2vYWQW1gAtJZBVNV1zQL4XqTk1goyO6O
xnyl7tSKq2sgyu+pmev3HB8hdoh03Vcw9DIqCcuANwz1h84205biKVFygklrA6sNHkC221W9
b/HDybEsV3v3qBwXo0xqkfN4Y2WMFsMZWr1VbI/jeX+NvUNxnMJaoAWeRIdAFH5ILWGEnYtE
BgxR0qBBLATxCYQuH1ZVvYPT0xXQAdASshXN0JaZIv7q33Tvxd3CmnMSPlqeLbKpbKXtFr9h
gkVao+ep2HWETyBP2CvSGrkqTqtAeWOMEXONUtTnGpM5sKc7wNGBZ+tUHbRirIx1gwwsMq8T
s14Zk8LjYlQbynwYVpv64VRDZ7Yo2jEXm0pCS8LXvp5QZC2XBXhgrZ1y6jdswN0FeFxqKWaK
tYjFv45ssXZuaYmiHmLTQV1q5jcD8mpWqdy+G66LJDXyTXiyGUn+Odm+mOCODQsTOG3FxZkI
YKiHybgcsnEQxlcNPXZ0T0XFzGr/X0VCs7AIBKjgT+GPW8GVyEPh8xVB0zN+7qlxGvjO1iKm
kYrq8FJN8PpWw03X+E9J+R7K+uhpUb5wYolkxOzEclIKP2OXxa7D6ACeUYPTot1381/8IfP7
M8J2j+Y7jXa9FSueUjj8W8YQT4+kQ1MJHAL6c4waDoeLtbKKnr4qrYxquGzqPXYLuRqvHwYe
Hf5hMEbdYdjJelsOz7Ooh3n1uGPNNeIUMClksL7uyA1XlEJd3YpZC1owFrpXrvPDlkUX9vOi
S6Tj7mue6FigsV6Fk+4oNTq13JPoHG3eOBS53jVFKpAMiEw1dimuMnbxwU2nIZFyazQyamQ0
5BB6x7yuPn4+wefPLOwUsjDiaPMPitJ6GnfiRvSXajjUP28V2Q9/KuOaNbQYvmwWzw69KJH0
inRfAmWj1dOr5M8vY7svFun4MCs4ufeHV9eDQSFKJVv3g0j94onX9/Yvnr9NMke0jO11D28U
V4NigS/DwvigYdpI3eepxeN34SXJWJXTyckog3+LcOS33JM/2OdcbFr94/DX7SZUZIrXqZeG
R3YyGN7FKN/QtY+zV5BdlQZgnOosFBe4PvHlh1Ec+nmFOp05dv2SDQUJgKafiHQad7SYE+ja
XEs1Y0grXQzE0cDbtjG7d7/inf9yxuEueNAm0pnPVwI3xKjcqQ+6l3ihP2gRuhiIC1xc0oOc
XsQtRbY6ORQEptwANnrF9M66r00GN0LW7wSS1InKNO2bEMpDS1DiUQj+gdB8zQO93SPUYog9
A6a0KKJadonp9SbRFIOGVsw0csm0DgE0LhfBeQ7anwtNWQbqs0oK/9xywfSjP2iYf3jaueaM
k92htllABcMM7ZBdS2scT8ZbW/yWcdWzbTvbv+kKmv6awkCKUhi96iGJ71IYEcrTJ2zfpTDg
f01hoEQpjK2AbNQJV3QgIeVD5OuTRSuftaeLe0/yhUVOr9YzJAsTvQeMC+YpMZSc7IFg6y6+
H8MnVkiklRR+EIiSd2aM0bqunvR5oC12bUWnfbfyRcfS+mp9LiO3fMoDpQ3Ih5ibrchseeAy
Bkpzlq2RAXwJhQAFyTRitYXldR5NXxn4qrrM083NLWpgIs1tXYtxjA5L9es8xrCzsor/ImHx
r9aICV8KW6nUucL1THuop8WEcmWmcalF1S07R49sh8ffz3wOSzSySSvbi87ECMy2L6nh/Kqj
htfADBy+WojRaNDnf2Gg9NfBfk9jPyAX9ebBXMGe667lqZduv+HUj2Jp8k4F+5ZXvCFDw2RR
Mc0MytCj4uIrvcA17c+GcrCBXaJqhVSNFGxJboQ1UsWP6MwYrdUYTmUPwuN792bS01H3yvwn
oLIOpTWI/laKzZ/pI4Va3RFA0EhydiqWsgY61heNOmh+495J6qrfhNx0sTx4+kQ0i2Uiu05o
kLHJjY7JdO5xiAmiWiy44dSbClZb95ZG1E7fdRv9kGzCpWbVnRkdLz68Wh/s0p+4PWOU09MP
gahoZHdQxkEw9WokdvSmbeKrpLrfcKX/aV2U0zzoBsGdP3HfmKVdeME06NkGuXW9oLVjdtPW
5zKYjuC6iUBcDsrczu6D/XDdV4e/z7Mp0oeHylwuur2dWktYCMyKM2MZgToXi5sW40i6sUxd
Rd6ms5MdAtuhWaRzScQtFiNlAjtFVR013vFbOwp6Z5jHFWxIUHZfQM7y684iohNAwnF8eHEC
8jm+R861SwdE+DQMN32wbdK6zOJ2g55GsVKbHRs/ZfMEEbj7GWu71xCuqyvHZxrs9DiF43Cp
X5r7+vrVX7B89C837LykCVyrSQlsEDBgQqau7srhq4FRtUrHRnq7ebrKeZOOI9ywEV+1kuIm
kezVyU5UdZbXEXlnArGxZs/mznyx9211jKjozP8ydsS+IqZQ/SEa4NFmPFv668IhfjFU/559
EJk64Jcwl83KOIj6OfW5JEp92k3TdW1nHvrOxP4cwg7+NYQFvB/CXng/hF14L4R1/UsI29MX
lF9/Q5jvUZvk3T4140qv5I8QE6PnFRJuwiggoD4QoOjuqgKxvASqv/gme923kTFzIGrZtl2r
oUv8Y5O0HnuXtJtlAsVE9ROQBfZhkWhAEqeiF3k4K0754ZLcRP0h3GIcETTxRuBwe/yVHIjR
nRfMoe01sWNqtl4PKRgRawwPu5GeGVCQAYyVzxuAIPrEBC+SCexSKWAyxpkrzqCpxfpPP/b9
233Tn++DZWY1FcQh+cU1E2XX84DtaXWhBFe7TUBJB8n/XBAKprLGqh/psYsVo+6qOjcPGuRp
BTlQ5MMij8RGu2imCGQ9Rbt65KAQavu2nv9t3N/e+r3xtfi+SVtFE89uPq2hcbOCohsBNkqt
B6cGCbxtrvE5E7Q05w0CDz7Ds4tWbQDZOcmcPTZJS3TK0F9RzEm8sogbePwMAbnW2VJ0+OAU
EzdHB4FL0zbKhYGiRToqzWmYi8PiCO1Xwvect6zDTqQ8fEoqPhv9OlcG5p0a4kkPdlRWe8aj
WUw2p04ENqPORGtiKQUXS3MjojUOVCzG3thRHVNip5e/AKdjeQunk5fWhjDQji6cOXOU6hOb
hVvuCySU8qYz6FPigN9uoP+knnESK08RrjKINkjPhOQgAyl5u9DOxkbyMQo4DxKt5VCepT5I
nxWIMwPZtdjZ2SEPAFfSXlmGXY9137HipsKRcreguTmmnh67TshvWrDqL3gpzrZxOBWzFs/C
vkYXFbU1UPR+gtBgDtzS6LEcZuLfij+XMTe+J3/9XBjsrdh23/lU9abFsDmCXzPJzjZpQtvO
CpGMwYfJAL+E7xhMIJonJXsYmzebg2m3CW/OPaFKKesolC47zJYQcpJxnC7/TpBsC8hOqKby
Zde/2KribkvUHO9fQzDRAhxA9H4Xgy3+HIMl/021YQ2QsJh8gf6ZfjtfFiKDJOEQMzoK4isS
RYMjqPvnbhktR/6spXRcHtClAu1aolj1DGDEhXMON+tTV/7CvrWJ2Ld47zo9PVIGv6NBP8eq
VbnAfSlfwO2hW2p62aa9U1I++I5uen32XneWzl7RIDFeVUjlDO0d6Ptxay0VWum7EKU/7vet
MNiDB5IGGbpOajP0LQiI5Q+8hPUi4l1ThqA009H6mq3++gFySaGgGDeHNG+ELpW7kWzZ3RUT
B765whowluDpQGdd9PQII51LJlGIOVzFicwEXKAAKGOBqds54RytYtZ6DLmy/0J91aI6bHm8
CUx8kU6FtAxifUU+dBY0BQtfU5hQV1cjrOgvMzcWfSFxCiqpKrFOYrxP/np79tlZQBHXdlWz
g580vGnH3AG2EgPaFif74OryagteAr5nA0rsWYLVRnn6rmgFXduJma9oCa6PV+GCNhaxfKk4
s/sWO1Uj9THF1KoZ8dgbfx33dzR+Z3nvB2fgxX2DkqYX6TNW7SR/eNjhc4O3bj7yaBhjpAMd
pzp6COY15dsivV1DJ+9Yi9O4108a6hdfCnFzpm1leThtLgzoTcaW3clLy3R7ZXDkIo4H1J0p
VuqP0melqsC80NCCQU009itOtPXsbBPBRTds44Db+gZslzcOZnv8YGGxpIE2Vyh5QeTeiYkF
OhoiczOtQVaDYz2O+zR+xzX/Z3X9ZDI/I8/r3DRSxizuetfZ9QoZ38EYQ41AdJihRykqk5Rr
rQtwF2ZT7YBdfqQoMtCAvs/FS2NSXi/fzISZhZmZja4Dz8uXFPuw6tLhc1quyjRZhsFGMRW2
EqI2mjDCcQZGOMvHd9/WY+tO3769jpyRWHM4FLAYDI0BC5N7GHpqZpv4fqvdrxeDMlaZ0iPq
nbr7WM//lSaSrJxM1Ks/ymXYpPun5b4Vs6dD1kQRk9RfI6aBbTbBrMeKeWzTQMTeB4oonJUc
ycp64MhI6XBefYByDwDlEwOwmzvm2ckUOE0t02273dp2DfWVC/6SsPaSmHJF80MNS0brCoyK
kn6C/pywRiKsZ/O61D7fWR68s1jx98vHS+H1WdRflo909b1PjH8Ld48xiz6l/FLswNdrrf2+
fN649v3x6LBqnqcqiTipPem084mKjgMvJ4Vq2jVufyt3JNhtEHBpPWWFmQSZvqZr+Q20PWOJ
t9/qPdseGpxHVp2ZXiz6Yec8GqsTMHxb3SZZFL+aZjMQsdui/V9EyofVkJGsDWUN09wgDa6S
XD/n+JDR5ynLbRbziHBff5YgfHdzc5/ZF3/kfv1O5+SLvceKNtW93k9XTL5uYrPBtinRRvVH
ynr7R9qHq0FKF+exsQy4mm8sHRrLcIgiTNlFGXgdEnLVfyScXWlofGbcu8Akmls8dol0JR1c
6CPgX5sOUjYIvQZsgXEFc2HQ4g1JZoSwMjZcprP/+5PHx0n71u3VpURl7ksRQFV57hyWacGf
GuFJg+Y31LkEtghXmc4968nJPGnpfbQbf+T6/yPO2Uf3YoXfarYPrlH0DEG8Tjf2eY6pW9Vq
9e0B3S/2LhSFIlGiwjHb21CISslyC8PLCfynizU68M8Yt7NFekd/28HVkRFFxTnKk/mtSFBi
7GQlX7SWJrjUaaC2zB4gftJeySQERMXS/CV0N/idDXNew0qSAGKRN1n2amA0mEKr20YsluCr
afIqKprFQ6kYXKDk5L/OLvsGvEKmnb7zqntDL1tCJs6y/jwi8hua/uY3sIFdk/UtQEeHJIco
NDb7XQ3G3fkTLZz5dzUYbaN7366mvgt5HDF/CXlS/xLy7KxXGDDARyV/HAtREYXsN8ttdvuX
iCe1VF0JaULPduRV75wejC+qTyuq79C7OtFlotOvUpXz3CqspbaX2JpSQ1mg5eJNSuXO4cLP
iPPHmL6tQ4v+L9qal1lEFs4XB61oA2Nj18lDR+dUST/u2xWZ5YBeZCVTs6HHpYvuT72Z9qz8
mi1xhI8A629+Ki75Zpt0Zj5ufKifP5yKG972d+oP7mnvYbqmtgmUDwIdF79bec+w0pdwcrSK
qGVQ44zyYaZpjKKbAi2ZxyXJhfOi5ibZleDZDbPv/rQKGHmou+FwbBOZqBeHeFw8yxrQNmdO
pYbxwVUJtSikupJawpNTNXffG/g3N3+fdPRDyTnDfnWZLJqxelKeav/1q0s6jpVKZd1FxC4j
XtqDDWxdUbfMfbC+DIy9Q9OX18hgWBt+f3zK8i7vNa1tntKypz7aXxkVnZ4LZu9+xetqcK3g
RnnLdhvBQMsMGee+dOoIRA2ChgTloD9YXG8cHKaohwRuXwoMqEXbpD9xK5Y/fPhovyfRl6k7
hUWLyiXW/ev7Hihf/s0X+5/Xcd+rvKHw0mb+9drAxKuw7YixuaF74F1xMBGq2fFqGQuAqtZH
IXA8Oy+ivjRYVxGLnsXUffUA8XB2ej92Qw+54D9mr1b+xFXO0OIcnmh/sAHLdI1Ca/KW1/HJ
i+XsxTgNDZSWLsjw5eGhMcuTCGVdL91XUaXN9VsVs+h8GeCwvO/pjqbO4k6kwq6u/hgbE3d/
JhUj4mVw6FLc+adf/IvsJXr+Yb88/9Xz5uDRLUSKcQl6KRRS2pCfw/K1NG0jySCmrP6C/Cm4
X5GfbTfSKEJ+imgTkWnlC+/IUqKC1tTcRulydADpl8ihfYYYjUW/uRtxez9ZfpqSpwg15j9J
LxkPVCBG+HSNmFFUVnuvvdOqBbVFuS5PBxRm4rKX4GOirM9dD2WtfF1y+Jh4qSHP/+u3Yt9L
cN4VYWlVuGHLYuX9mgoPn5Dqhg5CS1NLcdTj4TkC1kzIqc/YVqJo7JfM/b6L8VCNRXLpsOMq
RfygZa/C93tn4wEpLAuk8IcR1o7d5qeeetN/bq8c9+5txQG4KQd6bvzNniY+J4xAXhfGprfG
ebJR8sba7P7q3Mh1gYFrogK3DorCy4JkFj/IPHdR4LFeaMqSvDe2h6RExDtYk537ArAqfbjZ
zfkWTCHikffm3wb97a3fx6Smxr0Vg1cULec0swx4H1BM663ZAzDHR+Mgh9v2n9UKPVYq2tFa
dJHv7r96cbLaigHs/Elj9Ed7R+MKM3NwH4cyr+OEh4zNgArr1uaZPSP9egTQpLocs3N5MGGB
aejqmtVKBxzbIbrMlukkXQ9Ob3i2vp5fvV6ASnsSsGVv8Wm2m1vNRJrLGbpiKTYbVboknPqv
fuTFxKQLCxqBq9rBmz4uclKlEbsbj5y8bdhMbQYrB9/n/dksSieFwlKlPgzANxFUYkHW3zqf
zILbNpoqTRIgA6O1r4corjqAiHIuxptk6NVMgZUWMV3eoAznDZEC6dHmohfF1X03QX+K99Am
/gQDKouH8nYdTji+WrMLcs92zx705ealvVOrsjG1yyCgc4+dXbSa2r7tL3777PkHPcXdwyg5
gI/D5zGM96EeLaII/APfUQRs4PA9GV0ZZydRnlatFGv+CN/rt9Ueph+zVQxbFpDeimXHq1Af
CA1L6CHqLg0OXcL3H3Uctu7Pin96zrcxrZgR90jfLvWDmsTYlIPllzd+IQnsRCSBx1KBrKi0
AwDB+bX2JYlyIl8GxNVEtHK7bwB+GiSW/+LlJ8Gnaii+6MoFMOpg3JnrlloUMA6rgcXtXOvy
pwYVPP/lQRdtRvWXgozT58vVCRUhCU1nLQermoYsJJcCK6LD/IxJ3R4MA7yj5TcUsozwk8Ow
90yzr6CcCmz03vrBd8LXbtYj4dXET+PtMXGfFgHTbYL7yEA3pkPTZYM/FrD+rp1nJesnBSeN
fLTrNQY2KxuXNe5IqPRb5wUlFkG4rgCJvCDHhUGwk/QozS4KBGKhodmH1Fhb4gpbGXAHxB3O
RY0BY9m5Kv0VDUxQy8vqXJCVw03bqJ05pqGj9TFkCqGuNFUk2UU3xXudGtfuHAuRrPaWX9y2
u6N1wqo9zWh7PTeL7/CQO0+0sr0VXoeF4gj0Ef9OaUXM/pz3TPXf2NT0xNuqyZEy2B2icFoB
WBfJE1eyRLODjLZBhcXDWJW8PvUCbqqvCrnQIlugLw1ROZ+y+sPMUZ6rZb5Dckw5qKWV3ZCb
mVAidEtGC2ZXXAtp42DSKIvikPhy9gDuxr/CJPMAY7h6kzY4wiOSoC3YNTu/1C/KNOg7j/T2
8HRlJsLKWzhkaX1pw3d83QT0F77Osgx5dKMYhxBoD8cKk19pCh3ue2TKLUcG9e+UbWBG30Xc
FvrKhaBhovOgVdJPJoodfYY740GOVMMzwbZSXzPxmD3vJc5reSz8NE+Ua6j3vyXSiKNycNm5
78FudPiYlAh2g36G3WHUGFuoRRh6D3Zhfwe7Tz9GSotmzPuyiSfa1aub5v280q3gW0mWMxJf
WX5ipvmYGnK//tv13a8fi7jJ7MN+75lw31fxLkbXdp/0FvD6cBwDP36clrFHa6ofqavXUE4z
Z6sqVmlh5xQF9tHS0UG5TYtnm/nQFrf8vsffQrPOtCYop1AQNEMv0ni02aYhzXmDpxRisD/3
veF/c/PIFswS44SLFfqs7iR9eeUfn4fJ+Ik9OLPyZVu3l8n4NIhney34SF01T2lAAgQudu+H
ZmP4IAPHLfUY6rmq4RcCK9FaHjX3SA7eIfX5pnnpIqxNrTIdOr3FXmX1G6s5W+sb4RcTzV5g
SgQjnGycn0hVgcdxHadwKh84/OPv8Z9/dG200l+N1nM91wBMRORguHWzqaWEnAyGjMxUdvb6
vi/j1pdHy5ev9SQYkZ9qTwUOw12609ur4MGg5SHjYDC2bmk2B4VupxhEARJ7RWudvnP/4TtT
K9k8TbT2h2+87NqWjCKjsBG8pttBnZ/W5ZckU+xso3nWYQYcjBok7nA1cnlDHPHPW2l/2San
J+tDIYIeOFBLoa7ypNodDSfGgU6xZvrVLQ4pv7jJTLv34uQKU9S8ckvD7Fw+pbtmZM/XIHXP
aWrgiXV9vseapaaIS3nnJjvYtc8wETyQIf3UG754uCEt0cSDHcK5dMKx5VUk9A01q/4XiizW
ScitOD7u051TNA3FqrE3AUfYP8nd7va3s/eq3T8HjPV8RR0XR0xuGgMuztecxiv9GigPk/4S
KHu9C5SVrlzqeMfHsN6RZL/+fDPqwfashptWwyGWZg2VuqJdBocdS/x7drtmxc+9iYw5zfHy
bBdwKxxeaW575ugKv6h59Oupot+y4gMbEPemCf8jtbeATpORDYeNbQiFvqqHVXKr+yiACvzE
jUv8B7kU5YhwUHX1lh6Oeq+mas1CVQ2Kr6f74PhXHR2aglQGQ0qHjv4hd/n36KP2Ha4rWgH6
iEWdMFOGzhm6jcRZYfZyb4czQU7wwx+oqOqoaaByRI5drrNDVOGhhUGHRPlTyaJ9fS8XJQjy
Cq4ia7KANHH/0TWjEWLCaEw4EUbXv6c40/3pao9dtKUV2aqlhZV9oP094/x3Nj96K9Ynr+UW
Rw8V93j96brWWzGDuuv2FTUVTIBoL3cPbMVBdl8Uz5oFoYBEXu14KxgbcAMUcqnADx51oAd8
0pCTVfEtr/fUKOnxzFBHasmaXCkQbv8ZqzRbYLfZhat0dkiSlq/XKF6pPfDPb5V2ri+9vjPU
IStYLj8ojSJirl/uRIqY62NM46oqMzsngPovXi1I9z0krZ+2LEs8Sip8D0l9/nckZfniRNVW
dLbUVBB6L5RInV5xbOuvNMh/pzwXvFOex7s7QBPNicY/K8/jaM4tw7/kvt6R1yndhWINX1cE
oV13TvHZiQdnOsGIVkO/oV+F54htkN3PwvMHfejalQ+8raxsAzLof6fr1ZAqX8+Vq81t1vJr
WuYGmNZydqmy94A+zftXIqz7S4ltkqqBSvLdV3n447pKbI8ubOG43+SBFzfem3cVBdXDXxkm
eBnVCCpvGYcb7S1UQblvUC/DwsMqGF59/bk1S5OcBUl9+uHoLdIP5nbjC/ThKaOG22WtPsA5
djRRdzHmO8BZ9yvvDfmbm7/HFV6buuo34cfp7mqwzpULwHG7szRSAzHJGSuiygYVFVVqqD81
u1GVz48VNlHMNGg9dZG79m2vWSYbpwmnq4rp4YFV4Y39my5vcFDyfXi9w81J7dhj321sar2I
r3reKxdMkOEd9pbMqVkMaMFM0Y8N3kNOE0YJqp3jbDIIqcGbWsTfhf83k1W/3JMDJ9aucicK
JFekHI7W8JVLVyU/c4KDilvbk4D5LmzG8QftIca3DIepI3Fr3hWknu8Y0UrTH2RcJYewtrf1
9dK29rRK6RtHrNpvKTw0dwJ2zSUvOxkH5iInLJIbPpHc/s33/X/tuG8gLnja9rs4SkD1vNc7
pun25DumCfsL05SzZDIwAWMno0tTfq6KlHF+VxUp0N3128ysF1VFRkcOj/bY3Pfp2kH3lxDv
48HFXP8Gub138prZ7J0tAkPWSUQ2p48lqsYNrtwuF+0uiM4APEn7aY5JT9SJ4i+kMea6Yp2U
FEvJ/xNEb4lAFOC1eUAEol5/D6IK/wuIxjHbs4+uvxMK/8o1/Xqxsl8P6iih4VG6WdLLg1qw
w3DLb3IYM8tTij5074206UK4Bxqrwn/Rm8HZua9bEriyQflu7vmvJ4t+2+xhto1V45bBrRKa
R9GQdcmsIHcsxGzT4NurrC6yrqhgEzIVd6rCPjWWqmo3LRO1UPfsdJEMmBXJ3ZQBeOaYkF18
2bbkEJWd76bfH/a9T/iHzd9BNn94do7Y3hVl2a0G63lVVUqsNckExxy0kAYBFE2UjthH9h2M
W93ElVZZ1FeaGnSoCKz3vHlBZoXh8M8qxp3Ce2+OB+9SDRkyw3q8WrzGmsVkg6EjhIKY8OvU
vYewuOGZ/A+/53/FwY+a++E3DcJGM+PpN5Nug3ZjA+k7/QF0GBpHwA9VuxoHOwEBHtPTFq5v
sIU6MXOYWGTyhwff0No1arKOR/LFoa8zbfIbn/obAzF1c+jA/srTODIWnQApPI4yxuLqVya0
2rM6Dmf9U6ZQDGwbuRql3l2TZk9qFdG42DeOMSkV8odwWD7MPzDVv2XSM4USriJyNn9WuwF/
Ubu1r92dcFlZs+dwB0MSdRWAiZrLIU6YAftyRGFmwaqnMOjT0WKs38ocRYRsItGI/s2dDLhP
rxJpZwRqwnqonYl3tV5omKQ8C3HAn+bZRSGwM6IYNE7q72PQs0L4mLwoBkWKXmLxveLPMajm
uxg06GfqV1mqGzb6V+p3xVXk0w4li3540tM3Er/4O5vIFg1sf1Ws+kOeLpthG/PUkL3wEZ51
506MZvZbMTVUsnRa0XRVyKWZQwMSket41+FzD2WlRWJb0XbUIaktfc8Pd7832L72KFTVUtSt
Zhr9Kby4xohLr4qIZfAc7/lSQPFdU8dOM0IQnq/NF0IHNS1V6mOPC8kehqzY9cX5rpYGX6as
7TyTtRwbJvYy4L0xf3Pz9+AoxhsX5985qWwo3Na3orpAMp9qOdYslvsNGqvwkYlS2iVY1U54
O2hCTZWa6OTE/2BM6DrWaKxTT10gHBsmwfIalIGYBvs6DTRm+nEMhA9ydBZCChXDZ5JEJJST
UsANRO1v/tr/sR2luM4MkD7QUUZGEatOO3tkJaziC2b0mZlEZ3zQJJASqxrpNljtecyLwJSP
2Jov0mgzH5xBQ2gdVV5C31hXGRnujQDNkCCW/dxLA1rfo2nPbobhHTPTTXe5mQbjMjBGk+Tl
UCUjerECP+kvFOUfs8QNsLOQOqmu/amZjv9iomP7y2XktbKFOxxIWPBoB8k6pcrOo0peBfe5
YBKKxqEhFdmLkByBnuz8c++L0T/NXHIp+BPT5WoA64lwDbLKEe2E4ZQJqsNw4DDcjubrSMYY
0zbGNyC1nCbratV+V0v1YW+2F3lRqh+93vDkrdgLSV77IizuweB1JxfDtEpW3Jk4EREb/1ci
luYVfVMHoyLyzKpt0T9nXt+/xg8/mL+E5XRzg2D+r6sMt5LivnVFlOx+Vve0KkCwzrASwVhB
tvu9W306RwggLwawG12esyzcsdDUzk7ZhOx7dPb9sfydUjZUs/ZiDHdd0gHX/RYK1NjMpbAJ
yy2t/EtMORVVVq6jVXudhKxVS3vU3f+xALw/zv/Z/h/b+/6f/UQHwuw1ReUEt7x0OaLKxWAa
G1xeBIEOalm1gJAtHrhakkMCfRxk0Kq7BtlnvWtRG42DS/W2sQeMQd3ovMDo1ycmwR1kZ2sk
zK2ijR5eksxzvZUDV9JAGbRGxt6gPv1Hn/xfcmzfNxbBm+4mntTbef4vWshGa14n08klnGSU
vHVPzA7CONH/BSFXqOQD7Ym9/HH0K0GqUwvfviY/r6yzo98okp1ekQWQCvlAdy61cnaroRI2
aZtYeurhF//ExWv4Eyz75D8CPBugfpws+sTJAfVmyyrvbNqHuP/fqFba+DpQw/kftWaywLr6
WP/A484ORP1CyGBi6sLOlRJ7W9KHvIIQE9uSlr6Z4Yr9DsuJm/h7qJ2zBqHvD3Xo5Fx31TMj
0jmz+yCynZN/ZGCMdxVKWrHxG93SVvwkOSU84ROvDW1PqmrisuiNLcHzOfeACw0h0EB3ciTD
YiJcs5Vk7DdGHrd9Ltn6/ri/sf3b/bh9H8U0hqk0ZHWBePg0n+vpK4RvA2WjjM0VZtuJhtfY
BItaQTosBQV9cw6OUT/CGxr2ujCpBKQYsmm9bcMmoE3LAo80o0lVNbNdrYSS1uVYROOp6k9+
47f8T+62T2qrPJSfLuwkTPUHT3h10F6/3jS7LZcL5xY/p0zogAAcg8mpUVyi02jfJx910sWT
CyRDZGqBWSW2MzVPkXIHz/TlNqHLRBtFkUTb7qkOHyi/8U9cbWlB7f/H3XuHNZlte8AgAjMW
HKQpUrzggCMCIk3BgI4gFgJiCEgJzICCJBKkl9CUUTqRQaQJUdAEEoFBCCGEIl2pYghIEkIv
AUIvofrF+z3nefA795wJ+Hznzlz/YQVX1vtb77vZ795rr/Vbn3nO2R5dbbJeVzj64+g15E3U
vs2WAEeNg9n/X7O8Mjq/uTb6mipIWZCVMNXROseggIq8H9es1PSlH1+v5F0W0mofRAot2912
N4yV8GZKxlLRCEMNq2a8h/MA+gJ6ZqtBc1ObjTTHvRG2qgP7pUeWCrKcx7oA2RihDVJRoGe6
fe33QR8Lfa16zj2ZbL7ciN00YTR2FMXkYBEtYqAUD1ap3l7t17VBJm93tEjdxnqHEyFhrMVs
KtyjPXo6UrLy/YvhCV8EhwLgbNIARU2NRT6kiYi3p+zuYxb+AetfVjinW/OuAB5T7nZwqTIY
K0+IiWmiMArNN+yFwVEh5bufbb0Df1dZSjUWobR50E+3wg8h5icGhxCzmeaWwiJf8hdIXhTp
jeTUTEc6/wmvRIavT/7ZVYF4Q/30qRZ5UDuc0ksIA2opqqDiynTk+/mnQ7/hHmxr5HYF1rFe
pw83LYtoPRU1GJrQvXizqmGaw5sAIIb7pCoSxtG8KX9ALzrD2Gv5d8bSsg6W5NUXoAedqVjF
92AJV5Ctad11vbdb0O5ZnQAW5VCIcOpacatUz7sP2q5p3j0RG4JH5CU3NJdXE3xi/JYRfHEL
Bgxz53uoSCm9GT17Q/qZ0loKqx6uHRXBBlzQP3RyJwOC+6RNfgFvsx5/m7T02IlInw1t94V9
rupXalmrV3+qwfuUhtTYlc8+WCjxLfpj6cCBpdZaMnPG3WcE+fDlJySUAYhSBi1z2Fn/L8y4
PAIItibUT7sD5HZH5xzIqTWszopW1JB6vB53AyfEmQAFIec/fMtY3JMygZyvqz7wGp9f7bDL
zqtkMXKmbbILrX7hxD+ZlSEtuQ5ZEZEBydgeqlNUZlByMuvUvmI4cK82bEoZdHfcTDjppVNv
1buIJRVrogZ42eXxHdLv5T71A8OKv+k8ArzLS7PRN67COiDWKwBRdy1l+S3QvD1Ht4xNeWez
FlR8OfHkQHBKODw1v4/ZqRnl5FgZdkkG/CytUHbZIs+oes/mWDppzmvq3HQsUtsFI2JLrTym
kIJS9p09nQsyMCLMpVhi+vh3UkeyjQSjtkebmX6JHWHgj4vQQbnOwnr9eHWGbt3Nzzw/DspE
hVTVqc3wXejb4trfV1QfbC7XuNeUbTdFuYOSkPQVzu5Cczp5eZ6IIaLihsIuvP0G17azCOVN
g9/zWTLpGsFFB+gBk/FqZfi7aeYNqScZ7/MW82d9j/M3LKC7lKHr8Xdf66iwfTUCW2wEppPK
yOajveXCS4Rstu4uyFasg1Jm3Z0lkTWAnpq1Rbb4stZDVFaXJf7wmUVqygb7eDjabhJzx7Og
hkQ864mMxdq1fFRtCG73cOtnZFJEpnpn9fed19iz1SCXMvfn6Xx6tmU2mKBFYSqxK9hO/UyK
XX4vLc0fP1S77uUrEHaeywv+tdWcm3JcsXc9q+r2/BTXM7ewuilZNGldeUjjsEhv01dnPtt1
Y1uD6/zGjYV9sQfSWRvBwxEERwv8q/FD87KYzFx9mSgsp2MVfCiQJz1dVBPnb0ucVt7lBrT0
2hhFKL5NJbHFp391qANkfYrEtnhOLfM/2oqTT8cGPSKhur4wfpjxCnfE5FPgDdxpSk5c7we/
UkwMYQaIdWEfk1Te+hUuZe63M35dEK0xbOkIhx/HySkoQiBIxw/kazOa9YiQa4MtzRtfIXqK
jLJMZAzfpyzLKQTz3NHgEsJfW41faNGZStCa1kEkgPNyZrS1El9BiwcJv8s9s3Z3Jix/wpuS
Tu8t7FuaxATPJNyaTtVl60bDXUpf+yJVR9mdUyvBdKmynXvICwK4b/qVXFh8imcbn7/WmiRT
oHd4I3Wh/s6P1//J6p6bE6Yv7KpGnGETHYPsM6vopvqs+iDAhFWKu22gKBg2GOpjeTEIerzD
r4qgYp+x/PpOSnGu8Yr8W9zp6ESDEIZN5PJR8a8K7vccHq96c6J7fXQKcjUZnXYkH0jGN2mA
TN0EFGodLaeae+qIliGs+z70IwzR2QO/2ciHgIDmnOPsNF8gpUwSU0bWns2lJ6NwMhIugqf+
Ce+f/oL7yJHUASQCvVTf5yysjT7nW/6cBbG5gZde881r/bHpSUONxtuf0l5eIhNKVho/LgYM
OPlU3MdCO3xQTiSvAf/gfUT+8dA/BfN3UMAIFZOsp2SlisXnp/WULKiJLgXSZRkyKhBaomld
Eocd64+p876Q8uH3+d8vIjzVD63yS5ovI533DPslLN+9fOy7nfu4Cx0wuD57L2xCGTaTHJqU
rgJwCFRf02TGfLj6/J+sioG65C8S+2dCPKzrUwg0m6rKgHPt+h+8qeig3jYnwHtB0IJd56jp
SJL9R6V3qa5QkurpKNflOUsfht2PXm0kUcPeuAveb7eazYYT1i4e2Rspdaq3w4C94WzQ9lHF
PzBDQHpVhbzsid3dyywgvdFO+vGcRmszCegvGSxjEW8LAqxLqnlM38SLLAaCSaCZB8CtJrmU
ud9Lf9ffYePV072eOGtqXiiiOcS08MprB2CqmhsLoy3rgOOYvt37xiLxx5sHug5q19ayAy71
1H/MahpiJSVIOG9c1RtT+Ybnw6U3/wk1/l+8a2nacz6E7wmx0pn1qGwo9XavYsbraL/l43Mb
l+uIs2GkUsOpNN2wBID8Fbwt2KK7yxuoMhSkDLaLqegVh6jPPLgTunOk23qh2wdBva60DGdB
J3wKRjhk6Qv1maUD+hfxvntVFJzHgV40pM8vPxx4tUn0NBgNCbdvV4e2Bo77aWee65IbSU/o
A+kvx8ODPoXe+Qqu2GhnIbQ9x2O+cNm77AoxxKCneBZLEl2evblyhrB+NmVJDm7FoVh/CygX
WzYfDyyZKseFnIYzPix7TxSzjDfDkPHRSI3aoCtE+Ppa4dE/7n1lnKsPXO+heb/TqZ7CFn/m
UVxkita2zQOJCz0qeYxaMwmPtbaO6WhZKT5cwFFX+xv3JqKO9HKYICUnbkpadmz+VgDpXeot
26vGFZy/uhIvX0AzazLdPlFayaI+U0EDMBiWFJzHuIm30wIjF6ZtBEXGkCWTt++BInQvpcVr
F7WQ3W7kZWzexChyGu849z+7WnH05szOndzW5Cqsjg2Olqw8dmRu/WYawatp1cK1JArRAsBL
BZzA9WVyuoGBSn4Kf9Ljs0QdCfuN2vIaKSzui0YaUj/zsDWHaZmTgRpg88CjHyO24pVbBgFw
CB8P09rAwGsatu/Id3+FFq+rfiQj0xyGqVnjbCx8/ZeHQQeWHylI/HAm6w8VW5T5hKQe6rUV
pmhp5tQ0He8RlK/nXfmZ5xN/aehWy9zJ3M+ye9ongkqza/sx+3wMmtnWxaQ0bK3PnE9tA7rj
M08eh+z89oIPtUtD6DqWMoF10lZhdnjr6Dakph4vjKbqYQKtOXRmJjtYqnDnxn9USxiWwwgP
gQyFRYoX3PWjffJZoI87Ml3w2YOWHvkP6JZHwyFC+KZDa/nRCCh2QNWZuXrJW3RNHRidogHW
lwHqH1LO3jnebS1chdJHZQ0JJWevDyylezT3JHenFgNFDQEjcKu6PJZ0VjdqTw/g/jOgLLjl
A/6ushuQNPBmYT3a/+bihnKTt6E5h/OSp6OCE9uZvHa4ZNHQ4o0y2ScS6ZSaVWZad3R5qw8T
nOboeSYrfRIHfeBi2cTEXJayDZ9kStxnHpRtLRFIZCul3hIlfvT0ucWq8NaqSHLKRreOkDUh
inJOiMCXDl2JxoHaaq5vVZ9sNcqdzP1Gy1zVhtXuqBppq9btRY8sf3XHn/rKy3eu7qyVqA06
+HANbmD3EJNUPKdFOEZXJc9VGrx/29hBWmIxYl7TVkSD51hqM7uucQfqr641bgfXiOzytxoY
SQFGlnuMvO+E4eHyZRSPGF18u7BM70PgUaxeTGp5uX7qhv2u4V7BIXRTW31mxuZVHEZJaDqN
NuPatXzB5+3O/dxOZJMnsKcpc3AKQMSyJkvlSJJosXWlorbUO0T4nWQ2VsCawz10IlUJzakx
ZampUR0uvKq4uSxgMjFc+TAtQWsB0thRDI+NT7D1x5ZbcPLo1j7zfCedvAU534oa5xC+1tj0
d4cL6XF83S194QAb/Z+JSQNw1+Bjnz54TIMBJGuMfkfSSBDN075+v+iWL3MrbmOi1Z2QKDkJ
O8egkXMtxcAvXAHapiRhDsceMUSeQB0C6X+nPPoUIqgI8xisbiGmQZU5g1bdsP4dGhDd0W8d
9ZkniC79lFtYf2k9vtEpaYXWyufQAHGgGjjdSGjpx0bnFg16pksy+6Wo7MfPPBbErPm6muS0
RWt8ikVOeABKO1yMSdTbr/6Zx1/UlPTD/m/xbzvrWR6B2ysPPxQsVcr6JRW7H4866XKkxqoK
b+yfGW1FuBPBzgm1swdK1yUQicf6M5xuv8tbUlDxSQeUR6nNz52kIWe8rn+vsxXrvhnPYUL+
va70DMVBZtI4Pji9QXIx7Unb02jiE5vWSKQH7jPPPUnhD/gY5ZoXTFoYkCShpnnu2tnkxYZU
nO/xKCbqEaf+MnSrSa5k7tevKHhWivcUI6Ak0e0q4axE3rhOcBo06txiD/5+rGMVEtfffmo/
7y/93eSZghk1ZpSro3Vmi7BMHadLQdA7wW+I3HDlxn9I6fBM/yvNmZrsqdhXLoXAtAB9ic2L
CDNgJAUj+eXwB3x9v2DozqFsb/wF6MSy1oMKWytFFyahclGqUL/V32qNmHN/TN4C6++3RAf/
YGV0Kfd9Qq5HevbYiqaRayVpfua1UchJ67x6LaNV36nA8+l9W8FmZRToWkq4eSIk6wHSOPqa
DafvUJsboFGpPHLzkTIPPuOKr4nK7LDsb6mtPzJJwHLMfYxtnnNZC/2aWbRv2VqwdOr9nudb
DXIlcx99bwt2u19RmmBL8MG+uQuTgs3a2T+ddij3rIpYlotr5xCCHuXqgn99JfX+VmWRaqEQ
7U78Q2ggQCnAil7EYbeFlYNfTyuSwL2l+wUN6szEDJYj52rDVnfuz7bGG7/UYiQteVVWu2Pc
x7VOc0oahx63RMuP4NAkds/oGh3q2Lf70Zgv8c1prUpxH9fWdkfTto/eunb2J7vi3eR62hQ7
YmAhh76OrItpdkm43iwo8btSpuzYFtdSTVmgLTugFMMcymBPc1KWPVSaA4/+Xi6vHRTb9P4p
Mst6pTwnD5pq2EuxRFBQYyM3vn++fe+5fjHzdcUHMzSjU7SxM3fwBl3ma2bCjAuoONSZZcI0
gH62qVNB9dbtCStq3TiHYmPxtXFM/l4Wa3l7DX+2D/8/9g3+/d63aJZeKt4Ek1e2bWElXi2K
NwgiMlCXGkIsoLKiHhv8A6Tre4Jm7kR1S1rZ665+WlfxZnpOuyUBuA7zleO0GLDYOdbtDU1D
77e0Q+xnF/rhc2i64QboUodX4wRrOFXNjUo0DhRJsaw/EN6u6mVXM1i81l0g+wxKM9GUxFRu
KKhAUn9CRqtURkjIbcXKyckwI+hdnuvCE6SfXSH6GjHOLE1wlmRi0Z9S1Mw5pUhPrDjRKqlr
mQIz+erhgdc/aYLUTOJzf4GJthHOPlX6Uor0CBXH63R+q1GuZK5nwzOCp2zillr7VA9qwzV8
yzNZ0o7X/ztO3ylNZSLjkvm1FsJoWt5T7jPeNsUD2OKRno5FXU/aCBSbqoZYtwIbVe9t5wrR
X19JtLyz0PBd3YjpnQnGiZ/qO7QsAFGwVVixp8dICfsnEmyQP9XjSp4VXSpzJlqvzh2sVRyX
HsZhqo514nSU2k1NFvQJ3bGT29rV8NpA4MX4mArhe4MBFAMgS8njlosXmAVKitY+gXx0L4d9
/4cAY3gaCZEOxL9qF+mDQ5TAH/NMQ46BTJT9zXrXJq0d+0PtD20FK9cLisWHeHpcqYWd8WtH
yJsSMOPmRh9Bjnp1vlC2suGHC0KRpEJFPuSR0du+EXWdPpj3kqS2p24Ow92ZEchpjylO9UDC
VoPcyVzXsvLKBoTCYYhrCSYnoYQTMw6bYRYpIoueKrS6CPb0W6W2TBNqvmrckc88fr4ovmvU
J8xCmYaHiUnQIdO6SH2pB4Oh3OH5q2vxm3m/J/+Udb1vpACYM5Nv1eWO45T0UaP+4FSthFTm
E6q/B3+sBGGuD/n+8ik6AeInsRgIXWvzj1z5McHWiErH9E1+77RzH7c1me5WGp/Fu8JlgN4A
u2HAOE1yMwnbrkcB03Ei07ffnQiJD6JYtHCYs38rrVNTH1zWU0gClEc0p9RyzqpVm8MuffXA
JvIcfYotloeXIxH6AnTLpNcsafu9nCjR7OCUgy26d3rk8Y3wa/vbEgj+1E/s4jm5Tj0iMoeZ
AvnMY2rQxyAZ6vffpbLvB39lk6vbwPU0+l+9FhCPzoT3l5hvibYgC3wO84zWIBOLOd2z2SsW
iQoVHnxRERkPAw4KDBLh5y4BN0T2tITQaJjTpPhZSNHe/yPRIR6x9s4uA3xI6NoB9xZh7Xu+
vtk5OCp6U3p1RO9cQPBRD6EYydZLWY3FJPQQJCrrKoPYeRK0UIyrrSHRWBPEoxl9XD2V/0lp
WxF5HqPW5zY3Ykffo8QWogYQjmNgaDsV4X8vj9aEJP1yeKM/b3zzV79YvG+ZIWi9Deankw/l
sE49s8+cTmDxZl9OTp4WYRzbQijAwyOj2W7YeILgkYxNzfzC1W6MON+m1/C2rs/+erri+XYc
KQzjKnMS9JKalmhMMeEvB9UaA8H+TgoNftN6fhl9Hz78Tz79299xndS2Z2kCktPu+LQH9bLu
fXQKolfmM0+YyLy5TVVz5LJjeWNw37nSn1yKPg1jfKGFUJd8VcSX9jK6fhyFmmQWqyFgAulb
clLq34L5+/znz8H5JCiD9L4VngORHoVPKauD0EE5WOwsZzEDmg3DrMpMXX1TrC/mE7g849Vj
adyRRZ1OcFokfuYxR5bsPbNzR8XUu2RHo3+TtYLZ/1a7u4zpPiHSj+rON3Z6AP5no3yPZrOg
IdqBMr028pwjPJYQtWMhXxE1v27zdB1lOXw/+bHLaNhaXuxKNTChQrmZk60PZ3IyXOLI1E1N
UoU9QVB1q02BkIAnYytHtDPs/quXPEaM1H6zwLIRZ+krqUPoUohEW3QIJC3DHn5MYvQ57BAp
/Gey97rkQJmr6cHW26mZiNp2j4i8FDaad+3tVqPcyFyH2MVud8lbvSPcr2JVwif9opfxzU0d
CG8aZk+056wtafaB4UJ6u6uLbYLruQkvA/BrqHWx6/tVaE4LybGyzkG+b3c1N2j+BjrCCTkW
YfElRLmBYPGTRjEF4Q9Rw3Eb2Q1tDZX208od3wE/rNnjYyvZGDy6JDr1ERIDFSWzyMgAloi+
IDaHXQUP3bGT25tAQxTkslOhcbN6V0Jv90boWo/U99KSbkOwWBxttd4pCQz2H7lrl0dv3sjW
EHknM44vI2r16+VDc1LdlzbKTyA2OA2dB0x7Co4+/grvK7sihM9IWvMInS7q0HJotbW1LpI0
aVvprHoidbAnSqGtgadI5RpBLJ3c6PzdIkxiZDmsSIOulNgCGYEP3kTXtc6z2D7Y6cULPV+Z
5eYD99Op54Qb8UTjoO+BpfCkKrJWbsATBGTOY4qGWry8FvpHHCoNGot5j9qjQfLyUwv5OdbE
cXy4h5ioPst4fPk8N0j++jq8HWV0FzLOo6BuXdIVSB3/tNrjMxYxrWl5SYyaE4F0q0bzmgcd
Wjxy0/YT7BDhRATuevdZ9oIRwfx2v+1a55DE3Z27uK0lKM/h+tEwGKR7vWfWzYikru7r7Qw1
X47ryW7Op5g3VAHZoTZGl8vJzvc8nF+6cAipsDSdqZxXtshXWFJ7Em2giRP6BP6wFSsYaetK
iLeT+I4Q9MxvVlxlQhJu2OuklKcGt8IMEIKDeS7nJdgkSECGMDDmUxVDS62lHJwLYUBxBIZT
GTE24LTOTDBYP5ocutUmNzL3g1N74kC+defZt+l6Pe5ga5lO8j0ljjvY/Fs+7DdynDI8CWWq
+KWu4d6Ha26n5U5rlKdl9jNY0pXnCA+hqWUZk5d1v9oVcoPtL6oTGNubZU1HXLOhdWVH5Y6n
+piIebUVApvAZmprfdc/81yTtpe/Nhr+y028z3F8jjXlj+kGstmctkKpI4vVPrtr4+1O/eJ9
9n4Ely503E23/YU7KYq4ysDH+2yUq7pNWC0xU0lAb5CjiGQJOsoFnYqpyoyIQKegOBGgGCpS
jfroUuK56lF3eYUNUbsVMd3WqSBvskGLjHZtQB6i1nc2WCJsIz/kFwnXf1vTycMjqkoJu2tP
W5+YKr86OoaINvmI11WjEaCOQgyNTU4+EJF9Qa1UHh4TWCE0K3Gb7KGwmUi8C01s720Sve1A
hqewnYXyI8QNtt6A7w53Ot8dmjiXw7RmKGfjhgRmqhrfYQMXPhGRCQ4IBEGF+iXhplTNg61c
q5xo2Ogsf7VHHH/tCeeQ/LDfU1a7/r7+rtnLJwO32uRK5j5AgIp7tVKp4D8y4OpXAO6OydU+
mOoy10xxA9YR1IQ53ZreqXK4kmrwGBc2NSg5ghDtFK1hgPjSTyyobwcbQ67A/8eVBDhcfjNn
DDuOOI09qTMnv5zdU04QHk5BHkmwEzViv71zfseIDq8xH06M9iMnUgmZnryKpdynlvLwAqXv
+nSayJ46oujTbOAIJf38TDIww4oUmxIP9uxdPKu1edTDJJyWJCsRPAtyBnvIbWJeupSmi/rO
tRwi5NGwwd83YQb5iaFbsO86vahIO6yb/ztcoa+/XQRxYK8IKDJ5mhpjS5OYMmXreq//8hvg
wLKFnqyw34s3J/LkNnMz+6BFoMmWQ0lT1hyLLRyL2z9K5DoaoD5Ye5lYq/LSuiINpRaQDooB
vQq6+ro+/9CCERVkzPdNpTVbbsP/vshx9HviHzrx49S4IDWndPWYBKwRHpjSKbchspQIOvrh
3o4hqi+T93a11ch2aboZjOwy9W5YGegX7LTu6lfjVdWxDahlOy/ByIefJ57/5yvsygsYdG1O
o8p+t+yNle9g+wfUp3NyA+2FFg8RlBvqHMZ0+LLQAw3tZ8uJaDuiaFeJFvoVxipyQ9OLXpBA
1S/nnEjw2B3faldnOTk2P6G8hK82F/VQeDwd5gJlH9oYLDOklfi6ZCKCrqKPiQ5/FPT+RCsb
GHCRgLEsRmmpGYlQQGl2tH9QRdfBHDavf99Wi9zIXL/19y3P1fS5e2brtXYyU3EYiwFpxO8K
5+bF38BapjdPSn61hOHmwn9VHV5U8KubCS/m22qp98bTwPVOaUlA8xWF1CmXEgKigTKDm9rP
03/bprW6oaUQwBqyzmSpyzSDhdWWq6Z36hIvqiLZriL40CYRF6B46iCCe24FHp4flF6PMN5T
iOB2fCDMzPxOWtNehQ27FnG4422r9R+bzudOPbPe1KOOOj5MjQO6G0rgT6brKQSjlPZsAtRm
KD7y/QIPQ7fg5u336ZHI7YIOq4E5zXQoIpO1K1Xpm0b4stbDnoU1h1sJWnOvp7AaexcQGl1J
/f1gWekVgYi3WwxwJXK7ZRds7LEuL+eDTUgujmemBcAFLkHApgXiLIp5G51//0LRx/zxwNl7
SyySnfTrvQHFYOaqtaPx+8yUtYAx5G8Sc1xh+Rso7YrRqXRdC9A+QwyIFTXUhJE8jTuUMno1
Neqagz/ziJ8zersXOTx9D9LzjK8/j1kpIuEd+yJrlB45X2d5L9dSbZZydHLHXn7LO1l89dnY
4SNhv8scs6otkHDrtyYXMpGvMltfICGNFXvdPS4YBZZNFGtVypa4ED1wnKwk3ZpLrSQO3X+U
shM1Lwf1IEUg9SvgAt5+5dldVZsIgt3AM5eCS5SBDJN8J7pRakvuDTcqa6pdtK16v9hXX+Hm
A7evXCHsSKUZ8eVceV3Pzy1MvE9rfZcC5d082eOem6G6rGV1Mj9wwZmsPDrvjL1taQy0hjd1
nM5GQZ2VDnYxSEdJX4chuAH2F9URbeqsufiufkT+Nvwn1oD60u3XOudQC0/VPbC4Kfvn4sB3
9US3e3P3q8+tgevMYLBf+5obCLGmEclshY63uh926pRA8OqvAStsx9WR3LFnb69Mcc/gwbmi
t7OmtRirpUlVbOHk3RDZ+KQ3i6lqrIYMXHu4j2sDre5oC0QTbGgGEQNqggADDgjjy5pKxfjX
QQ0EjdyaSFuwo3l1QRo0ex4ooVznri92fvX8VjfaOIHb/Qe9TPzOxIo6+uHOktFO1DmfqHWn
9FhNiuxyvGd/JP/4vQSfSxv9Fs295isEGQYZf+czz3wMzDfkpNQfW21xI3ObBydck108gIPN
geuAVzM2pl18vKYV8YlJzpLBw33nGREIH4apGDuB5EQHtmi7OTA7KLSWw2f1Tjv2Lx4LPF/y
f+aVLnaxS0kgOgAlsHgGMzz9qes1WP8G5zQTWX35R7drUuOeZ4/0s/KFoLiDUwUOefO9RetP
GrHyA3m8J796yNw8mH/oOE+jJfJRj/TzoIzI5t0Z3NMk8PAIjnT8cRea6mORkmAMdlZp8VEx
WNPoMiarzV4+3ZL+MBE9MuTS3XmiMCHah6SdSxnNLHVywDqP19a+1Qh5X0Fwu+fxolr5ag+T
pFao8Qw6kUpqphfGGmLX2gj9NrgS3Zh/QPzyUzSrM9wwVj8VwmeBj9Uww06+1k2ks4aInIo7
iMhMnTCndtQq5CjpTSzzfeX3+CjFMkfWhLVpTRiEUzjoPiS9udUWNzK3E+13/pSEmwS0h2np
DC5Pztv12pWaTAAxpsmXFGjhFMxjFPyIesmwXDvGetHLKOJd5Yt+Km4N4TVCsQ20dH3w8S03
UP4OOhajNrkCDCPBEm/iSETqjLby+h7oUpa8OHZETxZkVCvk1l5oV46bS0jHQKb7xtJqrlcR
hjeULdTcPvO8Cn5usuP78A3vfB4BF2JWuyLcU7nOVUhtpOUQgmxNgEbG9aYHFE9yMvISDMhq
i8ckrn2stMZYDoU73Eyb95lKCrGoJqlb+qMdr78jAvX5JY6zFnV3WW99RLuyS4fuPGWNn5Ol
+0yahge3Eh4GTBoVGN70pqGdN+cmG6q/P/xR1ZtKt01hShoSpy26OMWDCqMdWFJB0vKbPpGv
Ak1bDf8rmdspVmyjE6P3OvimVvF+CaeUpt4zCRA1fW3DQ4fJavqg6lTFvtBgTockb5JtqRvQ
+qeVwPQJhGTO0gBD6EczthX/o9B/df2/2+/v9zgV2caCnrCUrhcI9zGPkPlUFpY+82ThJFTa
Vi2zOZG7+FybyiqVo66f8sv9dLEx3RhqNPtpdiSnxhAVIa6zU3/59INOlQeuq214WiyY/HJs
2TYkQ+WHoNu5wSI/HJx/1fDa9FGIU7la6vfm/9MF2ipBAPH0A+mbCo7UAi3WrSGXlSLTMKpS
GtVHs3Ec6TY8nt/Eqn3wdvXEhGdKk8XEh6lbQF+NHma8R5RCyJdq0IMO8tTIvOiEqeYHVee3
XIHXLghWdO2sLXGyp2ogUGk1eL4wVqw2sA73yQpkSRQBp4Xck1XM1GIWJlUx5CZToUjpl1M2
krnuX9KrgKXBU2Ln3xzdYo4rkesopoW2LaDmDE3xoS6oiWZG8QZeCsofg2lxCOnxfCWlP7tO
BKgqHpJMFDVUz5+SNjXLQwR2kCGHejZP3kGGithyheVvoLT7ynjOfTf1+J61eAhgVFDRqNK0
I6VjNndj4vfviB/I2lXvB7XSwe9XEAH848enh5ACngM5EZurqJK9Vjv17lv2+Tw3jKzSDzJS
Wh4lZlMLNdaTupMPWyqxhrDDZ8/6BG4212llr4VOCT1aHXb3jTkCnzJuETGJTHdobvtdQZHD
82BEYnSYEnnw97ZiN9TLPqK+8mYoP6gFJ6Ot9PMzaZjsmr1IIlyFMnMzb+a/Ri+21CFjy/3y
i8Y50c1Xr5ic7ecyJ2Dalf8lYNrICW8SQrfa40LmNty061XAwHjnNDzv4B13y6YBl9V62wa8
RJ4DWWRTLvioMTw5FbKhGN96uPs9oc+2EgZqZLHIvqDGvEj2Hezjq+e5QPK3UBHmlCiW72IM
D9GiJb0bz50pJExBpSvylL1uGayLQBX7+H0XrtDFHN3JIa72qmHZrDMditRpZIpTxGce68e2
oTv1cd/GQvXi/EzDYotN+9nQhB7uyUh4eL4c8d/xuQvXE4ZfVd5EpD183UfPJzDv0uvykjlJ
8kprzycY0Tosuoyztla4hQEZib1bhi2zLIBMWCUnmulNmoG/0Dx8hXx808XryBrqaYbSnUNP
z/mY+DR1ujrSVmGMLNLAIGvgsXnIJRZC9vLIqJJpuS3IjlCkKbXXTB+dl/apWzprjR7AYfTq
+8ogFx+4HqhPdShQCbd5AL5o+oi6s4ijg6UoQpSer69djXr0U9YA/3MPe7TZS4/E6n02Xmw1
TyemFaQidxKq0taTd4G+bVhcIP9fUdGpSQWe3ixs0hcvemYTfHrTrqHL1SqLmWeyfwytp/c2
Ryi2NFcyRPtwciKF6g1AZQ+QZeh16zblFUqg2V07J0T8hn0Wjxilk/xzw7s+mVo6xUwkhM+3
nl8MoXbpkriht1HNmY7182EQZfzEqqwubRdFYh0Se4ORcz9e1hRoHWxoDto8GO05s2szdMvN
5l1Z3Kek8xSVgLlFFrNqLIREx+u1cHLtORs3TsEfOUlrqnUU92gJDz1RX+52o0OD1DmeQQbS
Ss5qyUWuVki7y4xpbHvHze2Gao/C+GjJnU5iS6cXVSkKc+HDQrle9vS8OhhlvsR+48ApjpDg
81lwldlz7zMP1MD4UjS+KFe/aGWwdsCasHJ0pG+Lm39rUc9plHy8c6kzNwuCqc7SF9hUNmPV
+YyjHacePNKxHtf+4+xQfw/JN3Cv/xMoe9mRmZOueiIbSUBHsnlDzu/U8284ZeL5zpeS5OY4
YfsEnn51URgcIIR5OS6ODrkGsXo6S2pYJmpyKA39hgXv3WLFQc9cee1oH20nNP/xJCQvsN1p
CUyydOwneJSwL7z8KsTEm7E2a3SgNJ6iWeeXvKooGaj/ioW8RGDol6eFSF3efmUat6Nw35r3
yaZ0xwy4AiXamI71WKBbu6B1/9/jc6pefgCC73xy8oKDQ3cdQTq7EJ7m1dARweJZCt3pjf+r
fY9PTyq97typ0WXHO12wVL1LbteoggGYJsawpbuc3uH8PzRkdor4m3ZBY63+Pgy9iWG+6FQ7
YEle9BFL7RsRyRt6P8rkoIP3vK5d52ltZXTO+3RWoqcAWtkY9avNhWlI8zUJZUsxsr70qf1X
B3sJiQ4MYGomzvdO1FjyEic3+TLgq8fW1nDj5JE0UEbGsS408ObyT21kvJL2T3FkCXifo13q
4Djbu3nteSVLW6c1B+Mw7kcxtPCYNAumN6S6YJOxigOPgx9v89Zwu38/PDtQGTNwwIyFALag
lWIvRhdmLc3XWYxRHCVRjHaebzhc3ibg///V22JX8ITSp10Qsz5rcsmopn9genaW/fTyc0mh
nV78m3Y07gx5VkzQNKf3R+FpVl2T5GZ02queTMcysOGaGO0LdYLdBbSKzbKCyczwxCObfK1s
nJJl96qek0HtMvKIpxAFvLl6S/qreOae8xPyLz599C+pbSs0ANnhizQmJwpl0di0FS3djdwo
xz5+whw+z55eVnQvC9JUOfjG08cu2ldulGy3KJZ/WN+1n69ou3eC6123c8NDhnqIt+yHRakT
mSUdZyolCSHngKWaLu9wy0XvNKS2e+G/rr76YCsFVBMXtLyUHwt3yNX1cZx4Uqfnjy29OxzU
nT8VdqEAsP7HP9oMb9uNb5rq+E6V/Urt1NKW0K54X5/1tpCwLPPqlQ2Giq4HNrnLivFU6KUh
0uS954A1+y+qONYP9A0zE4QBa2bRaSEyvdPKZvrfHSvZiviEep4QvSC68owlKYcgjLjxUVNZ
p5Tk7/QM1gkHye4epsw+gC18pJ/VTfpd77CTk6WYXV1dK3m0aIWTbf2uEK5fRXt+8Kst+Vbj
/0Lm8vCcd+Jd+SUtAD06gZpmDoaAFuV0w/QBWmrQrrMj/UnY8TQ8JS17uAtsZ4UlBfiAGfOL
CDJdcieUtP8C5//2r0X3U9RNKu+3Kf4wbUvoo7UQXt7qRqExQ3bKIvpuhiE/qCZAoV4whL1R
pyulH4S6j0w0bigUo6HzPvN4yf6P4UIuPPqmCZE3HR6ilZub1moqrhFt3gyKL1GBFspaavUc
9lx2e6csmPVotDJvLj4hizF3id6T+igd1jRKgLwOzPjMAxp+A2Pf/yqKymvd46ZV/rpCbKYr
ACib4WITpnoNnQ999trtsNqmkewPunuz4kbK8+ZiQ66QRIQJvk5ZGJtpvQAlPDKhl/UGyr5/
9i0XDm9V4XYulLoYo7N4xPK3tF5Pev5bjBEt9WkQ2Hfe8DUssXlzQTT9o+X5WOd0ADG7RV3/
aFGs5XVkTr8DBbn5YW/f1sv9vWXR+51G17JMRwZFVFIRJq84ryoshpZcmQCbtg61CVcqTdxw
fBp8cJxoeU53BSH7c3lAPnz4prhTDnstrPDtDl3/loMdHlFTChnKaRnYTFkMQCz3SIon4Uz9
l1zwZzJMN68fRLyYYpIS37Bz32AjowOcctDQJ6YhACuLfBvcwOKPslK7WkO3gOYVXK1x9e9a
OY+zQDvpp5S3o8c9aVROwKbCPqf3hF6fTmWmABOjGn7uejdktCIxtw+KAhWDozgN1Qo2+qy2
Wtpi9F+KXO5P+LLPVjdnCSbKnOrNQxjayNoUztCrSQZB1Odi9u1u4mnrlKkji6DeDpqEzrA6
y3j0F/Iy9jHE719e9m/3H+jgYmtlevCvWpcGMjaVdJ3aw40RMmIx9NTRqVs39soNgayyIENr
v6UUWfYb5hZEhveOD9Z2c7I6en/x/Wp/uQ3Hv+ltvitDh84yNZtFhiN6y5YoS5QNVUJBr8gJ
HEp24W7Q24DVY3DsDJtSK53Q13Yfx0IEvGwr6He4TSMITy014wYe297cilRe4gbrgLz9UHjk
J78iP8u7Dn3O/qSlzPoXsQHEtasndouNxZZ5nPJ7Xwu8D8Q61eOL706I0VEAzf7bZpxO8uPG
zl36jLcq213Hcfs2P6KDhOFdGVdKMCjT4OWiybsHFPEJaQ61G03PH2z84HVVdVY9khZ3Z9pC
6OHDh2IIsxA57Ij++8EB/vLQrU7+reU9GRMJYYblzmGlz4ya7Ou67hpvXPPm5CD+9viaydMV
z8R3bUJyuASIxYlOZePmZRYN3JSMfKDAq3R+h15/03QpltAlCO1KKjhjVT6QE6WRa3/jIxbp
4HyiBVfQS1+Utpd6cHLhcU9I8/TZVZkEKgIeJGH+Ee3YIrM/sonTwGoO5Sfx1UrzS+7ZtXRY
4qaKy5Obs12qd2Pd6sxoI3mXxLqzltsvnxB8qTKKuTAqb/oRnUcmcmqC0EaU1DsYpY0nEuht
us9t6Dsi3QK/5xTxvxglFDDVc94rJiD4df0Lh1EG4WjMxv5TeYZSzh1QvBo8h7Z0PP9TCtKy
xWzGN2sw1Dp5m4D+wuqvg0us9926Gyw6FSLYhBkvzRAMyTvZnb+RLF3zUcQ2y2JokG9X6vpP
7b5CmDDzoJMUiMRaoOUAp+Rru6v+f9yDb8qC49ktOSGBz5tYz7Th/InUuuZSMFBLXaOMKFZv
HWupW6OtigcX/PMyRFf9mZ0ITGyZFV8y6WJ3mcOgSrY4Fiz1dasBwb6uhZigkJ87vKQaHXCS
T3+cvFag55I5LGLcUHd634bXQNddVoYP2yY9UW+3bcebos88qgnDc/feqDGRxSSeD8//4RGX
P7l8ie8SWEyjTDPpGOYhi2BnMKPkECGw8iVG5PT0qkWOoPhY/Mt25wdS57vkUE+berwcjNfc
nYUoZrKDo4P8saFcQvnrq+1hT0CiDQOL7q4zkU/xFQW5BhtXF9aZqIWjQlFnzS2b9KZrIldg
NhMnJhs6cKZVnOPCny/80rdDv77ltJDnu64OxF37nrIn7kbA+jnbenLBoskGaYnzwOqBIWV4
DiXxCzuRKRxCJAqhjWCkRCMQ91youSAZv+jDGhDUAi/mK9S86S0v7sfW6D231osXYz+DFNTv
PeRtbHoH3RLrdBwLaBNICb3zVcSIC5e5fUNDpF29dZTvHfl1jGzZdBs+DTZAuMP2bKjrD2YN
Ch4dq0T3Vg+bQprLjaDe+2fTgzvWvEDhD902lLwfIEK5gPH3UPnuGuUzz0WMxdCEkh5WtzWa
qNE87sx0yiFyauiDHfsFb3jpdbm8+3QORFOzb/oFJgkPJLMuGaYVccpWE0xr92ru1MtvOQjk
8R5V04Up+s/wRSKM9shTdFrbO0+d9I2blYD392RGslZzQp3uSPr3LU0RK9lX3mgPT3i1e3q4
tmhb5qU6l4HOHuqcajZYU5vrG+7bCr+1TVfSzl6I2DXg7ZegNXcXPlE6nDLvg5PDev6Emi04
2i6Ne2JHMJzgUBlbGoM5sQeRkcf+oVst/LmszizZjDTJmR4OIc/t5/+XX95TMJGY3Zu1N8wa
KLbpGTBVmeCBgmPlBVIVB4j29d9Lf0QAMYK/Q7ISgQCMWYdmYCpnJ9pK+rITNf5zDH8XDV6R
VfQgKCQ+To6eimiJTgU0Br9cT6zFTIOPRgH2ezCzQIMKu9ua7AqeMyJWn4DTRdiX+fN36ty3
nPnxnFO1JsQ7kSRyorKJxu3mnK7H0mjep0G+Rs00KuPFc6go+6y1E5iuu7BmqdylAZblnNlZ
vhcod3afC69W/vm/ScMyBHY3B2lpljRg9b7HnxKa2eoH/4FFKE3kueerErypqmvDS6b1S4OV
rKp6jMT7mYG2GroEpCroPcxvxtcBPqH/YiINdq0je1nVgUaUZfKlbDXEhcztAEVOhGPJnLkd
YxBVYSNylXIaDcgmBdSp6Q84D+z+yEx/2dtOlOl/pGDU0lPf4bHeU2Gx9CrRB8XounzsK9+4
gPQXVkGub94pmqCnuTsKlJ47jidMOS2tliwfrxSZAVb05ctE6kw6zjaFsPL3hGQtpZ/tKa8U
TnFCLj223eli8pt23zz7yPOmr1qjm7vEvfJFtHLqGavD4sxk1kovLq9FZAqoLiJ744IX5AT+
WkC4/JqIZNT6iQVOMwXx0aRKl/RrckNG1J6XBz9tfRqidZ2knznceOpOU2cz5Y+YdT8tcEHB
WTF0LG6DtfbLmwojzQmbhCcywuPisChmIf7UPQVHZkH2IsBsBpiDDJUe2mqMC5lbcs2fYLl2
3rSyVhZQD+5bGFvgrgIyxUP8Vxii62pA2R9OLv/eo5Ou/iTjB0cz0zv5Tkx/2f30ABXTntfS
H7hA8TdR0UlLi/FrHLaJsXBC7eU0dAAElMQx/DG7Fs2WfxG70h5++hn8riZO09Sl6dPKkstq
4eFk8Mb4MYk7O3WvTdGE1Yv3kTizfq4njebOLBWKvm+HOWsdl5V4SQ+APGDcmIkSGvYUJTNK
c9C6bU+hEUsX5HRqZn0fPrPs8oMgHp0zpKXlMdIicaAUi9ic7uYY/7wyq0ylNG/TME0/TZ/p
0Rln6m7mv6dI4oDnA/RcKUJYy+o+u1HNOVQENk+efB+xCmMf6sJyOhi+O2mZychH6CaW16F7
K/vXYxndT6wxTGXL8HB7N0JawsyD4K03YFdO6RAzQ8hUUDP1ZFsTrasAbhsxZxR2RtNMRL/X
kkZ/fFUv0Tq9/GI8KzLWMFjM2sckP9qzaSSl442KQVBu4wXl0K3W/lzm8hScX8o7guLScbYi
5ip0WseJQnZ3AuSkTvewZiHIGAneJrsExPlh8sNUcaOxUp/GdjW4vz7QTaBFffkX6bg/B/F3
0TiTL1YE9ZXYS4jrzUPuSTc933FqBAVXcewycuvdFR8AhKHk/DupbBnRhve56hZVy4FSukmf
eUL5d1xnqv7T27h98Lhf/fJf3EPcHmXetG7tx8k9s1l9RXs6e2f2zLIqpZ8Cj05sCFAGC1Mj
55r9s5p4287ihsiR689HWM0yP8JI9jeIpcq3ITXpB5TkFszEFeiWg+e8oyHoQFcAyXfeNJjx
zlb133W3/u+HI/orZ9UOt/6wUtfUwaJFQem6bsYdeaZuqdhkYmzvQH0Em/eYjjRcqVvXMtrG
JHt9wrRDI/0SUpXTvclfa3wtuSjwl8KvXsOW9jYAScomzySkSsMotpoh2k+2LBRlVL/Lcxxs
wAwIUsdIuN62Yed7LoRpP3e0212ahcvqNXB/P521tGiL+k1kbHuDhtuWcdcVzV/TiIHz7pI9
vudOqN1pn6QhX2GGLH4EybqCOa3AVrXqUSYJxUXpJ6ICJe/N3HWsRZgZlrqsn1/9ZXuA/sLa
fJREh2fPYJ8oDQFwGjYSmaP26fA6MyXxkNTcvWpWW+J0fE733Jo3M8XLhz0u8GCnnnxT8JQH
FGIDIXpKxJH2+hq3RXcsPWO2c7hWY1MCiCjfYrC+KB/T62d6cYFfVm0LSltOBRogIPMKCFgv
NFExoKWwAZam9Xu/mnh3nxifL86FlaVBdV41uYNtfO+5BCSKfGEYHr5ZvnkyB/mbtPqHeXf6
+276TaqmAVsSjnkFNW8rUE+AydE/82DJs29PTm7vVnA7Jp2bUCXEspWpARVUuCWCmLqkkATn
EEGqfnnLVV7WOCzM+TcSuvP0w+2h/k9oH54dri89g+jQdWG2r/ScOXcl3zBi3mc2JXGgllPP
/sfOc2Haeo1V7fX3hdhSykWSvwdsgwuR4/Yu3OoQUxvb0DdCgrchtCa63FXoS1jsKSxBdp+Z
54DglQUoheVSRnPup2Plci2dxg894bCN3XJgsGatUBESflvv3HftHUluvfSy392N+I4sXDt0
JiA8uGfT8oiuzEZIOf76UU6MZKMGdiSizIyaYGvYYmT4tuMnTGXGM9iycvO6DBYZIz611RwX
MrdrWfXBchdiaUDCeIk/aBBgVY+dyRqncc4SQLIw4f9T2W48+1YgWAayo7607El7WIMVyuM4
XXbz+Y77035TZgcPv99iAVkZMky+DVM39muGTMAkU5ZySGFJ5g3sZPZ9vgC7cTCzbHamF88k
uJ3wtoXFiwzlnSCfLpN0XmNn/lMrQWnTFnSaRX5jr0TRmo8TqylN1ibNy8A3NQ/00AfroJf/
8Ic9qLGmHOrbkSaLOqK5oXVcY4daNhKe3cghwR3AHyWFcjGktqhwGwNFSd8f9HW+AZFVl8AH
vx4ESP62YS1vNUsxpZK/hadnC5K/iLhvxdNogB3UoegHDb7m1ecu0IlXH2ENnlYeauawn5Vo
SO4U57dNYYcW3Wmd+Dxj79yrw8JgayHCK6ioqVsKFreJnp69xelPkb151ZefVdhS+R1eSVhP
rKcX3QemhlxJCH4WgGHB32kEbsV9ILF0IdomnEO/wr8qhwt4KnBJ+r/p7bzN1JYvXAxS1oSt
Op+zBeDhy/dh1wk4B3skGu3VnMpEEjK/JMwf3Wrrz2UuD3g2jWsNmleyGvetLGzMkkgZrVLO
TqB+SFOXuqZSRlsTOTY+OJh19MOO951/DvQ/rrFv3Vu7DnMgw0SRitY1tFxoqtwfYPej5+Zj
Db7I4Gevbc5qtAW42aCHEAnSVdt9b/zDmW9brl3KeGkTvDQ8lBRlHRSZnFePisz2jdhQ0fLR
M7Qvxx99MbUPvhdhGqMr4cXIO07IgkPUr3P4XVKiz1pMpGyMaXwNWr23ySisWu+F7kUDvHH7
pYRaaPGwRkOBhAeumjVrK/DbPyBz+ZO7PTDvPEHBW8euh6J5AoM/k2w53bxmBhSxHODf40Wo
Iya06e8fz6RTDCM6VeioV8j4s+4iS2TjwKOVb7lE8XdQE1WjIA1XJFrrJ1pZanOOwI+eQb2C
eyjIPl4/KRVKTleJc5F344mZnA6vk/tKvuyM2y1DSoVMdujaN4XIecbhrkUrlLNWA5tiWmiW
96SrB+7LCxCHEWCZ1wbZzfK0hGqezYKKL7rKCoILzYFldJiVqDFCDaJmHjQT/NVTc26ImPcM
L7/snX5NT46i43zI2WIpM00dV2+4I345LtMndNaSgxxySRzibRFtfsC6srozzCqe1sZgiHFa
sv7wU1vWUpLJi1bpGCKmjJnGKXCNXEIHgjm5qYPBY6oaO7zlf8Wv8csvplRjJNIAJ9aNXJq7
rYOYnNih1ZPg88rIJ+tRb1Zs+pYMvVu8u/5YOLAnZ77FXn5yGYUs0d1pgu43HRTyzhKexrq5
u+73dGOgTxBymMSb3mS9Zls8WES2QsCW9xXDSjMmtqYpZA+e3jhQFnvx9h1OQyak07CfllN+
r3HYm63j7gvR3KeQ/yJyyEQP4YGl5WD0MAisTnUgpcKVu5NRbuWgo5XlIhbVXQu2+32B5cBJ
4DXxTkj0kxUcwSMCm5rVExkpyNreE+VyKuyQ6h8GhTeGH4JTAJm5yFxrNqyGZBDycs8fY4VO
aWUUuM7IuWIfGW/3qdXKXahG/q7tofhra6Nl8Ku3aefe3e1xCPm5sVtcLWcuOLUz+DY4qKno
QRNRtsOFcvZivzhQ0zdKK0NAuwZKt+akITB26NS3ncDwnB6tWJpk7Z8tKU6HrI2V5tmlA9Y5
PSQY2N6hsAuBoVNKiKwEO5FxC1zUQOv9S+nqIpMD9HxJx740dVmeY99txXw8C5fXs/J9q1N+
jh+gwnTM2i6rl9NH1UQ7ZM6tZO/DYRu9EUyTxHf4vV3nbtPWJC7kDdv1eN53rl4rr6Ke32ro
T2Uu50f5huuxdukHEoSUnCiWYRIaN2umF9168c4E9tvzQhGlAG12XS0kpGqun4U75G6Jl3iT
k09gR7Dv33v7pwj+PgonruUpoIC5g9VBllVzQ8zUvHNtBPGpQcr6cQVn4/RLSznvRvedVuWc
JBTkDPpz+KY57wmC6fSd0Ks/7MzHb9vk8hzGjZBM86+NhEeXaHanmbkFTlTwq8u+fDZBNlhL
MK5dP0psTZSMLWMYLWlpihm0ohJfO1rKdLS+ivectg29FroV841p6x6dxYzbxY9wGj6FiQWz
r8mWbgCf+XmnfKJH6M02U2CNbtrvm6LjYHC/X7pkrn5lJ1HCnRQSuTtyq5k/l7mcE0UDXjGi
baNnZSIzyD7lkhEbxTWo2u/SP3SJpy6anHZamqM2fHDlZFmNt6Le8ed/5cqfY/hLa2AriMmL
IetPG6MUqz7zLEX1gBHC+rNetSGvZncBFzDNMXmXtQARGfORSbhuVE6v2bv8uSqV89y7JDjn
JN92dMGu45TaYMUlOCAbieGQQAVfmJvX7nxPHnDW9xvza5cJkc62yiI0XD8zldUsyLvgl0Ip
6f7jj0yUPtZXQbqi19WDdxY3Qk4MkC+bV6puC/NzmV/OC5u95ZnUCD9pTB+5GK7ps5lUMgsP
ybINGxj1nH1fny5yVqqapbMWcvld3nIf87F7GQMjFfuL7awvm4W0/cwzo6F8YyHQy9GYb6Zn
PO1dXcm00eFpyMYlKqVSRoNvZHjRcQglo3B3VvBmI2tDyc2pIYRAuHxm80Wn4hOp4yn1sbMo
2mZ+pplpyExStmBVfq6lknlz3RHBKG+fpWBDZrvIpu2B9/GdNUl7HFclHgVeIeqvG9vu0Vsy
DxscWSzt2yhBxdPFGdqjn2ZX/IorFsF8sVBpDy+Yd0idbbHTkBEhvnSsUL+89rWszqhtcySy
lehAMP7M41o2kr90aDeIGW4OatPf5xSCHi+YZVqFJmxsh8OD8/DaTM1YcozI1jbRGRZItK7F
6MhpBwCJfXMZHaz7+96jYzW4IahUDsxPYiISc43R/WnJkUqwUJDuXZiy+P6rQPmetIn4V1aF
+TMhtujkWaJfAONHEIvsVKaTNdWbfRD3SgvnbDYUdutXGlYhV1Xdspa4eCLdSG6ZUc6TtI1B
xEHM5Xvlv/ItWq6e8lemnym0dOnwjlWSlKexEoC9ffc/lAtppE6yNlUnCnvfNjW3u8tTp51i
GjEzM3u3TR/G/fD/j2t+qQvTwLrdwz0q7Q0brqUf9ivQ64DUz3DmzrXQSbu41Fpo4Avb6qi1
1vjSxZNnkbBykgQpJG565oEH11jVu+rgzsSK3nPePZJasfUq8q2YtJI3M6eKAMRcZ+tCoDkD
21MWaGsbMKBrABKtBRlTLDMQFPXTMrQ05xw7jLnNuw/Ep5X9K/p6DV1ovcNYXb5uqULvA/TZ
DYkahsqtumC/tnfvsypJg7jQgEGM6bnUujZZxP3UHloih9oYVI3OjxtmPw5ugpw6O0aSZvaB
P21YDHx0WVs5vyoZcrXCr/DEjMeZK+FhssB4osZ75Kzv+GMPY5XHUgPDtcD1/ajw3k+VeQYc
9jJBw/NrZzYOrRSUC2trK+6fDCbihttWz7w50G1kaOcyzuqfbhUHybStw7I5f3rZYVMuPQf9
+n3khwgSS1oaa3oYQkoIgWb9XCpc5AVjNk+eQq8e63TunrUJZrVVBj8OUoLsm1fQ1x+Bt4hs
oFtTKzbv8i3/uqDxNnM06GJK2nLuhnL6C2AOe1Qrv0zoSlj7gYcWA3pX3Cu9e1HOtS7szpCP
M1VLBauKHixjIyz7RS0sYZJNYmsErUPvr2WPYRonjUafXRh41tbRsTD2mcfhcVCsbpbvcbaa
cEK228ZFwoazVSFncrq5wBf/68LToXxJOU5Rga8qoRBx77ZRSBH2cZANQGlFEi+N65synMbZ
DVPkN6Qi+C12Tg3EGT4v8l6nBeceSQ8iZ1N6OR3aXHQeAjaw91iDK3pS/rsrxiLzzeKr4cdc
/fIUyvXdHZ1b9DpuORoK6x/IwQzwJ4RuGYC78DoMFsI/ULkfvZCKqfmIX29RSWYNJTc2RCfo
D7nPhqUtOHQ4ayfud+YUzS0KLLUVCKsPRTwzVsowzWEMrQOqAFuMcSFyGQI/Dy/y7yrwN6ex
O7EsE6fVqkIPQKmjoE7lQvZL2b2Zdrtt+hTWOtZlVS5Np4no9UZXN+DY12/+wQWAv4vKl9xz
pJhHe+Hcmr/r9GuYuz6WPI+Z4x1uv7qh6dFAKiCt3OlN8W4jWqDuy/6+l59rv5zJ9+0NYK5r
TApzT9Xzr27ZN65bRV90JgipreTQujXa1Q7bSAgMUWjvNS/5eOsHpAb36Rq9yHMVX9Q7zSSr
9fcWPO/9n9NDv1QetL/R1AMtxKwJz5WaLLxtKgdUjo3XNRduJlJ56wKOwbSmZy5GHAlQWglU
ply6S2YZrl8z/5L53Fa7d5t1Y1yuWu2k73rKxUGWTFC9TYgA63Lh1Ripks0fZC9m4qNy5/Cl
qpYGDXG9xELjNmZOrP4u3fWgKv23XD+Qv77iBb03qQbjti/7nAxM18FlXutE1qL73OvPPPuE
RNqP3IgukxpQQPb7uxM0n6UgYfUD7aYz+ve+7krzb51sw+yqiOikLZNxH8XCLvyyVfcbd/Yn
lPKEog3jjt4rdDcU7h+9sxonSmHVRS/hOLUax1ExUohMOMlXNll6tjirMqqtm+JEAaxncGo1
ofJTt8z3Pt2KZPflcdwXpkPWcjxETT0sIWsItKjgfRIWEjD0QNVLoyW5st5VB5dAxfpsrHKY
DuPIKDFjoxrTOh586FYzfypzmfAghuzaaxmtK/tQ58DD/4e7Lw1o6toWDiKioCAyKQhYaEFR
QGSUIcEWpFUGEQLKXFFGAWUIQyDBcpFZtIhMQijUAGEqxRBGAzIpoxgCyJAwhjHMQ0IGvtN7
X/vw3tsnbV+/Vy8/YB3O2muvtc8++6y99hom24n+OhW5g8vqtwlkJnKY++7a/bfjphODJm0x
cJPcCjWjfJQ31m9gkX1S8Pda/D7I9/8Bwl7IbH34sZBvFxirElO8V94qtfQsZriTl8IeSBxS
8baKbg4FY/BaWMDMmI2iFsTRMAj5U1y5YbvlVCWxXVZkanLuaegM/PMeSnMJNuAZ1cGoDWcV
lPvCEFOKKXg9iL9nh+fRhi2SdH7g3RpJFtdEtvPzPX8he4d8HZeBdlcfb7ZOy1+mWTH0++IR
UalLit0qA04d4EvZzmn5mC8yd7LyR6f6YPHFR4iFxHpqcAzyfNPrPmVFU2+CXS4PBjyZVv9m
+Li/u+qC1+Io0cqNqP4kJ9oI7it6dxFGKwSWzZc7+dgbMsuJoy7YG9FKcm2zT8dqHbKOdNtY
9hp8FU2TbTet41mfflQRaty8cMLTZHUbdJRqrcZHallTt8NABu7dzdpJ6oPwLncb8unFt/oL
ZL7p1aa75ty1ghwEPF5OPK49fTe7RSYEUg3kdzyJL7RFFQxatOauXFD4YLcfEYKBSV6ve+0r
3JEaMdn8nAldhKm7Wgh4dTlgr+G0d7KQR41j3eJkbXS2PXUrZlVmpf62426FO7jufwSrQSeN
RcQ4S3u59/fod5WSjzRyrrqLaWgO6wZGwKU74OE3KBNWY6e6mqNevfWPOblUI0mAqjlNNBpA
oUJWRn2GEZPomHtyMG4bxCk3TUTumAPXBmWi1tQ1V+arHm83qLFuTpudWvcjY2jAIuT0SEtP
GCzTyqb4WB9OpdhxycH3XR/rss+dwuG2lurI8+CDtIpqH3k0XnQUtoRO095YHNAOL6Rd6C1B
zihjBseRh/yGG0Tdsympvt7tM+vXMtcDYQtNrcUGfhtLOsceEA3dq2mh4/V8xvn+rQk8VaoI
azhh63KlNq5tqdtEapKzGMdtI/m1z4/oopKXbMmZCoLgQNzg9cpkJ8aWj4I5oy4kWKvb18YU
5brUWhLwVQfzetgGoTcnLWp13ksEujBjHbnyBu65XkiJkY+ubmCLQE3LhGbS4lWWt8ovrC1X
DdzdeEAqHDXkX2Ag5J8OIhEsva0UlrdmkSmz4Bttk6m5ILpqKHtkSyR4dNEdOXn8xbQ/O8e+
1pRcdoL1pGrCo3tLQ4EmjMj16zNlnAlf6+5TUofoTz5pcsgnCUrNX+W/7d9RsjZUQgBT1qns
On4ExLbdGkNNapMY9GPANh9bQYRG6sDFQFLiZCtvSx96kfUG0x7vPkUu+xKc8QAXIluAw1R8
Vu3JQChpi+Hx/Ydj0cebdFaXmp1vQHSITkzib/b0AvEszTnlmgUkhyYWGEOU4msVnBoZZr7c
ivlMoT371yo6qyO6lPhOZc93X7Rw31BsRGSmvv2RIo18gU4F3Bqydk7T2U73NUZVyRkdO0Ip
1Xiwb0O92gAj0wVFZNWOtLT0Cyt155rncKbbGYpUVZvklPkfdHcaTHndWL1Z9KXie2aSnUT/
PbzL7Cpchv4ve6Qp9FHLZECxWcswlcFhx5Wu59JOGJukid3qkHnEFh0bWiRRFL9Lmtwocb9u
5bRgBUp8T6p/z8BH81+ZqSsSimoI4DMQDQWLxr5xb6VudQwGwNlLwqvdUtBYHdcxycjRIJ8N
IDsOiRzdhjNFLgNJf0SP7E7CLLBv4HALyyWd/cl0hc7l4cfDhE11y8gcRzfrTOO0M+PdAU3X
Sp2JmGxpTH6MjtI+7T5bosVmGvoCENc/spgvun663ZAmcZOfpj1rwLq0KsDmvs7J5tt6hLxa
04i813uhYf2BFb2pDwuvasbXgRXdrTPtzOzm22txeeRan7yoqLQFopezy3P9IJf+MJ94wwhd
ff+Q0wNeRaVARZT06EdG3XApGX6rSq9JlamYfIysLPj78PvI89sgNXz/YCN5qNx72RGpxb3j
ahnXKqcWIO2caaOJksjFtXnqzCJYWUH/3OafSHyEl/P2Kc+JVjpDZ4HvRohXAdjbacLS4c4l
vt9USgaYJBc6S7X2ehzPIuRtpNK5qp4DHsK+L7PZEIae/NRDXVh8dafpgdW5kvrY6m9I/MiC
RK9qAamDw/OHhMJ2zDDO8cVD8vFw17lgidYQeTUJbbkjeShnRWtMakIVzyczDhgHQuVY/9GN
giXPWRH/EBuyJepRqoY0mDQMwjvuoPNhcJeKuVBDb8PVyoDUQ+nfm04HDko3G0Mw1ahUI1bb
FV6FCfgeVdKVCsMEoY2lDfQhwDxePjY1GV6j9+HuPxoMv03Niu7kVuRRT6OAJdjFsgDq2QUo
/USBScym9AP3ACBvWPbtM7NOGw2mqEbewt2J5UJ4gNf38IHPEGZ4ON43WgAE/qDdQkAbg1A4
djxumY9qRrpbPL3ptpW4YiWCqrX9JinIvjWHOxVxxMU2s2d8sWgf1ZxqoBWRytR7+17MHSRR
QHkg5O1Buo+28J1FlN29Z7eGUipzveIyjlSiPu3wH6yN3XT+wVVzd9L+jLXbb5Wsf9ar2KE+
V8sx5ARDfM8Q83wlEXFFweMx3MwlyZ7PTGCq35oL6XnPGXlU++bPxP8D/nJfW/0iPMBiMifW
2jNqMeC0k0evKwt6TTQbPP9Njpamc7OcxnV12WJS4YBWfNRWbYmTLfug6C5DMbpyJRBRvROb
hNy3Qpzv2ySAkfuDezUtTlTRkfj613iRs6dzXsbaBC8EeBck2ImOIQ5gjxyk37aD05NIDLhv
e3tIJPGuCqOldKzE3GEi3Cxs51PjBGuqmgGpSN9hDewVSRktJ3ETmcNALlKq8gIs7M+aa6L+
oT1O2k9vD7kW4F+xqtFOpj2LxgHICK7WJd5L8dz3dDTfzOTWx2u7udIeSfbFNmBNvSv4Aney
/ZHDnA/uypnG20TCcy9hUDwqfrbzQQneDaV2kDgh77eRULpEJ6mzcXFwAr2vJHpho64WTjvs
cG1XMnOCn/pvydgkkk1QX1751zwEfyhBCAg0m3n7rnznpHfc0XJqR+tcf9rmPSPDJ+5xvATA
THX4YG+4ebCsv1hm/L18m8y1ybEBPJDUBSpgNf6+d9S+kPP5y7ZnZw/UrCd8hlEd3gZ5O2BC
hmtuMYJ8rRYpF7KWdiXqz0i7/abyElUUF0x1mAZYn+K1cbOcAdz6KbpgtEXLIPSKUrL7180Z
2OehYJnnN2ZoGzd0S/YNK9Purev93Mt/wF9E6OeNtxxvjhsFxPZ64CCHVEBZJika2S26x5WL
Xbp8LXOoz5++Yjq+OborWf/cmTY+pP/25NBxyNDAIUAl81eQ0uDDhFZU3qiCh765NSLmPEm2
qawMQo4+Ga8mNxDVYbHpVkgIPMWyALV2r/+9h9Y1Zc681jiFin5srk8w9p/RcHo9tfS88KtU
GuUCUuyip9iTxIi8QWC6Og3W/jRdlSFxUrvUKP5rnHZ5AoCyR59XTu4SFVI012XcnOl9QTBu
AixNWXALgwIL6wQ1oSblJT2dul0N/seBxIGS1Jsu8VgdbHjKSzSyii65NbNuxFIdJ2M3J3ab
6fpP1dokNRQIsGHLggdrQFk/8ET46XfX+pZ+LPl6olvVvtSnwOoU6i3RaCOFNiKmO9ECzrj8
+MXhm2ZWgTm3ZjS3QYcK3RW6hrMk2nc+DJ6zs0CpLbNnq7FJGcYSuVaDwc6e5msEI9tS8lip
wNKecTq87/QQE6gOO1FJfkksvx+f8dPErfjHxN1J6cPwLgPNDtJXkcba+DzJDQLbS0WjHJyu
PLU4QnRvbFmEc14I+3A/Hw8GJ1hHqprZ6n98ELBEEo4ybeK1n8MF7PPVtRHMv8SEAzlrP0iD
aomKB0YA/kjhJqgq7O1rCe4Kk8O5uCGuuTVir+Lc04dL1ec2kTy9kjCp5Jnb7sfU3RhPRo68
F0YjVNKbyzeZ6Qord4lJwT0qPTt2ekO++ClzYXlJHwiQVeBPVPj8p+nKP/Ev07X1Nz3OXYYC
dd1fQlOwPTmWzbXg4xN3yxdUEbkTE91GIWagN/9JihvgjfUsL9d01sMA7H63giqwYKAdvg3q
+VdF698PsspMi0O2WqXu2sxaBOjNv2h0fyjiDARScegoFx6GpCHOOtnhRoy8a2FVToxLZSVQ
I6Zq+5eKVs8UQ88/fThfGOxSM0Jx35CbNZoVXUAeACU77uQ2r7PC2lg9YIpnvT938se1+MtH
XAZjNQqJAmww4qzxg7TgpmHfb/lEKQ70gmupNATybX+Pz20CY/DOAfWdZD4I73ZmZabDMr7I
f6KwwBqXe/AcutBk8w2EdGjfB+l/TAgHaXelYzamrir4Sq9tLB+/WaJdwxAiFgb2M5L0dluK
5E/dbIK6RM0kFDOkMsDyY+am4aJq8KCfamd5aDgjtMN+ZMdrNXWYPi4y5KnIHDBZ6Tk7vUiF
xkfDF0kPTUZ2Pgco0rZGHOu05HIVTZ6ynBsSOV0ygMmrS3MaQ+Ojjpg+E8kx8f4UriGWVt25
D1aSYNWT2lX7d4fkNzupfBDepc1jXwjtgFdGX4/N7YmNpXGZGGF3ZRYlNIDB3qxQ3Z0O/EFO
/iIIKpOdwwMwFER704we1TAcOBDXhSWla1Sz3uwyCJsDZaLFEih6vZhr+v3Jfd/U/ZNcfywV
KmB809M1Ky1oBpR0FWglOp0sDRxxb7lmyAnWtDQISoHkEvTnB7x8ZmpVp1FPSmu97VO2kkbG
9BF8F77O2slJMbh8y06j4pMGlpcb/bYx0f6MKVb0riJRmS0LPuFTHJeGpRo+pjrwLbbPwPsg
IuTkNeyNr4Ht5yWqXqbeTkIfhHenenHSDtLW1jGUkamc++8Cxmvb411UzuGJF2UNXjN+OMQd
9sFuPiIEoKKUakucVyAN5SWDC4lXnxp0S0lCnHUV63hV7TzcvwokVlyu293uZl+o5tzaRZzc
iwzwwywxXhDIb9/WFPkxWNyLevmGt6T6jGYaKQFWcKy/9+65lRxJqspANdS21L0acS41Go3R
UeJJjY7JlpXlaFr0vzBh3WHPFeKX7cIwrizokzp+o52TqHs1SDhBQ3wW5Xt7Tur1hdkSTICM
EL2iI7jE19Mdn3BUMjYDSpfKoQQWZfiua/teZcJOSH27aGlySYHZvA3q9WLneDsjtE4cl4oJ
dar0H6z+QkkjwtoZV437lGhco3Ow8HIaQuMJwnpykNjYbm4UgNqX5uye2b1SqmL3Sbd68Kh3
jKe5KB3xZq5SYIVoVkxCp6LyBd3hIT78kI5GkkP/ZjZ7WnEbdISbMuatNA/vRvqJIqM5V+9q
JG/oTuOrePGN9+gV6W0MyTWHYS7ymB5zyHiSlRCstPDN4vIJhJfsCrulVnTzQgDtIURDMAjp
RIplZFUzv5RKj67Bly4asN7YsT/l//WeuDHbIFuFTahqsxJIVdw/0EzNuMNn/a4qQ1lAJOc5
y6HyRHzt2dmYoKnRuK61YUtIx+9wad8TF4yfsZgZGpt0NtDNtQA2SbZdOGXRM5tACOYmx6dV
EnP2ENe7Ll6bqGmJy191ULdYhTGQd/Uu770xYaFuPxRP+JSUr3jaLOUIho70+SCeRNd35uIH
oUA8MF1XUI3Hy4fxQrWiYLJ0MylIULLH9mUzGsJ1ovTEb3qxdvc54ZjurD1Ku35MUDebiJmj
Zd8U4iLs67GfQt1XNQoqdieyihNTIVFie39T1391ZCFuonxTm87aXemqGarxrJ/HY1OclPTZ
cXzLEd6ZAbpZRvnzp/2Zy4/CbywiiTZo5FFwyq5E+mdl5uDg3HHNykaEl5qioKN75neVlZoR
j7LedbxCewem1uYRndOTWgLTGIFmKpPRD43n7PhwtuyE9ouJhrPqk60v2Pqc6zbTngVd0zWt
XxO2MnItgALLdbprayqvUekUWA88Xd2FVSH5atrJqqzjoOE26DuHrSVEnNf9FNWuNQcVq4WW
bRC/S5MUUj3LD6ITel5V8Uqg4fd35UzG0AjKqx6cJDjSUoElH2d9Ek1RN56pFDZopTjLScrg
NghUzudb1j7AwfbZGrFhm9w4HU1sBdZY27cvd/ymVb6zE60msKnU1mykv9ZAZYVI1KXIhrxA
npWNpDitqLFu3AVMo1jTyRMIZ4iMQ6+c1AbDgn2V+//zPZ762Ud1XoI+my1AZdVA3eeugwMm
CEJp/k0ns9RHj4QniKlJXh5LJUPFefTLFoaumeTTlMVzfBoE3r6uBqk+NW99yh5T/xb62Ch3
r3XfqDKHkpZtcCPNZcODcCwrSe/fTwces7nLzum2RM/WMR1cueQhXyC+FYx6ze26ptqKjjeM
qwhlW1Mz9swb9qALacwKruKwHXT2iPt7vJ3pOX9m6Lq/Ocmvw+HSTyHbPm5Y8lg15KgW/3cv
SmAb4c2H9hWzlQSV9Nty163y2tFIji8VhHZQ+TC4O7tfiO5qqhji9dCxVd0c8UttteSBpdtE
SJSQ2dsS0wKVTIWIR6aIfs2BZgP7iZlUdTbrFRd9pzAfZuMvjgEUPJ3MbZY6P9Cpbz5I3JJM
fgSxwqJEmUcVUeFaf3MfkuyvKoSOXnQeIJzTZiAkFarwR88/3JVM/7JIbC4tTj9yRTB7WecO
/RRSuwfkX7Be6OkdclDK0P0EvVYw1NuGvOHiyzIUEpH+ry5OwYsCim1c2PV3az95yvd0JmJu
ajRhLg2X7cshVzXOXL4TPqfgsZQSlpyhqHsjRIWhNhP35lLWv+ePS2e9qnumtFlSwoPNn6zi
6dCQVltRlgQNxbd0NfODo9Jq1QMrG0O5X65QPNtvA862seeBoLS/O7y8t5/dX0AUFSvMNKAl
CdmkzWJXpOf14QJi5VJBNJkKaY0vQgY852ocCWiENVs2GiEza2Z/03T0hEjzv2fqV/67u+23
Jv9ZrThX5r4xkxK1QOXw5/5xmey+exGwkkYe7xmOiGMhY2PklMVZXVw+OSGfpDDIPiz69Fc6
/Dj/fYq/sPjMNcogsNR4W8wPgxerB2XkUa+5nq/kBtdkWlVAHsFKeKrTeb2JFgxfrdAHgPOS
xO6qfPyzLYhTl6m99am1FF4NbxT++U+jFSbhzvIQtyFzcncPRIG99ck2vZusVMDDxayJKyrs
H+PJYz9nN/fkHZCrzdb7SxfOXK2vg+k0py1K0fTTuq8Wfqs3DYeFhE+pW47FCMnbW2EoNLin
qye78BjzB/9kg1iSUlp8m5fLml1EhpEhThmV2zX20M7xH1z847eWIEpXPsMlsVjha6JphMjG
JPMF2bKRECzHvHYalW2PVdfcfLGxGETNeC6ngSulN3vpSlFBlWd3kvggvEtdjHh8wErIp6T5
PGqW+45hSy45DMp9UVsAni5xY6JlWlzuSqUUkyQMecxb/sEePyYEoWe9mUNmHSYDGIjpDz+4
owYPfQ45rKCdONeNTJLktxKk9A98JuUR4Y5q5CPvSq5ja+Ml3WJDmVt+W5+HuZ4BcWSyJVhH
FPjJaWT0he9+IqHHh0Vg44sW74VPU/WlNLK9i+bg7PYFZN7YN416/+iDS8m/eL3tNpCpWFHj
e5V7hIyztSFMZZav5ZqJ46ebtshMxcOht4oQgoePrD5rKTS9j3SuVU478GtBBgUvKraMA8q3
QfvVXi2OjDl7BCZSA2ovSpjRDuwNmV7MaxbVIMSrweifYP3PuG7VFpT60s7aa/6Dk3/81kpO
LxCa8Mlv1vY3DIyPLLFaItwLzmPUYbxi6Rbjq3bFA6nU89ri4J7Q63FDYtugE6LOO5t/EN7d
0qrl+/RpVPOkRpyoLDzgnXUTvryp0nScy2bNMuclBeUHHaTA+PyADBKqS3bXPtjlx4SANinX
ChmgKN1yr80tN2ktS2DzayuWjF64dTxustn75HGZWkFy/UC/JbK+ewTxpfZ7x2u/KqcLPBWo
GkwlhWz2zrcupx611jiiRLlpniAA9TdPyCBNqja26xNXkgzdUh6w2/e8wqsXJCXM8sagsNYB
KyOQ/+HKEs+5CUbVBK2/024zxiE6RWqbbktcFouLcUNT1Rdnn/cZqDWpKAvDiqVvyDrh026K
yQE87gXNWc1dGyDRjoIf9FxYDZbdIuHw851TWw9OntH/Lxmublov2pZ3sb4ZD/5CU+L8H1OX
Z+bc7olq8paqQbjbEqqZ+qZzKdeFkXv3X3hbfaU2okuOf5na1Tp1rVd5AYFWrSl4xJjz+4al
t2M0OV7S+nIIFYFqeFWe/KUc80Ex9HECtand5jGMkfWs+FFVrZb3+QF1IeKAvx2/RUPUBuUM
bYE8hhhRurmDyofB3enMfnLgoEf3XveJlLRvLJVPMiCjsmmQk8KE7tOmsU8DyFUl4ZMtA2YJ
5IHl1Cfy7P2iPytzH+7/Y8CQFy9iHzdrRIjOStTgnhsxdIEvPiKafVgwOXffdyum33qJ3Gyy
Yx7SPi3FFPEywL/a+3hXUh0boDi5j3pJBm+y3ywn3XCaCzFsbaz0GQqEms0+XSD2CYCDFn3y
qZS9W8xGRVGkgwKBYZPAXoIo80aQ+9r82L3j26Aa/vbPRwPWV4YhWEC3WORCLsm4j98mwWGy
baWJ9tB4zpg0RLr7+qsoDFVzq0jI3LYxSNqlLnpfTB1g5AVpEbd61XEv9vHnYA+HkKJf4IoW
GSqV7JwYXoH/kkCotre6T6FsG+RYQXrYyW3i93J9dallvcOm+3xY4vBvTJywB79FvJ5Gtxno
y0e7NC0OKa4KUKIJ6/xAMMAMAaJ4lj46Gjqbi4tIyhtghGrIJ7S+b9jmoKuFWPuuPR0Sy6m5
6TSEVaY2WbQjzl4xvDzX7ZT54BiQIUq+wOrvTjOMlUMcu3oGPyPtLmZpf1MP/kqGxqOFkzf1
2wMDqxCQxG1QbP6NQeYPnxdHVjyy3xorDvB+45dxrg9JJNVCHvLuPi/Az5z8lf8Ka/dJN5oX
LcFP46ZTqibxWKDcxskjg89q7UWla1QTnmU4Q7qOoRb3Fu5KiL+gLvM3loNfRc/58x1taXBm
3FCws4UploShBmyDxHhyJ76Axks9BR+Z7LDnjxuq6K/dBtkvegBJl1zrdsorVefS9rDq9Lsh
2p1FY7xFU6BNpJIRxqVLDXqDlYC/8htTOO9Od5FOtsAwJQ0qEk0JxBxDOpkPeVg64AsbZcvc
ZqMHZGWnCzlUTCewS/rdRXt2CviXgXny59L1DTp5rKiEivExujh76RJfUkCNt0w1D7Dvy5rw
EEI+XXFnZl123A3L/3KkdmxxlNwt/YZFL9q6KXYYIPH/W4vYn0i0ElNa0cYrtgesq5skwMC5
oaZiQFa5sz7PAhpXDevnXgi1hONhzHaW6bci2uHvm0EA3xvd5XSHfNnY6HhJ/vzAjovc3hru
8r0hUIdazIWskd2MyS84u9zmCVQVOsTqJCzGhm6DDNu6gaLET+/OMh9eBN9XZeLE5qiU+ErJ
b7kwYb/Q/Q8AeKrmHt0bV+Xjn83AT9DTSBBk38mGAtqJAPJXOiUWPja4ws3FWTsHKHYh4DUG
37Z3d/4+f8HFMTbUZKl4akWtcU7dqdbC+m0JEu4NbSwuqTT65gE9uD1eO2FItUcWflFxqbvE
iGHP55nP1CPovfeEu56UwlQzn9FThQ3vmcgdX7BdoWsbaDHbgYj635iWeHfVs+7r2vqwTF8/
wLngvaEewdCSACxwcrDC0c3i++EGiTBGyh2h+6hJSLcge6k3icwTZ2jvsfuxX1j22dSY8v8t
RLOLusU3/rqMvB5YBnnIh+xu0yaGZDu0LJJ7bHBmpQsB2ARfmp6J427k3cUyuWfO3GsypIAa
k4eDmnkjHYm2jQExThOI7ySmBh6sCizVncYldWYdvzkp5zxbLRUp7uHsfk3rRa5WESONJAmd
6yGlW1IDVTuexpoJ0dTzMwmCupSQF43cvghPB1XAuYufB++OlZqs+4tcxtm+Wb3cKOmp0ZyO
p8XnUKnaV96upanC1Z8bwTduAydhfV5NUIM5nHsa8zTRMBAj89wwseucRDiBL0QyiOaki0bq
Ep1es1rb96LmElabXvIXYkte3thj71exHr3UNd+HVrkgH/bvn4wEb9cTlBhKLsS6OQ1OE/eW
kWEKEXxXODKLkjHNETV+Cl7uS0Asx7IPOrREFJZWzapz13mPkktXWgL3Lf8DJK3Iab/RRYZW
YVc6LhJB0u9arA7/ja6ou3PB2HNg/XHnutwpTU0WIxgXONOrS+qnW0HCuXmm42NH7nhHpQ7j
DYZ6PQNYFxUE6Y4//vTd/Y/54bBj3S4MtK2Zf5pJ/m5RG8Ye5JZHfiplmF3ka3VaG52ayebb
BnVS12UmYKht0Nze7d1J/uFvRYgnuQyWfFh9wbmbrO1h1Ldm/HmaWyth/Yz1OeUFmpqBBc3C
SlBQlWispk8fuyGrbaQfXkBdud5qjDmFM1XU0U1BaxtGZI0TIQc7dCckHTq/brXa0LyzuAmJ
3wY95p86O3macVwzgIEC3DFauVdTfJJYD45rs7rGkZOc9Pbzl9gtfBLsqWX8yj0m5fgzpFMk
IKYvjUzXY/vyXcWXNkQiK5nezCzk+chTDv2jDfghtgb7CuRpw+OS+Tuj5AWkOJALQup/7JSf
tybJ51GwdBrdZ5RpoGZgNuJqeWqlpdIoICGfwnXuDyXm4swLqm+Jy7QIbPBywnvGFw0xbE9j
ESece8S+L/VRuo6D6RAJwoYNoI2dT4sT8E4vrf2iS1SQ2r1Sdt7af5o6sdKHHusjb9a9McCM
UTGK5pTiFAz48G8rbLrLtwzYaQN1q9ZwWLeNTbYQEPyMPYyQjO4NkbQLKDb0TifhXBm2x79i
Zl27s5Ppjx4ueYF9rr/S8Lw4VJHZmDtOAFKZDPHzxWjAV7qq51mKW60F44Ql5BAv964k/fB7
9QuZPxitCvJPUL1m5a94nYbL7U/oOgdTrHVOIEJzSVGMHw++Db9qc/mc2qGCHJfGzbgMiNgm
0vslzoh9NtTxl/4B4IqGRfvliqHVZRFqK9w8yduw1nuWsHL6SCqqHJ3lIEvoiDf0cB2IUCGd
e86Ed4PJEV6pTMetrJ0kPgTvTukqQWD74D6EsvlNetFqvFVTLqVlnBuXnSFR6TCcDE5HUAyb
ct1+MlbdC/tQhx/T/f0HetMlq4cw1OrHht82M+srrSo1j62xtrKkRLPtDSPqdNdjyWu6ZA3w
IK8k5FMR+V3J9uFDyV/I/MHwVdAY82pdvNV9m+rLaSEn29+ULVN08fySVcij59iHNJZOX40H
isPr9kqX8KiUFycmAhmwlxWgtPpOvV8YACyKBoD9ZPrllLiG7CnqLBBIetOUSDWGbYPCuVrv
8ELjA4BI0t6xEh61Q89yJvUZCBU+oh17+vzIDhIfBHdnEDmdW1RsGF7nGQmMufHwuDYil4eJ
uAKeMqhxn/fJrygmUl6RUzdPbcpw70Hhjb4J/WC3HxPCfkivOD9RB0WE45BXveLVNytJ6T2I
a1p92SJWkS9Jn41ssnjv3LCjbtW4JbziStqVaAe37vZNx3uZhmqFfqKnKgLEXSD52NEikYsd
3kD9orCfafDdm3JJizn/xchk8Wc2A+YVq1iJG82R9yItTaOwxoxyb7vlZA+qyoj5RV3EJaca
ompL8A3nvP3iHsWSm7F+TQsOz7WK9Q0joFrrszdcZvXfZZKPh7f9Hk/Liw9S/A1+yoTjsuVV
IEUprPuK/ZvP3mnYwsC27tVlZ+2meY9yBvy5EeeZsLcJp5JonZaa562AemzsOiotdas0tz8M
VvHzCPz095RSIVvnOgWvXymwBW6pq4RYbamoA+a3opVHPoorRfWtOf1A8D5EBOUMOfzbgvd3
l2pTOL9383TdKPLgUjU7toQCPOm4wIQ2bmc/eOO6hlzvIow6W9SVb78JN8BATgiG7GT9o4e/
QBRdI0G+7WgJwCHNZ7egXb4voKrsK1rc373wjntDa8gNYHEqfYEfXPdzNlxyfO64G4E/vOf9
O5X3D1T8cJcfmFb6UPjviScE3g2/34vjKwmv/lF1KCRt/cxQUI7YU53Lj7v/7mg4UI2Tq2lB
PlndiJoXFF9VpouxSzW3QbiB3JWHEBWpRyVzggmMUAzyFOf/cI/L5I9puXSoMlTFiI7W5jyt
RoAKGwsTgOuBG6HR+x7S1V7FFZsHQmBy+PAfn8ci3WK9AI+FiZ1Dx6WwXtRYbaiSflndjbmw
0diINWL4m+W5GLFaZ7ierpglH6vJWbq/ZorkdpkpR9b3oxNec/uH7aTwIXiXmm9x8IQzTUyK
+zlQbCxnci65GpEdd5J9WIL11kqqceU6ThH4HD12HyjqipXHID8VPPGhbj+q+/oIzEaIiwxj
9gX5u1uu64D5tXR8+RtlP+WCyYo+U5y4T+invNBdSbRL3fcwZ5FDkZMHfMRxS9uMOzc7uSgh
ANF1jiUV9lP22j+qFXMk222DcpsT8RqySUI05cgCitPGRg0vkUC7l9V5YTXnysT43/rGitn7
SFgnpoT/IPNhwNJO6eS5ixZQIrRnDcbmQI0I12OBLBZeNFEYyXNgnFByNd7q2xfCkwb2ove+
JzUvbnVC5xweHhDb2f5D8O5ODXkwcxkQhfpLoXlDidNvviIlidQ4yDDEXpCzJ+eEgUfkI7O8
x/ZDXX1U9/fnEBUTeB8hZIhrSdMENqwhoXl/zpu3U7fZKtZbHtqIkhggz+zmN327Eupfok9c
8JFI/dgvNim4mYeuej/TeP9wZmb62ZzTMLmsHW84sqceQPpDxY2APpzNE2il4S2IT7/Wh8WF
DhdaU6mB55OdlvesVN2cssrz0Wjg3dRZu9YzHyKyblQls2AOenziZ9Z++ptPqjzabYKrn39B
sgGOTl9sg/KBw9MzR8jPahFS0jVqD1iU1F5gV6RN2QMN29nwQ/Aul8V8rcmhxfT6WIfLHneg
y50o9silzid+gTqxS5SS3JLrqNVyW8SJS++9PR/q+a9+n0O4KtsM2mkQmC7UEhTVPUuTufYy
lREWpcvnHaidHFvBYntzXyyhet0ynNzzrm430vxFpmJymraZU2qx4rUoFn/o3FqIdcQ0F3Gt
rFJ4RakhDfmsrxB45dpQzQfsd8oErELphm13rk5563hpOSM9LshpWdw0WDDcUKtA0cH2pd5D
i3kTULpe8omdrT4E784ikJ9ZsVmj0PRSXILtxGtdMl4ZLfXtgaC3lNTcRybHNh8Ms4266OOq
R/I+1NtHdf/ii++PZhYCdR9h8IAlv3kbvFtGgsPEN4fW9F4tBcY2HbTfBmW7poiCe1mvmFk2
dbuS7YMe9v+g8p6jsq6uUO1tePVGUPI0E3TtJAj0B3MOgQ72rXreqEG4B7Z4TeqiAxbwtoY9
BVdqLUJfh9miLp1JkHgt0o4js00zCgZpq4s/TamsncIV2lcEh9i9CzlJDJFSVM/HOG1u1Nwq
AJzj+KZnBNOPhaS5WWpvrkvWYq5tag/Hol7ucdvZ+oMwhgVHIyV+pC+XxAZet1aA86uEINU3
1dxXZtBUjHxnXNWynNTaV9XCxhbmFvrdygP5mMxVI65fnXp5xRUaTEUg17gofjoYnOOLmy0Z
SHi9d3imLHYW/GWFjQvOm5dbfXFwaqKPrpf4Qe4+JgTOrCB6y7qVLPM6bhAfjiseYlyaLlje
UxP86a3A415j+6SQ3bAiUTgiVxEwLiie3ZVo/5w9Zh+cFrD25XMIwgORuqN86XtOzJKZMfbl
usMMnbY1BOgMEBL0R6ObQft8z8++pEt18ovM68OWcBcBLXMpUZh9RQH5PdgFE6RGuA0c2Rsj
LcoWAiqNkU8OvDc7eCbnPKOFlzQcXWAr74aTrBe3arQJdNBE7VEVTNvkFzYtBfjbCsuoGyif
O0vFoYxvD8zuamQ+hMQTMOebOHo3OTIwYxv0+aBGMYxlCb1LB/3ghaKxn00Q/rbBgC09F/MK
rQUqvZz98sSH6H1M9zne6ixcX2ZmL8MeDDM8JS7isVg1xAlLK4PjafkUj4AbcFGYLPT1plvP
WaeVCdGLuxJNpbKzXHFtdBukZXuxV2VtPkPUPAc2AfgItD0ZC9FWc0ivqFQNNFPtM7ZoEoYr
k2tMn8hybOBV+zIhc4tJDEM0UpZz1ThonP2C7vA82GXFEbLzFveByXBbIk5Ok6kwlNapPzlr
XSLgFzfURjBW7Rjs8xf3HyrBKgtIUDC5z/UNsaDuX9wO9nP0lvSWYmuXzoZK5IUTui/3tlTj
XVIRCXVc34QBRjeykZID5CDSllgr+NtzOwPtNcxCvK/6FjVdNpOoUbjaRMY1llpN7nldpTxl
4nBqoAlwm1pRoOZdoy2fLUbuP0DZOZI/FS9xlp/McSFTV8XnxBISTAGPMu6y7KRXmdc0bpU8
I1cmhQQjuBn3HB13NvvdMFqy/Ji91DlxFV78tI10E4lc0NUOmCufrGi7NPpEvNQCEvRjz3ow
3HWUmvmWf3cvf8WGEtqdunjx1oCjblTKO60OB5HPXjP1CrxiCINp8V2SpLrOhNUHmbwFu2Od
g8Ac3erRbGBw9+J7FsLBtrLjLgKanyRW+kuKeZjnzGrn6NWWr/jzmiknJkTDWLF9cpIVKcsB
cj1r3aN05zQPjNuS+5LH97Lky536m7Jbw1v8Kjr6pY+eedpVp1/8DncXg3atLaBYF9RWd88T
ErwqopfwplDdnMkb+Vyvf+HwT1ZIgFQH2LGg8bFQAYnqCTcsqzw1GhInItBtUsws9qrSLWKl
QyQzcoHi8yJ7fmEJAICXDTMM9SnDzgEh/5xIx/YurJTM+n4G6x4QITARaFvrHQIoacBBfTJ4
kFsEOLP533Fr54HOQXXpuUAtY3NHxy1DM67slVveTT6p9VuhtcnfE5fHuiFxErvzEtspzV8Z
BiJ80kLA0MAWKfaFOcKyo/1DqKlBFVPSQ+NgKLixK2Fl/gBTr3qXEggnEjnz+BK/cx1YPF1z
oq2pRy3UpKlDI2C2p0nj9si1Ytn0CpGQZehWfip60v4aVlC1ZSpR5abMNsjkQWZagpR/iMnZ
5fAva2MbjHgzVXhFJjqq0++zhGFLpxJ0nMyVwRIIUx6nuhx8G1HPDsHHJ5IakYCeqXhyV1lZ
wexGU6zIWCysiCAg1G2sPIFOiYqKSvhUn5P0M+vvR7iurV1dL11YfEdxyFnicMwCMkJt/qGw
EpDKNojIh+LOLJZtIXZPjb89e0+36qTdYpvXchmZotFs4CC5Twjx5RlAyf/vn8Pehfb8GPrn
OCQOaeZVq74NqiQNM5AvOUu0pG/RQmTHTLiRbwJE1BbIBc1UOujH/x2PgKvJ1u41iu7lQ6GK
L+sTVlifI48qfPFYTIfPokJbktT0Zmq8HnuC+ua/2fz4IQ6izjtDhKXmaym2npeUoQOXqd+t
yhHfWwXmLJVb7oATRtLXXWNcg2G7kvQ0Kl/UDB5yuqVH80BdkXva5rMt+ZY+/3Z3RnO0fot7
4XUMZMuiJTOPxaNDzkTcF7DKjTTtsEo1du8SDSyLTgIm98FUzHAVBaPkpRMjT/ewnKXntaDz
UqphOmXK6tMo3gZMv11nKtptQDEjNmeadpSmeVTdtbmpqQVrXG2pYGZkbiBkZqRvbqwsICAg
kX1C6vtf2P6Tbb4X7CxK5cQzTU7Yo9jJToa1UvuSYw0n9nitXcKP3pFDjG2y+GFNXeUNpUCF
tKO/MAUAe9Vn++JF6QpDGnDAXbrkmd2m9gTBdJIza0t8KrCDM07MG/lGRfUyC2+bcw41Uu+a
tbPx74a/7yxbp4X0TT9mybbU5TLL1IGJ7v04bynIamQCSefETTHJNyV++N3k/4oNtRrSdILa
JpNjU0qnakvVGEhJVDCHWcZxL9oLr8VuloabuyoyvgVIBP9yV9wLz/UE5BVD9pWqVIjXS9gP
UxmJXrdnt7Ax2Rg/cX/DJ8OClKf50dug6uhFiMLgD190oobCPIYIXmKBRU0eQf0hKi/bMNW4
05V2x7QTZdOmGkqd8WmxyhZGdnhBMh4Om2pYmvtRNDzHdeDi8Nuzzw9xGjUR/Do0JEmykpKf
pXlebynzSkHHwqbR0mluf1/QqQIgVtgvnP/JK/rJxIL7Svn0rj7FDepshuil6oWNUiGE3meR
+mdQ/BFMo4bFLRF8ZAButpQCOSFi+QtbALA/gWjdFT8BD7UaXDtTJIlffaILeby/4U1zSfK4
HXjI8/VaMqPevW5nk98Nfw/+EacD9ny+hXwGBN2jVuLymY7lCPMxt0mX8EfKA06OngtACpde
joGs393FX7Ah573llRZMhXDjbfthJuwtkbqxeWeh7lTZ91yLwp2Kn0lsgwwGgzOkfIYdvuXt
2hX/x4ijlo1vAps6F9JLNYZuOc9oJyBuXu+ZyWZZ2L3CWRq3FqC9DNsMIwduuEfHVAOpbjMJ
HN918H/RXd4ZH46DLSRFo92CnXVrjM6cuWwxUJbgHHMjTaHbQFng7+u05JdR3As7+PiTzShc
x/0jS8eC8MsZeMOBAc8usj2QPvkTreO3aPCA2H7dbdCFjm6vDZZdTQUzzPq9pVo6waJKR9Gg
4hHkK/t4yFSIJtMxRuKQIqxHs8NlpnBaOATqAsQ2ilTtkOX3gzyac4IBzb6hQshLA1WeEDwe
2Btsg9rsIfnnfUftlbxIcjenYQx4irqjxMPf38tfsKUmSvTMVk6ENkEKhxTHYcXAOh4PeUxm
ZOBNvjlZZuQ1T3FoDjPTnfnQfnpX3HfhTjvoa7syRhyYum9cP93R5k8+fLuqcT3WXind+Bxw
Znq7Flyy8rSCqbdgfx9Qh3Ufb7LRU2/1sHo72AEZIPIsMdWvcIJuubjAXMOCNurFkkiVzROH
N7/r1TevqsDFktt8Td8qwljG7SmA9f3Kzsa/Gz5ZVkAkH+u8+J0h8k35RrLhojyqmffpyC2U
+R3TyH5WdWBR0ffdyzesw3zv/O4+/oINOVpoER4t8xJtLrjpNPAtiETaiNCtt99ug2Km4Lds
FrfURUoM6S9YwBpJ3RX3xzYmPaYjPaVCeLdBkVWH9obtaPXnGhJ4TOcMDcM7nMkFMxuKXA6T
75Zp9wYlDmKoyHhVuJ/nO1qu2TYoUMFxB0MgAZd8lqCDNNMkastYGqFgw3dh35YMeSmQ0Hjm
pxMeT7gV4HyoOIS4ovjermwnid8EC0GIxZvxU6Z3gRdYQeZSDjMtDX9S1PNlrL1MRLVWy1ot
p2nOWEs2R2vYbyL7F0fmfj1czvQi9nqGglGJpi1eWVe6LtskmXVZHcpPUGv1T3MZogsA2fxE
fzGk/o/yqFBb+7r5BsA0USAazE/swA7k9324goNPBfdvBsyvKgEm2h+AVeIY4w8lpAIJ5fei
tX3NyuUG+zVV2Hd6ON7VHvKg5i9/SyZce+NOw3T+NL8Cd/ADEijJYz9KLVoxbtLREb9r1xYM
U7QzUxlcrT5WsVlsWm9QlTvCFbpmjMmjCMK7JWqOvUsGMta1u9zYYKzwpuwk9Lthrv3r1rXj
QSRSTwCLm//LHCb5Rkkr19QSmxzdb+PV99btqB/T0pWb/Ls7+Cs2lIq0y2l2DY7HoxtrpWoe
Xgm4nE/tcjhYO+zyhp6FX9oNyxwoL8sXUbDuzTo8DZ715ssdbf5kM/8zBNYPevytpzUjSM7x
a31TYrzhlW1QCOcPwceHqJWB1R4zP/i5vzidilzkKgvbwRbn9/R32PHKi2PrEtUbA2JJSA9n
IIaz0CvGajY3lToYL6Xi+/VkH5iqdX+v4dZV3mc7mv4aiORAFbsFtYzL0iiiCC+JyGbPqe89
q9Zj+6suKiZVnCstdTrS4qFebOZFfJWNOmZcUQkUF4X6qpBuCm7m4A4D+UcP0+426nRsg14E
7KO8auxdVnAa7lXTpmPfZd826lCFwjDolNSVjbBrPw2vlkrqAx/aJ63lSQYkaQ/ixFyqJZrC
RybcSH9HV56HqgbEeNosCq5sygJqtcCoEYzr6+XIQkPl6j5ZthKvX61o5ICd3RgRNm+eN7XB
HqBuhVilz9xubMGB7xjqumSAPbHzMSu+lXFjXJi5zNWj1lSmFpjnNtQAKBMCftI/1fZU99kj
E5PkdtnFV5jU6CWgfHOPayZp+LyZj9zY3ucjVtaHVr+nOM0cr583koCbYPKyKSVZhFnbQQuG
GjHBoqOAsH4q3WH/GcbfdFxHkyU2YOCtUfv5hj6/dMKIFTQ/zWt8iErytMdauVOtpIDq6Bsp
KYuCgp901IFAgUOVXsSq4uHitJPZshgMBm6gLBmUusHBSX8yO1ifecTlFhV8xA21FFuhjMEQ
hwqOScp91VIpaUICS+e/SkHdGAoUpCw/OnEv5PPZgs6LW/iACS86ofyBRJe6bPiz69mnEpyw
g8uwNdNKW868db67QSU9C0S4XCrfp2ZQc5KTlM9kf+4IetivMeQw/7vsVVxH573gdJpOk3cb
1lxZ+VhV01ArQsy74y7g7bwYMexIz3lXqe7pzRCHI92WlcedVHieHqzMHcjeUDU3UFl3x147
45tE+u4pFyWYGl+NdheFlS9XmnayS+1Uh/BWXquzNt0rqRI1L75c8oJFp2ZLa39jGvb+9Ntz
T+uZbRp9ZswA0BANTeKNED1fd41zrXiK6dgTuj1Zshnxpk3uD0P/s9QwOlY+RFdbPgFdZovY
uKDHUnLB6eqcQ1GxQF10VWdOvRPvD9K/v+IEDxWFHqbmLN5DLm1eyHq4A+tPtvsZDQOxkToN
80+LASW/GsZg52rLI08eR31HJQ1OxZTDmaRENHTZvlYqTuQ9z2O+jCkxctwkJE6VYSNzvWCs
sRISJezZbQ33NascH+w/1s2+S6j3d9whyK+A+5/1+KZStZO9QO5psNQ8c5MVUv/mc0++JlFp
xXfoKh1xeuaQAUZ+xXSttaglzeWHK18qzGUrMfuWlRi1keySEz8CgyXgi8r0WVu4SnPz8rt0
dzWAQkEvgO9F+mItrsXckKbcmg1NhzFPUk1n5lISVKFnhZSqN+9PkxnpZiQbgl17r3+tNev6
+cp3AbLVuGLTMpV5fUPXqAfdgAlWQOAw/0XSYHo4bE4z3dd9Ovh+KWbKNvZaheZR4sRNh5IZ
V5y+MdS0J2ovesDuzPk3w9dE1sVrzte/odqh5XEXiwqdrlcrK88PZmMKshHP7hqx9O5mnvSj
Ujb/tnWL6ms/Kun8DO1EUBtue7Oi4K7slfJgFWo5T9RwQ8u0qRkLGBn+uH9YWVkXrW3Eia30
pFyOPl6yLCqKXGKYFdSl5WExMwEeqKuzKaVWwYXDueNLHlFLeamLku1ful7+5vjNd0OIUURE
k2dsIrRDyaZ0lFaQKKkhsq4yMlwKk+mwE24kgBs3oh8sK587Pg/iuJJhFrRM3ASPE4PcRkVw
9orDbwsK+P1mryXDofk3W76lSKgZPjkDFIgaoq76N1l0tRJWRq1HJms0R+UEA/FFSJWhs/1p
vZQutLSXNaH0dK2IG0rNSj5qyZPAwvoKrF+QK9/8CuyrVmPt47vxYugNpliblmFoVwa9u0BL
OCawHD7hDX7ydOr2vNYq9Q5Z8M51HMmDzlvgRK4UoDZhMNmT9pOq7Sw9g1q499ygldXrQQZK
v+utmpE8hWQiAlODKb0rmfHA2RpYdPWkcE80tbbWtZZlhCcGSMlJTmrcJmFtu+2qZjLXiMZm
k9HRUSkpK43fzFbdXCWg2vdFBISHWPZkb7AG+zMh/FeqlYXnrqnC0O4lMz8qbCbwhawTlB2e
3Kjcu/b+BObQkzCrDQ0xZhyaDjnhgCDlNE2LeUpdjnSGBIG23kf9yK84iUmSImoDoVXyCRUH
gfDWhoJ6IJ03sMY3/b3Y9aE9YbsR8CDDB7v2RXnCC65tUMPwvm/0djT6sy1mWusVZSPLuZGV
Ei+8PYZzqD4LwAHFxtrn1YMxx41KyZS1g1rsM9EJrVwvwnZwxZl/viq3YdI8Dth+TkjWQkS4
ZrigazYF9ZSSu4aE2zq0bZBSHWBv/2B6H44WjRIBWlDDbXFrlIAGiTRAS57FpFutZ5h0Clcn
6QekoAuw5sJA0PSn8Dt8caRQQ7ryO/W5p53qM2nPZuE0db/bt+PoxaF5xR3CNgkw96itrFgd
5zmr8rt3z/l17lnCQyDnMLKx1uUTxekiClZr3fHOGEy1JLUNaclxPcRmXPSI5lTtOdw2SAhn
YllZdEvfZhkHNzdINyPXY92HlYWscRJTWNVGw6DU1fb2yINctX4G26A09mfboIAfgJPPCZGr
IBCTTqcF2/OZ5OZNDDY3NpTZMTaLoQOA/T4a0HtQN6SlnUPrXMTTvRzVTG5VLFdqopJhTDfc
YqdkZDzMZUvUGKtiHKONeOKsPYSRWds8jbop4fK8vBj/IuBiYpl6cXrAlV61mjbNo5rlbPd1
BtZA1XxyxfCJUxv4y4QzdI4ssHGQSv9x9LxOiA5Q2Pwy3F1zrbO2hOhd29Yn95x4o709IEcy
dcVAefAlVRhKCqmXDuO6s641IaM3zDC1pKj8TexQoQQhx6ZE++4MDTYWG1z8mbKa3esYmdfH
RMZr/Y0Q0UZQcq2Z5GHzN2cEv+dX3tzgPnqOxl8y1Se2jx1dnWtu53AqvmAg21lWN2q5Nx8T
veGMOVOnGALySz4/5FnZNqWQTog+KjrWW+rE2yOmStduRhibOXfcFZxaksWLK883Ve7zVSLX
JgZTTIxnF4arLfp8Jv2NoVYWXUGpqSvt7YwTj3TiV+Ixq95NKEqAjJyM6YDWoSoVnGSOs0xD
dgfUyKYFqyIoEDxPsDBXmUCnnS54TgMfjNi40xXxFDxC6W7oH1IZSBHbFxthZHCU9oR5rLi4
W9Bn0kHNZ2LjwXqfigVD5cSkI2dWZdXE6n1m/22jeDl7wvIPGs6SusgTAcIieMjL6il0DEUH
dwYKvlTUFUhVUd0oeA5k1Ar2PFTfwBounPck3rMUKc2asieUFUK3LvcWpMlHoZy1W74NIUig
dUYYNYJjmbh68BmqvTyVkdTsPNhT5GwsZOot5SxXX+uMxFa6Y6hdPcUX0BLilnV9a3ESAZfw
okvY4x7XA/ucOuwKHjdZQCXnjb6EOO54AX8qDsu6MoXXtTXe9EPqf72H5ZcWcug0X8KzFpxU
bRjih/dwP/ILjnEf7UGMbtXNY7SZJKvwLqmDctugRnez5ZlUx/d2sb8u5/+ZpdiC32bQriKn
QZtsnOVsvnzTkFFP15IZpjY/+KR/cRVuT0SK2FUws2x3bsZBWjnpXy624o8BLiKvDtVDKIwR
jGQclKbT76HKAr8CvFPaTwHeKVd+Xdx/3BFO6OOcUomQGja2WrLkuBoGAv2LfrjXZBbZVDAk
P8nvZ01YlZO6StK4TQ25lB1SZmIYYakfotm7SCD3p2UJifGKTHfUMT3fNcW/bqZ68Ck63Y67
dNavsjhzeeULRfmYYvN1z350Bapv5qGtK4izebI6oIjoTq3yyK5yTsvHaDeZgQNTNhyPdUxd
/gZGR1KsgpfmTJvTtXRryN+KqcLo1+peoxUHslFeJ2MofUivofD8jfszvTDwXDcOPdz61NPq
QldLzw8lhjNK7yqNW+Vp8mgO9PC9Gr/OT+btqvHPratHvHRPi0KbVzap7iyMl7ng+g35KG4y
l/t6BSn5B02XBnsp62rli7giinufW/Tq1oMm9ZnFdW1KO6N0neNKXQ34oa3Oy4EQ9ADJYpxw
rHrQpqOrGl5Pdy8cH3pq4xew4YYuEHVPKPApuS0IjCNw0IR4p6ltnl6dRjpUsicANkhYj3vQ
PSC7rmbXiIqsb8x2me1C3jwcJ6Y6EWuHr6BfHFV8lmjb55NREB6tZrSZGisUmJKK8sZWcAcA
5Hb8qNB72PDV7sYZNvnLhFWTo0qr+3SOnwkOLbAwHAqD1+3A/OhB7pWQ0hNdKGP5GslATTsI
WwkMBnaLHFlvdiPZ/50tK+9FhTrDe0HEbstTyix3rNaDNTI+LKi4QeEM+emN1sKwzwy5Am90
3k4xtArS96dVXh8/rh+Q2i8eiaP6L1ngL1Zncqu/W2OBO3tOAQllmgCFqXZno38Hc9TTvquX
PLKcK87JHzPI/dWwiGrVgt3LnCtl49JN0EYDX9Pk1ypCBPIQt8M2SDNBDt+/WoanK22Drkl1
yrxe3NCZX2RfBmoU7U/vmUoi2dMut7IvLoziDqhvDPe69d1RHtfgFq+rFilIY8rDN1dNXWn3
rtThiqPwqw6N+IUNqa2ab1r1QMKXezdDoPbfvVwQ669WNi7Qul+ZZIhMS5vFOTcyJfcZNvOU
c82uPR5l3u40fV7kQ0VxygR5HNsaDh2frOHxiLNB7iXEChvOMhgnUutAIHm5Ihz/OGfU0/Nj
EbGQ04Uzx6xlDfxavj3dWCvqurjufG4uautxqJ7lQ6W2Z52bBcE+X5cpOFRrnINR56l8a5ur
BoUxs1gprvQnOSN7S/cemLV6nSBeWTg0KA6JwJ9w4fVydH73mv4ZSnM9cLBPoT1QWQhK0rZJ
OPlJAkV3NZR6GzVYhY/hKvUJfxnaUkey2TDkwfnduFiWdcMelzp7+cW5rrjKRNg8TQ32YJk+
EQTnrAgDga46XNftjij2tUK7BgbkF9dWP//hh5X86EVVh0qkjMxzhkMGCQvZfyJMFf76yUDr
gE7eUs4XHbixlZMDFcdEXamT2QW92WsEiKXslNtW6YkFx/ee9D5EVUYXIqgiA8K0k4d0XAt7
w6cDa8FKEoVYI/D3MD/6i2PUGZzVvc4pXmfkHP3R8shNPdWdp7i/Lt//3YGJ8Gd9Rx4MNvyt
T7dWwzIhZgHCqH+5dXKY2l6+VLbGEJUtib1SD2yX/jsDBSAEZ1FQatnsAxtaScIgPv6dGFVK
kmua63M/f8AbD24HMcWqySObrwGvf9OvS/zLnc+9SjLL2kveyaZuLuyJv+BtJ4Ck4KORw/OQ
9SCux2GgU5yFJiMl1yhjnclqIegIrB9T3m1xIrp4krEKXpxaXtY70a967/ULMtv5/NVRxUfq
TJ5xV7dUjVPUVQ2lcUJwBapg1PZhAOAdwbM2B8XV2rQ1dw49t1kqeLsZWhOci2sfxEc+UgFP
RThH0RyFOnkTplEVp9tGLm4NChNJqsPvZlvhXWnnlM8QBocWE1SWXp35u5rC8ebpm9Wc+geW
5SRLk7m+ZaxCt7qzH7UsApFW9qOXUUhuHFqbFmsOhic1Grqi9skXYM8JcTaBP114cHZZ8M5d
7aBJc+T1oaA+lR/RUSnZ0QWvjauknZ1PZqegY5xqNtApYTApuZDKuZDOu4QLoxuSCosPy0vM
URW+J9Ehx+20hs00tImS7gUrNjmM4JkNafi+uNLl+RtOA41NZQbp6q7o4Wo/cyGCgbJEdkrU
qr4+bJ7f8Zfx/gngBLOMc/E6T01RbHCqFKVGz1WkB4bTR3qAVt/D++gvXKpz48G5U4n3YexE
q7YcZqI0x3eHdyPV/933OP9BRc/GUI10yWB9r9NYZTR7yX/R4CvUFHoYME4wgQDmt1p3FP/b
WRQQ5jhvwkYNkoP2CPAPSDe8ljveUA1CLyRs6vDdVc7fCsXlEzYVAMfYqV3I/YmGVdd1itV8
ohFjk+Ni1r98KYWOEVXUKQ46IRfKbDdzj/Qm3EjwnbBX8N30eKi/5Db4t2svvhsFt76Mos6G
VqMH/h937wHWVLYtjkcQUVEYRcBC8coMKAiIVGnRUcRRigihFwdGqoC0gJQEZSzU6KDSiYIQ
CBJEpAQIAalShRBaQuggJXQIJQn/433v3Qvz9JF75/7+jhM/P9Y5u6y99tlnn7VXBVy4ldsH
Z9mfBYFA99St3AP13zd5U3oYOoVe9aWjfpkpc+UXz+aVPjhDJBOUa9K06alhq3tXbcfJKJVY
uiBbKzBgd1cJZ7MkUj9shmwmrZexuFfyXJucu4zvgY6BabMaTJHEjFNImj9EW88xJGTp+gH9
x20TSRZxdmEJXjhtyBB92m3MaHQQxS+2rZxmr0LucnPmG5jivq6UaiR9gWD5Sv1yiYRkyHyV
4eDyPsPAn+bY02R68U9hwOF9IjrbEu2M9Rg2gECIchQ7u4BcOerdC3MFtQ8Esel4e0j3qkui
gMPFC1115LgIff7jM/bDY3mu4tXWGLWc7pgZ/xUJDFJZmvBM2KjQvi6tHGV3c4/K9I3hRoG8
CHuxmEUjFCwmJnQiZs5AU308VKqmjsCr4ZeGRnMPbH5KQGSUNN5+z4qqXeugWTMveLz7uefo
gCc1hTwfN1f8xq/YNSzuaT0crXjgFSjdD7yomss7gs+yQtOOQKzZ6t9IWr1s66D+qeBzRzc0
OspphjerbqeVlS9Ak3n0NGXMhacYSTdWwSD+3Z8kDoF/KC8LG0plyGAdJDwDy3bjNUf09gdj
/CT8xmh6OKbPS68+y01HYGX7w1nLlL3T9dZ6+d6XYWrmQalNj5XUuD0W0DDkOSLAL/PxLt/x
K9sw+i+AO3WI8+23n659T9BglOmn/68j8A54UYKme7M4bzIeHNE62rfCF0Kagm633PEi/wAp
09al+1XNqOfLAR3h0RDUaw1gFe10JyYVe82ZFw4UzhEzHfW1isfR9tMX7j4sdwzcO4I3mo0T
HVEz6p2eojVTl8udgWEpF/B5Wep53ML7uvQIHCEevp/x3OmgybMAFYfZaMxgh+aBZYi2gdA4
WrSk4YLPXANbmH1qr7osYM3ZpwTku3QAYliW1yiJ6CV5QvOlGhr1ohk1fj34uAiVm0589AO2
FlhD+nfcYR1LI/3dcVlULq+PZpGIDNtm506/+1K+NGrzUvvEQ7TGQU5yfwF/YWw5FUYZ7Yct
tyu2p14gKFiWvUf3KNmIlxhAETHFWktPAQ1GLii/6aJfimOJI/Etc7/7SBN3SEmuM0rkcrts
xqyJSl7XnGbmk4YGE7zhSrHeHYtmp4BdMw7pm708AK/YAL+nzTCf5RQwU44N3NhZ9uHm7TuM
Lzylb/S2PeHx8qwafVICFu01bMCUprOfu84KKV9Pq2nA8LBlKvUNrfl2T6+anJ1wDU0qCiRM
wxPHhJQFAHH2P3/c4lVoNfvdBYn4NNJqODzKgkNs4bfsslEtN8LCqkam3oqCwfIdVkQSW72B
HDu9rxHQ70aDA4cgI83VraeBMHg61QU0au0xE/mxcnKRN/e+yfBVp9AUcVfH6GTbrtAcl2Z4
ETcQToKN1zuwHnUkqiFezvDCsKvO6QYtuFolObtgWqPveBt/wYdRPQwltlr9mu2wTO8H9zGa
CyHRkLl/23+58HPjBsEgX60G7k5cnm/WmxmFV34f427+0uF6or4CDdezoQfg0MmwZ/56cTY2
dt8ff5BopU8TOE42YN6YO40Z97c2SxuxIxOdH4bOyY6hj2Ua+1+4YFWgYMC3FEng0ze8oGm1
ZzuswGM4/gkl1wMtmZyOjgOCR2vXxH2KYRXk5zV/BNngI7Vql431GBX1cvGfL1jMzOuglMQ/
S0/ONFUAdgJyniUvYIxB8Cx4u+vsP5/MJ6jZ55rjdNPoAcCLsOZneLot+49HN1f41q/kJt5H
j1qeVVTXaJ+pQ8182AvEb2Lh9zWVaVcX6xDLhGDPdVBZB761nNPMy3CRMIX0p09fGisrerRx
9O5J4gb9MySo/kK3cAA8qn332TEF6+Cm0nYEiqAA7PiigNGAACs+l7/2WKvbx1q/0ZGbJnMc
vkspOrYOaoTvB7xTOuHjc1wn/i6s0MGqaCn42eVpYmf9plrK38et3RYbLl7ht1PvTOvBR27b
vi2l9IoP57xOnf0uBdPsCnRiKurnDmO4usmSY44xPJPSFvzJ9N3YzYwBbyth71yzi1uDZLh2
NsRMzxt2VuC16UJzJ9aC0vossjXVscoW+GmdFkteHTMMNZM/aR2UliKyv7JyLYlvdbDv0X9H
+N15gxh/30R19ImltRcE4ZSlZTuu7Fct1YUaHujxcazBXdDL0W6Bv4uZ1+5GdT3kOHC3we+Y
a0O4CyD5p0YoQBQVhEQ4jULtAp50RMCKDWRFjE6n4MdtuzmwG2cZcHDsanuAs6DOXll7ESIy
pNz34T9jgrgZyVe8Apb7nZXeq5bRwu1L7xG9VkGbzOC/PDB70tPsZKG3gTMyTOGP8vs3VPx/
7F8kEYYBJJMlvgpg+l444yTIG6mpZ6kxRsM3LUQmcGVsGAiIU3hASkOAp0BdgxIRLzIgyXF4
4QWgYPe01yJcd5plnvODfyfDQmafbbuKSv2aT+N/ibPvLdyt8FklbiamIJ57uOfIfUHdmpwV
irQRLDjapyDJFXAXUQcPeNj3c1y9O69yYXodNIJ/oq2DhdIewO2cY1e1guXmWpyGDYdbNEYX
dAxrxlX9QXF9gEyTMyuJufJDlYbwTFPj1IKDivDFHL84+/cCcjK+haGlrwxCeBeP4dG7u3fc
UXGcVI3njJIWGRy2XX6F86i+iIO/J1WEZy6Sc40rbG7e1bsbim0duRJbesTToBIXX7A8j5fH
yXBaYK34+RWLH7s2qYe9Jfj1HNDng6bFpA1duHD7mCr7q3wRFXqzI2nQdfzw6Cl/moxONTFH
xs52yLmLr7vYJr6tsU4yzYkq3ygrK6vxU8gjh/tiYqqVtBBOwJZjO3T8UHTEvfdwPrcbBnz6
RgjNmJBV/1j+9GRYN/pc0lUTa82TzovzfDi5EzMlOllPoURYxz0j6PcE2vHMqbubYjQABsrU
cRlhETVBPRSJKCtKRwge3rjYNj7ubxQGJB8GGgbpuk0I58BftJbrNxvWfpmor6aShIhY4AGr
7lv2i4l/fwGjv/wClvXO9tq4XlpaCG8ua98tM6ajju3t2kftH59lupZyTX+ZuH+UbCWtFPW5
OvWdxSD4RDzpfFk1mpn5YpBQuNDtiHqHdvuZhrWUr8mFQAO89wn33NqzdPeditJs/ZFf3FMs
+yh5sfyvfZaEBN6ug7gxbdWpIXxEnX2973k9Gn1wXQWuarg+AUUQaLEXb3+4sSEhvs0s1ykW
M1w3HuqYDBiTyckNPXy4dC4B5u5L1DslWOvm+kN/L3rkaTRyXF20ZEX9HELbNMdQaww4o4VF
ieh4PL8lzH8L0KIM4Pcr1uz1OmznSVPMjEgzRZ+YSe6NwB5ofI9ITRNzil06FvvIMcXFhSHn
SG2UdPr4TE03MeVnE8KsFOOHeMWB0BPLJ9KOilw6cK+d94HPEkrBy+2ybImgzsTz/pGqj4gf
bh+cVe44QbMJMxKDpd7aeXqvwNxP1eHCqnP1b5SyEvBC6YOO7W8D7WIzcV5OB98aOC0Qqb6B
GcX7FgocOf2ASc/WfZPgRFgq2C4P2/2zHa1dKT/FWU6iSm5exfUHK0GidV7/L74ITjyyirx6
1UBZKj4ZzP3GXbFjv292tE16bobdzx+VFRqgIbMHIH5AZnlX1d6cGQIYZLpZdsKu3nO+1DxJ
V0yrIHNAa0VMWf7YP573XwIATmfogOyrjS9EmFa9iNmCzWanXyTx68lA0RpYOHOmr3lCZR20
agKakP7ioY7nXim9WMRdax008GYdxH71eHaq9tLoAxuGhaVtCxaEZ0HYu11sfGVCrY7xmyMS
9umQtdgiwHRejmZQKtZBxo9ML4HYVyDyHdoEiKx8AxSwJ9RmVw9Y8yBE1yudMmvqLX+HphDJ
fB2vqMU5es7uIR7YuJyBAApf3BqJOjpj02NAqgjy4ieTzSgt5MOu4ySzp1SwUcsc1f76cFcS
sRPvVIgJHVvNMbxwl4k9MWpv42mdM5tl0VTZunwnbZBweOQeBLYXAtG+AImK4B3GVAHWUj7x
nhp7rVPRz6NAbG9VEgDuvMArIivTo7/cpdxev33RSfIdeTWfrxPTtOPkinQ/CaP21AqjSvCw
sTue5oQaGQkApb82rdHiNn3jrf4+Y1696JRYwl6x+G6NrrAnsIhoSw1uXR11RqhUQzdgMioH
Hbr9kSMvaKc50Thau1TRY5He5ZKlUoKrr4gv8L7pDx2b9lhCWsoeepaBsANcZXuWRiuhkfNX
jxfuj3805aNQqu+TryudExaVOSlU5YGIMnOJS6nuxOr9llDii7ZRuyE7hI6NCR2j8srKEyB/
8w34fjB6l+9EwRiZfLzXz2igYsYRvXiwAw+ujkt5r7OmAMXaZWdYyh4dPct2Zh7c7MaG/bnV
86Zz/IMj1j1L6THV3at2mkqnx4tl50o1bEts9ScbIStAdEBHTEBQcpKae02gJ28l1TzU4lzT
bPf9VOtge2Fy88PyaiBbpq1pGsyuZ5/cop0dGoWDaNe6q2fk5TGmsW9xyDyv4u7InKwb3eXl
lblCEzi/YX2dAzXFcqPI72+P1u4Vmisvo8pFa+xwsdrfZ+y0yBDdL9nm4VK5VNdcLOd5bNJn
blnOA52cxDQBDP2v/z5bejP8araMGvkyc3IAjh78r0ToX3wlv70CQLNZE5Xu2sJA9tIVNju1
fpmYr8fNy2H29tSozt+Dns6ZHfvg0KogMeNmYDxKHNGZkI3S0Z80OGAQIt+cq2BMZf914Yun
4QD1xfnHhXCsKfxO+gGD1syOqtfM/Hb1I79xzX2Z6H+UbMVjgD4y3c6YdKt13UKJ2kwUOAC2
OhLohg8KvgX9xnei+5bmapIyITV1HVq5QmkaZnF2bEG+5eWlx2ZEA+1vTYeQoMzHr643+4am
vMuLcrKziW93vY0xz3y7hFbPCKHKym6rWnBxNiXFYaSLC/Ju9shce4cVyMk9ld1hwwgdbIQI
HI9BAyH51cvFAI0kxhuahnS7kle1mneFPyPUIRPS+noOUwldcu1wrjYGG6FfChqHCi7PO1Yx
FJdCSgqbX12MfqxNwt1LJeWmdRdfqHFMLqxODsFqr8l3KFwIfn7n+9unhlLgno44FwN7EclL
nXEuq7YWZF43wGgVGltTM1MSLUMUKkkySRaTyFx42yYwkZN/sbM/v7lVUbi+9eZYnPC9ECBc
JH/bbSlSsqrW7XkiYHiJzpgjGjYAv1pA2s2E6CgQ5InaOnJCaWJqUaA0jWShM3lNvBNmqMOF
Is8tmjrPPIVEZ4yZPNHx8ToSJacAMGHDCVZMkxgGT0llpcG+q5JDIsWaHd6NBenmxPyp3MTU
UVMGjzjXsWIBB5pkso3tIOctR8Gpec9k0+RqHtkjI2gpQh/hkEpWQyx1qifupYgI1NO6oXq5
AotyxahNJ9BVe5NtiFm9yY3wa5lekAMNgT8FeUMgEEsDS8BwFKI+YucPDDypq3sN4efcaW7u
8NG0uyknwzJMOUZZUQIHY3hOGmjKymn0tj2M5WhdmBkbto0W9A8wG2hMuEn53t4kTtbdAS3d
9eGmsZ5Telr6nPFjQ22CZe2cAa+8vhwvBPLr76InAgnvXwiXwn6AQ93BRPfyF/9YlX8NYKPv
8/3f+T5/kcKvLINDLjcHA7rfLWVwAVK0oc61UDigS4pePnxHM1DCFq+mKjBuMyEcUcuxHPRF
+v5RoKwnsCxToat+czyfh1+x433PjpJ4U28bv1xRAdxEIH13iSpfi3VUyYqaNIXMngI+Pf3Y
egLIHRaShxi+Tp3aOddfHmnxFqen2dfUyLR/vRgeejrXhf64vn62wAFVnoZZEXDVUU953x37
kPMGMBp2jG9Pfe9ObEj3/Nvl3NwchQQntRNV7+dI9e8wgLSaoZ5ZoHFpep/GXstiCK/wWSOa
QNFx15s3S8KZHLP2ek0V6Ax0ezyWamyzWASLJiqeQMdHTXUXiATsoxmN6TRREmHFygGnCd6X
TyS1+PC6Oy4QjIkIIb/QUuWgQKm8Vq2EHp9j8SppHaR4aAiVspSa3Yl5uCwb4G19a3/9HcuD
hfD8XNnFJnU30loRNSMN/6hbs+j1a7v0eYLHQnNksd64Tdva85y92XnQptoPp/IxzR9OyVuK
6Bbwu5+65T6Wa9O479OLuU+YvOYpd5oHDZC7IssrlKZaeVfEk6t14hnlzI3hKXVevfedR6Kl
M7Ceqj+mxVThPAIWLSsy57HTw7Hxnq4ZyJMNd/dPN4WVvHOIFQBe/zW7qXAJ+PlFzfpVKARO
89Ssd2ceEDKNby1OEjSjHxH8vrIhklEiqRql/ZAGsz4Wy9nyoUh7HpVJCfO7//7D28t2NmIj
0L4qTMwq/sOiJbJw17Z3lBCzqoawMwFOg4pCYQcadMh7c0Ig3RMIO1HxY3E2IUA0s3R+jjIr
w2Xeert4I5HdUGmxHTfG1ayMsh5rpLedTukKne6gpKNKfGZOzDhMj6RtI/1+oX3icMTVyFf+
whxOdLrrh2+Ew4FjtNdB1XRBhPMRy3XQle1CLi0GHXpFgdPzOFEU2/jZf2wGQHqJGSX6Umf8
b4FZonIzCnfDVg20YD5LF9ZM/EqAjHfZd9fKNlT+t8FtSVPJIpLNIrzi3cRZcXqU4OF9/3Zf
f8qGwDnasNQ83aoZ6QYb0lsm/eklaoajFsB7j1BW18sLwehNz5R3qPOpe62hKJ+1PvJ/mOer
pkFe9DdTvLkOevjqgHPrfSRXYmMi+MqdzOYVjo/066Wv/yMPxr4gvXJZcHpWIzBLbz+8Nqf8
xdH/SL9/mk4A7kR0ePXXm11LtKYLTObMJkXGl0f5Fa1H5TqEMWuIX+XXTFTa1kHhleugWyrz
ySgM0mutd9RPS5ejLWjDuNnDZ1Wy2e+T3uBTP8yP0pNeX+P8Ca0m7b30liEWC2jghWqBtXJ1
Q4N/H7TPzTjgq/ZfijLwX1FRtjrnszJ6VT3KuAB32mmt4OVhwKSJhd9GBvj/5+A/URNh1oGk
d2bqWapGyMgppbU75asnzKYbRqZwpBGosCVY+MUdQEu8yW7qk9EG3Row2mhOBYw26CYd237C
fZ8+g20hLQaKIdBEpo4h7JTVDAuEb11FrqctSdWzuOo4YGrXacA8F753Z9DWrb6lGs2oHwwG
sYzOvEBFal0mDVg0XCwN/ysumoiJe9aBtHeZ8CsvnSABPq+AINOCtskuGHqFmz+j1NbOImWw
qQpI/dew8VGx33dHj4b2UejFC/H2hpkDVYW7LcZ43SpGZS5njskLXcue1RcJF2BB18rC7OxZ
XjyJ4ExkHq8B9r8y5Dz0lPwRYYdPese/0G8bUkPTvmZ+rGKcGe8x3MGUoLOYvfzrGYZdTXTD
+AzY77lJW0nkUsxGHEPS2EcWLuX1RpDP4kkjilkHAm5DgXiK7s83Pqc+C3jxgDJPZVjPOuh8
t0qVNb9QF4eSF7ygfz4kwrjVJUs3G+sKPiijvLHRvw0fWhi3FeZRs7iKAOwiUXorBQcO70qp
19Zr43z0b/f5Z2zIriEEFicKLsxQRpHv2ucm1kFitY8c1Fga6leTBZ8YzGrs5QoPUAHCBig2
rjLV0INz56Y+PnDG8y1HwQsaXCbNNNQAa6DfuO5sJITTbF7Ov41e4G4tinfje6PQzTzJ1br7
148TbhUjS0WlUU5OEHh4DrD9hG5s9W/De9YWFRGcSbriwPYjoo2ctzoqz+Xk350Mz0OU8Jz6
t7v9Mzbc4e/n7oNrmuZCI9XNIi0B2+vaoUt/egerA8R2IOjcvRpGRASQnjpRB+4SHyXyG/e5
D6sdsKPuurRWh1VvsNBa7srRgk2cr7exIq/8XG71GUAo/1qJx617oi8DFuHlG0CyJy7Eq17N
pKfwgw9K/2e+M4dWx28DGxFZF8GUfgoeeXXKgf1wwElnA2qLNqPM/+yfcTX8u2MC3HTLmhE6
ZgEaPoWWIkw5FZgUWOzcc5ZYyK+nEU9NyotGZ8YyULadKT//3CE8OX5oduUU9+0P472BHVXF
vVdQYwfoPqfhZC6njRPDaejpqI41Hvx+HbSyrVCU3hvAd74lFMEVv9cu+2XXoXmm6T1gJ9rU
ZGPzz8FsSB8esGBd5zgf/JcBt9u5b08VRtCrqynh/gYPrDgO//ozUW6uVLAHfczVt5nrXeg4
VURy3yXpnZ/rCri3A+73XMvVzzdxFSfacvA6/tWumdfu6KXJFrDHtr9WbB3OCM/uUFR3yI7A
VTuDfs+qd0BQmVmVJ3QzO8Pgc2e/MD2bbn89XupyohMKr3DESj3rTrDIqNAFoacfunsD7cON
YdFHfkQNZisxyvK/2zhWb3EliK8g2j0UTg/uSBksw4HQpWGGyxbEqROrlg+Q4OHlfcvl3n0b
m2wFs5YJsXkdZHiJ2mzMG9gj8mH5LF7nWDbPT+8ySTUFYCCMSNlWSL6l8m0TtUhOYaoVkU+P
DDj92BD6PRsrDgKGMOO5s46m1z8cZ4mYr2a2d+2BmRmQwGRpMlC6ogwxR1+hX6da3fei1Q9q
wog4nIjguMgUR9ZGGthRt2uwAyu6g3utKLXtjsuz0lqDHOZeRpH0NtfbS/k7vIBcv14zliYb
22wF71l1BScboP1XrBeAI831L1Q/zo5Wys4Owf+M4/mVa4r0dLkRl9qx0AkVpz3iSf5Cm2/z
NljjhfGdO1HWrV0YuP/R51bRLf2ehIrjzF5j5PzF6/LbWaLq68kjD0S1e4w+aIx8rLeAi0IR
mMaxQKonIGODhnmEJ/UiCfETG/HsBhK2tQZM9syqpbj7lTKKqXsvI/JzAXGSkZKmJB+kYYn6
HhFb8HruIxKadZ7NlnGIozVoQ9stQRYTB9/xSzOdtVhwP4wfy19wApwdlJ8wL8mE2RsPQiMf
eI4tkJ1KVQ2DJ7dE9y1V4KnAGA8sWP442jrQg6RcOq6a2uYzmn3fair3Y8AH62WWSPlqG5f+
qAmJohRfLA9Ea3Z0bINH1GbO3aEw9sraRaiGY/EEt4/8pa0JK/TXZtc3EiLqo5/lLHluKCU0
tjOJ84GPds075G7VmjuPY22q4DzBHpheQ775FkUJpq/6rHGw8J6b3QP2XSGLUMBl8pWA9Mae
toJZzJp+YLzYvsoTW5JJXVXkfmy9whEH/17gaUVxkuqDNTsaPL5lBr08eZX7x63QfVPlGrqT
2IF8TK7PmDw9tFTSm+2+n7k5utSv0NlQ67dQ7zjUpzjnIpHb4EGskPX1ODLNQKvTAfAzKk8x
QEbJQHwqaZlKBBJNXvXSqJpRhlepUXqTJw57A4XpOVD4SX6HjdTszG1j4tkfw8Qh1JaXNTWZ
P9cMbj/8EWH7btD4uzf+sAd5WS29i6bQUUA2dn1ju61g1ji0ZOms/ABrFRVGIF6z5S16HfR+
APyddM2v0QHw3VBAIz0W76+bPVhdcHQ4aCuE31I5O2J29/TDTtVn6yD4h4WAOqakQu3x+tQf
EEJNS3VY0sIeKatRIIkD+MmfP4kD7zg2djzJxycxicH4KfilKU21zyR7rlzOT3RwWY1/gN/Y
rUVJMzMQSL8Y4go/zq+x8THtRBGPpaMeW/1QQ9CNEBkNB9PYjnhpVM4AgcgPzK/BglPG2v2Z
GEYXPcg8fWO7rWAW+Th8JjVboEnRBVh7pKIbcBwGWHrmQTScQdmU0JDP9CA07bF1zQOnc01B
WyH8lso59w8sThvcQvoN+VAH8qdSrasiPM5dFvr+pC/FS14yEX+uJc8MeA9HkHUcG7MbfZnE
r2kQB/K+mPluNDskyVqpFnAsletn8/XSze2bm8a9UQ2gLBRrdfcN6A2zVZRtGP62fUWvfqmK
1KI1ZiBXLlohXDX2aglnv99u+tHZRoLo+z6KVH9RI1iLBEkE/8ZlvaHhluA2pE7NwmVvPbgk
E/nI4eQX6nMIeYflDazgCqwXejLSiMzTdNhR846TscKZwwW/rliuLVMRLyymp/pMH0H/pdPL
F9D9eW73qZX94hcVRP6pbppUSRWyGYV77p68m6ACNp0tGbAF8qoJ5WV0LKvAjwvEsTTor3ey
+CQh9ayeb64cx2UWQcD8Tx+IPORnb7kcSc5xJSF18KfHlt/SeWh3yzfSsW33avGoX1SUpW4N
jJLVsVAsPO381IK5Zx/txVP1iUFLqzaXWiCJ3B2nso2ttoJZ+86+tHqzROd2ke/Gp91s/O+U
Tvm6BvZ4ScEjjCCXaS0Tzk+xPP46P27MSDLDhPx6Fi6GiMt7TeNwn6pGws5dEzpC9W1y9QDY
XP4Pbc7rIKEIQOQZxBLdX3G5TY1fgZ0+Qx4Asn8zcl9TGZgd6uCH/CdarBqhK8ZkYoeeQzE+
F40ar6llaGjQL4l/3EjQUWtTclfVMPhiDi+JGN/L1sCw6rydxzyrkvICc7IlbTZateA3KoOt
A95mgAQ/47qyse1WMIs7ntjii5TykeIfgUxPitvXQc9GtQY4sjyijO/VFXCKA5obITYNKY1a
1etbofumyr21FD375rKrfwKYcvZbWitFyxIPUvjwPJ/E7WP+ooDOJns3oLNpY4mor6b4lMtp
ZlrYzUdXhbWo04X8isGOTqFAcu6wll6utpLnvswenGlRniRl2umk/goo4exGYoJ6HGalf5lD
FUzrQ/bpSq+V4axvU+V4g5FaUaSkxZpysqBMMjdnWD+C11tvtRp3D8HkEUbj73E8C9rYy1Yw
i5KVJ0UEQt+8QT5qLJ8fiGafoLCTfvYtU29iNiHjFjTb2dbBi25ilDLLXvAvId9qcF+7nFN/
/rb1nTrkQfTSklixiPBewP4STQmTB4TvrmcA4Xvifwvfy1gZ6Nc74MZjPDyZl+ZvVO+JZND3
TrwyWQdxPPXoHWLrLbpis4r8DVfgU+BmON6d1+uTD/GCnRVT3kjPUQGzMCJp2PomKRnT4gO/
TjD0d58DX0Xiv+OJapETKR9eCxiGMnh9O9zw47dyUHN3bK5vbL4VzNoXONU1z50U55KlXrLG
ztmq8lCK67e1UtUnmO+MqTcbJZBhhx8CSRZvbYXrWyrfRrAYAeSpae53S5mB0ZkGswMdIuF8
3i1GqvN6RbC0sr/HxECzRNHXMznb0zZvamExEhauUDNWsNSHnI+YseS5XK8h+bgx2Nqt5Y1C
6Dqo6bY889IPm06okqNZ3p2Rpvn3AJMQpdJZJ4AdBN68uY+pbgUnzfOnCW4NRYCmmZ3R9/os
SxPw35UOLZDhF1CGtDn82MqOu2VfaGogYy5ozR4TERVPWrCMdgI+7PY39IbvvscexI1HXlX+
yRrGyM8XEnHWC16+Qwn6Qiff5G32lDMj+HHYVWWsJ951zVyxl6TfxzxlhL8wqccTkzWRCBwx
nkKb4cRRG70htpEyVmj8eiEF2eXIddbhGJvljKe8FBk3S4/RmkS/c9AeqbGZ23z9L5eo/bq5
4NHwssuvN9JhrGVukZ4StMbDhX82NTWLw+s/gIFPivgnj/zQ4GpI4xind5lPa1CFh6736dM+
PtJ7tLHxVjCL66/X/BWcM4ysXE9dFSPVFvQunoEA6w/utfJ+0VhM7XhxLz74xTL+Lc4D+X77
/a1wflPl+wbTLxpnnDk1kEdhlEjtlwrErRkyrx4VuaDtxhMWcKkBOHaQq/MAgaos+BFXMEuk
fcW9r2I26rSCsIxbxI/iJTdcdXRpcLd3dVhwuEAjIUpv5dB7LS7ZEmGKcOzjx0yB04zm+u2/
baSI48ZieXOYP/u9OOt7w7XtCoKRlN6wHCdk/zkS7m+nbHmjwvdE9uDMC71VmdNOHwvoB8UK
NzbfCmZNyCehhOFDcAbeyhQH0uXqorS6KbngJ7uyCFoyxBLETCkNxuSWfuFMVTiJBn+//y/1
+QVpMtOwUcG1o7zTF+jtGrH2dDFUiNYw20EvtZx+NytJgOXhudJKpTEgpPmVo/kzW833p/Kv
Z/JUL4ZN183KcjqcZbk2MmxZC3xXSR0KsFMOqMcNl94Nc/0KtVH1NTfYQSO19DOvqtZupIbP
tEORqq/HcVPToK9hSmVEHYt43MJLsx/cHj32UwT/mWNdPjbg4UNFuN6wq3i9obtA6MV/4cfi
+SNtdciMmn0LBkSeia9o/7icWYGs244dc1NfOdD/0t/gVc3KoPz+/4wR+r8w+P+nVTU1MhSg
Q8Yh+guEFK2VwT37JF/kYVZrDk4zxBTvadUY3WRekvqVpRF8rdMvj5VmbS4COrmSnowuPb7D
qPxl6dWTVZGGhaoXtFzXBM5nU19nQZbLSc83UoHmxhoPZBkE+/bQ82cXJ5AuRntgl36IvmJ2
LFKz0MUQlpRllz1f+gvs6OUPG5ttBbP27YXIWNSp3pixGiWYk+XpBiggGt3+zNSnMBFRQRXU
mLSz/Doo8c3o7N2/lmR5Zyzx4nTYkNvDA+sgbXwKgekF5BvZWfChLpJWCMSF0u1BRHqL0NiI
ZVtN8qfyr8fxrZhnS5yC5uckynXLLtDDcIzsHT1AGNpnZY62TxPMY9RyZsJ2L0CxtjYO/BMI
p3TC5AXGB2jQRpokRDE7vCwGZLjeUpjmh6VfwAsmoqkE+kFxHp3G0/JJPymbhx1Y1hDeYaXn
1pH7Rppp8v3rjc23gln85mZivDWsdkNIqy8RF+/qeKUC+az/1gVYSHDJGafQ+2HZdduLt8L0
TZV/R8vk1woZioeaT69qpL4krYOk8oyH7p7xkqvGhOvKjeg1WGILsrSKtZ14wWNlUv9ZV4cJ
5mOybx+S6/Zt8irP/sK8t9D81KiSOY/JAefD1Ro/TDwT59wdg9URkAiJs0NLRjJdFxr8QfHr
oOYHdQ+WfrpFoOk9oF8XYfnqhFuaQDbyPhjjRAlp2J40gZivesfzKi/7nQ2blVfhYshM82RH
mtw5iaDPP0FByYjVcAe6QG93CbGvmruD6GEXmM2+f9j64aHwHUjlK6jqqHdZsalVGnt+pjJU
RQry+mzNUUDSgI29scX4dTrx9Yyctxsz6C2r7uI/LdqDRcZqM3dvu1GC+Pki53EL0Zx9pHfd
MUr4d+bAAf240MDG9lvBLJrMlE5EPOinYvY5CeHPNbXfpDEsS0yZe4QmWrXEa+Ysn3cD8TTF
273N4cIXiCtnY4O2wvotlbPxLgbWLyqJH8r3X1o0GiCcXMOhMfhazmsL4IoZ5dtVgszeFGez
QIBJS8/xgP/KEcsScf+XIvkiBXbbjBxAugU+8sD/vIdjkWJuqnNh95SQ31Ml9SuwTKhbF5pY
RyVAoINAzPd09PHseuATTdS5yteyEppAAIK3kSUYeW3wR3f+wGVw+urPNfeawXtsS2pGi16t
gLGmQVEMd6Zv4bnFZ3nL2mevNEUL52gcYsQtVDv8cPXzRLOjb+dgFYF0WXy1aMeYTtXgt5Ur
qKFAZlmjg4Lc88GL/A9QP1dCww4+c4EydPaJPBQp2dgPYNPoqV/TNFKjVZ1rfc8K+caL7txC
GnFOKCHliDhDY5fPOQckm4YJom9BHyI0Kj9krt08ArDJ0M6NnWwFs7bNS9pmjcg8eAc7YrfE
4HK/YTa9WuK6DnrEXflxArAIuZqZ24vPULJKtSdPu1bBn+2q3grrN1V+VM9sT3fObf0Pk1rx
cgHXTZEep+Yz6UHupSHKFB52pSV7txafG4pAWm3uBqbJSQeWaPsyl/v35nI0AldHc4VIh4Lb
hRE2Pe+alYF+znazjn7ZbTIqFn6Vy/ZLzoRDz5+e/Twy7rhROQnZM9qDHF1JFP56IjWwVMoL
dlXOX5OvBxMPHYtDY2zibNTm5SbZDd8aHNDX2TeSduyo8KbeXjS9Wn2QeaadvMxYW31wpdWd
0bT8xIL5nYBk3ZSUiVruLcRufFxNZxFHBs2RMFkzwGn/+bF84S6LR6lila7OmcJtOZ/M00oc
C5Y6TeVWjq728E0bez4NbNQ0oEi5TY47rj6eA+sh8ad3/bU8RyRpWTcCsVbdUGY8/OfmKpST
yDRnSvI9DDlv+gij1C3gF/3Z6z8DJi/vNj24L0z4/8nrfmrzR9OiICzPKRxvxZ4eKDUkkio+
jB7BT3RkddNfX+XcK9/Z7ovI87qNehdOdeM8bEuamW7RG9zxYtNQObZ5XypWuj02YKhNC3NP
0RfJO+hJGznnZyFO0PjxVq7dR4Ke21UXhqrA/zAKT4M2td/igsUFV+rXYT5dL/2heKF4mh+J
0GsCAluoFZ0w7n0mRXIb8xmxtBZG3mH2mRzdAt23VZwtnK9EF7ZUNFKCtyhloddgKE5p8HGR
4uRUdax5D8Tffx2kCG7s9v2SndPvqP3s7sZT88pZ5SKldS4PB4dUELwmJT39xeVOMxRvmhQI
+01gsKGOaeqxsZPce41PC5boR+i6BPj1E5UXoTNuumPloeL4+Dwrpdfqsw0829AP0UmKk4dC
5iqrh94xT/GMBvWBFyc7rYu0wYMgpi83+zrIqvHe2suK35VtG89psJbBKlikHIksUSuGoEuO
PL44Wo52QDr5W85dUsc3byuDT3S9xnvFwKvZiZ4xpdY3KQUIH6ByMrX3A5WInbFBM2pncUPC
vazjrB2RjCZfdsyWAbrJ1YFoyjc2NgdrazfHieJ6lY+v/SEee58xWmr81ZxUJTYZm4Ye1Eop
8TfI7KchwgpPHHk2adI0InqvUE5oUNTP4VkaGJJoBz4ov/njLEdsC9ZHGY46h96WJ1KOt7m7
lx4xMVlCMUAOqpzCCWonAy6L5ilK6buKjl+4ADvKSpqUfy4Ge4I7Y3+iQW/dOgg19MWQE9tA
KkR9BY/cPPTD2Bkf5p7mNsTj7gcAPymimuyynBmdNf3JgXbUY5R0faBm6G7lP/v/C0Acrt5F
9aHK6hWvuNdBKa7mtGJYCn868zvBiRQoZ/qKVn3tjL9fsc/4GcCC7GD7Oih4+xhLVH9elcDG
vpjS3FQxrHe2prIBZ9cOXS3LidIsjtJRol7k9q5NLkTEoSoKXDGEoZn0tIBZUNrJiOL0QZdX
e7ugUqvB15rqCa+0IXNM1cMU9frEwU4Ep0SH41JA6YfvERxFbvPiNaWHPpJNOw8WO+E4LRe1
MsTlILNKqMohixzre1p31EutiIElpa6t3G4rCPIAvC3fhzq6DqpgnxfBAvGDMm5OkwAvvvs8
ESWrEE/L10uw4lJvuk7GYbsewum8m125r5Z9jlWrozHkGccZtTxfeT2HpV+EeOrXQTIlP46Y
wyAVkYdIhMz2E+W49Ab7G75hMLEeQ01rqe4A3ATqfed+rc1oduZVJ/FMC7O5y5n2KwJTzx3h
/+MiGD0IPIbIXGFV4Z5VtcNrWvAnxVpwcWQJmz5pjL2Jr+4EVpe/iWqoCYRlFPbnXQdBeWQa
YKO8zNRcvBuYeVAkhtEkzrhiD6PA6ae0Im1WnAbsJYsr2G3dddtj3Qza3tYpOO9DDa8m9z5E
U+v1KZiW7uzdjTA959eq4DRB7fnmioMhMXQaBClOkzy1H44BNwvs1HjTjt/1cNft1sF28Qpw
rlVM4/YvadIv6Gaauke8517KlSMRTeM0Y1ZxeVx8zLMnUp7UC5y+jeqjZnrpGNApH/m0tVqr
X9jZwXaGPHK8tGlB2YvH78ZMUTwLkQ+ExrMl4U4qLmCKHcRGlPZ675FNNbe6YO1svVOuXYmT
CBxk8CR8eoFrIpw87XysdyaoT2gfwErsmxXhxH9URRymuREHKmFnTz7ZCus3VQ4ZtQj8UYpK
+c7RSiBaVMmslkpdLpI9AYR2nG29sl8WK02iFUMXjXLQFJr/L0StIbYbQazQ9/nT9ad9drVd
saB0B09K3neGkbnrIFn/80umheugtoXrViJXECbIPcxGP1v5/ekg72h54fwkKVi597QWhePC
gsdiD4URMg6+V8PRfzfIL2V1TTl2SeCTp2243ooUsn1srYwG2m01YTnxrGsd9NrC7ZI9O0rl
Z7+VZdvVkayPCWU/TQF41CyOrtab0cWO/jC6CdtnidrGuVrhBNjowI2+J5KGkj4S3G3US9so
xSS6MZnDbI4r7WJWk9auWTskVxlZETgg5Gr6wI8eltjU16FecmE7TeYqzpj7mGQKZFBhDTZp
2SEGPn746KZ6W13sCFQSaTlBVKdnr8LOPf+SIPW7jkw7GfQZKbJSsc+iYk6qJU11iKA1HPzC
T9C+qhFfxZB5tw6KGnGIFcJlH7p4A1zO1rIV4m+qnMPQuxEjNsrhsmY4dWaZqQUv3P8g1RLB
Vzv1DvB0uRlhg59P0gH/tusmS1R93gh3O2jCeMKkm7J8UCOy7dw1lWZ6FZWny24Q8DppueMb
KK1uEyC3pjAW/uHy823tFh/8un3z1jg6cCK+fLwt9R0+/kvi6UwBQYH7u7eNIyYmB+w7rc/3
szFlwUP5cHPUNDsZdMI/ywdjbs8sd8f9LYE7YezexGg/YiKuINlzm3jRIH32VvCElPNMTFB0
4kZcn6eIA7b4qnhf3RIht7feiFGROUDIA0zFS1VuDF4EcqmeyjP0mfFQkMQ7pt2ArBz9sHkj
bnrAuSgzEp/U8/RVTX11RlWWqrR9M0XamX8idvnlYZnPI/zCXdaW7z5xdBbySO0UPbvg4xkV
dfiomhP8+D74i6eWGHcMwlVxiG79PZ7CZfQFJN/mbb4zHaLHJDp81cN664F0nljSIqQf4DIt
vApTyoaM7ycOviWqNKyDkuS2SZSxQuEXVEpBQk4M5yPmveycLd0PJbRM10ExuBdrJ8nwcb9T
MjypNa/07sPtcLJxuwxBKvVxPOZ6/PjrRbSUabZkvzN+U9OwykWRd4N3Z8rPquszAhO017g+
Bhy1rhanP2ue8ALSqQdxyHhjFuuBOJyd0kov5e4QEv9QilOMa37XrNsdc64rMyXYI/lulf4w
Ge5F8Lu7+xdeETCjnlWv37jQm5CIV7+QGdpjsYpMRi3HStDG6dkzOaf+3CDTM/MdQ5Io+/gg
CU0xtHo4Z7EoT/SToC4GGN9yiNlYf0uYNZ0ooIeWr7IInZWAPfNyBL43n1wcL390gZ1o962K
6K33PPJjNtW5Echr/nrTaLfE/ievsDt4IjBeQDmxQkoJ/6w6OB7QBcYeqJm5nohTkV8mnDnR
byUP5CNpnR6C36vHe86Vi5axQtBfYilnJmEPp0LfavA4PO4tq6vvOI1eKu5O4Y6hy98FL0AJ
g0rx42/skpjPu4ueXQjUXewsoB+VObhxdoRfZbYgInyOZVD509HYZdFCuRWC+OGE0tvKPzul
Tx/obZuiyzve9oZdkv9uY7MtYdYk76Ja13TAQ8jvA65Vx/kvHzx4W6Qvd3YKdvZvnOfptSkP
A/TLplcVw1AU6moYTXT5rPmXWJMth/OnrJDKzFshkkcM7B1z5/kVFdWXaa72I5VM7m12ao8G
LgocDziW+0n55xc4XZDHB9gCbdKffJGiz4qndm5rz27PycPNnAoUSr/70hu5EtYt8qaxholK
YZtZ3ShzZ3+Ffb74dtZ5iSvbT2NGQjwlGjNFm9TTp0sry+w5wE4U6eiqbH5d+uAdB90G/v4m
s0CPwlkIukYzm7bIb2bcHfQ7ryx05g/J93c/n3j6VMcPtWNmbcXFdqLDTiMVcr1miP2V30mz
sIS2KbMR8I+dpkQgoTNDA3A7ebtxJgR9HnYnqsjw+FzMhVjtue7QhTXQaNO3KcJ/d7wjlf+x
UWrTSEMDCu8iyWnckERp67PKpU2flfnXlhVre7WXnrqve+J7Gv9kg88MtNpyesadj3lJ0ifZ
NYUf+ytlVe/eOuhEV94QdIluBZUCPj6/y8i3kapvEOY47v2yWOBMJqlNi8FfWZYMX5kEQuHk
aVylaiYZLgNWR0gbBwgjf28sEB+njBX6Pm+xtykX+u7H7fARGQdYvZLIalI4V8WY+wRvP7Ir
W9vuLgTE/WYkuJ1Qld0pjfu4VpaeFGlVXNybo641U9hXcuoqjyHc2p5X492qyE6BWSBK+A+5
qz1gX+G+bVd6nHEeJPASV8TYnj6vUW0Za/AeuAURxxuzS71DZDTsVxFTZ+tfK7eXbEL2eYJO
TGdRsnSmpGcGf5wpKfT3FJV2XEpeMiT00rXInIgLLsdk3MMeFtGChytIirLHArOFnupY4isD
yyxObexPpTguvL4IftLCsinH+g60urIDyHPTjZFfo+yhB965Fnh45kT9CEn1mOO0srmqPl7k
mr0oPyBxKP6wsZMtYRaFmwT6gEl4pMFyhast3gWRZbxU6CNBP5upEbpYpdY25WS/sMapAm46
HMA8anl9S5zfUoWUphzs46jGnnhZdcZPb99OyC2q9tQC4QJc6a/7yIQzTv2K8T4js4qKwTbZ
0AQuWbCvEGsM4V/hWHhiEYUbPJNOMhrI/pDPv1dOuK3pRboeJYbTbkGhKg1nHh7bU5Kfs3BE
H3ytKBc1t825b+OTH9P1Xtzt1aS/jIuCWCbjkBm2dKWbEFcwgcN24VoZzic2sSdDU2hycNIi
UwFCNbaC7QEymr4SuLixjy1h1tgTlcx4Lk+fpxhZ87RYtP31Ke4W4QZ6JL6TT6kFKXbS0z6j
O3Yd9OQm7kdywCHlp7BL0kNbIv6WKlxtNlLXlVvp7PEFsks/7naNipCl+lQU+CxfteLcc0r0
Sn9aK+GY6kXhe3dsP2ktW/QGOMVYou8L4nuQd+biKxe3gD0iWk5HM4TsmTZLDyZz3QHh+cey
Eo1NBikT0g7qLmpmjLsTFETJ7pCPwxPFuDXeNjhXJFcFB2hRa3HJXW5S5sXMHfhB5Jw5OItA
uzMFOoBrL+6QAgSD1wspj5o4db3eLc7P1Cw2mrecCYrq+RetX9giVivGvUbn4co5xrcJ+fnx
wORoE/2mZ54/SuSWD52kTslMEHrLGhpa3EW7p+3Ci1AzM1wXNk7PdptxS3RPC1Zk4L4lMg4b
hhqA+/vrV+UZkzHndq8Kjz3p6VWDtAeIPKtq9WoAlHjSFJzxjOwsG/nsxl62gllzbObcOfgM
eRi/fTn4ZaOGQCY0PwtBIs3MShOWy7Ut/5abwpuQqCTsRB3vwaNNEJndPUrgYI7xrVB/U+WA
K633jxhpT0Jld0pnphZqoPXU4CwbwyvAt7L1Vs4xVc0EZ+ia/5NK9iWWyGJJSK2bmd4H5Mjt
aHUZ6cxUOuLp3CWQM1AY/4xqUdWaUWBpuDIQh86DHgsgKI5TRx5ZiOi6/oIN6FSLu0VzdItU
nAxkNy9bkRrPUr3WkZMzd9PXD2NZp6bq3cFn0K9vqaDlO1elr1H7ffR8/9wLxm8W8gxC/zro
IOfmS27ciHgcxVSBaV2Y+MIhoWyGBtZvg0LzQh6ERBTOSlvW4j13U+XNk0Odp4H0bbL79g3H
xgRBaJcxf7upe2j+vI+HO6/vR5L95cRcZMShonyXEnNhxcxnYnFqqlH7+rUNjB2me98fLQSP
VgyfX/u+0HENBWitD0S12ftS1RlN1t8VuNaQ4+zwyfb0kEXplLRh/ccR8LLWHKmOPotku7iS
wx/RsVSNn9JsOzm6bObv1UUot2dkxgofrqw6UFk5FQAWj1os8wcjeZ7yTP7Wj5pC8iyXbb4y
bDaWFrs1HWpRRnXxuV88+GOPClSxqaYSF50y2l2f50q3G4EojmPIDZr6Ol56bmCn5MBHt4Rj
rEphB5nYTD/xU/v9/1U11VUlQ/JEV8LcLHdjHV3iFPXjklTgZZimTYfsErFtV2OLHFt8AKhX
BRU8XEtRsG1gXPE1IcK5juZsYvIuWGWeaRvwOIebhKijlGQu5YgY2erXYOmCd08vyFVnFxyW
kyjQAJasHDAfncBHKFwsfR0ExI38ku7s82uWNR0Wz+MSWVGwo7PvJ1W77vs8YGPIgoiEH1Bv
rTk9oqRGVsu9QMdAsmwaYUOOpt6M1aMCM59H943elRtsgw43WidpiLUghIXq4yK5FfZRibrc
CoWIyG3POx+mHYuZ13okwhJ//flTjGi0RkDWhAVpRqWXO7968F1LXpaMWU2H11rsrHWGm2WB
02JsHhR9Al10Iu60JHJ3nBPwPyAx7ZwFPCajEbwY+C6bZKm1slPkT3ulgkgT9LWYn6lWbYD5
o5uj1p7G7AL/q8cnua62sKsog1G3UNO/G3PIyjKPmCgvjTJAJh2aZK7OBLTzirEjVdd1pQnn
FFgkyrUDsZCezruJJ/vO4FVSnlF03UX+veprzkcqdN8lUYiKp7MZa99x87QI/JTWzLkcgakC
S8Vib9roWJFNq9LSEbPzs3dry/6V1cviRzdTos26GmcX0CFF1KsRuoOciilIrlEjn8LYN/sb
plDfviqCH5Tf868g/tPXlRtriDCcmko+ks0zMigZwr/QhQDD2aV7Intxk3s5glga/+fPSP9s
emjtD6m1drhi64iYCYsu9+DTtEZ9nHeACUMnIfNZxtqzPv51UKu1Nor9t6zcpweWErUgxDd2
gdjwIip8+67wf44ABNpNmfDMJlf39XIvlRjvu/gCm23fqF6Sq7yc18I744eGnQpkhkKPRRrT
rLSCu13dyHX+a+66gO3dCsedjd1sCbO2hYPkBmshWJIgbWZaD2Mnzntr+Loe3PWmdd5y+fO+
LXF8QxW2IaWs2pwsteXcR4dTJCOjjy9LdIwAZmGHWaPhy9FX/97efvoPmbMdShg5r5JoEBN5
fNwQQknAjWX1hiwNvJogwk5Z9l4hX4kJCL/VGt8+EjpVne3zdk3WKCtavrlCz3F7+sbRcxh7
N9RiTs6Y75dYuTxOVpJAZO5DVepNozn9veAtMM05n7DEvqUVWayCGoXZG6w46bMO2kfbpli2
sZOtYNY2MNCh2b7F3hHz9BFKDWrYpoY/RY8qXPMArZPUW7ojOGgrJN9S+Y4A6D3IROJlr1fx
+/pXURH5c3Dcyhk+IviAdvC5MpYo+fyR4J9Nd8BW/5hFybOsllcdhTTF7EJXn5lF7cnw7uKV
NTIW4sl8JA+uxTzVjXhP23VqDFUeFm/LK1NAxPP62dOvq27yqOAT6eAxTl5a6r94jy8gX/gp
+kajRpsVziYGOcs7y3Z9Ibc6rUZU8AxWRx11DGc3bG0Eu3KDQMsIuvyv8XysiRcBq27ZMZTe
uLMrQkGZDH1IO5ZYvg4a/3LAkH9O5jcE7QhYUcEkDrex245bKx0qbhY1CJmnzdgtLiMptB2s
hVYAfV6i8s9J2MNY+CPCDrrKlLeKXUi6E6TZyV3WtTd2KTlODP7d6bq9J+ZehFkJSCaIVGFd
XcgFrxcOYmLnCcbpJ2khy/7BeWf/OQTQtiuWznKuliOejn2+gVRAfnflsV6e5e2VHuaw/N1a
lUAH64ZpMYvjBLoIZ/VHWDZ1sXEiVghI6nr3x6ANvWwJsvpF7K9UcXWhvPSj6KxQlel22Pje
7rQs++oaMnoba2lTthzJn6SC33RPmKK0VWajawgatnMHrOiG7UXjT/Y5sr3ltW2YwLTYaOOh
4HNHWRru/+tNzJt2apXo7xYkqE02Wls2s2pu93Skjk677aa6Mx/Kndp7/tboT6iz/VOdH9JR
5Sidltc5x5BOUp3JSb23BB9upOCAKXHCKsI2IeK8XmgxPZjUbbW9Jq9f30jLbQ5RxBU4rMR/
a8Wsb0nBiL47o9OP5572Gp8uRyyy+DR3+8ZutoRZMz4C2dcnFr+lcsOUplLn990rms07gXTG
Kbr5rD3/4LAljm+ogob0UlOEjN1Ed6JBt6x8Q+a8RscdJzSgfo1OdUX6KCWp33nsNnLrpPMh
AbCBip0OHu+xDRbEEn3AyssdHhd6awfOXAMMqT+T5f4PbnJjpR7zYwSs9uAOTW9o6JJVtm1/
cZhl4VpesFLnMu3NGymbQVJ8tJuxTrGXVhI6zf9CwHUiX6ZXV54mWjRP3uBADfa7zanJ7Ccy
KJaHSubdVahFJRIOxamm8ytpEZL7YxGRsRyztwbPo27OzDtTi07MOLZ6WZw8iHCSMkkGDkKc
oixNyP9UYnUFDmaUqtl6vq9ccxcq7iVIB+ZHhxgP7gjKwVTR/Y2TA6KPp6Uv2xaqP/+ffv8C
f1VGY/dey+KJhp1wBowR3zKis4a13MB+p9wgy3f0cMJey42jbAmxKHy6YmnqYxEDnJHLOmgn
Vy1rlNt3RDmlGI2zvzl9fK6KOhz1WHjId3wd9J38gd+3/2MOj2xy3ifaXT9aPHbXUmyG757i
5xaIGvNQ2OOsEFj/226xPtcoXVx1qchHCKHfIH0qUXK/49LAiCXaP/CD42ZK7CUTss7L+M0/
rjLJ5bVcKyaoXs7jnWwMm4/QhocFOTSF2gD/bN8aCD3f7Cz5e3L+1zVr3meg3VzjKBT53SgC
/ovx/JnOVQ1N4SHHmHYmA8tBvZnwsW3J7k7GBVo4ToafrlfQb5YGP6jBklDtf43nz3mD+8Uo
+zHZ29cG+epQBfdy8urhbvegyOrd2R/z7KTnjQsnYhhcP492iNCZHEC8fAxLRAgrdPB/RA8b
DKWJ/XJocSzHBnclSfqg5vu4iQTy2qL2mtxFZJQ1nPK/05r+QX/IYwKQnovhwpdozxQg0MTz
qpeqUeMN9l3FtKxLJ4qfWGowMxr1OGdPms+MM129VPO0lp7Nuxhb0A8QDIN/KttIGbtq933B
KcwLUxWYS2hGom04sQvnVDhXE9EhJpFmS1pxDHL4dWP9rWEWjxYchxfvEQZ5Eo7Eyuq5GVMj
lI7Bsh1xbsunLJSkzV5NlOBu4c3RdvZXu+LEDIEw/gPXuzJng3O2Rv/t1PDiAau8dBSMn7WX
RpccxBZgBmgMvyIpKGNZsjhZFyFQOIrPWwdx1j94O1Yxg8sWirUr7R3Q6JNWY4lEd+bfJqD5
7WVkUiTDXRMnqdXYiMlAKii+MrZonj53Uf2E15XVAtViScWOBodlv1LvafExez28HTgQ9sj6
1u8xNPf+EcObnXzt/hD8nbrIsHt2mLZxcxL74Ul/L4OQeB+GpBdbQZG7o5cTffJW7v6igOMF
Gb8MQ1fzb2X3IIrPyp/cNBC5wbIieL9oOqarbXYiLqNNGaUyBBG23h3vd8/UgHb8X5V4sPjd
vgY3u7LPOa4R5yG64BJyx2IdNN+1AAScMniiOvu4DsnpeoFGzZGX0OjY0Qh+KFS4acTf9gWb
pPeF2uwjj2E/EF2xyejBSwUU9ZhMo4oQxH3VsmMi58OVs2/Nwq9Sh3MfJHeFMCxve9IPSrHm
QuXNqWx2T8VeQu16HSab813XYeJDIMZHGvaBBzmw+zmfZYuPHkomDgeXLvaUDc6ZxxCM3X5Q
IMbf00KSYtDZRVyvfz+zf0zmvM0i0SXP6eSM6nUHA+P6G1NFbwaQrif7KWn29ICA6/csJeT9
V5GqayKnOxocTeJKb/QCL4tuba5IKe6STNnGoQiH09GnbnnIueo5yVKNoRlLyTGxyBJAUbhQ
V4m6Ohp9XxFDL7gZobsOiq4fLkgd7uCdbd3LHrSxiy1h1mxnQGmR+X7aXSNcthOJqHyrxhRe
/MQZrAKcm+vo0BX9CIMoyv5fqizpe3PDEMzdYr1D7LiyLTF/OxXOM18dagl5Lz1dE1es6/ri
JWA0QVIhNveVC6oc/tkqhTe8O8KQ6Q0d6c3VtOoxvBhAFOHzuktgaQY4dT0R+YtCpLpsvrdC
osJLF10YGenkHLtGXst6IikXUlugIzuMRpfw7DimlivXyQduWQeFqpo/oH+wc6ESMkzKmC5e
R4oUY6ELS2kjAb+YFjs13xtJc07r6UThG437DIRG0kO4Kn4/1X9wfUMSPeZdNQUPERyKZV0z
yAJT+pPaNenHYpdVO2ZrVZxTFJEX3RT9MDqGtIS90em/GCyKeQDZASZ+49q0n3FuH2zqS0SV
UY65xsSGtOQnZaffVgPiwP3ckz13Thv3t4XDCpEeb3t+LFI78WFhr4FGLHVeDlLkvkY35RXZ
KWP4e5r+72tW+YjL3lXlYf4FvxZFu0kxVI1zeheLC4nwnbseEwRUpl7Uduxx601a1Hc2zGFQ
cQbSoXB/bTb9oP8b9TdVelf9Rp7TW8q1t5Mq/kvE/4+79w5rMvv2xREHcSw4SFMQ8AcjCAoM
0pTuDMVCGQwBBAIOKCVA6DWhqOMIRMwwiJQAUVBKQoIIIYQQolKVJobQQugdQuiE6i9znvvc
i/d8v8egz3PuePxrIetd72ftvdnvXnu10CxUnK0vWPUlK3LjJwGJNmlzuOOxIanigbUAgl6h
J8q31sXKdq4/SNSQKyUNkgRVe1wrLynw54/LRLCUHVrlExwVqMrRr8uKkObbXdbNGj6FPdML
19EKa3ARW9UhiKlHrpuSpSc8MOiUr0XVM7sM+5LcOa2H6+RCn3lIun+pD2TLypwcIvvWHFOi
fyWAHIvS6KetnTl49P/C87W38dZHHBgBDx6enmv1MY6cevVeTS0XBVYZMRY0OFKQN8TfOpH0
JCLvocRHnqAVFJsCtspbXTHIVlOy3X538OFOKPxXF58XtD0LSKrdxCSHqQa6TaWSt7EzEUwj
WPCrM/zZuMwIThgIsujaPGhmyNsbE+j8obfI4OBrxB8KRUN81J2iPk9zubWjs4hlVc53CENp
C3VD2e6EVW1XVsOPq1cyyhtGoC7dcawpR6xL+5bF+mNjTr2k/3Sa+zyOfywHL7micxRgqoTU
+bsqNbueJLh8+lUzojEGGqFwPTfLLhRi6qsEXVWOW1Wgzskv3L4Rw5UqR2qxE+n6o22LISuD
H4o19FSu1RPj0u6luCHLzp3tNKOCSI+AQiIAoJqqqmqPy8VLW4baYV4ZJVMp7OI3Vy9UIA4t
vJSpKIifIiYRVIC273pIzs22LuBUeGgutGYle4TtdDj0Z6uggSmDE5cTtGJ0ozom80KowsM+
zOokZ48OF91HwzeBBltnurKJWxLNBlkryKc3b3wK/CuvMJIi3o+2JTVD7rqlsc6TxHibna+5
a2lTyI578eviLgAb3+MluajHeC/f7lwoVMQC1hTFCQv+BAKck76ks24rm2FGTgh8RYzqSIP3
03PH8uDG/nNtQMP7IIFStAokS9krybJxyHNd/0dLvBjuFlB1W0b/pMOlT5X53E/c3me8n45+
bjwrPlftMAcrTx8LOWuJH/afwBDYqHKBtok1jEnOW2bheUzlJBR5rSZ1hVSLYVDqI9+bD3wO
wDf0e5FMTt0Ou9x6gTDnJ2HOSmnY8TFj/d7rxcYc1019fZ0AbWIjh5obEO6qeZqpXTbWvigX
SUSIuFPYWf08clwOxJFGtGeEGzH31kRFByoBlTfeVSRxRkyOpuXdXwJSMw+Zzs5PRacXpMXF
PaQePWAyJUFdBY7mOZBqW4RcRkf9Wg3k0jHZ8WjcSu9bXNEjfEBROlIEqCqKa1qNSyU4sp34
bH+2WWJMqfjGd61H7wmbxAJMlouNz6+LEjh/Hp2nc3WM4TTLjzxXYhGnAOtno+f1vc/afTJF
e1BVXxMzKKxGQzhh7MZdgyeXQ5lPJyss+PS20C+YI+H6J+K+ezMBf9qGeCMlO3spBx9OT5Le
B14ZqlPSqIFJFaAeiH6ytvcDaeN+Dm1Ezfagqek5d1CvuBPKLFKdCrouWXU2HBUjqfF+0ZeW
UHK+qIKTBWVq/aGUvUIa7qFwrEqs4dmJT5T67A/cnpAill/Uxq9BuonkyjICGW5lgHnVhGrg
p2RndmGSt7pdKY8TNtJsX2tH8W88E9332dd+Owy8BRVjTrmFWQdda9Y8cvw6VZcVM/Vlt45/
93zyOtzCQBa5b8nU811Dh3IrLbV9wWMz5qohl8pFKXkZf9CSSkQSVvelwAs80x/rNZk16ZLU
GcWJLqOcP4lZK2tzjf/9wTDdMrywp3PNrlfD3+GeuvutuVYt5fQZRvZo8AizMh2D4K2d2gZ7
N4OyaWtZWxsOOJgBL+mpHFF16u0LnPex7s0uCLzHgvyUnt0hN5hgIK+c6dQULlsPQEAqJimW
JdbUgU4pp3nbqMEfX1QgF7TybYdm/PvFOWGpwxP2z1PZ03Wx/D++Hh9OSvhZxn/tXo916DYq
EYh6A+DZOL85GoBMFtRc+3OwVo9jgEN0HaInbXm2Shc935H9+y4kD7pXV6qzN1Zvr5TOGszJ
2sVmyidAD2oqLkYgA37rZa0Qfjxx/whsJvNnGT+tP+KShMbmte+lb2wC905db33d8JC9VqZc
s3WqAcO6pDevqu/Jv/S/BvjrQnn2QbUTpx55nWDOX1VmOAk7tNbUspa9B4Z7UtnMhrO+2Ssp
iXff5ZKRUf13LXKq1Iq6UbkECymRqo88PsZ+38/tnOQDS9O/oSD9yhJqV9Nzqhv6Vs7J6JUT
bnOKwIruWddWvMHOslt1CrYZS38Z2gEStK5vBpjsO+KJgOjQrGE3Xvy0U9RnaS6jen7QKuxL
CTR4xJRVfrhVymDmjdqup9U04VdnX50vMkowUZ4zjRW3vDdax7C+aQZ1UjtK49T6qP/s278h
BmsDhy0bZK/JYFQcJwpGLg6VrMo0pq9Msrblok5aKCPTNezFfsxQeoOhQMuPh2c5e8nqyKzO
xfz1iksd985NV4gmEJe8mcTypUJzy6vt87MuboO3enKZGXANqnonpEIxLr6AY+TGLdbcKdX6
yGPkQ8TMNgOAg50ninyY/Mpbti9KHzD2cSoQZMOqztCkCrIhAKE+hfSCuUqpNmuaqsYlv5mq
+9B3sahfF7/P7kO51vtslG0vT92uX5aK0w3ACy3Iw+licpEIa6s0V0pPT6G0QFV8L5Xa/7o/
4yxa72EP7qnQdvaR+sQ2BFJCVc3Xf67vI890RJVj9HM4D7ubfPJCbU0cUjzqfRNzxq7TRecj
z+/Zf/pXbifD5n+jDQzPIYS09ZHSAZ6J0sPnFP6EbWT+FD6Bl5waAHZvWQx+AG90G24GUouy
QKLjiOJXjIDmd9GW8IJBmm09ZLNBL6nR1upwsfT7Sv2hWXWrsWW+TUwmuVXI8e6bPvrU9Vyg
uutERqMrW9+ypXh5AnHH8+GrBWL+stprRGsgMbM+dt2LdOdhf5B0o6PHlEaZ7OLWZL2DoOlW
9EhyP6Le6O5aKEoKptn6burELUZX1pGkdQPepm3Rprv97gUU3cey+BMhb7P6LZ96Bn/keZ5w
citE+3kg1W3E1lniNNks6i8y/lkICi4qP3s38Uaw/7iOgMw5LRN6C5NzCHp/1jR6Lmq//qzK
dQuf+SGZ2eTqmax+apB3LGuF4xt+6ovV0rA2BZdZHsRFYS63bl5/IZA3eV//iO6mahbVIGuq
eATxkafWjddyeXcVUfdqnugF2+Ih4PMUZBTrQVq/OAOt+JFnsA0ZEi87kJvuOsD3dimHevrV
CPzWqJWZ0dSFiipzALMJLMYMZWMNTw3sXLWK/TiTkkR3k4Htvuz8+ePh2n0+Dax1qPVvbaa9
ZLsfxS5HivalvLXpbsmOjevQADloEtc985RJkttnBKV55Ha3H/FwedDeH05LsnzQcnnVxoza
56ehJy+jnwdrDOGsue9CJ7zy+4i580mX0dHa9ZQnI1bSdMc87fSqUfRFzxs7FfvGaQVnrA2w
MaPNx9v5uBqkrroarbAig8Yf2l6cqwHM874nqr7OsxxV+f3YErXnTHe6OSdEYkxDTH7rZOgu
5+Q/xkkv9KwdSRLXTXCM9jG7ZLDPppN+oVg1jRDUOK8fLREHoVB42Nc3JQYFMELieQfKom5a
omjiUkqceqI+RncfjgRg3m0D35KSGu8fxPViWkHQXyzT8waRJzdDiQajJpshRY/7jtdPaZaJ
SE/QY661fo1z59Arfwc/B0aGVZ9OLi1KUryFkg8WpknnwrtFOoU2BpxRFgyyhOtfLSKexUJS
OpdJ+WvRmzbAGdTg7U+iLPb8mumL3wjXvTr4sCN+COK5LhryFKjffvMmwMiyeuo6+/aFdV/m
BsnrL4jo5GquG6YnyuZpX1TKGS1ZGRQxZM+p3a0uLl0/xk75Xcs3A1Rqinjj0Jjo/282BOEi
a1PNMvgu9DuTCd80c3HWMfXtbYeu9FMTiALj8MTNk0qfRKHvDtU/jvvvBtPtk61jKw/swSzt
kHaqf65eATJl9iPPQR5Ci706qUdaWVexLcDA+FW3tpRGq7zv45x9zWqrLhe7T36ZMl/nFucU
gR2nfyiFMa8xrYR/GwY1oN274hXSOYW3zt74gFBI1fCsxM7dPTDKye0jw5+av5PTMddoOZyG
lp9aTeP3itkBmfeviBawTSCx+IOqj6050JMub1lHFDRQsx4dAzEN+HrcB/lwAYjbC1rJUUeG
zIkEoI7EL7gKNx0zW5vDaDRLqj/imWTpDnlckNx1f9z7JJz9oaAj/PxQi6Q128rXF9TIXPa2
NZ9Azd/A9cVpN9kN527T+8RStDxNfH19a9yu51DWTBl8DVwg+GZYnkQVdK+WhI8OiSDxbOvf
7NvmmX+n+A39R4rfwaEe+2Btk/a2oHROYNcb6nzxkF5+NkN9+2TkjS/T8OtuF/gdFs8Ujvi0
gM7nlavKycqad0f0gbIW6YvvOGFQlozYfe6v85nJOXQ6SesifSU/3oOq3uSo7YlwUerJjUWU
H/lkGR3aXjZod702nhQHbIuAONQXXanLaRzJe/Vh3iUfwdpUqTjYP1jXl+fxd1zbFddSjwpl
UZTUKFLYYfPPgN19h7i0VSRNm8f0LugWzMczrPpkXbwI+uJ+vkBOPTxgW6gc8kTH9Eou1MKk
tpXASaDU2Vf0lq8r5ssm4R/5VGvKrxW4WVxEeWLcvYXVl8EPlLR7ocFtcQg32eG8F+rHzVXN
Vc1M/5It3fulteO/7t53wgkWPA0NTKpSAot5xbus0Btexa0T1Sx0Tau1XPZkJWQ+cWQgKb/0
dLi5jJUUuHouNYUPQRi5scyVV+2/GxmFxEQb7hj3PZlS7thxf/nMPpmJrbHCBEBsWsWprL7r
qXna/j4r2yvpF7Pff/LAjmf/Dcnlh9gvStujdNZi//xBCM30nkUBPthbIY8OL0/xYG4MAMQu
JThlamVgVQTATG3cbbSLETRQdGjVd97AT2x3Cbn/BuU/5L/36usazSOrC+RK7qX0UGzmH2N1
CChyRTBCyCwS+9Nh/i+F+XVrLA5kvYgdCrhAKZ5GywQGqEOFI68nWIqP9xFOPu8DzkVdXrzw
RveImJYCpSpI8UyuLOVdRFXrPf0R0/B9ya92Qt4XVH4RY3mUyOzeeBivG6kDj++yz/Qfn8My
aAVkx63CprvGT3byf57m0p22GdEiqf1HYuZt69A8eXFmGgLCCX2bv3Onwql/2UDvhBoanBo/
RWO2prQOel5IFJxf2Rdj+PmXfzMc7vUuzc3d7cjLzTWxxKk+dSvULD3Bq45m4CV08r3fF6rx
dQe5/ZIdXg4NH9YsPpRuCEkJFFfOqaqYRq9r+wewop+7xdhQLDhWMLmFcGAO0iZijL227W20
EcYOZdVsCkF+FD++EzN/A2N9NLO4dBnbmGQNcL9MfRmIA+rXamKBjq21l06L5XYkuIPGA++V
207GF+Az09IEDcwRt5Mi0ja8/A7vj9kp6vM0d2c4nkNrAVpGM06RYdHP+9CemL1BNyeF1Mbn
0IRoaVb74X27fOnnYf2/4zBIBgpTNYB62bKVd/Uj9QvIpLWZwTo3b2Pbl/hCxpXxkoUllxHn
NPbkvruGX4jy6yJjbOodyNW+Er/3avUkORo3m/rfnBKmMus01elpbD2g9DEZscuZJBtCS1ln
ewGLbvhh2ccE10ezS1GtpAiY8a7txLyn3bEfvLKkDwwj5zuSgAUJSYXdBJB+GDFUYLRCJzoS
dDI/KlECnBnK+VJZo7MWCeqHAYDcyAJ0r8sq+2XeMN9UzE5xn6e5Xm0+yGCfvucRIafix9p/
86944MmcsRJn3baOLAr78nH/PL7/dg5p6bCpoAmSqWOHF+Z13l7zt285iXJwICfZwEjvzBJ9
bXN+5hDcejXHsqTwJmP90eaDtwShlU4Fvo0vRfp1X86CPqJ4Mqmin780Fq3rpqlMTLKGWoVU
KrrOAeb34rTPehLOhT/tXX/QnY79bQbWMJ9Vq3Wm5U28KyPdhRJ/MfjkTtQPMq8sVybs/Uvq
tNsQrWd0xuyEikHWg4RfxJujycRfT/IbMY/IyqdGTpcPZbHZEufGJAPpzQHbECXrraaI14GG
O0V9nubyu8o5r1jljjVOXcSNjdAG1hEPRMCZm4z8Ihv40vZK/m7DdT8P6/8hh+RvzaI50ZdG
UXD7XKUovk3zBFwf3hYPOi+WiyJ1iUi3kczzdJAPKtEFnHuU9+0Bniiw27ZGETnkYujAF8L+
umwrhVBO89jEpKayD21uLBhMMikhIl3/MbN3pgEXJe5DZ99uqTgxqcmCQJSnS8zCmnQPSxxN
J+eTAxULEPOC87w9O0HvOVBROWsfpGyOl1RGkyyGOE5vpCCzWYOWTN98fFFaW3ySwfJPscE1
bWK19+mRMiu3xrXRQ/qK+gNKN3bK+TzNpVHK496ajyWRfLMennJ+gxKLaCm4mwmJRE+/qSML
zdN6xQ9k5+PivXKhtVZCPAuff+u3wiEp0SqFNYG/OyKmdgbDSTK31RGi0CimcbHsWV58hPyk
WNHicbJG1xb/kVtOtZi369DurmTA6tn2gxlfqqHb3RQpTbBuhT8K4p9y+X0xPoNMsgHazAUo
08CMfkl4qBSUZmZW70HWCK+c55mJClhr79UdHmc6bkW7etIhWKz7uWa038I0RWxYBgNQs70v
SCfEI7TKDkI+W86TNzaibPZSZ3hb51J5Gmos1ORDaTdrJsxuPmnkI8/YxbPaJ5kVqmHuNcx+
4ZAiQKdfaTeG/sA7AmcUndxad1B5p8Z8IcslHd52o6uuzHU0QhJZmd+UrVfhPXizzXozXHjz
xvxESrZd8SvJ5fLJXN2QkDnMPuLKZPE9BEh1fgQ4f6d2pywuaO7q1/Lw8S0DPrAmN+d9e5HF
PQmm0qbv8CNbZzkJW+OrHWhOxlamRaaXm4d2s0iY9fhkKtFKv9cWnE75H5WzFc/4tQTyW4Ba
DbqQgQzuS5BrMoOq2mDiREyrLe/xxEYKqK8rz0qpTJVYNrr+NlE+r9/uWKRcsCnM223IxUT8
K5bjXSMS9x1U4Lo9M8rS/kculmB9mPZkE7WffG1Bwk7wiBDzHp1mEYB1CI4hEi6n+4rVUlhZ
6ecaI95/2L9cr1hVk4b1ErMmoiz0Njp1I20wdfBAfc0KUkj89GLI4p1XETtLPf+r9/O0mlqR
wR2UForwYiGnkpwXoP5NGiK3vrrYxXUACeB56fSgQs4k5d0fRfkjAEGLYrLaQmGrr16Fv/9Z
Thss8AvLkzulAm0dsVdgyoc9hZ0WjLy6tXxW1+vSFVHzifN3DIP+oKtP6CI9ewoBPaFSAzSN
CyiIJy7D6SPPCMVPyHqnmM/T3G7M1/ivK2lmSEF+WvDMK52SMLB4i44kwtc0q5bz+coDCPnO
tHC3Qbm8ZOf70WdcPbRwNGanDV8aOkp/YGbu8yi+EY49B9eJ09aesDSvYxq2PcEJgVff5Oqn
e5KHN2A2clE8QYhfsAKFkQW15Ea9zRNbppdeI7zI8HCN1vUm3taYL9Tx66wkt5R0JRMNyC12
SQE1BGKVVKVBLwWq9Y/K66/enQthCi7vCZY8qz7ld+HE4BZLTN0WCbVtKKoMSUP9Fa5utIUV
3uR5bLgTeC6kTHvMxPInkrwPzRZ6TEKzz0ewvxm02ZuuuJG6xPtaG8Lc2PD6y0l0ck1VleNw
Ufn14Ueeq0mZiYmmLMiH7xV3yuKC5tLNzaNwHxuVHNV6TkLLPnVzXOVmV10e5yt5fS0ZyGny
c1B5JNo6z3b0yO/Xg4CDxuS82/D+qW6CaK6+9p4+LkB8Iyy8Vesdt4yr7FYenwD2YOiso1WM
zXkLVGb/LI1naenXN9kPHUIfPxVc6FytM05DFZjsE64f/FFU+Eu1+6rMwnliANxmihSQnxsv
A+b4+mIXG861lWtkkOuLwA739aEjU2mhJb7h0O3wACKuiGR919jxz4nHZZw+3hkyr0qMAOaM
53njZqbUm/bwZctqLbeLjIGdemQ74RyygmcD8dgzb1ibzRPpNmmzYTaRwO32g3GjrldI2QGN
b0ByWygRqNhNjxCW1RJBdl/r/Y3ZAeYPO8V8nubyFnzPtS3/0ikfSJQgeN6y8eaA1zGqfq89
EW4dJRr1k5l+6vVVvIBJuXuozPh9ECYC+3CbprlsVuGJuJP67Oijz6P4VjhsnB0lozIg0nME
r+ZopXwv7YcwALNOD25t9pEn2bROoGti64lVzkIoIp9qeld7bLR9cQqVmw5zMoiGS8kOfNf7
pXp+Vciin7IBBE6Xv61r0mfX1rd9v5RzkdQeyuwbzbiKp0ofovI0PVHvf4UtSnl5XraakZJv
LIV+r4lLet4/p+9eZ1eDh+D6AeRzAgE7wR9aDBbsnGBkTM9bGgiNbjph3c1i8xr7Kh0dzlOl
fdxuiB9uW2qKFLv0um1eId77hqt9Hd4sPDteId5F/zT/zE5JXNBcBhvziAR3ypqSoT8PbFMs
J+zCI/okoyypTjkCFVGj8bf7M08FgzWkrmqOSWqEZqrY0vwVEWB3RQyj6kzb/J2bMVzg+DZY
DmRNJ6GMm13vVty0bBwe9iKM6T9/N1eAeH3pVN5V78u1I+73NYAQD4wM1mWpph6ytexYHsf2
jP0O+6XqfdXiNBXIJuWOtY4UxUc8T3dDLwRhtG09UCreTZjzeJh1Xxp7j2GGQU9naMsmHarY
HGwV6AdmR4BEAOPxRX3ZvWaR5RpCf3s6zVV7ZHSMPnV1HmJOsbt0zaf40u4PGvcq0erOPHZx
g9baBAQX5Oof2ffC489dasztXukk6V26rhww/zL4et5o8erzyjBOBe8bo0CDOzGRUvFrKSoL
BGIxBJRONq9adIl3XyoF3r6tl7PBOhD1g+XALjH9c9n3mDG8gzHdJ6q9M8kGTwZmGsMfrUVb
RusocgL04i/ezIB7tHs4ouaSDjCkDoF62GmZVThjfX33QWTSSdavX6jW12XufSc9fbACTe9F
deZQhQya9cepQRUkqKARqJFlAKg6C/M7kDcCBTP6dPv8kkzx1jXdDDv7TFAOJeKn6WWg1ay5
ppz+Dx6fTKBUBmcdn09ZfOkVf3aYjma+y+vKTWWpzRuq1Te43YNGc2J4Z2DvcpmTvf6FvWjY
si3cuOkt6mGrn0fsLkeA27XJV9EwEQzuzXGZEl5lZs9u6WhzfAo2Ad7hURJzAvxtQvbZnDI4
bATBhfL4TW/YWgknlWreJRa1EM6+ffPJLjH9c9l5Edp1U0tgR0Z3dXZ+2oeyrMw4ayhAK0Al
hF1kWncwbDTlMuXJQv+bTCFl1L7tfW/fzxeZ4gMeSKjT/g4wu/GFin3VtemBlunoiq3L1Vli
M9Eqmz7Y8SkKYP1orSiFHsWWcb5MxkL9FjH4ZZ3AtT46VQN0bSZkkWpzKqxtYwbtPsC3ELMD
814s8XHHgmanMgzQez5F91CC1q3pcBtFFh3/7idOkAMre4/Z1qkyGiM005yAdoibC5lNQk+F
GgBslMIo0Yp7YCd3yOKG5NJZtD+ZZnngAc5Ua3k9p3JwxGO1YD1JO0tDOoL4ncOEe7LwyDzq
AHih06SfZK63/Th4f9rWEm+HITcAvgkeTu8K4xZiZqvKURlMCehYv4y3Q9zWjybJcWqCW0s0
g/0qJF/Pdo/1fWnPHPJe5/ALtGioStVYGQGkw6S/dBC+KrpsjyUZsgo6nmE/WFUfhzpyiU7U
LlzTzXy54NYeXWDZy0lzTsOzxub7I1mnt/Ze7vHPA0pSJs+9nOk0W11VPcN+HfAJ6oTIS1pS
bh0jyHj7x4etxHwnuyo4DcZSkIiEwNUUNF9EkNWHAN9F2crgcvyg6+AMkk3rpI9BQC3V6Fi2
C601/mLgwC5nmdtVyWxXMcwJCHCu9dGu0D1dkgNA0aeGb9o3xLHlOv0MpWJ7to5tug7JdaZv
APN9kBfmLaN1XUetjFpfT6WyX/vtFtUulfhvZN+rf6IrrEphmbevQkMj7F2w+Zqvr6UvhDEd
FigtSYzx4K420L8A/HUfbT7R4AiGDeHIBfE/EiG4ZZ8EyvNJ4NYVTHYhhZzC81emwEqdiWbH
UMsisccbLP5Hcq79QjimnpAYQFGhPcBE/3B2cyekHwILLcYb3l+4mKBY03qbqGWDfN63Zazu
/I5zByT6Z1D0Lz5yMCnV6RTVzSRt0VPIEmlnYEDqRx4RtTne9lc7BXFBc2vWSF5trjvrtoCt
k5D6rtOgSY4EUq8JTUNnSNBMGbF815Z+a84RQx4G1wJ6AjVNIuOjCuvcRKIj4vg+cZRxgecf
zHKIPSlCrdBOHr55PRtCby8fFBuT0Vkl2JAGzTayjoR/hT/3q4wXd998ucniygvNQ1VYhPN9
C32itnXrSpeNzxBQms9GTp/nOsWEjE/KDkhDFd6sCdO5Hzo+bpfFyKu1cpWQJtDWoGL6P1m8
3znuNtEOW92BR/7YVOlqWxSvIqAwwNkhu+z2aFzDBVtjc6kWFSUdgj1S6vDmFjPRDWIGY2Ds
zkcdeS3iSFy9eOPVTlFc0FxugQIXajJFE95WY6kEiNWgFdqD2AUEMGvpIm2qGwNWlCtKAWNJ
LX0tr7LlX3e80ICJb0AFj4kVrUVJ/HBwmgsU3wYLf0IwwFgNBOhReLho8Ovx5REBOJ2VtS05
PqVeG7oYPNPsxCpZG62EPUhDleWUqx/7Uq2+Knptr6ojmHFso/8BcjHCxRH+WGOrGQ1+jIlj
iVhFK442oOKfOHWagwhJ+LVTg49Fbwmaz1TqNl+BmkKWbo7fdCYYDMz++r3mTuQHbk9DSa5q
8Y7qXVUtiYSFZd/tQDml6Bd3XJby38+XPrwUYuKDdOJjuKrYtjQscPyTCT9vpaJKSwxP7Tbq
n9vAjrpR4V4CsGKYrFFDVV3+kVP5cDhk5cM45o+ungfGGPZ6VQgyRGcN51j9tpjTdWeF2yra
O5X+h9J76tgpOHrP5nmGQzozik/cJC4TBQTMGGNEOtU23lu1XpHcN1vc0tfaSlAbmEgVL4ts
xZjbaRWasoo+HJz6Up2+6ogIO/yRh+i/4lbTi6xWHnEofup5PD25ZwxqrH69BPQWFf/nrS5x
51EMZIQpBQpzxi/61FZiVdw92JwWz+kqVvfBylHrivw3Y3Zg531Q8WoWrXXkfJq4sWBPSF0P
VR1dVdg5fG57xZG3i3iaXk5yfhQl6JkaFKYO6hGHPLXmpAo+e1diYRxNIf+qU7hDFDckl1Y1
zz5YWaTGzPZzcYjoqSjFTIME64FWX5fOtxQR68hnTXsvPuHmZd8Ez5SUX2A+dc1qWMD4XeUx
jKtXiEsUtulMqSkDvQeYKebn+W6sxPkt7uF2Tld3p2dWHzhPax+CDDIk/fCl6n2N+5DfdPF1
efEK5TQM1P4SYizs1BO+HmTWOrmA5VhPc7QI2cF9wUFKEjr+0+khfVSl2vD0XFCGboT7UifE
VhggLfnr4SvDrj01dXi4S2ouI12BYGRabGbqEQM13KHNHpT+84rRhNctq0IL85CwkMJbN27U
p1DAM57sDi8EIfuJ88N6etiG1q0JiV8EUnPr7j8f8izL1m0zRlrTEUSzvcyYHcK4Ibn1KfK0
In4SPHFuSrYi2Gu5WXiy0iIhAoz6QA3UzuCUIxB55XGem7d9EzyCyAITUrRvgGntoZloJPne
vbvjzAXicfaK4hbz3e3969IeIQvnb9cqNaobdd7O8exSpzGNN1a9UtmR5tI/KLV/qY5fZbrs
OVJR7MVeN/iRXmJBdgQ4EfMnz4u6uI9h8jQ7TD22V6UK2HssYNk+mwmtzVrfB8GggtDqvgjj
6VLLErcOIIngPkAwDpzbe/nJTvR7dSSqDwrBYVvgdbO+eTaUBE/xy0e7VwJdZe2QQfXEAVvB
2b1GAzsf4Ybmfsl1Agq1/Tj5ccFoBaZ5aBCpbWSxOcLpFMDgRIMKy6w5x4rqr3EQ0PcAI8oC
qM7UWtfU9/N/8deJG+j/nTx7Dq0TvMqWHl5dZupXDKV1LGee4Y3lJMnLnNOB2S0a8GjLP225
F1HXOzQ7hlk6McOQ4EXITxY6cAqREhMNlfZ/KdSvW4agTO9l+rFNyowPHtgAX9t4k9GjwBpN
P/vbTSvrTaFE03qeu5JKSxI94zq9BkQTg4Ti521o9xHLDwALVKK5SPTvuF7YScqTndijQACr
Wo4DkOygOWKFuOcyZjyV12wuDNAAGghfUutukOovij0x40cR0yeSQke27GnvphZpgUebe1sW
t5YfDryf2CmMG5pLQ4bndGOh6H2TpBbJzfXTc+72dHu3YMAS1TKhuH+oWHCOd2gttBMy+9CZ
7U70rallOLh7dNNqWh8rku6BiRv4vS9iuMHyLfDYEuxn1pUCOkuWWg/iwyWGpZZMo/U059Rc
opjvLo62XeVFOpZCmCYeTCeLtbf4Ptexgpy9B1xnO20ZfHe/eBC+Jt5C0RenSQSvUN5IEoz7
W/3mljOmHxltP14Oe2SlJsWM34CdnK6Ca4v0brtraRJtdGmI5zOVaJhvsfE0MfVRm9RMm3k/
J2z9k6mZeuiNp4wFJm8reQmPhMEfa9qUiEJCmep9GAGm6EakswD64q/kk2WZEvAMmJJL/gIz
klQw1b6Bp5rI9zX+6bRbBw0Pt2v070ggRCKiKaS50y2ra42k2KIkRG8NaAkBASMb23kbidId
StOVT+fgmgx/a4eesGOR2zi98hLVOXNiTOgXT84nQ/MP+OEAcRqBHbn+nn2xbCJ1/nhaREfw
37VI1F2sTJN6KXY6G89w930vj5RA3NuMADZ4DJhIa6WaXwDasebtYtl7zn2xCl9zISSc1OFl
TyhYBD3zLCsyt3rm3XTI61GY0xVl2+SUEFhWTbPW6Y2YWYE/1iVbj9cdbgwVd4nNM3pdHOH6
Vm3rOKjHtXdzyp0RY/9iJ3iZImulgCD9S+fjhl7CzDc/8iSmalZW2W+65SCGFdg+ta0xPxRl
i1Lz1OJ1zfpBVQ6X3v+0lLqqdk6OtXGItz9mpyguaG6DKfcAyAFBGyF4nMBUsVlY+PmKMd1W
guj0G7TBwZOPyUqL6JYRr/uqoG6ik4Y9OT7XvbLGpCBZvf61GZUn+QkXOL4JFsWD2NkhQlKt
wHHmeaJQoPn7QA3xAtbYg4xYgtDc+mNOuShchkPEWNcI6l56cHcaehuZlL+K8jpzbtsosvHF
99w1TP8XI/FVV0St9QAQWKMllJ0SxVgjeoluo+4ZhbKEwzJ1xOMnEV6jQ8RVt4s3IkVKtV8Q
PRj2o73hBKc88jmPbCKiTcm+uiY2dT0RZOvKiOO7sxMaL0/ws053y9G7PhNlAbCD6bilGvjj
je04tw4pUDBM0DkeFXvCNlvqwwN9kfkzkVDtqoGaD9Frup6k7d6DCjsFcUNza5bzeQZX0TsW
wlyrlTo5B/88r+6KICC9+fj5pV7Oyf+q9A86Z3Jwg5lejxRLuzkl62K1bJ7nrUWXZddZJn3k
SftumBss3wLPnktbbsE64Zvdk2FlU3EYThmIKA1/ptmoG2ij84Zo7bsQpFPiO9b+0o0yNxrd
QfqX+bIxHXMt+X3tNKFlmMKfIZ9sSLtR+Gs83nvVez94BZavPR4qI07FUUycljowJY6t0S1k
hxClmshL2Qqx638ezJu8lQ37Y+T+b6AiKR9QOwtM7JRxLaUNgo8LW9lWQ+Ll9PNuXD25EzPQ
2TEhAuoX7W3/dsHybeUmXG+7JJsG2NbW/+mSwJ8bVzKJb3FphaaooOn1XKw+U0yh+iOP63e7
NhG5XaPf7Zv+5flN9wDsE3c7wqAJkjzn64SZ9KHdR/pS6J1GsJPsyKPL0NDy76uWjqF1dfX6
LwQDmMYzZyNcomssaw6K7FTtW6b3GJKv4R16ULqOP+MDVu978SbIH22KPKWa6wq0jiQHt745
ONZTYYyllKlH7mtWNSdr7ZU+Gu/alcuo8IzdiFmP+VLdvyKPcu8i+HqHOlnnDOAtWqEkzo20
KgdrMxduBhgI7z3b3U2MeAwxyUFFYbov2HpRIkadImaBahwTyMbN7eIzZcugKyGrijAZqkKx
Jjgh7ZkzEYKGmmspD9FJjmZQoUFb22i0wMBOrfgUOVts1aVAA4L61ev6klj5W0PGIRtrSn2k
lBSQ86G2oaiBs4Q/I59bvBsZ/r1HT8o7geRuww5EY85FzRrqsHeK4obmMleIR1AM3ZLma/DX
YVYySFUtz83zuLolXi2/C7+Ka5BV+QX08/hHnhaQIomqbtpwCB6yFYuaWPdKXY0CDMXYP+EG
yLfAc2h18ZTwfGC+zex7lpVGG8ZfKpMAVFsH+4y23VvF3v35y3X4CqtJoHCsCEQuC785VEVK
SBw6p6rpVGKj17DYFuE3W0tEsMb+dHvJIKXgAG7NFRhcRXa6Z65OM0DfI3blpvhj+rqJfv/7
IAb/Uc6VJTLO/ShNdSxeqU24BvbrkU+mjVMXSLdzsnOtb0gj5CUs+MGBpZmDTk7zRj3U+Umi
GTQF5l597mDv4MMPhBdhXqUrSqj3K2P3bz+jzroOt4EN3vPv+hjE9c4Km9pLUJrNMmMX5YII
IrWZ+7AmMpGVV8sWXKK+LxGa4yVH/AhRqB2O/kETlVL2HO/RHpW3pAnCRDMNy99/+YT9s548
Pj9o1FnTkpMuismjmb8LdlKGpbPG4wupaAtg4Mqj9i8v3cLzNcdQmU4ANmq7f+R+nFixChuz
VrY0c8B9soCc79oWgPqjtzfm2hFlcUlsc5PWIc1Z46Lj7oA+e+VTPdBQFqSSbk3rnwpJmz2s
GrNzrA9Ns7x1ndQCpws9RW5G5BwM93eZRUGIWfM2miZYzXy2Lsi6nsjTZrjzGa5oru8+p/Xd
1WEJrxtDRUp1dfydTKLedszPUPWb373wNZauSuUzWvLv8JmEMfpf48rj8ZHP8wetpHqpoVIf
eXzja1pfHXzDFZxvgClKz90K/8zzeA9+PRsZZtcZcCZtRSGbk0s3d1o2VxmlnaeboZ47WsHZ
eGYLkhxXWANscTegNc2g39jg0Cv1Ly8D/jXHzdt67qH7LJLflcFzhp3iXR367OzWhKEa3QR4
cuisIwF80TFTs/SMxP3MKrEbI/T4iZLMtMzRh/MirgM3nbOjDmA/fFqxZe/YrHkovxeTAQgE
h8r0SSXeizaQIS4CwDQiroBd8Kd7f15ZP6HqQvdgiFSeIyM9GFNBBgJH03FDrn2Nue5T7BCX
i0+f7HauuTbf2Xisfl9RzvikbUE8dmwYVI+T746fSHdncUoP3ZiSliWODD4PDPHI3orA6fkL
9SjOLVXm58pvsPgHY/fFxOwW1j+U/+/KCcWJhDXwUBUhLrT25m/emZDl+O3HMzcYc/JMEm9O
hZZHGd4CElCCsxKyQZRqnOiRnwSjVzQ4GYEia4jfxb58IL5mpWIeltPhci0Jb5Seg0ciUCpn
7Np922bYIR61BHDUmdWL77ckSk9EOiMfkH9eFgRGyL1vD5xp2n5cUTTsuopgBShygEftnBGB
R+MOgUM+UtfCiJix3vkgxx7th5nGoI0QUopboZczhWyo6PVM4D2BGF5X3YED9mDzCBp6LgiM
BtVEuq/pT6fdjwLXOyqnjMfRuXJQu4PP5DFOt+agKsXN2/GubwfoRVaYo0Xx6SPiAjs1+ZZp
TiLMxl9kzFtb4WUdfzXglnIdskevsJJ0nrqqcumkr5Feie+Z+M3LfWqmEUtkMjwXYIs/fl3/
nOvmQ/2Tjl/sOeL5CvOHN62iC2KW0XdjxYaanu1fin1q4qPa3ygWoHZOoWi1fOV2o7YkcxOW
OVibSQMKai0xtS5TOR1SHp9uICWCrOZalDie19KdU/bDMMZkupZemTxrLi8DdexdL0t+NryN
y0CfG19NTb6jsKTfE9aNXI2HTlHWTBKfeVaYU9pv9ZFCKKR7hkpNOyVxRXMbf8mzByVwvmmu
JB832qEGCRP2dASsGWhYJr0mBP6ap4y6o4D7n9M1/rufpkbLZyZgqdP2txoTzR3uO35Yovv3
j6FzV9FQmB2V48LUedrRR0GUnSeQzmzxGxhcomLXdGmu9LdE5963OUN8T7ga+3/FtFfDXv4I
MWWA9cP0OzpUPsqnebCsCFSiNafemx7gfwYdj6UNdELSFoDGQCOgkCpQIzQuNWtgs9ezb7Pa
1yxBblwanzmZ71STvaztOGvvW2sNsG4bhtk+jF0wq5XcgFqv8vUElS/HzbXOdOaqXVSM+c8Y
+A4sg3q7xT/y6EiQLEmqmmXb+5Jz7VKztiYyzlwXgaJUEh1hPOmSR0Nm9bX2EraZub3GW1eD
qXm2tr5n2xLuu42qzlmAoo+d9dgpWoTQMR3a/WaQXyBExHobWjhrluCUtlJQXYtu3+qdurhR
IecDM9Pf64sdNSc+4NxtbT4kclo92NdWF4OkqxorDoruFMYVza3lzuP+kQctgLRBtkofla1p
Fl1wv/KWoCZ1ZQirJsa5yafMDXNuedkT2plYr1+oeKSIsc3i/NmRNtUZKqcbhSWDn8UVmn8+
kwi9o9WuxDWFgXgCdAzrbR41uaW+oWaecTZdLkpnafPGOll0Cd6li4PoWWzF5Yw8XmnC0QB/
18X/rU1oZT5An8fyy83FPQA9/+2w8ovLj/FsM8OrLSlSxfrHt9KX6jxO/fovRq5FXgeavcIa
G4ZH1H7k0cN2o/IAo6y+vlPdddlR4t7UkwT9v0he0j9zHGPgxz61GrNKzsD2IjPTZlsLoF2x
2taskuoc782dgnlRFX2+B0rCiqp9bg9s4hIIL/GxGHpGL0pEdfui9DE52ytkPIKw9mP3hSAX
mrus4zuaxlnUAR3z4JbgaWvgXE+JF6F95nvITpFc0dy6Q3meKb9MN8ZqIWEn6EE1QIw3U+cc
cWXqwQOM3vYZ1Xle+gU7WpFX5cs5pO1b8rDv6EyCwOjUdvrMQM/cOJN0t9SQKzT/eCY+QPBb
mlwhTsDjkVNqvNI00danZk3+TYaiB9p1g54oNXPHagn9gZNIiJgxS/eY82oPCIZhsiwYYxpn
4f4GXuA/r974Yh13t0Y5dRc5d6BAS49Ylpp+zV5lJCuwr48+7MfSjZdDVmxjUtCOuUW6wKhl
Wzn5wXxx0RGAtytTyrL88nMXevxpSplq8OVYBHXMaNTW4LDtWNQPoZ94H07DMSGzJOKF1s4g
aOICyZZTewkeyKQCY5tQ/W7WBxNHk3ycujfL50heo64m+hbIkiUYDOkvSXJ+oOOkNTi3qcDv
tutx4DI0mYdHcS92rAcPr3USZ+0nCAYC6GsRPkBo0NAIuwFxlxY4fyc0aKw3VMvylO7ZdlxN
rY1647qv50rxOdawaW8Jz18nd43sH/kAb8p6x3TaBViDz2GKlot/KTPFVSY96jFzpre8aDiX
9uQ64kftw5nEd/Ich5OwsTqjJyIKVhOpaZ7fgI46Tjon8BWfFRG1Tulx+O/S172cf6/5rvK/
ruS19/d5SjCwOEyFQsALqjn108VzC8xMs9zqlBoTBZehHw7V3f0Vpt7TtSFxXwJwy8UBHqK5
HXf3OT1Xt73NpVaUU0Xu4lvDHTOwJxMHLgL33hxPihW30WWHV9RtkQmqcrpVwvZvH0hIUsgE
Q3VjMI0kml/iFpsND6pVpwqOxCJ+NNR9tUMKVyS3V6A8IpGdYr7ODXTdHxlBUXdvZxZ6rupm
RRTR64imvXVFw/zhSw97bfBVZurmmowGNHavAy1oOrF/DIzmnAygsOuqBvvl/LhC9M9neppV
CH08S24pm6J6xc1priCfTT4ep2Slc3rttfqyXoIRMWLhbyKLvW7OlbjNNAqHiS5JUvI8HwGY
AFdxuL80mV/xy3Xc1brk1Q3+nhHd5Cuna0OrpLSJn/V0sjRY8tkIQ1XfuXveAO/Nwil5ZyYl
md7z8pvV07pCtCSYbyJDcvUVX+c92Ykx4uVC4Y2hvuZ3RNGZ/8g+H282V68PT2OfPD44MmxB
CyO18gucW4SEhXdvtPSNvMO0DgIRIYXTlBPX88U/aZGyU+q/p7k3qHi0qZ62gRec6NrJSCHH
yY3+oxCg9FII5k1zrltU3v2h4cEY2GxcBR7TS/aNFEjPqRvy1UkLBszUar3w94xjzwDneWv+
PY5v6jf7oGsV6LD61pXVNlUIcBBMH+roys1frLWB2L9egCZ5iB+J5fx72CZ16X83sPsC/axb
HaOzlH+IvIWNEvrh6OLz+kLLP6LdyKrp31v/Z2n7zWmrwW2E8AtNbVOs/iCIktqVvFKoOtDJ
OWWg5k/g/ZMO1zoWxuV/XzeeglIRRW3omkjHM8Gj9Yzi/+t6XTsHqdS42RBQXetTbeFcUOQy
w7RXxa0y1Uds4QFwvaqiB+gYa+lLIJTF6LisRQenXQOVvp5bLG3jlZ1hsPLKKfU/Y/vM/+zV
RyImHk1lbdtuGZx8b/fvuffDae5X8PkBF8kLswAhm7SUZ7ccUOCCdn9OXyyO31L6Fx8bypEH
EacaF9XNPK7bYFcXjD7ymAJAVrPbodLf8dJi/r3ob+k3+2DnjYGOdlOqT6a1b1kzCIXz7iNL
llmKxRZ5NqDAOXr2ky/P6+Xh2d3B8YwtdmwKf/9Nlbh3HBrmhi0/t2zvuuFo5oE3mH6x//kH
ebBVObHxAz5iCMqM5LemFTD1m0NyhBrnbjWoOO4cdEEhdN14Pb0yyfesRJoQeJuS9nwyjJFX
SnPG+DjjUH/Q4OTtPD+jh/fplhIqkf6ASFvLJZPkZ5MV5gXMdTNSJ6RTWkqEUn7wk4pHO1/w
72nut8A22CJzQweZtK00SZiInyzBl2jsj1v3to+0MtsUcpMf4PMOsuxcUA2/34d0U4ytay/z
aXqXQ8kafdAL9thibsQQPzkW/3tE//TfwDK7sV10HdvrvWkataJBWANZ7VHAWLyPA5rISRD7
tf+qz9Htklb+I7g217rrVA9aoG8rJ/I8M9Fc419Fnu9OWz6z3bTby7cg0HNbnI+yXV96FpGZ
8j+30LzyevJUZJBBrdXngTDDTYZgyPMLGU5DmuysraUEAuK5KX5LLFnMoKuKrfzDTmgirzv6
Q4Z/83O4TxItYCYWQqAVWEEmvboWx3AO1fy7SpCOSx2/ikNrCA2hfstLoqLyAlF1/dQDb7Pw
HAJBELTRNrvKd3+nRO5oro3uwUr3niVW1BFfbIq1WR2lDK+nDLX05ESfio5S5Om8jyouz4a/
v9BGX3dOKRtuWwadg0Z7JdjYpnDKoPGxYrgD8w/n2psXXtehNAHL94fqj3YT+m9NsduBQj0u
pC6CklVPJOVAOd/1JVDbuE66z2s0p+U6Ide7sGdo3PeUmFdTdXbqqlsacf6ScvmXa7m73fN0
a6HoRH3nWjXlWTdRxLasrCXteV8sKg1XJJHcE01+lxv1w2Xc/Y1r/ufDayXn1Qzmcfi8SSum
acFZR5IeZa2L/UT0k3uhA1HToZXyOvATml1SR5JM6ET7+mhIYADM1ndhP/u1pvYNn/Sy1h8z
9ODsLFl56wRTAHlkoVMssKgZvS2h6jUw8/213WvOvV+orkIBF5+P06Fam5lB/Q6tLVwNqRJa
ZL0Iyrw2A4CaM9IkApiAEVbIstYLEkwDFMu++GRg93j+iU8YSxVoN9ubym5ezO4w6iHl2z7/
rU1VLzcfY1WXPsn2yC1HFfQKqjytQ0Bm8bVbr0FFrar+QWY6wU1QzrrElcdxMnJzKK8OunyF
brs6TB6aD/6ht3yjJFNZcSqVIFNxltOn4m0qijrker0WrX+gsAnGU9KH0LHBkt/xadcGqm1S
ZyOvWudRis0FvYRKIy3YJQaH7nxig/L+UVE825vZ2JI78YEFFLlO13ZLeTbcZBn9KMP+HBpx
ZwzYwN4T5FjBdMxMeCUg4d07reqlYtxjbyFgripJMSDEQZAoSX/ruy9e7XoMuL5Z34M6vKhW
HfVMO+tpftuxldIo1c1HC2sF9WuqYhOouUCzuxcHdv3yf+QDMZEe+Mae0DMk6KV6yoAFlvzT
BNl0qVFz/tx0KvsMHDC3d3jp6vsZ1zn+SMgVj1hyZqXia1yRm+f/qmFO230N853DsCu7eu+5
E2G9dhuUh7pGjPIUGZJ43zRtWQJotKaYvXKLnmggYlgllelgwylGWHIvHTiV+3cxwoqicMTf
xQi7rTet+2JXTx49v/P1xzuGkx9UXVikkkrPhGfpYztrMD0Cp6bcKVANsNTzYtVZB3j0D+pW
gsI1ADMjo3CZk9Lvdz7OFc31VQ+P+2pBS4pTHMeZowtEz1ATQ82a8dbhugrE3GEg0MoAM7dZ
1XtJhfoL7axXuhwK68r502lX9bnlkLportEmYrR57cgX1yflSpP/LiZerPbw7CGkve/+EDym
bQqGXO94GtVfMkjPOwoHzIMqvz/8wd3XdaLyEadzY7OgecR2AQas5SbLybtVHtMK314VT2Xv
UTX8crS7WpTsjXrn+h6kqSPjQnCtqHqklvyvJOvWv9KV7P/j/HurUtx7QKqDXMw+Xk1OS9Rj
eTgALlMhrZyySyVx4Pi8wfSbJ+Z2QOVv7k2fFeigV+SO0ZSNK/VkD2xHGQfqX/GxJ2jQDETO
HVpf4CubGjLQcfypluYLDJnxok0TIJy4o9nBbhJSyMDGq1j6mPoni3yH9P+C5Nrw5lGQLmxB
eJmPNV5twfuWTpHULN8RbX3TcRkZJIOJnrxZ3q4LZh1nOtdAg3LYUBnfPvLLIDtygHtlZ0iG
jnWn2jJMEczv/V8g+YZ+lWuB30DIa6VGpuErz2eAzrjTm3J11jzJiWlJ5tHkYg9R84ay7voe
GMov6WodQdgq2msIHCgondeUG4BG/YFZNNivs+u8hP8zPLs6Xwo8HgeAignhl4ZWniY6Wpkz
UAUDNU0razCkiF22vjiuhpN4ruUzwlLqf8o8pFh5IiHwWh3VuxWyhSGHIIO2ep6IP8yOV7Iy
r1CIzY2Nd5HtiuX/8/9A4RGAj6NCXb0f/noejx0FDlCjvW9NWrdGMXBuNS4OW9vGJzFRCVDf
Iw5jVB2bRoKILWHlj6eoBLV1B3x/XT1r+4jMCOwk6dUOgVyS3H/Qr0X6q0sc2yD9TspKl1EB
i0Owt0GgyhILvV7wJOJOAJj9+py26zSREzzw4wlNSkqEcl8NPn+AZnDVONNUDh60KToUc8WQ
S1T/bDbhUzSvgJHpzRnWiYNUIXfDNx9Km8LjWAtJ98BbTuPjaWInxZKqzbGI4vJAfIjNqXKC
q+9EqjaoQkb30f/2m3yFhrvaXmMzbYIbtU1/hHYKkKr4ml3VLr/GjzI1gMdXVDiNK9O3BQby
cFc1W0xmx6i/p+urGzVLkMxbcXI6q3h4RAY8ceUxeN/OZcqz5/sICkt8pVU+3P6U8GoCvXyp
WYZSYC4UqEapvy84d0dp6efuJbf5q3HQbS9MdVvZthxCeHXBzG2kuRvFsZtGRD+pNsfdKHC/
tZ65i63rKU5+HSXFOoCt6aNqGTM040nhLhmFV1MUEX/4K7BvN1aozZ7NdE0+bHn5LU5OXWkY
dd9FZ82FFsYmfOShkv2E/mfcq++Dlg8aO3pM/X9Edckr6RCHzvIcCd9SyzB0rfi989awkIln
4oLcjf6/5NrV1nlgYdoZS68d7XTzYZPV+9q1MgtRvIrMQXrJvWSRUISbDKZjW+rVXYZCWYcF
paWjuQVvBnS/+IYWfDY2lbWQ9ZTsgppPYd7ZiNkBZY9tpt+qm4U+Y1C/tiQCBRh3m6ooM6/a
tsPVVkJtwMzZm86IOxebIuSZOuKhPISyRYyoz6gXFOcH86bS67pqa0qAknndsUVyS1DyaxfD
HZK5JLm+SeIVCw7q6Qjll4uowoYgDmBLcJMRz4nr9hjy+cztsxU5g/yXgnR6u4/rOMB1tMc9
ivOmxC3yvBrHi2T6jCs2UddUfTZvfBIlyCXAfx4b/z166XU8aBpvrO6Q+x89Ixaa7upnPBpm
DIsZSBy06VCqGQEjCbKBTnmUqM5C45mPPAYlPSTDL26E+vcQHEibRizWvjlSiC9648Lr9F8H
wAH5HSMh8PSi/ZqjpMVB1+Hp6wQfY6fL8OTf2owB0qu2MvJTDefFjCVJScgmiwWGlLK82NXu
Tn9FTHfuiombetsGXexiYMzOkX8uVULPzXRNP3wQ4jpm3qi9730tIaQ1+lQhsvuCGJjt1vv3
vdNxqprnTR+By+xABBJunoG1aIFgAwmTEw1N5IBmwGw30vCR4U6h3NHcr1CDxTW8EkvZvLz4
GSgutZ6+qmHHZA465ijrM2P5QpeuMsResCcpmjdNx7XL2hOuFLDWYY4kdYC0KCj6B+UvQMYd
/v9Orj2dGbWzsMzkxo88R1ejRKyO22u20RaLN1o95jvmZmlGoet4I0MFas42rb5Xd8gVvJof
j6FLeAFoPpYfOp3hNawVYrDpm4MtX4F5d1uqxbQBdjNxLOfnD9gRc5slbMo9MCZy8xGoSEWZ
4813cUvHbv4qMDrh/+Smw6uh7QmSm66JMVOMt7bVzYtgAQr1ZOOuo34XTd2J99DisiDDJrRf
u/fXdnWWAPP8Oj5TPF6BZc1u0vU6n0wVXB9N38zqvbN2XuFlkV//XaTYfaJImG1ZC50aBMeH
rGFS2R1Mmm0SHZ2G+v3E7g19Hu4tfX9lZaa2FuuAVm4tSUgdokTOn9QIyaLSZcVHi378yBN1
4NKkRgWO2ResWZdiBMsd/bAMUpxZXQRYKIVbbczYuw7yLezU/JulZcWuNTcn4sPlhpzcJN95
UJDw+7mAvijwgwy6KKSerTjLK8SJGe8iwgyHHq/gei1MknI8e4AVG+EuD0irEFvpQ4NW87wM
w6/QfzdXoXsNGJZ49DIu7DxCPx9Z5gem/lRY0/pXrwO1OLvCdXsBYkk6d3DvBCEb9Go02n9q
dX4sjqaFA9lgUOtXNefmT8etypSTpL+7E70T77ZZraqamqDgaNqf7s53xV6eX2y16eyYvRHG
ZmxexeNudaF12asaR4DOcatK7NZY8V3XWuC8jPuFGb0HJWWYnymR1XJiaM2HnQBVESu1hPS/
X51grkL3/s+489x/pAPqf8tTt3AiXVmJxavRPHzfVS6rX8utTxnY1z94Gm/Ac55llEmIg79q
3qo8TTC7OQV9mak5yjEWfcUEmt/JDmRUbF/gS9g5i7ulC7LKP/LoOp5cb7TflDt5avwqwg51
aLs5wlX9aP5/krXP+0JZp8qsvgebgOmnDFe6LXX49BR95LnrqzxKspqzMuaEBI9XXPeUliFK
d4mBizVxU2LB3o2Jqj1gVsFNqrnzYWEr1WUdXruYHaKns1xXISbVo6txDq1HZJAXIjSptBJV
LzTU6KYVPMDHtNr5rvR+BcSzutaG3s1Jn2b7dqOengqbgkLnuIdbExjxwitRigsTqBixL7E3
uA7I5Nmr73icaFM9pUHw88x2bXe0WxPkVM13bJ+qQ8Wf+R/SgFqksYOuHH9e4oWfW5T9ygx6
xrQ9R2DJct1P4HJb9L5ZeUXtMeMGFL8WbLw/Z1n13l1fFv1Pyxs75nK35G4scF1lRnYtmgXC
vM5mqHGqRhuZhu+zDxUgpBGDtyz9pzRCG2mB/z93bx7W5LX1DaNWOUcrliJQGftgi4ICYgjz
oC2DVYZSCFFGGzRAkDBEwhAGK7UMEaJVpjBZ0AAJBBFCCCEiAiKSgBgCmIk5QCDM8+R7257T
0/M857le7en5rr7fX2xy7Xvde697r/1be+016MH7C5CjXFHdY8k3+w/N+96/0GVybnCPfIoG
HnmFdUQXZonfBisSC2pon07/dtyyx4hxUxTK2hFhn5CUc8h02Tbn/rC9UwCZWKXjSbNrgnOm
30i51P7XmPX+PD+jJL7T0G4X7jSu8OJ4tx3V8fL6NGfOcb/6JzoD78sAoP87G46k9mBWx8LI
MuGyfMD52dODWhh61uhzCFpysK/i62JDXIrg6r+THuB3DP0/9cje6sk7JCGVMBtxurBk7oLi
EpN+d8NSvi6ktDDuGOW69dXcV1rsqCPc7LtsbrjXObf2ApJ+dljn7Im//vBvDGknIXp4cy4k
YVIncDbrWmaergUsBrQBnrj58uy9/05W+oPhnlHao1XlZodBuCbSH+Pi1l2StMByC5nmJ+FI
wlvwM0rYPkxcB7tvIyLQ1/mge1d1roOlQF/tbEAVHK8BePyunPoNUbcZj7xhP+kEvmmfnNww
pbwtHkqIr37aQuQ4z405z+2augrhoqs7vKjoGVqy4TxFwEMp6TLjsKmpWN8nQB6lsKXVFcz1
p9d+Q/Idm+8a6AuQ+3rFLS8HE4j6qTYcMbbA6L0/Ec3CY9CzAcVq+tqrk83kuI+84vcY3Q9V
T9hQT7L8oMssExlQR3G1b2bJ+zyjhgFJfJkOLnLTu7LfcWx/6m57kZN+ddNjoWzYlZL5113L
5e43neLX7cvo1UB5Epdk681PK9VO1aQr691Byo0vD8FOGuyLrl4p8DMdjbqzErbj039ncu+j
LI47xqyolpe39SpQzHo1UoKD6D8nLn4kyvXH/RAMpAXqbPiwhqXcm2zmBO+15zgyyBcD7siO
ZTXctml4sefek9+Mc4ejRVBEmu1PzyQJDzeP5gbJBfYSXbgxvaiTZA/ykQ3+MZfZJ0eKHVKL
bldFaQ0SZOAWho/CPzQv96YlSQa70jOjt4jF4tWcjKKBa1/d+w3dd22+s0+clJS8Sc8bqcTt
Y56DifL6IdoFEJhf0OZUSZLEKYWMXe0ZE3emtWdtOZxKzztufMN2a6Q9ACboyC0TlKbnUB+J
KixolGhkX9EGP3B1Tv3rj/9/cZ35tZGLw+vMZsuIiBqZPHTZRrQNc3/Dd4juSIiNW2W5Tbuz
7BiJA+5PE/KXd09fsShNeLhsKehb95K1VRO8CjUoi/ZlKZRdIHD01Xd/dKDuXb/Zv+j3Phvt
B7biylKPxpH4mKFeV2uxSbQlWN3N17mVvlJ+RqvzTtCBw6Gob5+qGilpIIqjJkzCm1vjlqcu
dUU3CD1KlGx++3KgKtJpwZ26tb7+rmAQ55M6g4B1R6uAeY+5824xQeq71ytiQJ8y1GSvvB7s
3Gvoc4DQIIN+JmRXR5EmitWVBOQ3Ugeuybj/luA7tt9dxdz5aTh0MDXGdmQmFGGcFRGGWvZG
a44+K+xeLtgjcPHTKF0GhqKxhVLnYkKlsALZ2mKFcOThEBcj3Ypx0icbBQ6VA5tlDnVF6roV
+1hCmEjdf7k0e/nIQ493HOmfupuVbmnpxXEu0ruyFMgEnJgAEznacMcohhJnew7ExbLb2j7B
SqV8YAz1eWdPdw9F2eACo3alZau/IJCaaO2CWGLZLtGAXZjjGrHd929Z7KV2Xw1Hjxbc3Axo
7OON3cA4HUMNSexjbTuKiwdc5EU8LBtO1OVR+psa5IZE2YQkfCHsSHUz88kXaW7r2Ln+u/Xn
VAw6umZXdFmv9PqpZsEuFLF57r50L5qX+MqIi10igsbwcnH1KpyyC0giZGff8pDWVdkOG2Y2
lC7mldMtTyNz3kgd22RNCvfoBoVvUn9sXnUJPtJmA0FTvCA2FgSi/0zfP/uWvP2sp/Kr1mts
C17kJyfAHneLMTxptcVYcF3IAvKN1APkNWiEfcxesFqUsS98VE3ecAYRsSkMoD4Y7ZWbY0u9
/KdLfNBPCW55TEXzZeRq3fxVxhuplqM0iBV4a3cmcdVl1oY4NnDNv/73rKT32NzVD0dIgtRj
giwCLyNVIp+/WtoyO3KORbFazNDjEQUv4pQQWbt3htHoFMev1/q79KloyCc1y8ujbVxMSoOy
4VR0/uiLOT0vol8nMjmrQXVzWzt7z/fXfs+Y/1zP7FCsSw9169wbZd6v6P+cYhs3WenIAXIL
bGeUdSz6ECzLYM8cQtevnZ5O5utWQIfS1oe2gdKhTlQDrLvuZ72Bo9rPmbTBXoh8LFhhrv5Q
0rJea7z5zoF/izFA2YT9bTi9etYgn5RspslS6sfOoY1ksnmKLpVcTa3NdQ2YxGAlv9uLUKfh
15DAl/+WmfmVt9nsHQ4G9/3SG6mnblzKoOfbLdq7Aoc060RUYjpxErUPI6rAENeVAkX7XYNh
a90r2fnejya4GNGS5I3UvYueJLXtOzQ9zyLnZjy8hCiob0shd7lC9OUcxEi2vfMA20EtxD1C
V2VrfpjZCkgVCZCq6d9KVcz/kKq6fyFVu0PCazkTVY1ItXEQtB2OxNJCnagKobouoG1LyxPW
07fcwdEFxn1R1X2EkQBllAuTWFqgU0vEH191XsIALmDa/5zwREbxGWsMk+ip3B9zqjUphxcY
hIimEDHLs+TzLbSwrFV4Fu77g5hXnQFeAs/JKcz2fexq3f48O+iLGdWhFP8mOlIQv3uy5nTc
k9+xKN/9Ylhq55315tmzjESmobSCAd9n19kh3QKHdo712uFvmglYoyIqsrv5da57/ZaYiHR6
CNSbN0urXpBul+kUXsAnEikCIyUDnWgEWZs2/6UC3p9Iz6NbQ9A4+Xhq8Gfe1858+jsG/yd7
RH5HT1Gq62S9NVflL69Q9cdjKxLdqCQeNUwzm9WG29Mizx5LkfQRAnGSsHtydgQ9ab/vzQuD
ArNruwIhQgqUDqJDwdbPIAbPjJDbweMekWyDtcJSEi/7VvqTf2+mpmZZSHuTGFHwx6OeZ14b
+veI+rGVtVc7+ury8rv0nca65BQDiuuXCyXgLjmLTbUBktqlurNzw9/HkfgxRyq2P67hVOwd
wzZWDS3FYOIuSNz0oua2ihrTluFEYv7C0MS1GF0f0wIUqL3Hy8wl1pvRvH/XztHzK4t5rdGj
SmmfscEtbhKRPQSdUliahA92QeNhuD14/4Xr7LWQsclMNbiF032Jw+v5A1eFaz6iYK9ZfVQg
abQ+48jTnCjLs9okClEM1IEAs+3inty+91tG7CSZii57phjrJTi0pWjnNaHrLJKz1tQPdjYK
K26qOne5N/NFmSghXjOA8rAqzqMvOe9Lp6SNvMbwU7+hotHpkidA+Yc5Nx/Len0bl07yaHx1
fC2GqrF9GR/srCbBqc5GfKA+ngpkCZ9LTMo9Ndtg2mUoSNUI2O430syptPrgIkf9L7qf/Ibi
OzffA/ekbJGF5o97mUbHPRKtX4UQn/MxgTXDL0sLNQNpd3A23idZ+upgoyucaIFB550mYvLW
8Z316xao/U4HIrtKZs+F+LEYyknownJLXajl7jz3FrCDrCxogD0cFPlCM2YJYpMSe8/r6DsP
/M/acdcoktFZeCWvkjSj2p5nq3b7p4v93ahHxxbcW6use8NoK1qES4dW+ri242PteRi5sguM
/rhp9yXVb7LoILGqBn81QocdpvVGqrCFOlTObI4g5oSC5D59+UzX0FIBXGZ+7uCFSlgK4AZp
Y1FamOJb7SKr5p+U9M+FfH4Pa6TtUAfa4vVyWUOeFcnKmixGWNAqXTnxnARb+loid3AbI6uP
xmM6EbpAzpT+v0Ml0jwEB0DlDflfoTLS8C1UWkfkc4ZWClS55p/MwBHE0hlL3Szp5tGZ0jdS
IBXGKJtiJJjkn3p5AgnBYc7yI8jOJUMOIJ8bNv8SKuN1VTZ/gcryYnrcF0is0OmtgIaiSG8F
NM49aGTtKJHcQyKWAJFxDqobO21/O/9Sy9rsLlTEbI79zGglQdy7EUeLUCsYaJyL1phY5A8f
kA33kW7H1ZT5Nm84o7TxDdeveZ74zfN7RycD6kOrt/9yRSdxGFGs5ymQF99ly/GaqhKxYSlD
sbWzVcc76R8dmLFmFKQWz5rFBTfIQ0zcheNF9sTSNKFqrrlHeJe+pPVGNtqi79b5578h/c7N
d44mASjuTKi7HqJ8YdQKj8nJ9LURHLPuXdASYKB6SgU7T1Sw0cfoMH6zjQELu0XA+zYkIOkW
m4/2/Tj6ZZaOXDZ5j0SoNRHeR827E9iN71ElFsbalHKTsMsEMyZbDiTf1d9uOO2RvZBAffLO
Y/+TdtwdvoQVWabefioAZbJoJTamPWvEXAlMp3d+2QBrZMa2X84iFqjGZSXls+VssN2dueq7
iqT1IOMYq1DU4YrBSBOzDGK1agPYLuPEFf5MenR2clYWLS4laA2meUShwtxtH+jfn7i07cKB
tohfJDJpQ5vzs0Sa/a8S2f9ib6Xo3P0GtUgbE49/iKTX7InjqwwftaQZC1LLjKVZNTptGUEk
Ftev1l1UV8x8XGLePr+R6djdn0mekz7VSINgud5DjLDUcx8H4AuJOm8hMzmFoBHAcOgjHJ0N
IOCMdawy1WLXwkQw/UXGA0Agp7HCr3jRMwnYPIiPzkjVPDv48H87Dx7/BzNcgj287J7NjX07
Yam4meO/XkSlDIP02Jsfmeh9Sdd3mxvqsAvWUYKn2/G8nhe07a659o9HpYq9azY6pn96hlQP
eSPViJP7SULiVkPk3kh9lZMOqStd1WosjH/8wchEKlDyRe2sMSb4mIz+PAUBomAE9StaDdnR
JHAn3bd568nZi7+h+q7N97BUS32AHBvL2OfZNbvPhRftqFNHjfsOHKiMmGq2gVx2tl+NFB5k
oglbQGzu8VV9Tx4ZsypF2s7a7PYZbUhdiQxsCJsemNqau2ObU+KSCXZ2TC9lg2xuppSSRBqI
ArmIhgSuNoFYTCm59v61W951sv9f9bPUXBFiUIkeVu79OQ3OxbtseKtGFJXNlELEHDrIGQzR
t49C5He9LVUK0peVA0l1isozm+N+qh90KtWi4/IYS/5VqQ7Ow0HjdQ4l8/atkcmEDgs5L2c5
p0RPiP48J+GUmdwliVD5CuNA4sa5fd14XQF7KqDWMEaLGFCFSCos2Fs6z3FtjsAXt4NAoNFb
sb/D2+V/sEraFkDSYL0YFsyT1hybjuihGW565TU9WG7pnlpOTsEIkrLoB385dB5u+DF/+2sI
7qSFpvHS07++4MdoAZoumlOwd8r5O78W8eqiXdRajPfCMN3OfwZQdImYTixhx9waRnyDSdV7
7Spx2EDPfHT1Q+X08wwC8hinqxTmAHKF/IyjbH3XZgejUvrBFrX9Bl1ju4vnhzupup5MW8vM
6ogr/rz8lR/RQtrA0BgE2h51fLOa93zeGeJVDoU4OwUQtRZ2/sN6+QBJQVl1OlB8G7Y7Z2MP
lyQ8jFZhxhvwvXB+3aZGgye/C/otD47uI8rMVESgKhoCigxP6hucedI1R3f6sdu9iWLkv6rX
Gz+YvXskxA7uNdi5B61+YF57tiKIQSEEGCEkvKc0XwVBHXEV/tbz6HdFBLyPOiu12zg8aGSd
rD6jJYJeDLCU4QmiLPVC+1qr5rOUymPHOKCBtZLnBceZrf4M+Yj8lYBrZ70zVUZdWuOU2Y1b
G0QH1toj/aOFginsY3mBz7liisLMSkEGUdKQTgXCPDox4UxmL/S63P90ZPgtu/787d1nl+JF
4jy/b6gvyE3dQ2U6pqNlguHo/rjeMN9GWuoN+QiJfnAbegRdkDnnLNSmen06nfZjTAnkKfmQ
17Bojr25v7NhLmgTSw3TQDztgsPoKDXHOTcbZ+C0xYw8eH7B6YbUw0//EDbs6Mptmvdo7wed
p+qGKl92p5AdGhT9QiZQn9TlkYEzJqZSThGWv8DFVvdaR8zbxR/VbspWu2OOGdgcRToe5Jh/
xUPDSZWOBfAgIET675IXdZiBJ/5NhX0xOkk8crK+YdSZYrTFqz8N7FbalRgHvhGp6JufjT3Y
qDvyXgTYL0dMrRRzJRiAl2YAXpqgRPDcWJDf9HjXisW4xCzYE1BgiX9XYKO0iBUdJCIsn+3q
Ivog+W/MOFjeU9HrRGHM/Cx0OYsWbSlGvfIhG2vICdPLfbhuIUM9459yO+zItUdUC79de0X1
cpv2ZhunNvcRiXBNv24atzhqVUPQef1TJbPfxen3EivpJ/10xcBQI3iguZWQ68A490Xv7PTF
saFekNpJTigXA1El4IvaDDj2La4cWSDu2fr69VXe0zidxXlRxD6zYL9L3Ao75ppONYU7PhP4
zdP8RRZ41aLQr5FIMpKsmS9Fme8dJ96rE7qa5L2u7wnJlE6iw7WedussN/capJBbIq7y+3AZ
VNB6YHgMp27D7oZ1ayShhIj/knbtd039z/LQB75jvNz9enenP/ZkviL3tfVjfszJwgTvoSXP
hS9vLpwcBY1R4JpHqMEZZP/iNjmI6w33xeVRkLtoODVipeGjYTOzy0HMPo6RAtrLJazc15S4
edk43LOink+UeE0yLC9gYzdYYE+gyOvndPQUj8AhahWmaGgBpwTgiClKwsF2jPxBnNhVuJY4
UpX5GF6J5A/pvqD4eeXE7Qbw0R4mRtPtED/jo6wQ44zGT6Rtn5kZ3X1+4b9eBeJy1UjHwkKI
pUOOvCogEJ49xWL4KCXNWOlhhTHBwZ9FVEEgEIuxJ4Qd87RoMZZZLHWyhJt7ihaRZBa/d9RN
L4B+fekq4vwde468c/BJGOku8xeLbIu+XYK98y/wWKAbw2TjCFNbAiVbEV21GBmYL6Mbw5kX
nrPSMZw3v8vyyYN6tgAx6sXMv370Mzd2ptdxmoH8lbocUvVy3nc3VLefiz/d2pKjIKYWZBnV
R5NnQYZefFqBLyMXcFednd+H/w0TQ3QtZ8w2TQf8PqJOf8Y+ZIYJFOMzDCAWhcHuLTSv2pml
wBTAw1VzsXxwGr45ZoTwc6+ETSt0NXXwTebQZLZD3XEWFuKsWk+xtXU0X56PMuus5H6x8eQ3
b3jn5rt7AQEkpc+h/F5MM0VN36/FWPA5z2QewErbX1JSdFqggOyldffyFpfFuHRacH0kEAEa
QDxKvPVATTlUHRdrvJba0dT5SlxZQPAqPuDzcsaLeGKp7NBbCV9egNivooNbQAbMNRgskPq1
d/8Htb1N2xdrUQ/mrH7gVsMnTNNVSVQfRPBgfxLuEC4uKXtWtwvE9a1vbm5xZblyHL75pwjS
d577n6WjtMfCrtYO9bDXTTrnUlRsuwufKaiPGWdliCycS0Y5coZzV1yswGEVe/y4BDyCXJoS
QLx4lCiJCRabseyi/cnTVTS9Zmu7RG8F4Ssdp5nj7oSKUiNd6BSfPt+Iyd0z8MPzUd6NOr29
hns+d1sUaPJZfOxjjzUaeA05IiS9JtfROyn2kUAmPweDZumL1/4wppjqZaWdXcOIAhUkQo0p
ulv4a+rABb47NAFbypWols6gNWCAkiux4QYCEaMaR17sfSj68n6/eqSZm+PIIMSlOY8Kg0/Z
5gGQ3Pc3SDbCRGlosiAckDBm70V1UGZ+Cb9tdp92KqlZOTPyBnWW7IDlogcYXgynX4+wYZra
WcmEJSOYRsGerHsKBe2Zlua0BZBDqpEfcvyVEbhPYoZ6C8iiiox5d9zeoJEoLXyDKZmWgnFw
dsr6WOUtN1yKPWL1mucqErm9CcAVKLdXH7MRd0x31Kcp9mWILk45Ud1GtG3A69XAL22VlwYs
FwIFkAkkEwvAiwNRPLD7t7unho+rYHizLQzCuOLeketZ3hjv2DUn0tRARjLp4YJCKwiMM/42
+8W5n6Y7CED2C+Snl761h2CxBP++bJDaV1iKkB6XVFA6FCqK5Z6+8unv+Vbv7hbwlvpfWjqN
PuN55DAS5RK9dW8379/LQt0LNNLKKqxd6FCzZ8u59pHjHWTBHsQYU1jJ7HitvPwTmYuRE+yx
VC4huczfpLYrNd1RYZJ7YWlVYb6kuN3hKkd1gjDiAk1EAMdgsIurvQN6UvJf0Sp7h1v3m9wc
XFb8ONKLzC4gjHSmPK8M07iZ+2FWEn5uXmclmxqWPzcy3+IM6A8cG1fOf/Wd+j3z/3M8sytx
zg9rduC62QHXIbuPwTxTt+QHHrPTnhXtXtwx0XFuUWfYKGqEkDXP3HJc2GGt0jL3Rupm3unI
BUKAGSp47BK34Y5bTtVyjY4ztFTCsRCTaTMHV1+UFjXR0cD+QMAdZ9s8nlXc12Z1hA69G3fI
udB9ybCoPhwf1M/Hsw5u46IPt8G6mTbOsP6oFBhMsxRPykomVX+Q8kdyR1Weafe5JwMFxqJn
ZIGqREoSt819Ztizs6Hhx7yKKBbTzfbeSctadIerrfGfWa+ddjNvXcwbXpHWbuPXHyNG3q6Z
shfgbvfAheWp1hEFmS0zoAjqjxpXOF4uANoX7liIihLfZmZKzftz678A0N4jfu9IH6N4coVE
LR1a/fth2LrFRdZASJiydhlgH9zJXgsba8p0hANBeldY/UqOIrq6DhXcIK1oiZhf07G7YXDp
Z/kn/l3+gYuV3Y5Lz5+mgDsOIFTrqXPgdpBVScXe+O8/MJvYqq+sUTfx1OoN21ilr48EqA6Z
c/xe0xLtO7tnHx1u6N6TfO0f7JQv7VmI9ng6GL8/MmKA2Vs2uRbde0MN4XtAvXm5IIKz7dT9
3GxfUUZ7Q82afUPtPCw5j1cHWlKWt7EobnYv7DnuAppapuGiATPXxD+IvkfrvfR4IO+dsknH
SEJijCDofIWhjn/O2NlKCEM5hEcREgNmwLaG1nYZkmQiHBPDkXPlWLdGl5ZpjfnPOF6uCwmd
ATnRk1FnOJWbe8MtjmgjaITJWkt5b90RezQ2Y2x0c1/1MjF5dpgBGny5797ol7lpB1EB1QEc
dNylgBycTDekLKiM3t3hvd/7DL50IXJSDqS2n+tbvZJEPEpifKT6/27Yzy6y8QpT+kNa0OCy
n2ztT+XP1PanLc+FHm+GZpaMoLMBZy8+MzJCWyJpMWiNJhHxMOK9o/1Zar7Gc91yN/Fu/FcG
x9t7wsLGFBFTW6Y0WrD60+SZsLriaijqSTJxdH1TKYCALx49SsDsfhSm9ZzAHj0c4FhB6tCk
NKcGquHBqbAUDK+FakFcUvuMI2vwOjkJT5LIexGziCVJKUfvfX7+PRbTO3Q1PQKgf1S0KFBJ
Mq1xhe4GFpevKlAV0g2GxG5/0/UZslPAbewEDqYRc4+k5rvuFApEdISPTHsrQMzP8DI0kWzT
oGwqyddFzSez+b8J/6pJlPgOE7fjZJDEWwP6s/DTKiN2eb8Ff8XGX+zXDs+zSG2/kX1a2Bj9
b7LP6FdyG/2N7K9gnQcdDqmdhVd0EMkws5+x/6CUm4+naoW3d+MgfDFtWyazDGHqueE1X8al
qYtRK6ddlAwrSoMEPrtC/LMpQ2JTpEMZ89zyNoI1Gd7iClUdpkYSs7IWEuw9Pxrq4A8X7DVs
la+hbIQPInUseyBuJTT5Dp21tN7Kyax8oSpQTqSuiEc43XHqV9bu1gsvFkKX4mDL5HbqHZtI
DAbh0TA03Bl87JjmIn9mmkfBffqow9YQbvl0dN/363ssiOWrAgqWyC8sySLm0CpNIjRgMezB
EciIdPS1X6m+R+Odo09/obmLaHJz9M73my+v4JeD5aqPMryyyOVGkNYU/w62LkdWOIq9I8dr
QMRoa2qm1H8yW5rf1adlhtskohSfW8leFUwSxNns4sFRFksa438XiuxNHE2iRps/LqZDQPqG
pGxCHbwuIOduy6m8+rylwNe8daHMExFwKOLw8w+kUGilSVX3xwCDQuQbKb3Fz9uSZ8BxCSB5
J4zXxD0FfdhWbo7hvP6MM5oDJL+LOErUBqiZNTe3/gjzfS2d9R48+TN1PWxkxF+bxd0VaDOM
nBsch/pN3OCiPdwmumxYVtaaBw1qXokLbFelN/dCJ7SIGqX3tWYOH8PHFdWHUJEBz/nRLDHd
2UYWkno4eBACzYjFh065SDpvhI2wZdckbUm3aGpOJp8PZh7d8HjSVd5VHmxxttmjJ+LzDX0H
XpdQ88r54vahKzbOcgPWK0SYJo0IK/jgs4t/NHtkkkWHf0zzpuGf0TFJGF2hJQOitru85f6q
cV364y5uwd4R65bxpIV/7CIyvnVOCzsaifMRevu0ScnKKDW4BES4kBNdA9YfxR2Qq2d1CM8k
V0HCnTJi9n6qnpiZVhrzPERRU8gZ+jzCOJE6O5mjGBI+yeF1z8UcApaJ8FIzf0ZuBHAbQVUD
CsTAzwoE9ZdNZKq83zGThmxtD2IFN7Z0ztYzhrojXWztfswu+HUTUQ3iUC92LIwMQ3t0POhh
y6yeqxJ0io4L2L651zid2RyXgT85SY5NSjHrzJKvbOvVNfUzNjfsj1FnL23uV46TnOuJsO1m
pEOcAzU5677qlqxVgmYMFHNelZSCwGsXfIYml9yqSsv1LAo9fLdDbTpWPRlTtMvILAyBrtIJ
4CJtIipPlFIDn+CHiOOFcEnHnPxymnA/yftC/tZ17398rA/XUTzi5Tkgp9wGIYiWezOX1Yql
PCznuK5alrRS/fb44xCaS8R6Ib/z0X6pAFO4JvbBt+Pc2BIq9jtcsFKLrGphzlWXg2zZaetT
Vr8LRt7DDeyXUa+tb/e/pHpjc2pWLFNvkAJM0/GVCydQV1yin9kQiyiuUJu3p4QNFykSEhlt
5VMogm+Mnl2EIjGChqqqeQzE6UfMOlZzZC0W11HhxLb3LEi/JxuY+TjSJGekwYf0LSID/KFg
nwNjaGHZbYyCZp2/A3JwUYDXztWmL2dnJSVThTQiKdwpYPejeU73kUzkZf+WVwaxbcp+ET5J
hHIaGepwE5tp/tgek7fp7YSHayTPbthFl9z/+NI/eP7/UCsmVlCPJjTyXudUYZAWRl90PTw6
O49a+hB//DxFFZjYZBZwSScrOwZwZubk3mrRWNketwfBIFhYMXxaDRw6NBOsMhW/ZynUYuOZ
GvgFhjeP3lyeivR2p3sUwvCNalFfT2w82w6m9A2pLTK7r+7Pzst0c/yJFu5PFiHLwU43wsrO
ImNqbCD2yzlLTthkfDEj3MXgjJfRrkjpp0IvQ4vU757mUQLPsccLlO9El85lX+gd68RoTG1S
XoyJ17TSutnAyrSX/vbaH89x08NZaV+tRb3Vcbb/6wo9krvkGgnoOHfe6jgbdv6zZGsHo8LD
LAfAwmGRlDx/vSwqbeI0U3pP4HM+X4dIPixhRuVUc/7l9hSQXZgkLTs44+xoJrG4UzFrd5Md
n4QBubPDFo9v6iCW3JaumEGDehENctn6Rhp1cPJWhQuK+p2s03dj0l5hXkz5jgtrSTyVcy9o
ESMqgjxQiAdVCBflxFOAyzZZkCuvYOeSQWsGsYytOlxr4EMQu8dVFsPE645BN5kqkwaXhi/1
0eR5DEQdjHissGQeYs/W19cfyboVd+tXLkY/enTlW5iQ+TY1fx8VwkvvxOMDgIUwewo0+WKP
oY8abfO1krBS7dgxD2HmCtLBoDNyLkObXsJxilpoZmXjwk7fm/2V2Ps03sti+TPhcMUTnqWz
ZtnlciNQeXTQzfp2NyL1RtkQurL04kqyxLCiOUICeB56hUJo+WyDM9oF2TK3PcMGw6MwiQkX
DOYOB/Hw08/AKRrPKlODR4kSN/POhNvcrML8ZQR+kuhHwV9UUb7OsKVRRouct30jNIvv0KoZ
ulO+I5KtQYTkgvFtB+dBj8Ill0MKiCTA9TAQX1K07rk8te/AQARU5kJtwSdcOJDStCSE50E/
6AJRKosuciKOem20HMooqnYBjLzehd1RF+X0gpB5VfWLMbEt1UYK2eSAC1dX0aBqPj3KeCVg
eYKGhOOL+LdiT70PJ/8UfWMELTT09MuuR1S1qd5qieJXjYXIUT/EIVff4b5C8yVoGC0lAEc6
+RdpJu58nNyUNsqwX8oAQZ0G3HcR4CslFcq2rTS1gxE48FTFHuBsetCmTptAXhTegsaV02hN
Yvlm96tvpFbfSGFEXNogUNH5KFbJFmcTp8J2bX3R96y4GmLvSbNUjfvQmuPlRb+RMv/TK7Mf
+CdIclGo3XduNER8LjvYVeSC9LNpJrUtXIXKunk5cwH3zJxYYlYOSl9+Z2O5OwXGUTjuUSig
X2056Gxt7QLkaC3UOMz66MCJ/wSDd7zcbJ4/194JOr8SPCcN93jWKy56QqmtLpBW/IbKNbO7
EQa47MiqIZBsL/0pa6e78h7MirNqliHw3PLWJne/ZA9YNyt2kRldygkdnwE8aBLlXPlJM7KD
F/AijIOLw0cHUl80fNNhPN+QiG1iNRW7Cz1A9uQrzkViCMcX5EjQxPBan0vAzrKu24lhwOFN
mqJvl3H6CmBU5bRXgAynLl7JG3TMpum6zPNQ7oClR2b7QhbV6YaBT1o3c4UCiS2i3ji49t2n
1/7Omqu9JphX/QfWXIfIYyTDkGku93VfVu8QmW3r6EBrrdS37E9lBFM5U3urxtur/LxECRcE
EbNwkeVrLlA/qj8rrSesQggUo1lBUNycGj/eV/l3uu/19308fP5OOBynZOI/AD0RHXMxFPUD
15ERlqKBNeE4G4IqJ5KTJcHa3ezoFEyzPVs+EiTKyprf2WDc22UpCPfhmMQMlXnMcP27qBAa
3pfhAo40yTg6Iys7QsCXMdfMKWuYJ18KgBrMFuZF4tdK2zLsfjrsKIFInsRAdSVT7lM8UhuE
twoBalQ55WsxBpjNndExszJPB4uhSKShgTO2DqxKf1ypUYfZzGZrVd12qJXI2SiGwnszME7t
noQRIBSU+dcvK6OFIf0nBa5zoOvKmXbk/C6HaIWffL/B5jsdZxkxnAaiMGtmnOmEBjTVVfgV
FWy86DNEcEy8c5t7WB3yciGIJSeBhmEh3GLB7Ebs1+jH6ax+7XWO4ZiTyOgHDgQNO0pFoQa5
NNdOvPneaRuv7eKLKBYoyUPaneogUI4J2lzXnm85z83LqbQcYbsmTJ3vvrpJLLx5ZQrDsY9I
oqLxxdNnrE79ndV//r8HHL29NfeAmcwpknHfcgB+2ovu6WxzsDUfXjpvvdNozrek9aj5YSpa
+KCFYRWKMJT0einF9eF+zEQCqqj/XAaQkd0n/khgpv/Gj3/58lk+JacTsmSb/sTxk0F/4wXX
rmAoH2oBTYfIOf1IDC1nulM8IYscIQFmXjk6/4FrI29zCjUJRG8NrWR+JKZGV4yX5eQfPvOE
NsCWtwFDBmC+TglceIr5IVK7vn1niKOj1/qJIJZGfWwT8/FCaoRG9uwYUrJBPT64NtaG0YXl
9GrAArIJAkMCvhAD9dz5rEbvQA1QxFxk+XJQxH5VM52a3N/ybUBf9XmKvFN+aYrvKLHAHDBB
Z88zmQm3rv2HPpZMoujIj47eUfhW+u1m1exgRR8ibk/P0Ct4rtfZfn+JmvzzZMKidVTpW2ty
pazl15BEfcZR2vUBBjOV9XSClLSBUitlOER7/WJQOo+fM2Pys+atHfCkbAnIoEtqk09fchSZ
fWeiUEOVFdOaLRiJnn30RLI3UViKBWSMDVwdB87IjQF3SWY2lh9GSlVPe65NjPZm56BPoG1n
ix34mVoz3vyeehWvL460gxQmZgnYOa4mhkt83MV7Ohvz5NapXziz86Ol60JOUNzXehLx0dni
SKSF2Vek6k2Wgqi+jcSfrTyKm7mn6tS16zI0+eFqQXNgunUXCbGq9HmJZEEuGU7nrMVVkIK2
ynayfh+n39MO/LevKX1+Ti9D13u1yWgm9EhCDtSzvY06RPYTsMt5HbMxj8+8oB4UFndaIgZk
M2OvXh0FXfXJzau4XV8T7mzfYmggcM/NjcpecHDOtOHd4Yk9r121HRuPIHnMrdT4nVjNVhXB
n1mWUhFVXIskooS+tLIC42OuictdihTBfQa93gqiwWcP3sYL+Lq1F5bifBft3WFHBqU/4NS5
oBqKveYiY3TYS+6Y5bmsHJwjoSBiYbLbiS/9nDWR3WmbCg9Xzv2wfVMUA2SnxZxrQGuaVxqw
AzWJhNjn0kPb/tEpIbZJ7S86hzv6nrIJMAsPpQfGB1ssnbLpcjBiXEXAtTCvUo5vXiywjTKn
P5vgpbTIyn7CrbmRaODEwU95UMLilBr5HnblVKVZpNNC+NP96WXc+Uj9B8IXbJJkCUHzWs1e
0bqGXu6ajG0yf+G3Vj/gPfZKe2ZkTbZ0WKyvL9nGOFoFh6jSqtfpYQG1Uy0sXx+BsjvgLV/E
qVamauO2HYNbBdJXgrxjosyE5xdHJlSapqaitRdsSdmmXvH7TUKRJasXVSsotXeaGAs4W++2
fh4q5DxNdZz+AFFzcpxoeZ9HLLkV9h/RRP62Nv6IPzvmqXumuLxzMuV24UivY7bNhebaFeJD
GXMSthqf49l8yjQwYmG0Tfi8NbfcLyuo4I51lJn/2h0SdLk2FF1RK5Mh2IJFfcnLNhgevzsT
xHHwAhIPvqp2D/IoFix58cAxrs+NGds1KlS2fYfeh6t3wipgurABZ3WVy2eM0wYnEx9VPg43
ie1ZUtd7I3U+sOfhZsEKOnhXOTXC47EOvIsHC3EK8F+KmOeQ/C6JvZ3Ceks3701YTHDs8hwk
cST3+I8eojnYuaGtr37y71u0Zm7ptHcLGHLTntdCbyJ3LqwxtyE53BrmEGGakDW3uuZRcFij
57iNN4v0eqkrcIBQYdT9wQ+DfkAUDWB3ah/q/7hG9KqZiD+WG3RSwHIBNcRnFD7e1ubI8VgQ
I127qIUo85/Aq2avhu8i5SCBgG+PT7/7A/KCuJwTnUv3Pj/fWhpAuBmFC2yiQpwXn2QYG39i
6q2aZ+bQVJmcnGrtUQVrqaUiBbIiAj5AIisrOWUx8Ed8wH9NY9dPtOQRXGY+vHJ6JHQX3KMF
0FUbAV0VB+iqhbBfddUzBAm4GSMr99bhR/kVLstyL7+BtuoDDlVGDkOMSmgP/mbAS674WBNB
9m3jXuF4dgIQlSQ9NtpPTNSv39sQGBiqgQyVC/6211AXFhhBpBJhqyB9g65sfTCzeW2C4dAh
PJCgJgV45DlGm6BFcM5NVVy9Fpuq+gLTSwUDuvPXyfPMljp4aeEmOjl/mVhRjZ6tVz/x2V9+
ntje4skb9eKcTa1BkWUwIqDIpadKvzBmAQTvsEDNXWrGPPor+FXm5QtclQyJ5+rT3CvlXQWl
gVHOEAvCqMsdCDa8kyrssMhOXqbv9PnXjPq//fo+gSD/jdauVKRQKWQ4frhDc2Nwm8dHay9w
OYukQ3edGtH4e6pW9PXYsMsMekzW6EaQr71TZJ6GXoC3DxCuQ+6ND4u5JlbldfHuWjShdccp
wUEVsv0LDJA7QSI3vU7miB9r31O1q4tWC/LMxR16FJXAqZ6UlVvrIN3zYJH9+jbnBZP66gGf
imM7u6yyPjyevX3JuOghJeZ8csE+03qmMtuy2ebga7rTTCNHOeeBkZlZvCbpvLkBm7Jh0Mwc
CcBvK3436xInod9Zvjdcs6rX7ZQAUvJOqIocvMelOP1oOCUGD3fJbj1WhXjgbqq5mXDGhhNW
jr4Cx+nMCE5uxrDKWYmHoMXUgm0vRN19lTHEUuTYsWCPFHAsCjEdlbzGgJ6mIoHy0XdzZFd2
vOZByzs/ebgdW6tfFR4M7AKQ0csB204bLyoSqgxbPS1y0tEBwpjHQEnx2oLPo+GMQNNSXHAj
Dd4anHb6NQZT1qDFfWZjvE5ObFbdq3mYsck6rDZaUrBxE5u+vaiaXrhkMRLvwQhU6lfWGfKm
i4qNvuy+4uIkJkNwA3ZNX5sdPju2K90BnhN+cUG1KW4FrpGih7xiBmYCyvO+TC1SQ/eUTFtX
hHcPPyPgOY+eeZajA1WdqNh3UrAOt7zfBZJav/ffvvmf4d85cp0OG8wnahEAP+pO/2shQexW
8p4pTCWOYdxeuajMFmoIH9SG6pOylwtzMjUuqULr6rBh0CpyS54LDq/pgBrB3T6/5p5uFYRF
AFXJn5sWh4djR+WCBVh3cN4crRCzHUUY73YvtOiHeFVBW+wTSlegnhZFqfEtU2k+4alnmc3b
GOJkz0MiLnBU5wJDbvmlzAOBxRWTax3PSWu4wbimrjm4prmK+ORChfWGnDw7mmOlKiVWZXHM
8spbbqNFRvJA0RlMJa+7Dn4jweZgrHsgDUGvXB5Y9TmyfnPuB/yjuarardrZpb1FDSXDbqS9
FfvaRgjdNviAVY0dS+g3Uvb5kRFxkPqytI+ET4pO0sjT8Iryby/g4TFVkBeai8KZ/s75O59O
Ozzossvab6eRLMx16KtT+9xZDnTD2y123Y+bg0Jw1OWfRHizxhOa7LURb6S+VzOZDoKVrmV1
VTNjDbXW7wz7HW6gj6zsaC8qLD5mUfT4jdTQ/c4qniu74VZCumT7Fj/Hv8seYWo42QsvMBcr
Sa5Ges+UTlBWdvTxXIqhn+cYbo4EeO56OU92ArIxfP7oJMXUb4NJomrhru/gb4Bu1IMGWckt
gysyyx19Va5MFkP9q9YmAjxmQR+Rgnlucuo/vMpkbgAav663Cb4ScyR+qj0y53qduTIGewYw
KmhrHq6OhGpo5nTJjqQg2Z52P2v8OP08LZPvBx7wNgpuLEBla6bB3qbYOoe3Gr+1UyR+TgNO
FJnnEVgQ5nI23v9adBRaXMT02znD5fK/ysm15vWlr2Kz8BxxuTjr8YdMB4PLTAeUvmU0cPcj
ivkEvyOAX4ditVNBhmWDV4KGbQtqp12EDFoZcBf1vVNANvYqy8VmNSk5OwcC5ZpFeh/I+vhn
/jhDobETweGo26X+NeNZ25cM9oNsiBWwUmJKlaYvfyk4GP2Z4rF20YuGprgPQhYujrKtL/sr
+9qz5+v3YmygkmFnBy4dozoJ1MmQvvj7GP5vYMcvL5yjIQVcTQFXi4yvv+PgLPxMRRE1K/dd
DnfxUrDuh1e80IsRWbTSIL49fsjvdQrZI/taeNrExGgberZgH2T0jVTw28pGq2SRbfboij7S
A3dN1a8u+ov54FodlpIjjm7I7JxYZKDpd9Q3BUZF04DapW4dt2/0PDGv6JnDJEGYtea+dDzG
XgyLKzccrwTNPTHtdR9H1R2/QCynMd0y8yKoL9g5NdMwNmgJUaQx1dosU8OJPoGCJjhEnIiA
7l86mlywE2tKvizPUWv9UaRjAHjtxs4mkMH5GfWzE4pk58AEIGuL4Wbv7MqeHAh44y4nDr9t
elFdM3/PktzgZ13f/TQVZ+S/6JHW/UyY94WECLOqaSISfYel56NwYsXGVdJhr6EjnxhEB+Qv
OY4W6W4ZbB6q5shO75L4M1zWBl6FHaXfbmHGfsOR5XWv0TGOeO0VBBWW8kYqRqaJHd254HHD
xgAe5K2MUKVHQvpfobSI8Y2jbFkrKbMDX0wmMiolLsqZmQI5y5EYznnTpamzfvyUKYFk7rmJ
kDeZ8DDsMWZ1d8VEvs92eU/ZWJTVjE6ftPmr6Jfz5QVxWKUfuoYcs+VjOJNcb9V2V8xjPW0g
S8p91QTCEnQk3pQPTW+5IgGATOeQGeobou+mfMrwdEJ+0HQszYTfM0EnLOyvvsL2yTj8dRtp
Z9wnzwnJuO9Veq1F5zKD2m9/khOB8zTrnj9SvZpr0ZUQPZa54Y5kbj1B8VWh5zg6LRKjb1ra
C33rIbAlI404Jfjp9Wu/b/X+oU/tEDfcwWGRwZd9qHB+lJjm6iI7+9xYd1h04BrdcqWU6qeM
VsBGY5YpJUh78+gxPoF++6QMnb91KsqAa+DAgmZZVMRpLWzeJE8/sFLQUdQ83YtJIDl9Hg3G
kyfoPK9eIsEMsO8EjzpDvMeIWhR1FWCtnp+83M7BgiH3QqhJ2Zn0mPJDGQ9DS7PXKc63w3yH
pN3FW2GoQOxdf/OaPgoXriNoF7ig6jFyBi7JTsGop6une/D97mnwqmCvVLlvZ8ccWkmLxhXS
hltiC+6YplZB9bXwjAHxg45p6m0vvvcxmH9PYJqwmL28XXDQZRqCZkVYxRy4EZxqYb3aaiDG
KywM/0BHSKyOmaHBSsehclsEVQNeQZI6zzN7YeWZ2V2Ee+dfVxOIwvlVowhL1yEBbjtOIn/K
pKN7Qq7DbYgqL16X6eEugHiNHMpkxBHB9vfYWZlubqyscVW2XezCM9aD+5B+1v2BEbE+T0AX
h6BrXo3faPrQ1CyYbDKd6v14O/aIQyu7iEpDh+3gKZ+7b6XJC+v26DGw4NQhZvqbAKIZorji
RZXzuFoZLjc3MSyi6rhL6v2wuar5o8Us0xoVcXoM+DKLWzwsjQyKTahE2+p8oqx3edx0D7h2
1r/qwURPqD/BooQg0P/owO9KBfQ7FpupXFb+mahIEaJlKu+NVFXQ4PTe8dmgaR2NgJZu/6y0
rkEo4H4IlEgHfBSGLNKEIZC3KEW7MZAHoNQPcj6/ohS+XFxbKSfUrD+TTaQlS94ecdY04fhP
1R571ZWiFJ+0L9dQPyaMyRoufx6nIdKlRJOiyYBToJzDIZScJ9MpP6ebv5ZF0LwG5JfJnZ+X
MFkkY4xiZFfx9LG7KxXIQEsZ3SI5LhwmALl2xWlowOEcCOAKoJggko4HBLMT+hEdJdt9xIUN
mnaMU5AM3TA1hyI0Y3TMRm4Y94y1TdlaGKwUAD9ce3nP6t7v4JKU1Ht6E/1v79g1PIkx8kcG
Qs7zc6B2nKDeEeLNKWXoRAH6GOF0r3vmUXMiorr3UG5tSC+jLZtI9/CRYaFAYwV7saEW2xUh
4ctUttmP+zEaZfWPd387LCCaxZ+aVErTkZ12DtTAW0XL7KaZWs1HkNkGE5EerUjmGpEd3inj
+0YKT41UUbwwnvnEbFmc2tCS+kbqRlgcvOzFw0eFFn2FLUCWtk9MN5zHA8O0ad53mAyQHGjA
4znXgnC4L5mc26lHH3hirDAwntlaFlipDMWaSTtT+9vdfjLJgqBXjlZFW44be9O6+nO2NAWQ
gXh9JWYr/qYqsk6zAtXKpaqrJFwbu9oylumUQqI9aV/RKm7IeMZ4IMherzw4Amy5ccGrsmK9
JtOSpldoJ5Wr3IB5FyXFNuWeCclSqDYxa/UJMFbLok0Lmgk3Y3J4OU9huH0eFu6RUZq03aup
mbX63XSz2KPTENevlGbqF+k21kjMLZdzYLjaY+SGQwmYjXsij3gS1SQafLCrZHLDxwsfs4RQ
2k/UrIjoXkBYHpXWZ9dxFkxgEvXPauObzOn6C6HBTp2UsIqwCghHdvmRTMSD8BYB2j+pZw39
Kmxy2U8xlN+avKrdSuMNSx97WTck8cTmUY10ueTdqtuBu0J57fnC0cjlx6smNYru2+6ThUe+
HqTKHYdMteSa76uc6/CyilRpPS1ea3tWYQNGKBGmuzQrLEzW5SEsy5nSSbr6RyZwddc42zBx
YTJwi02mJSUxqGB3mAWX4TDQ+kwmuGiB3bZNswEPouQelbd4B7shDIacmhTrD10LC7LCO16g
BHb7BuQ2h3Rqb3VmU/zQFyGewOWhIgbAtli9SIkqMqnCRuBuGQuOKlY05fQVUIinl4YAF+oj
9U7401v/27r9j/2+Y3VhKfXw2UKkGE9QU5VVFZVhF3lJq4gs6Q96aHdGe4NGHDUHh/tlqtvn
hDGO3uONFFTbVjkUdrqJIsSsmfNqxPQS1IEqZItl5JOOpaubsjh55qbUQJTAlabSVIiobNnM
5RYtZhgKi+WsgnH2QMSDBaqsVavOzbqPvaimEWiwnN/7cPEmQueNFK6NCp05/TTigMfjj4c9
iOjiD1bQRWGW8LwvzZT3HhHkoDDUlk8HojM9U8MkpanqGXwVj7z69EvTxBm2+m7j6tjZ8GUg
7jE7JmfF8suQlR/6jBcWDgqedjSgC9AVEBf7rRJjmRExpyOfZrHImrwnGZ/pr8mhzgWuWhUG
1MscQRXIxNTeRpcfcxhWm+5s8IwK8o+OzVGMedxbepztGiM1t6beXRTFI7CYcZcogYoirWTG
PFqSPSNh+RyTnV7bIXk2IeiEL9BNy7f/OklTnIlC0ImIVTddznqFqw+h4qbKZNDV62PKXlU2
LBd7rhmaWNQe/E0vkKk5tv+brmhLrVtotdfjd55t1omMcIrLlpl28Z9N1MwviCVLsFG6bP+g
tK+/hYxBoIkBX6DyTDTaJ5nvCTFs+WRpZT3zWBtNvV76kv+WQtTFpzTEMumx8e1SB9qMV2n3
iXJ32pKmVsvskMWLAdX0+1fLR+LtC5OeD+p6PwhLTp7LxmCdZ0BqAsOZLvuNPPquKgPHs2tn
Xh53wSW04w6Q2fboZNbLMjhkFtBqRXGHpOESAfaR4Y2UUHR+x8tFDwM7RNAENzwXEYArVZhI
uhb75D+2UP8lYdW/MqGfqdSjwLBlt+3X1d/+DTwPN/4NPHtlDfqTkiQHBYTapAX0AuBBg51w
Yhp9QO7nb+rPrqZSQxFz3d6vjgOFAFuS8ufAQ9bA6c4JTwJDLb96ax+syPQmxrSEmG7lVTTT
KpLomI8b5FDKFxgQBlRBKzuZcJOWTC5NXmBH5+T7vwXPeAA8w2aYnBxjjFxk13e15J+PeJHG
dakgLjxmr2YpYdPamskikiSq9brCixGzxp1yK/lGMpGBdOOEbDlDw47EvDKvpLQFg+E+8lSz
XZVFyW7lqxWvaWadeV5FJRCkXh8vsi6Nlg1e86MYc15ToXTFmde3fCL/JXf+rz/+QaD663sW
R4ZgcI+cC1k1wV2W0UhnebuWTwcxCd+pHBBU9YeHBPoGgvobNr+lhsybP+5v590KVXX5UfhN
eLSm0EfX3IIqH7V17p7vsFMrAg/f0Qi2zKpPQ1An2xqetCsgoWNLhvTSPoLFi6NtKYeHpOV6
1m3DLhO7IMbKfmHjbEvEw/ANDstyDDd3ey7h+9HFb0YzRkFiNY1QU5aLaC57PfY57vqJiYI6
GeWKRYu+1/pWzIYTStMFloA+bGaS9/iV5Fao/fYPXEEd/OrjSw/DtJcPH0b0wo8MFus+DEn1
Kww+0aOH5m1+MygMqiAwGXlYKLcLFwbgbk9xFzXn5l7NMq9zies3W/G5QfAtkNVg6Pi1kFin
B/HmkYpiCu7ph0FfCKwW+3g4+xQ/Pjb7IGdlx/yRWzKYmsuvO54M1IiaGE5bmpmlvp4VbRIH
LPvkbmWrUscecujDRV3f2cLeO4/lGcEtrTRIRXrB9VNpx8I/fW2k/aJTwI9rmo2pmncrd5fI
bk1bQ4Brq/T8otwFyUZVIirNtIVUs5nuwXoVguxVm0ltzV5tXK4mE/mzAb31cB/5hxTT+Aej
EpYhPs7M7SjAmYDipTui/r1ZxUfODi7HtFbdLvJJLpiNOrhrJkAQuHaHEqfNqQ1qss+xZBmv
Ri0fK5ghtpMtB0wycnrlIt0Jh6Gjk7ZtpNe5QU3oZqdGSErjir6p6Dxx9ODYfFuYoIHd6xfZ
glIbBd1Qj1FpPTeJasypbm0j7w+2d2dktTxvfp60gZAkzJyfvPBiy1mtZHDlYBBzSzenmCO7
7aEeqVJ8RrzV1vHAAZRditzS9us8FC0Pscc81qRfA4J2XKOUnyfl1F9sezYz5cWLvr+8YR/9
3YpB2v3625OogcHQGXuqxUa8bQBtteCHyjMm6AOmufcR+vK+gLlUrBFfPFlzfPvjEumeZ6KK
9M32u+4tIqsbQHGUEUJKRFwB2KlxGJOQEZDrPJhBlXVLbfaqLJAHsBvaSu+XBN6K3Yz9cpeu
RigodMZ6jSB4gdh4deDlrwLxRzd29UZv3YyOMcf2SFwkva4u6ldV4t2GoDJXlRAVnv0bwcD1
pfmouOZ4M+ax/Ncyqums+GNZEGjwsWwZRR6ZD8TNCLjxN+QkDpZGtcbbpE6nI1wwGJrNdHxB
O7i29VUJO93qgwuz9IQfLi99MeIrUyeBtO5F9iIx9u68Okqo5agzdqDzmYwJaQk5QncgEB+u
oAc5cPPuoaDNFHhsp6rCgIqeXrnTsQwE+aZXcvNmMgFj43P4xNHCCpLqgtlmiIx+eTh98HMg
2R2j0UKQ4xrDhIuGYc0bVdaCKZlD6b0gzZKsp6M/CuSmIBGRLJ+wE0UzCUmTW8jI1ts2zpRV
/aqr68UiP6tjx04eFqRoV/UPXws9Lqzi9452GfRxN8FN2Vvg1MMn4VZPL3OkBpXGINPopcBK
b+mPqxkK+VubH6rSv4OAlqysgEvXceMl4U/1S9Mb/YcrI19XjPTT1M65IzMTESMbt2Et4JhT
285007vT68QXT3uicN0BjFHJDW+qYTGf0PuitVFqLs1z/Yc525Qy8abFsEKxTewEMa/R+3IS
EIiV/s0B3g22dL7nzE7/gaB2V46+kMRLOEsdaKXqm1hsj4WgGIpFDUbcB3WBHXm4IubaOKtn
kugrmFNA2gmk9V/WaaJ23MbUiIYqDjw8viF/sTcnE8rthXXHvkTVq/1A47Ad3AtACjqQkdnS
ymr4COY25MLdrQGU4ECh1W59CVs586YH72djj2Govkbsc7JA2K+SgJdsp24WjffCRQ8KGijj
2TNDC0s5QPkul3W1ltKNe2N1EefSbBfXy/n5+yDpYfzmlgtmia5kzbhyyxJgv8qaknnataY1
qv4l1aFM17M2Pgwfc9sEr3qTtgpfAjMT8iRkmVkc3NmBUfCU9dNPzk5MNmE8srZSbcSjcEe7
fyH2aovCOJAOgAU4ev9huQDeV7LGLWE09dH+bJLiI+o0q2hfSK9TQnCo/zZwrrV/G/zsac2O
0zhcDUQTJ6Vt0aMa3cxbFktE6teNKpBxhyJjbHi1lEix3oQCgkocara3d4i8DdTykBMRWdAj
bSD9U+ZR4WIS02nXzAXupv3sKpZaiZgz0l/K4XhwQmHZWVlFujAEERazKCSMrGlk4Xfo0HLE
yk/SDMPONV8YRM8uKYi7H+pX03MioIX6/4e9N49qKkvXxqNUSZUDaUuBUoTYYoGiQiHzlGiL
YimDiIjMFigISJjnkGBRioAQKUuZhCiUARIBETCEEAIyCoSIEMZAmIdACBBC5vAdq7u/794e
1qrq2/f+7vot8weLd4/nPGfvd797eh/e9hM3ZlyqM8Z7xvzI1tdwS9SrwGHfdxORnEFVix75
G4PUSc09NWmhKRJ4WsH4/BvfznGqSeYiKYxl3VYcKM5Xpn9OSvi9+Pya/nefo//ttayWpWg7
6LsVaGERq7pjhyHAxd9ciBv2Vv8b+N1iB6f8k1WLRl7I4Wz5nd0zvk9sbHkx+5O063TfkT2p
bqSqV1plqPpc98aVCO3zQku6X04oMWww3FIotSkcbsOk9zkMHtCzX3jUPlsSG3rSeE8qnLgJ
wgfk5FvAAoI0cpDjUDXUBe3zlUez2ibyixL1lgYZzlxd2VfsUxPDlHP5l6u1JMdP+N6PtY7i
jE8sfk23Igo3DN7JN3XNYzojQqDPJj2/ekmrmHq9oi1dcjndEpGeNLJVaoDSkyAYXzuInLt6
bt+0jKv/vNO9sbV8Xe8dNl/A6B4hOlV7UHPUpx4syDf2iSCrCn127XCLQEbJhrqmFcWbMjxw
zfiJ51lt3xOjuG+jk5p29BfO+hOL/ZVYGI63QjH6AUTdqNDOsKZCz9t5YvZGW4XvtXfpwGp4
2nljbPmHoLw0Q43gGlQha7SuJ6kmeIEj2z/zCnFM+m3MfFvRW2IDvhIisWj6ZQCmaHIZ8CqV
AUdsRMXl+MpHPdnZayFeyN7A5W+C+Mq/gAVQ1sU3Zeeg2oOzmvv9uLH3+ivddaW8slX+6Zmo
K6ybWPth2fOu2RN7xYqjjL2WiNDPzd9F/GGoahN0blU+VZARRDN98RRPJg9RLKXvUcd56nPo
i2W37VQjLgQUxNmY7Lf9vKMAWZ6EPglmBuBgFobYfEnwymS2MGejP8NCOsTTQdUqfIflhcyZ
bTt0kgAd6YuLmdM8VWGHWvEAmSjoOOffXp08tJzY9DJ/jDoK0TKTYh0PipREdO5F694pQ/AO
Lay5tIp8TgMJcUIeDD1hVErbd8ISkTne3fUO49s3ZHLVTFrtmPjQi9fG+NkylpR5wnBJDD0W
5kbgr+Lk3xeWBbajaTGeWMBJ/VgeZfAwJMBmMbWqrBnY0J5yagFKGEmhy5iBXgmh5tA3jF1l
6nTJH5lXfYdWDSZGxXw/eXpFP+HJBcqMuelkPKXPTxSPQp3cIg4x7VkrehTWMjYksW0pWuD4
GetB6rpwyHETJbBTmc3rSU1159Fod2mqSDFsRKLqKMeeinCdviexHJ1EFqJFs4w+TcLw0EPk
YvzlGMWyfF5ILU5zGH+bJZXNHk+c95NeFKr1Fb2BqX1bLJqy6nuJ3KP2MPQANN7EpPt+7oGm
wO1xmyDbDhxNFN4AJaeHmVi/S98ANi37omTZNRW3NkEXauTZBGq51oA32bxj5Q3MkbQuQkrf
I7u0fWMC+nAr+svfR/s9dsqtzhu64ybtfCYWINwnzj3fbXzAdjjGQjKm6dJaTmm5Bq2HsoeJ
8UXKYX5OpE3QRSrBaewhUmxSE7NnNzrTZ4mW20BUjB+Pa/jteuL/pYQ82SjBelsh0qyUBoKK
yDYw5Om113xZc++kLyx23rhHDaVa4lxIaLtkvFHYpQOqis6mC6aaJF8X0Vh51LsBhBG3BESK
sHLGI8WnZNbpbthudpCqqe9kaoNkn/lcaGbyHqMY9ATdnfICfiAAMz9wUOCSdEnNRr89+90s
OGBgRFbuPgLcJy14FtIpvWSi3EoyhId8YNDVYgiECP8FwUILcJthZz4OkX6NM1lDepwxIvIY
6ZuijHg3QNWe03sfmRtntzJcMTBCBfrZKNBvJzQehiC6qxAlU+65kZGoPa8XZNm+3zWm+LK5
RzE14LxH/ZQnw17x3zXZfuOG8W71um7Pf42Tb+irHQvGApoj/Qt4V/aGhUOx9zXORv3XxvV2
bp17GbinttfwZcwFf2JdQTYmMqsRUw/OzhxQ9yzT7DtAWNjwHcwdKSBh4pQehqS5lrbt51hK
fhhfbm/CeIVybk5viF2fiBPTRxftqDYdiP2GVjsC7XrtX/jvgUUZAi4e7Rd3U2W3rb2BBUUE
rRJd4OQUtJIZIL+bxnpB07jJUUG3SG7vR72YYpO1/TZB+9BXpO8RT9NfHFjzrz6bPVVWaMDI
77GFootccL6s6LpozH01I5MfWN/Uz3MSKdG0bBua/sJeX2fOsq2BvrQhxsbCmpdiXtG1HLEH
Irvkns4MV9MPZfaZoUbYxcH8B/uqGNzWyjBtGiryZEDRcuJQaq9Zvs0Zbifiy65kfOeYjIB1
wSQ1vUuIl6q8kDeLfeGhELVrnXzIbIOTW/PKHx3FTSVs6QqO1QvzzbR2zCgPntvuO0h5edO6
TWDucqc9HJlc1+RJ0i1fvZgUfVUs1Goi5z1yCgqti0MhDtDknreOE61tS7qQeWinyq/FHqSe
VfrjUyZKae+n4NeIzGCuSonPCIdr7OozdnyDH/COxL9DDTbVDF2EZ6U5JEvOteOHcvd9beiF
3F6Bl9d4LzJaS/uFzoSZoQLsmZTbbH/q7mVkiNegSb7yhW4rXb+UoJXUYye91wcIGsCymV+G
tdyTW6rmQp2R8N5zeZ0bo+S9QrKnx7lwiV5GKBFweEfZ8zPS8VVBVtsM4Z7qQlYWjlyU6G6v
u8TH9bWb1Kc2wVUDa48SCJEKjA8lRbN+bz+8vHaffyjl+oF7KQA7nz08C5vFtbS6lRDz/3rf
/0f/yT0jpkzHZQJL42OdzFzDB6pN7tBd5JZCYJccWEI5BChZjdxVwI7U7nWzjGKPdG8vnb34
QvNbxNe4DWLTU9c625EQt7OKtwYjukt8NLzUW793mHD0fBIXfdVn7icNXMH9z/gLZg1kfiPc
IyKu7sLwvtwwt1GVlOXCALBp31Bn0bZUpUCX1X7c/TK6x8mnySla9zHbivOZx7989bvxOKis
5+5iOACqoZSuPApaCdCJHBshHG3t0+MEVC30Sx30HRyvuBTocmzCeyfO6jl6gDvPuhd4V19W
dRQSURsem6BWpggEM9KRdTIFgCI6JT8LbIUPAXpdBTUPnDamiHVQU0FSECQ3cxN0kyMJBAgE
5Lihm6AlgNoijbIOKi+9+GATdNjkcccsRJi7iixhGnDsHspecsYFztxMVhBkPAYhk3+winJq
3NhynfLPikHCPaWZlFWCLAFMBbhxAQVsuAl6v+UfP6PC23HlaxYVLbITgfXKy+nbb7IvxhWa
dj+6W+K92FNy1oSw7ABvUT4Rm9PXouh0xcGgxQE4Gd0VyflW6eDvxve3ZIA92g3cOxvTpIEk
+1xRp7uTH4zukTukSVMOKS7nNBhvvGjMBy/a674MLvQFzk9Gv3tfAeeL/Q8fgHO0DpSO5eBI
nb47tHDlx+lmMDsODJy8DMY8foc5mh2iG/VEdqCXKbo62lItu/sH8J3idck07Uryg3xPQ6rq
Joi1PtYmUQ1PTPdYiG+vFj92L78TbkmfySoMYa1bNe5+vBskMVHVEh6gMFuC0ToQyjr5XQkt
6E37Q4TbcsbT7JvNrdBhRg1wCvWXAH4RQWD3xQFfWKG81r7HgmhxYXK07vobA4QJejXrsd2o
/Di55+ITLcqpSc29R6Qez4vo/FfjED2dAqct+GQeWInAy94wDypejl/UTxxnqYLfqLZjMtyQ
A6tzg7xzyT78oGrSKeiu+J23crCB3DOO+uLdZsfq2ppYAvlp8vsBB6xmn6RzckBELnSExZ08
vbYmUuPgzERJWbu28aunws36ZbzhOythom9C+hl27fXat83RAW2tNwHbMsD/FcJvvoRqFMOm
CJx0l6LoBpDpg5KBWp0w9wBK6uhTPfLIggFikLMxGAzOfdRDy+1UlThKkx+J+qtDAZstS76F
uvBNd7oOaneV4YZv0IJZopqZtO4DOAn1AmOhBLdREhyDS+ItyJ2/NCPFWprLclzGAopmU54z
7v5Oajv5QUs8dEoSVevPpaSt0YNVLmWjF2LfYDxFJl+BtUwOzk39CT0P3c1BoOSpLGuRJkFg
9hrMdpNj6RRYzZmppF2tg4hedLE2QfJXEunnelkOd51SKwnExwR9wHxqHSAhwtuuI+9X9C3u
qGrJv3U8cq1ZYPbDw9jlRbL1SyT6ZZhJEKF3Gv6FeA28A2HPghW2dS6PXQ8UwHi5OWTa2yh5
gnAh9t48cFB7VTnlDQIi6j4hovQSDvIYc8x8trrMsTV+wLuRKyqyqxBGnqruq8wTw3Tbngql
Vx8VOfJXpyG49KKn3BFhvukYhh4o1SqnpICjZgu5Q1LEJmilGy15qLaELGFwh/L5xlRfdZbb
iMsVVGEaSJQldSb2V460BpH3qPOo5GTIfA9IdNWUzM0IWLfx9BuTety1RBVekeO7LCpTZyi5
lRVwWflZoqD8FMy9vvLAsD3XRVmhDIm3eidx/hYcr3orprSIViXwdSL94iM73hA3v+hAPas7
XJr8tmNuJO/YJYlzw5pkuB6wEIrVFJF0f1jnnaXKfkK2yJcrUwuurZH12vYdFQtfg5m+pZhv
AXA7jB2bhjdB9kGGGArytLg0gjilj0Q3lmZ6sk6eXBDz2oHnINRdQvfUqFTjpLYvMuwmHyLx
8cFRS8jUBtWt5X2LUYWCo/L16TW5tTDLmanzeAbDyVvwpXxtfo04BRqUqWoaT6WFwobusIvK
bCtEcJeVOcZoRJv4oEXGwDF7qdFxQe8ynFUofaAWMqCnNzTzE225FZUhNyokMjeALvlnvWwm
66T8RS/PoYai/qqWOWLtTdCf9XIeoJeZf9HLYZQlwD7+qJaR8ChpJurP+rQb0Kecv+rTf0PZ
PKcBvUM+CM/jVwGnKJox1pugVw3mmmUez0UezhVTo6M8O/EfLCIi3tEpFzuvHo4jvQbuCdyQ
Lysj7pdI2rT3I+JIBcC8+aY8tr6GVIY6M8P8rmiUEaUpzd8iXI54ywwTKYP096Mcyzww488g
Tziuy5p28+Y7htdleId2/Np1SDrfNf8kXSS/7Y07BP+uA89xAkmURUPcz50kuXcRFgQRKaZa
unRfnkbqr8zZhyfnQ4Lf5MTjqkbPlQikrqDVv2kmi8R+TA5O5ntjpZbJCn+6CWrLPSjhm3Zz
v/fsYpepuEptMzIFa9OQnzjOCnA4olWhsVqUprQuBbpcIwrPNx4gCchWt65Jg/6UDHRZonxn
B4va/cYKpVi/bh3U/2YD4AkvOntKqCzChgG8a9uZ+0sH0S8Ib6qy0UyvrkS6hT1xMSsr34SW
+W56xNQc9VpubZQVQFNl5kzVX0EWnek9Kh5sWHfoM8t3dykhpLWpInke/YZ5yXvEnSC+laHq
nyLaZfcmnfZwBJ4864tVEg9thhw9LHn0vAHlBHmoS7VbFnTZnc6WgV9Z/OxPtgldWAn0d6N5
YONTguDbC5DzyuHpWOIVPvkF1yJWc+HlxzBj+btlX/FUGWoXSTA0AaEjYu8vpaBbu+S6662B
L8ewl6q8LTt4o8UDdXVWYCFlqkRumfDFEsz3hU30NsRbkT2cc2vfYCxl4kNbxKXrdXO4Gaii
+Q6cujjw3S8OsL0zcsDM8qhwnMpm5SuOX48PqVlnUeSRr0LNtdGMiRlLG4lFbhJTFElkEoZd
iyHekEJlQ+VCMpXaFAAp8xc+kqUfTtwYAVT+YbrdA6bkODabu0E32JclsDgjaOSvL99n+JB2
r7k+IOnsj8c4TM0w2Rt9lxTOJL+fCxvYzVr2WifpLQlKq0PnmO2/QM4xzxyrhORzYTZ6bAeA
2XBjXn7kg0h1SWwP0SDe7Q8tGuJpM6vRTHY5Q16jCThZ4XIIej7EF+WB8W3uViyn+DyLvxi/
V+ieEucxCd6Lw48UOfSWoFP7LoPJL4ArRjvs7j8gkRYd2HNPS/1HLQC38M7PDmDAL5QPR/fs
Rt2LzfcM8tmYpAETN7/Ih/EXLbSFSpWOBm1yXrUla/zyUH+epbjCxL1oUv7IByFoeuD8/aI9
meTSsEZuLG60C/N2wCk49DjcLuZS8/1UtzcrH8qYvZH1qrT10nZoa2anr3aOKk21YGVH0v74
d/kyJW16Y7WFdDjwlEkkptIQ+Wi3bWa1PsK4iPq1wLB0Q+xyHeKRGsl2GAduP+4VX2m7Jf/w
t1g//6vToN08ppUfI02CbpcdWgXf492E7xSd6MnOTMbd9IotbMAexeLmq0NzNIqxhwAC5dlD
Zl0bCcHlXUXTaNEgC1YLtKhx2EnMT7BF72LZPA88lSDpQJ7fBJWmF4oL+2DpctyjQnXZG1P0
MvqSzBj8z/PdmbA4ItRY7YmS7eKdxx5lTwJndY5ztvmOSJUpqKRX5pugf0ctf/N08loTaDu1
yzVnyFVjf1yq3+cY5N5TFi3ZIcx54+H+NT/O+mxH4CjRcY9bVDbWJ3vFt9p+2Etj6/n/2Q9q
EXXbmbxb+WVPqDp1wuErMDXMsqccmfbL906il7Gaq3KrY0MkmPp6fEkhQ+qxq0S8nrjCnIja
uYaaMTcbAc67QDPQTsxnEDP1O4jdnRxWmcLtuNFNEDZw6UK99BWiLv8a8XYXh1XvUeOHomBa
A82310ufIYPmbGe8xfujHcVpvZRk4IyszYyXl1eM34Rn5vBQbdTqwXWnDnktR6Hw9kRmY3Vw
IcdVvqDexsSGyHUjrMzCHAi63pxLYFrYT3D7MsmAdtw2mEPBUBHnFOxE91kTKInrRlqqkdpi
9koX5KdJ7WANQn0Q0G0hJYRQDNlNbnV0YeidOyd3fNtdSHF7RxHHPQF5jGxA/COZi/i8t5C3
v+y53Vh7AtKM/K2JMhC2gwApZrhUw+K0tixKOtMtN0EvfWUa/bDHd4SZB4BB5xpNYvMSdUyO
q22yR1aBEeRek10Fbxe5hh5ziyz6wcCe58cYpkx1PIyde5Gkrjc7Tgf8DKxnOsoug/ctuLcz
gMkcSgMmPUyH/SzXGuu4ZgITq3eigTv3BrAZ0Gr+Y3O0newdFzhd9sHmomAlmnYh3QroAVfD
USKr4k2QmvysQ+hpaYDeJig8Fr3aIEPeNDoM6SdckvawYG1bhD/XPUS5jJ7hf0x74G/Tym7C
1DdB/eWwX6PVwEvhJdOxsA37XJjsJ3/PtsQOU8c1M4j4cBfm18eZapxRPRajgoZ9cbLo4+M4
CE+ZF75Aqetugio6uZugBW285Be1zvgTJkoFcfTGi4+lFwiG5YLXz9RoXTXTdqJW1GSgt/Aa
JDukHcMDpq3Nw21rr2AnpzJgi/s2QcnV6Jnra4QP/AxXh7H8z3thOEYO2RN1BPKGZqNttYRo
2/JKkxdbX+jJbH+IHHE3JWpVcg9seT/HizGJkIpfg4cCHirYHJe06cS5oJzgM55IovxSdXu5
Zj/SOzPwMQzXO1lOOSiNFB6ZURvoWpsBCnP5JqVeelCqHxrSEUHJniHd44pKq5M/NucC5pE6
nGtWTkzABGJDFPjijhOzChzELQqtkKaZa0lbF5jNiUPej9OvhfivrBJDJuJx5FrDexhraedB
0SDjs3EP5SD7FU+va+zZVdcwBQz5NsQBcpeh18xmeagGplrUjemcbysCmvBz31uB5kFC6MCH
wEiR9bErUtZpceCCy03M+/AlF5iDT5bklHRvj83u8R5rh91LlpH/PxgS/mfV26faPiHwCYFP
CHxC4BMCnxD4hMAnBD4h8AmBTwh8QuATAp8Q+ITAJwQ+IfAJgU8IfELgEwKfEPiEwCcEPiHw
CYFPCHxC4BMCnxD4hMAnBD4h8AmBTwh8QuB/GwLGd2XfBhcqI4cnPOy+etNSOhObhRu744H3
MthO6ploPpuMb+LoI+qs4Fy7zpi6ZzPj/9te4H/58wizSJjAuQDnuKAdwQvZ++s/3zva2VCd
Ca97GqslzClzSV4pTt7Q8DJLXEj4d7yJHMy10Ogk30HVSmvDfTGzNORt7RGi47ucEuwYabxn
t97MfYCK4D7AAnzIvOH9kX9Hjf+sDIWX/cSSmUK4v5CE8pzig9fZdjbtxOTspMc1FYFjbRR4
CZYU0eMIeIPJKfDyQlTofqsQAHgbaZ88l2Q7O7HB/mCkkeE+vNSb92LWtaPC6KgQ50UK0+en
y65xpuXHPtaq9rSuy3pnQHb20NWQCjbAxcVmTaYcQcP9MYflyqvVbhAjPpzU3HN1ak4huLzX
6Y7hayPbXbWT5QHVTl5xiQ/ZSM3gEYTj+O2yPwaWNjpVv2ANCsNk2kR5jV/faAuXV9pC2OjX
xPPViEUL10bF0UsM3HFXjgg3e/AA+Fj2sssKnPpg7PsaX3SoZmOO9jJjuxZAOmDzPj6P0lq2
axm43872OHGb6sMOG+8NshuoCNXCxRenRmncOND1zzD7t4U7OOkg5sNUa01/GJ8X8fcY3B4l
1RCueiRnEJbHONihppzlHv9UQ6gP/arYXjc0K4WVA/XA1WmR7nYk/JZn2O41BTGWtPqpWoau
l6qn7B9TYvYY1UNHKwlLMwO2mVHbHuTcHjjLgMu0Z5yO4oi4GXuDZvpYTsnKrZU/zZ36hzXI
72Qc8B8f6yVfhbIm+7t6ynqgu67479/QtrhCq9Z1b8+Sb22ZjXtSt1jhvSMLvm/aPXvFK9WV
sLWWJHYvmDeZTa0J39WZzJKSyvxEZcdpQap3H50VowItu+Tm/1yfUKUyim1zl7DG9+EzcuCJ
BeOCPY+L/Z0B6ruhlUVsCsLscZeDXSwLm8WBOuPUh+Q9vucGdcw+z/SWk8tKV71xY5qBpeYa
EjS+cWSUlbBt9Judxnx8vA5tGfnHLwTUuvUO8TNGrSwKFqfu3tV/soy1v5VY4lR8gx7qU4cr
9552jITbLdQdzc7mLAlPow7++Tn/i3//yw7If3v9E3Xekx7oxm7F5bIji9W9X8cFXKQU2yja
BamG5vi2DKPZeKK+PeRq8TYfHtn3MiO2HznRf9L/HY1+smz2pgeeFsrrmK1lYfAGjnorP6zE
nhF1B8NumGJE4Vv9E0Ag3o3pqe+93bu62gneai2K7qRIdogN4BrJjO4I0HgdOqThc0MRTaU4
1bnLmRl9H0pMTiqZvpbz8gZ8adFDb3/O1DtoYSX0IpmcSoBejos5UpadcsflgPVUlHJ0Z8kA
PsTq/vDGDMUReTJHr/JYGRW43DcxlJwaWciyt7bqk/9CvhJySPaNOMaYsOxM9i8uG+2MsDGw
vxKDBSiNDv5cR4nQmA27Y5JVk61SL+OPRGIPLafVlDs+WsunP83mxPY1I7qiHSzj9O2ylPd0
tBlJNGc7/Z1eLrkNr1SXQlOgF+f3Pba8OU6HYdditIezhblVQk2qro37QgLnDyCQakhb+nVj
z05kC6VZ4WjA+vj39tBjyvv7zna9FEtJLU/j3CcDypDb/dAnHKwt27Xks9Jfmr9d9dY79t3E
PU+JSiAOe4twLs/NqWSscBA369YWFzab3++VPha0vdz8Rz2GSmbIMvXCbGUtYduLlyzlInIX
+Yz27FnWHGvAjeqw0g69BWKnf8V1Bxw0rd12myhXImzLTvXyfpMXpREarIX2DymPvlpfhJIH
/GaDKscuiSrZClr+xubQWXm7hiExWgt32ysgmkc1tb35bu2skTlAKRCQzbWmA3Sfm6ATAGHz
jl3JnJkE1Knf3tD+lZT7RDNB8/cCdYakm6Am9213flN125DGc+vnjDTrH0MfPtsv/4/q3eLJ
mOJdG5Ls6+MKghq6dqpOkIJZeIiRA8WN/mKB4P1O3+qOronRUczhFgOHs3rTObgs3P3tbybn
DCTNIZ0a0rFvQnw9+0KCuroW3rz2VdmatXFI96XAsC5jmqPfRas8qYAFQS4GLQe2VfGOxXbT
GfufpBU752+srUtIWfxi/rECr2JB40mTOBaly/PLtdXw+sNzVl8ZjurZKAf6P27Z/xhnkU3I
3D3h5FQpXHfjzHLsnipxO+dOHjg6G3DDnixwLxPhRonYMSQmY3eQkS1Zl9nCrB5D7Fuz8y/w
ySFZ917ZeBiZ8PHFS8eqEDcqn680+a2cse1i5xF54EemabWanV8bV+iPYGs28BQ3R4iT2ukr
Eq1NUN4ujHSsF7gEc2Rb/q/ZPxbxt79tCBFCJIwOlA4DzhEc27cl/m2Cf0n+V/gk/6WKQFsu
WzgLae/5LwyJvhORJN9Lva9CSzpGswerWyLh0y548kutAPQ39vCaleVIzm53wwXOWMq44s87
uhfAiyYN0ocs1ML7L3HAuPCitoJbgilZjHErXel0zjX1kU9UadLbX0+/eSNmaqsWWmSqXsW4
zx3QtdxY0Ur5oeL0H4nXpz3T6+hu+MtDLrbQR2+Ou+c6q6Q64fDXQtwQdKWCrBzOgFqXvXWz
3S0cLq5BU+Nuj7yvSwPWSAdS/fTpUNEMrrHnxLVqa7G94miZj/oIR1X2zLT3QZ6yce6b8Lo0
30Tz73oJAO9OLuZQxAHPDGIEwJZOpymQnLSkbsNoPPtuDNymusYwkpxXzfdIzf7FX3ST9ZEE
/Djdn5f6s3ChLKVA4/CBpESJG9N856RaRvOYKot+PcDUYr4sOZ/rLyWuOXmxLaaaCO4WCziM
f1xzc7P1tuSY8Kky+izsR1Ow4kZeyNnSy7Q7uUkGAsdxn55hHe8Bnh+ealH4FuuHM398yuw4
CJE2UlulmlZdHT9Xa7Aj2hSadDfuUve7cqp/C06jliWqP4/RzEc0dDMNEd1BCv7R1cVB0qZY
GfSRF241fJcGTjzS+8qr/HFhVYzGjMeFMieRf9GCV1bCQoofrrYgxy8b51tlafXkxh6HTNnP
bq0hj2xbGKT6YEHY85u9yiecXg6XzT6PZAhxRQr5dAfIZfbVOarunj2MrzDfzae97TTOOEds
ldIzH410hu2xa20l6LEFijbv2Dzzg8HLB9fPdlbfDdO8+zSMkJFps2f8+wDRleGCGY82RKoB
XV/s+fz8sbk0Sf1qUKb7gKRtNeDW9K2hTL/crMy6I6TUbH9NwoOK2OQcbasnZs12d+2iUwqy
1+TK7gSPapi00o0zCjxn2pL3V8fELo808a4yqIAuCtOxBQi/V/E4pD/JYmElPpugpxYQP308
/F9r+r811xZM2VXZfZ8PUgxTYvD+1t7flM93Kh1l6R0at+CwsH3Ls+B/kOdzFO/anMrl8W5q
y3iQgoH/Cj9ypRkne5HrVT8QztbyucW2bHuSm4lLWUgp7LTZ66QLUHA+Oxqsmtao5lFD7rKd
y8O/tcnNLL0xvOLf2Z7eX/Ftcb4UT0GW9bkmsy0KfN/iq1p09aY/T1jhFBi+QCn0eyoKptDJ
j65YMhrf6xMpNnq8kzqOVqiVU7PDGEu4ontrTjjcCF7nht7mdayjobW98O2GZD/CbUOUr/z2
i8ounQva30frvLgJL8VkJDW7y20fdQo99uEl3RfaUovg0ZOv0A2sghYcAVLMrmbLqM+OAFfn
e1WxW4YZVWGK9SZek2XZzaXZj9wj2U5KBu6G+Ec2eRe3+5jfTM2Y5cb44asEBi0GVrlV91KN
YyiGzL2RhnebbTC5rFKVkOvOfd+WdUXiWxhYzUYc7KK7HmB2c1sA90ZyH9lCpw58N3m1fUKp
q6/mTrNNU2rBfKxjCSnjUYYTnCtyOVJEc+8oemezt5l+pcvSMtHcvJ+7o5Rr1sqOSskpJWUJ
YhTPqaXddWvuVsrz9zk+nD9mt6PTMWJjzSbqWNaa9Sljp+2UuTMAzVcU4O+Ol7Kl6Nk/+JS/
Bm3BQDHQeg8VVOTrTRA9dMuzhn+W8neF/2t8m7+ril8Tb1GJKZ6j/Xjgl4Acj0GmSGmBbmDj
vTVip6sL9JvUn6OLiY6UzDL2InKn4IpdzuHd4LgIcsVeJ+8k88+IjmHMho5+XtZ9dAA513CO
Irj2mdVUkX23Xw33TuazALMP/SMjwgp9jw+RM8lN1aHJ3B73oZzyAeu2n/xy83eK9X/QBf3d
eMLqvhXdk9o5tyUKraQTjXtdFQgt7i11F+YO8X1OeNvrzmXlVvdMREqPO0Ib9CLwrOEnFLzP
Ym1/IIN6xr6dmJn5KLZ8O2mgzNHAyd1hqYuupwdlJJKIWjMYsxyk6YLr1hmn1Y0NxT04+HGS
x4WX4664Q7ijGC/SY8eztQgplgh0npO7trMDSwmRtozeN+kfeirC81TOtxXu2bFDiWEPaGfv
av1eCJqmN+YL3Ox8tvWLiIvT/ItT4B3caGalfsoRptmxr14+JVbAzS2cLhJUl0fKCVQn/3z+
EczxDWyteb2ixQ8/NX7vrhq9CXr0WtBWsqJ5jcou4JAUZxbWnZw6hukhHx3LL1k9qLBpxwB0
G8WfdyV88Xk/7IGJimamVPnusIfbUOekAn58xtLOD2/XtAIfLXo3y4mtuyaqmLB6vd35c8x6
yozcKUZ/qAlmUiMjwHRsW2C0md0eDeZdf51h9lQlNnvNUZ8O1WbIntRqO468xSYnvDkFkr/K
/aZzuWPW8+5+ws6o/G8o84DffWvaitlob2UJFnH1LJHb5pdPt1ooySnBHE40JjX5B8TtiQxw
1QydFOVefW+wM03PlIZcDTpE7SgFeuzQfVz2mvjgrHlNyEWdH+oiByV2Le25+rdMuy2WAJ6S
iQm6U+q7QvGiAaNoYtsTwBRMKcnKwhy3lhP9/jb8e3Lo8TqYPTuHPSvFm6B7tbu2JvyWzDsl
IbT5B3C7eK34P57SV/gHWWCPAVptqqPjboBJwQeRAaJi9CWeHVOUb12nkvmhPhvaeNxooQ0H
euHbE8iIVGurCiF1bxR7Ljt743Sr8dmmE42tcM3AMqVAfz+hJrFa5ZpSAC47B+AfkJBZk+b1
n9cewrHYIpcb+/XGneQi5XUOGPUa+zaRtR647dwRYrQGuMJEIq2bo7tSeVZUBs6bcZ9to7u3
d/eWwYOg7WEsTseT1Cb3gRfcL1+tk6JNz612le/waK3cbYN3ednr2KHjYB1TF7HXPafAPF+1
BE+7duyZsm5PUkqMa9Ed18K7Q0K9yNm2fj9KsjVtPjqmj+6ub9W32v/aXyZRUgIdE8dHZI9v
G+rTC48nN+VxS2+OjxHR7k6lk5PXcLVaOb6N+NYBT/jqXM7B3fz78QGCSvwQJbUJuptNJSgf
8ivUdOgilYwVQHOysMd7FOO/wxbzT38h6OzS2Ue8089eZLgzh5+Mk70pJS9HcwK9piyFkqsW
NVh6vayr19p6I517cPFVaL4iqvseTcbx2wQt7pWzO/UPvs+vQXLQeGg8os5Qxr65CcJNy51O
+Gcpf1f4/9Q6xdZfTN8t2azWCugVrzfeUAcicpUiq0aIUXa95TfszyLxZOhO6t4uyw1gAGb/
QIGNB6QCk5iiaFnPTdS0nGxbDUXqH4VmKznJTiHyGiv4Zb3VPjLWkGgsLehQSQE19h4mSi33
sWVUFjYAa9ZlVQW+/3fa+WX6G8SlcvlbwfzErKhZTcfudsa+dQcLillbYfNg8sYkrnwsf2y0
GHNLUWMHdp759nhgYWc/vgXx0h/5XRDVZcawPBrqeel7umPO0WQpiu5gUbcJOsbeikwAmes4
V2f4k5TZ9qH0Dp+U+bKsHH+sd1Vzs3Dy+r43s5U/bgggXVdlE0gDIuFuYYCyrx0WsT7hcZ+S
tofd5UyCa8S/Cl7+mpN38Z75uZEDZz9olF8NzPPc41htYxC5MksdDljRZDnupeqpdVk36E8V
AsTYMnRi2YLT5IbSi7QAnf3TyHx6hxdOS+DldVq8xZrsb2TDtsoKfF5VQjLwniddGLNLXHKI
Uwemh0mrPT7txwb3m04Tbk3dRjrU2D/zdk513yhTiB9WH6Q8hp+ES6AnedeXAV8t+6Qsv2de
gcuRgkfoRJ/Uq2E6fkLZLlivjp+Ar20NOORyDFv5QUfOru5bantfTUBV9QEiLmjmVrTyMtUj
puxlrEac1IN7cLrhdzXH35tYDuZWKv0D9YUYRhEEPPuNK+m0tgOy+63T/A9FH/bKnRr/+zrl
SoU/jxq9sdIxtx6tGfDpP/e4qvr209hCmnJJCxFwtoIaT9RPyFM9sJFuOD7bdsyzo1IRpafi
BIOpEaXfiDOPT1kF4Q3XtKXv3QdBoC/y6MdONfcLDzOzlZd63NkaG5mYNEfP9Sj1SxXwEjR+
cpmB5tw5/ex1/f1sopLgcTPbNBvf7Pl+JWhArS3p3Fl7OxR+eAYVrrQC0rtYV2PR0kmiuJEC
7ubW1x7re+2PxYWbZ6cUwOnDXgjwcbmpTVDDgDLgUcN2VVrQsQlql5fsCkGJ+jiQ4ePlkoRJ
UXpu8bxwoIrqKacpr7efSIiDaNCvlg0DNqqjgSVgX2tsaTd23ASZqsDEZMAtxstLuyz+HqC/
hOwUrgt5aysj4upMGf7hrm3/NOHvifhv9Of9N4+xtaoWcO5CpeyEkbKZCc8Uv/o7nVGoXa7S
sTwzt8PsdC6ZzbaQs/mwgNV8Z80oeEnMH2OIcNAvEv700E/nZzbaN+lAVTDN16XgSLn87fGB
jN2qhXSjwLOL3JVRopvkIDsBBNpb3u/rPfTe5PF7wpMTu21U8LcHyyQba/SMtMgZXJFE+T46
4Q9/2H902iyawXTDBBd5kMNa3aoJbL8IOrOObuxIT9bTY8tCZkTPOM/OADTut1cWc+BHBlos
6M02nb/40IumFnpS78BbrpYUDNwdjhuwpsXkzFF+VrUSJiMUZXVmIxIFzdXrr2xy34QYerx/
vxH5+WJmRbiqkYp1ZehckAIp8oQDPAfHnuboAqOTPNB0t+R5xBlnYFe9c+HfBFmoaDxIg5Jd
9Jdc+xz3nB25Fhk42dLhY75OnzQ/gvHRWlbIG1bxdhwbqTw7lKOaUu5vuvEcjfVyxZpRo8rd
sKO7R3iOpwy2FC5ED2tkJBZM8HlQTFqA0gAKduesro2F7IsEZMPffKB/r/jfMyfe0hTd1mQB
e1CnzWAcp1ebl5rtCFvg6y8Kr1VYj1afRcZgtZLTpeSazxQlzfXbN0EeqmyZ/B7BqyjCUVWY
ANWhweknpH8YE8mIj0v9KrBuhBLXShsltmAYHn1FUOsVxy9Q7/jSGlis2hMRMXkut1L4HXUo
M/RW2hkEa9Al0iALZ25S7cUzcYJbxh+PTjmavbHcq9Z+pE+J2AP28nH+UPO8uStXsVXbXQo7
00QcmfEvoxvpeKLxusohsm9djAGE9fC0pHJwKuy1NZp83pRy15P7vHITRBpGiVpAve//6Seg
Yewwnjq7KCRnFIsIen/9nyb8PRF6NEp1qU4g7w+MuCQ3KiEJu4C41UXtaicyGyq9xoiOUcfw
hIq9vXrQcW2ffKTQqJzapUYXwBloyimLKu7Uu1Ek/PvIpKZMXf6C/Jv82BgYntoF7RREfIGm
gDZ6afJHImKIyYNMBbyl3JCdmXkhfXZW53uEKTVLcn3DoTvzqGMMMW2C31Q2iO6QfxqW3RHo
AfeuiVpZPnBL8iqmzZhRBGSAJUEUppvRnUCCxI4HQmLGRHkTcWVKcCqmzagOZ5ebrb0PyXpF
eSD/c1hYx8tNEEezCTzqA159tpYeSHTCSKcF7uKyBpk+hDlXOeOF4v88EbRMsftVfj3jK/7G
2Fn8qpeSLs8XLpk4y955KMqWwjlTCbI4hauU1053UaQTZoLxuCOzhU92UJ5zIW9ZmyCHOn2h
7Gs1kUn2TP3cPKIxeLi8b7nuS9leIChlZgMIiphge8zOvcVMnOYUop9uJ4og+yNVPWanmjAT
W5YL0yRKRO4BjyHHuNzEr1A/ytem666kULImsTQ8Y0DXd61xuShFcqJ81vhxtT/f4Kmf5FWc
36TvrkVh+kE2jkx1aZZds6ha3XF9gKsyFURf9o/0XQP8VCKWAD+I0bceLfsrobhyQ7Yrw46I
7oUPmozu6k1QllpH1Llh/GyUUjZ01p3CT+w2Urjj1LWYgxBn66Pq1EJKb/Fiqm+b8HV6ZCsx
rSVYu1z7FoyYhRoDH6E1YgwDAU9VdWgg28lVX+ojfxQlAeUlTeZ6FKDqE2LOdobNEu1awZy7
1rIc6LdmbW/Af9l9/D2N8T+nLdUmoLhBTeDl2ajxI59b/sCt/c8bZXoEWn+1B6XbSpFb5rYy
2z9OvMtkeY8UNFs1KhVAQeEeGVhmf8TtExCV9dtLqdH9YqlBxFld/o39DxvetvUGh1QtXTBX
+fpNcQUc45/idUh9MgGwLEGKNwfAp7AvPXbDU8ObbZQNnu6oZLfYJ7tDlBPDpj6/8sO66FyA
k4GtTfjL/cvR9oWLw1jF3esVjoOUkSkKsJt3C3gHOe5NViz8cyIpr9jbu8cuH0/wK1CfyJZ3
58B9hFET/QaMvIVWaibWBudTUuFR6VWXUgB9QlW06ZhjOVi3H+t8OlbqAp0cMcXsjPm+6BLW
wMxx0meZgXf0djybU1h9ZcIFX93hj9PwbmWkaBV1jvcyq8Pvum5tr70QisIvp7G9s6m8Xwa8
4ewF4rkhAjIZG8ZTGPtsunfPXLWPRnFKXW+kdxWfcEn7s/8M979b+u9R/sBTbplyD3dFb69d
wFoQ8xsELv2boMFc/9EoghLvfTg+cooc4cO6evusLrtr4ErkZ5FTRpfHHIxP38lgwQ95B7kD
fv5vL+R64MLqbno0257VY8WqU+BS4FOqih2g1x2CDOr6OLLbNWizqRj7IDlg/fJarXYaOjSg
osjbmp/j5aPeRLzSbBOlccg/C6BbtdH/oBrVhDzAUTsRFK+elCt/loxbrB07azxYs1E4hLGI
oOWkHE3nOboJj2I1fN+BeuyOH/i8xyRgPJ8xYYiOfJA6HJhMLvGx36P2kkZcG+DEIOp30i1K
ktda9vaoNZhdAV53H32uaSCpBTOkYTX2i6rn23Lh+6FN0CgbJvVK8Pu7TobSwHnTrli9BX/Z
XmFH9SCosS+B3V3ufQ4xykPbkSIBtbs+UHbrzSbIsv9bP37oEXQr+Cx1oLoUmUoMx8Ecs+Gw
r2EGVGnFbVkqOXw/zLHEGVDM06QW26+vSVXuiz2YQdh+3SlOP7gtLq3u6zYpJJWkxWTxJOfF
/C2CoDDFzmUjSWF6nUX1yAIfqghDzsN2jfmbfF8B3SXzFrjD43H8exgIcsUCRfPsGNi4sFLO
v1mEOiDPHVirlv5Ud0w65Mds25ohiqPbIFZX+mu1Ukrwzh3AIvGqLst1/P3H3vVf/+nlttkU
PabEjE0qtL7tqE7NqKnB4/0Mg0aTc044ZeBHq20iLGPiLAf2WJCfXegAfFbnQ70fxGnFj+wL
EYLWB3qM0kNEEGXDw+KqWauVy+Cz8XtNEtDvBSVNLPJIdoXks8QegK/Fu3AdqhE8Vk6/6dsm
Pv4xyMNXfR36x5X6crr//h9RFe0WnlnlVB1e/FvKiLuV8AtIVgXViBf3FwmGyaoExKi3tF8j
YY96AnJQrLm7lDe1SWsHUZoFTIPdm6ARpLLdkNsmaPrUan5qXV/bJui24HvYTcCayABcAQLs
5GqBzKaj4hN5kgdqe3rQOYNceNl+uyEEbTphNf8BY6AtNzR4LJ7qqSM8YhHWg889wg2oM8WE
XXsnswZvrzUKC1ALdE3qXQ4wgbxrXMQXZhrtnu0edIzLoXImtwAyxShkllSB4xvgMc2JdCer
saAFriswpuWMeqa/t3AMT5xTwBhu+zikqa++Bzu6H4ppK6IWBl4gUyPRbeeBBOi5kxjD4REg
Bw/TCraJ/4bYU0StrNpOpjamCViAz8ZHjEUHrpncuXIGwxiVPm5hsI6dg2OyJ/JzPYk1r2Cq
72OPLbjTdsH03lpfAEZloj6t7SGY5nkRGTMvzN8+Us4zy/xOEnMJDO4izeFFrZugyUCI8BoM
kx1Ds+OlffQgCPvoQZCfj1lUgdW6A3Hmvi82QRYAtq86KOE5VmvPUJpYsPkqIHdiak9oCi+Z
+2I1zSsAmUSp3fVn2co8Y278qlVjuZ9nx+kJC72YCTRsa2g9QFqH2XgYDXgfjJqiNTxgJjr3
+kqfqe3p9cwbRkjk+6C7nOwwGwmxrAVSNx2K3MrCbHtxB9aUKFY1I44Dvgl3DhyV2j5PEpTL
dZt8NldG6wr2DHcQ5Z2BrHrI/xxqRHuByZpQ4BbxTDYoiuMxKJNM2Buk7904GabP12qyFszh
/hLxeSXXXG/SEVbSVb7qLiccqL3nLMxXC3Exi9d2FIoHQLIoj4JIpO/3qykwB5Q2knd9Nf9z
nnLl7JBbYDrzogdCyrojyf8D7wAQIgEYzlpLYLGnJ8wNWTBfarXJj+i+4X5NjtzbSN/LKtDA
yq4fkUXKbhgySNY6xLKx62Iv3yxkNA9QGGDj97FPHLimOnq6y94Bm6Bl+Z/9LKyPcv2eUtuk
3eOboGBz8pm+DxhDiB4AbFTNFumqhQ2wPFcwGwsjM0DR7jYlGzH56FGQGo4VYIdRz56XAXnk
WiO0sVeEXOFTtHi0UbYS3V3dV4+Blnb1xRF4AGlRYmuU8mUcMsB91suCUYqSjq/k0fvS0TkM
RIcVKbscVQcZZOadPy7kW+mGiOrS4EhJYrfxi75IGiZyVQZz9CiFIbfMHLjFMvCl1dUsQHBp
F5DSg2vAks5yQT9CPJW2W0Ry7uXPA2bjjOl9Z2HpJqhlkL0+KNTjz8sJWbV3nYVl6qvnYI7J
kUjpKxhGrlgRkzOJ2l0ivbpXZgZ02AihqJLrdo15ZUN0eztK9Vk0zYIhcBbW68JZKMeiIUnk
6SmL0yazlVxEICNchrdrAUImLM4RR6otcFOtFXasKolO23W1K7zDQJcwUovQSbJuwIxvmVO9
QBwrorYB/jGTzvcWSZ+qhfQ15W9HMKK6BOHuJ1FDjXOqNjFTaCPV10jVHReBnn6EFUY7HFOz
iNpIvPCrGEPTR7E/cJbjvpNdAGJRNHMUu5vCmM2Q/AxhUk/PFcA25pyWg84DsZzZ59xeKaKI
b1AI0EjIce1NWLJ6T4Gvlew8eCni7BxWs261VZNlO9SzCfpJbtTqSnfMEWHZyWvlPNeAC5Jr
78E9Vo4eUSXCMq3xgWU21Wz1GuCSHV+31Mt1s/qA50cugyerwBGqziZ9RbT68AvkUUqyoBgw
l0ufzvXOjeZGlkedapNcAkdYuAk7img1hi0ey4kBq+ctqngxc0oYKL4Kxw/XQime4jvQN0FP
9yOEroblUWc2QRENcUcXd1DZUNTsofIoS6B3ANOXCrdRK4yKl+PyPAGFln+dXyEZacPYDu5Z
nh/YBP0s153/GjFshTk3MS2uhdqtPYxTf0kx1J0bkZhgoqw6ZFfAxosG1PCYDdquotEPerDH
gPtTWpizWnxRkwk//ClzJoGbXnWAboXxDW5FNs+hjsv/HFEwi4WJFd8KxYoYSRVkcPE7qhUP
/HZIrFiMOiHP5/oRi2TPo53FjsUo7Y+iECt7JnACxE3Qn+UXsmc1f5U38qsP9DRL3jRM3Gjr
+8D7ehMEB7CsRnRazT81nnjsWdLYpy4tA6YjpVG6u0WaO40jnIjeprDhG2oi08FVFsxy4lwj
JlTPW+AH4PsGAUf3GJ+umGMQMyFvz1v0RbyZ2otgbou8Lc52thcCePZPpaxyEV8Nhy37TjdY
9PFqJ28gmHKGzeIcrCXy4wcgTwIZtrxZEue0CCQJANzx9d6zNVue2xHLPNDjd9RN1Fn2ngYS
6+4JOOUty7A/nnxyuSQpM7mY/tiHbYgvyGEzsPhw6p7hmix8XfPHdeqRGttv/zz8X810pQgJ
E0n8MLOVvVsLTseM/lHqawx5rWonNd1icAq0r2KWcuhl2S1BIxKHLd+BDFjdI33pO3ZfnAGa
lPyxlRekFHkVApfBQvzekJB4DQbyWz9g9QWkSOifUm6aMNrFjUPerXkdGCX10KdNb322JUJV
+WQAuaN7psLdXWpXzy3BWuB85baWU05+uQGsFJhGgPMZmSEOBMCJrusmyPn1Tm4CSJNjp33Z
xG5Ko6ho8enlKY9HNVE77R4QmsRhYVuJZebksoGohnKtQ+aVZ++veBOe1BbWbZ0LHzWy7ala
ClQ/39DW2Pi28hzU0NAAFzhc6X//PjblCPbQUewh4GdmeQp2/j8aQqZFOWoWC5LKlYvBIamX
3ussov442YLfH59bEdDGJMemXl3ATTcLas21Jv3xVRv383v0hg8fw8aOB9l9WBMXtJHK3WWH
1fYAljRCfAD0nhKkg9oL3rcYRyGnb2EL+BF4Zkvi29ixEPDguOEoOuoaZRP0EEjOSYa9GL86
jI5ybAcIGcBfLkY0cz6sGAW0kUqm7Sblf+QRJ4sWotWr1Uf7Tt4A0jNTPV+MY3vQUUYaqK/N
NUsJX6MuNqblqS1fvSK7ZK61GNCK+rASdtOKhNJGHVerrR1aJa3XHRxcXWZ0ArPmCSdXbVNZ
5o8kBYuhLszEnUV8aRIEdfFtPqSNZHt7E6QAdncPEP4o1dkRHaPGfrqwCboFsBZU17UiM++5
GaOjVExRw6eBTJ4nw7jmRhO/xNU4c2X9QCZ/4lPApJjbqT7ay/sSMKHky2L7wqxE7nfetvPD
yedQI3ckkuF0PxTATCH7yEyRIBlGApL2f5Aof5U+JkX6UYqh/zcSDki2SgClBaTzY6QHMK4V
eygBBUE6T/9VRv5ZPiUZtvWHFacrI+nAWYIT8lzuLWKJrKDGU+z4UT28WzxDdeKpNIGHnwLn
CFfzAWUCEGBIdNEVJszOLRLJ0HIArARYC+mb3QQdl1+L7ea6Si8Ef4A2A/Ix+Qe83NlalFin
6Zp4d7bkJVCaHhWxCdoIure6oa7z0a4BtJkeQB60fKBt8EH5DDBCva4bsgNqCGZBm6Y3QUeB
Ih7NfkCJcpMyNiCawvNAjiTDytkPNfGQ78s3QUeA+PTZMcQwsgH9aoDy0Rl1CzcMJgV/3zbo
SmlLbI1t5kZBA1SUoG8ZMmOgOajkDnEdKqYYPccAUa9/R66Q6zZkv3zrMWo/+EtgkaV7p/B1
5O24HAhgpwGNCTGngBgS/8mCqgDjAq2xjpsGDXTyayM+d/i4uLGHPvA0mRuQ62JB3c4UN05Y
uMV0YgwnR3SXbxlSxoDyRrtvCwm2DHTYqVdgN57/3J8QI01BbcRn3qgaIHNungk3KF7BgkoB
tsF+BtreK24pNFBaaEUkvNoErcm9LQMGJVru/eErcblR8oJnsSxWRfe0sCavyGE5cBQmeAgE
lHRLhDWld+2IBH3mR/sYhzJ3mJ3cMIDOjnwA9u8TB5yulMUUUVvjrohzA74DRlo3HjBAIhjB
9/mGABXLzxAa1RKwUoWoiTyI8CAMk5NMc+IBBkeTKWztFMwADBipALnTvXDUdALSH2IBG+hA
hbkAUSiYwY6PcTBiKUR4BJKTSLPicfF8o19Q3wBN6JLJvKw+Qjanj55+JkP68c03QQN/Hcxp
VIu5XJHITdq9AHsHtMbe+hig4cEzUWHDdmuXUDD9ufzvgFlGKWd41zHht7BHfcxf5TIrtkKm
JAvyjuVH27sJYo9obqR+NCT2sW7Sdn6UdTYeWQPyNE9n7gfUBidbbIPdBGkC7eP4HBK1sZon
titCfRSPzkUCYjGyb4H5rnHK4rsYBkZax/KsjkWtglbzf3Fj28nGqu2GGeDJLZL0QgR7gGse
Q59j9K5Q7gODJ3juHiV76gkJOotJlpw3LyxWNudDfdNyf4qnwlQED1HeGI84OIK2j3BFnBOP
njw9I5GaC924IYnRNGLRsOwwsB7ImJucy02NG4vv2g5LBiw5rlBaTm1xl0Jnd6L2ynMneFuI
s5NJuzUZjZiWW0B6AmtXGLW5/hsaMclzskqeS4/YDiSA7fVlNJMEpXck3NEz8Jiauy3JfN1Q
mOIrWL5VcRrNUDa5Ls4SeqYkoGD5ysUvaIaiqcPiJ2EwRRCqiWYfKxlhpoUtu9IkVxKFm6Bd
eefgMQTMAV9Gkf3HEPPrLBPP3OiQyXjaT6iULVPmV1hmYVRStBQ6E1sVPy+/Fo3uQ1Jk9LAd
Kx796hy51ijmZWDVW2zf5dmYUdo29jC6m8M64wkwVBB/EpzkMVsOyloXWN9BA1u6gLVS4SwZ
WO07N82yhwaismM2QdyPlvJaWmNfGWKYqQfogzlToLBGaVpQSbiwGukD7FB1G3y0rsVrniUP
hNVQnzmZOBgwppk/uVsXUTFdgKYYWwYD8axl7CPAy7swDyOmNoA5uNgc2ibo/GwsigKY9GPY
XsAlfNe6xCwBvAkiAsembqzL5kGr8TZFMnT2gsAIpIZlBcCkkOwFGTcYsKe1PxbWYwIURm5Q
sHjnFhDSjdpRqNPa+kKFAqEjX67UBd2d0myLRip3RsfXwWCZb7mJluP/cYz8Z//LmTAY5yjm
MyHn8o7R9fC2oj6LMyzIjjYB09FxEuGZuDamN2sG7ETv6FJwZiGxVaj3YRaQsWWQGc+wcAiY
oYSDZLaeDhfMhebdvVLZeAJK05HlbYW5PBuKEbMbIcDMuzzieOFsdZkPsOASIZBc59FrTX/q
4bqmZrvEM8hx0nFZL8X04TXucrrXFMAGFRDGn1ZrnyTYj6jFj7YBUwqefyV/XM2+Ta1QyVw8
kLYqqjX4EuBR6BROmSZ7S/olU7ss6vNb3aQikCwW+Tx6E2TQ7HG0d2RhVceO+QY8zb3btwMy
K3jeDLi1vwtLfw971M2BCjZBRi1kjh1r5cjHaYW5JGwILdLcx7eB4XuBya7qR312tFsGm38a
0T8v9cAkCZYSxXaXbSMXuCFzlwXhXV/KQGodsY+5ZLtc9D6mQkaRndjYBLZLhA5jvwyiyn/3
XnD3MYn7unJpuPK547Pxgf0PqPZjzQL8XsZ9nFkz3eZKl1VMcvpoI0K/i6pr4DDsY17BpFz/
v4fj91rRC1Cyqihlvjowsb/6yx/GQWEKe9iqufVGrRiCEWfPt4ZqqY+cbqcF6G2TuSshKnbv
hlP19PSYtCs9lpHZOc+Uqe/Qx5/WBOt4DQ3UqBSPw0ki+v1CnajexwHa/6e9bw+EOnv/n7Jl
l2JtSVuRrRZdJMYt19pIu2ESE5VLUe4GM+4jU9lWUmxbCkNaaoaZkBhiSJJchxXCGITGfVxz
H/qeM5Otbev72d9+v/v77h+G98z7fc7zPOc5r+c5zznvc96XiUC9yRi5HAxYY+9ImhMKb7WI
EH5C0Ty//yzwkRV9Y+39RR3VA9c2Dx0WSWs35/aAwcXgRPx8+h7l1+850dK8gCQ3Kc9JEWoG
dkpgfQXS0eJpvvuhIqb5g63l5EPEuI4ufbq4fsWNrrZzq1FOpFBSd1DrBt/PhVHLc6/Yc19U
daZYgTddcH8hz20VjMU21O3TfG10rpgJLjUyKi2PeE0F77XQ6hMgzigIT4XiCl6zmiJepwY/
Sd23e7Bqbn3w8dRuQm/uhYjyPFFLr45u3KY0IT9RqmF1hvXd4FWT7sEtBmDeoX/61mf2JfR7
TumTo0s4ZJKBVqT/Q3FCe0Nm0uy09ISBoZR/35iHUkGIZ6/YfJ2oeq9/tSF4n4QqwSsXTIz4
mzzvvnWJwjH/zClBOzdb9Wrz4GmByaO9plXjbcR2+2Xx9YPaGoSafOm5FwGGY3dxXRNHLriM
44PXBI0fBq9TuGO+W0LHXY+ZVWCe2sw1Ae9OmNEZI9gwjjX5gKvgU6o7aNJzqjO7cZ42DIcB
MNd4r5V7ZMvGhPArWo31Y8fAgC5p0vtyWvElcHa3NucetTp3ygFFp4LXh+3xGjLuR1t0u/+0
ZntUTEpfkzLKXc3vaQHit4vv2efv7yJ7H86HGicPsQm1oyuXnf1bguZ9IpyXcIfl4rUVRwSm
VVNQt+o3uoBIoao1PXA8fuiEFDIkRCfwIAiwvojhOE1UvI6I1mxWMpwLcTjwnDLWG3VtsIk8
93g4TliP2pUZ+PWkZw/MlMW49T1y2VtLbilOnHs8Xk9TpdmoZL1OnvTgvEE8lMrNsq+mdmXd
uqIzuCyNe3u8/v6ECkElQ3nrpFe/7vTePmqIlnZa14RUC7Xl+QDqFZi1E37oYMMYHnJFD/au
HQPzm/VPdFabjwUqMr3xuTuV5/doo4dtgrN13H+cBWfO3xXHl4IXfy3z2N/dE7uhcRxPx39F
CAYTdTZ+wrjXxp8PrMtvoV3QLQTznfJcOmtu1dk8DWoLsxHJ/VJbfLSwwqi6ZrcfOBelMI+B
sednovqWydgcy0nqjao1hnNWcWTCV6LdY2QwF3zFcjvvLRnnuL0s0E3Z2YAuzZMJ3uwyT9Bw
374KLJfaCOt6zhBAAmprILV6nhMoP1cKxtbFAs/8D7CPESZd2wmDBwWmwLSKXCylOv5G69p5
9i7CJcHLo+fKY6enMe3xhbT7BWGCP476g0XFaff27MIsj86pXX4oGRYZ3c0uCtFdziqOKBW8
YBk1etM8/uZOqcB1y5XBqa03Fl2ubx1kOSFY+GtjRBk4yTgwrU+trkh9OqUcZjIFTkyuPjpE
GRsdeqCzUuni7ONxdGm8bL3/tH9TwXJR93xpcGwuC15Og2faLNc2maQIklL37FZJq64YbJyS
o28MuB9A7eWUXQgKspkYKrTWO9N/9rV5bdovuVzu0hqdFfcezjbs7U0jC26p5zYs8UqaVFnR
M9tQ2JNGit+iAlKG7VgvVNbONiEGdFaMJld0K0RPM7MFp06SOHP7TGh9gZeZmNayMkp1gDPR
xGfOu8Eoh3JJxpFkGw3uAwiNChV05bv7f75Ug2Gu7EMqQVpaZujg8UM2pKCV370W6PT4bk49
z6nxa7QPx8HLyVy2gPa1z6t1GCB0mac3rfSSn2IRy8a+q5uO43juNGAvvbXXS1LcrX5DBqY/
Q3f7kdlyknZj7TB+bmrZOdDw+m/ZqoPZGtHANS2W0vOOQXsJyo3XO7hXx2Up+SgmR3zKentR
YtF0eEue+tj5PGqPi6Up0gA5ooIHr6fMRBX1DXtKNtTIhlmo06yaLB2ZMcUz+MpjdfexylMU
nbtmoKtUoIttNPtyLJxF8py8ueJi+HaPNwgkqjbVakR95pFW7TVyG7XxkntzNCmGtMleLq0w
LRNVPr2kLmpaYsS9ubw4H8voVymu8JWvV67XN9HuSIoaBReh2e51kNTRiBnc4Ib/4SVBaf35
FAPj6tRYIwlvB6vo0uJ8s6fH06OxBL1ss+lN46btJkipDQxk+6E1Ve9HGtEreT6Y+g6RpjpV
+8nmKY3WEApzZHfU11m2bGLdZGj46+oMcT30KimLqNDQ0Is/G0T1Eks5OpjPOrgaXWRdjvSE
aS3ql3WBLMHCKe8r+wnMJQNkUsOW69MPV5K4GiTQ+kRET2ur+8uSGY+NZNvrkOQpD//a2vhf
KIEsgZpHGyrLwPp2eYAv9jiKeFZDouhqpO6T4CqNAKwNOF5PaM+5qvtEoElSJ0eJzKiYaJ6y
575BfA46kDeIshQdjI1PSZFRE1zCl84j1naxx5y5qhgUO7hqt9Crvng1BfzB9mcUgpyUZylB
9moXu9uBq47TvSxlUkqWrelid9pz1RXBoWdptZxYF7vtdKCGt5Ko+ivf6+pjWE76vOTOUDAB
rl++gzDYn05wloeBz7NMTQ4MXOikJ3OkjPmX/gbfWt4xIN7UPjf7vR04N9VK/KX1MJii9N25
Mei3zjcINhBgV36KMNhZVM2aV5s/5G8gE0sqmR/U0pirAhecvQL5nuWBhMH2oghWq8L8HoLd
tUdmm98gfObXz3el644KlO/WZu/XnXRvTxu0E526T7C7LmIGCvAZXBfEHgZx5Tr2QvkdArgv
RYGVKjFyYr4EhKGSeU6e4lz5iTeI1WB6PhFL3Tib5VE0KXuOe0i3oOpqefaEqkfB5Lf8w8jy
AnBIn9wMhtyQ/O4oeHnQ71Fultsbe49g9zYK7oFRUbex4Uk1KyiOewAIiyuvnlABy2uSIKYK
gpCawQupJU5tT0FI5aYQ7MxhRM0FEZWgEbLdprH+SQELA1i1ktkHI8uDHG60rjHIycgc6tg7
QI58dNRx+paV+kmprhowbL8EpkaP7nYjd/njwSwKEQWCLH4rO+PmsSCHs2CiBecMZvRXi57W
ysVOoyqHZUOuDrpd3thxboB8s2qp6ZjWl41ig273FDoKu1FL1CUAxXFbcJa96w0iTPCBukTh
tiCHYLqUNnjnKNdCq/O85dfkLj+DB52s3xR1IQGycAYscmhqaDOEwUV30lqdP26QARRWmXas
GsWCUYEqdaMnQP2fiIe1GevX8ygu5CkBChytk/VcEZ7LV4GLoQOCHEKanbUZMiXz4DISET88
iniS0zipTN84vbd7g06j2XTW/nNSXURwOgx8x9bVb8y1RUiboVENPGV/WdP16azwMKku2MWO
XYnL3MygeflN7nIjALdyk6dKuWXcKXmDiAZTgR5aiS6cqDG3FiVd7vO22XPs9e6YEuKeWuAp
DDfotybZr9eOOcYEEqZpG8G6iGPAFv/MwLXgPCxAlyUqV5PpN+Zk4QkshZo9N3dF9mCEKjFs
4yR4/yngJDmld9WOFBSazr8k2KEeR6iK6E5tI7BEB06eLCF+VT2lLjhZF5Xe9Yw28bPoUHJ6
J8O2jflY99GmSsJvNRP3RYcu0eZ2RlwCiy0+87/EXxRdGn834uLGtuXxzgiO1G+IeRB+P/5Z
MYfNfr1P9eYAWIVpTw3ec/vjZH9MFdDdgJvZvP5a2w/xBw6tFDj7x9y3R59vZpAPVncndhon
Fr9BTGHn7YMOgBe7ccPn7c8cf+lHNDG40HnG3L0gCDyUQKy5LzhxXCREIz8X3xtY1v4K3cy4
StuWITnHxPYLHhgxv0NQidUuLKC6xZ4RONPeNGTG/G1sG1lJLsLe1YYUIUSgZaNxHL3z65xn
dFKyxw1TRK2fj75uMVjOOaKUrjRQbw9u76sGN0BfSthGSorXMvQVPDU6XdkmMW3fciPbYIWa
NtdFxZJ0b05mztuydnzd5jLltozWTcmcV5c6aV6T08duS1SXRygf3xwzKGHnzqGKXUjqrDfe
mZPY4LOdTmJPDCkbTkSItJiM1llyxNA6T9Hipgd8/3VXh/0vDIQ/aug/JW4/mNLGbR4ums2J
mxJaYiKdN/jzfEasaJMIeT4OEXMbsaITl3K3Ctz2LuEpEyH4DDN3cHt2fwOF3tY+Elf4QlPi
MC3R3S3/nk3aY1owpeNUgznNSCKZ4tBx1nkDKEv8KpjaPkxzOT1MNogBy7vl9SqGMU4TvTTn
YqSuZF/QLrOond2JPjc1CFuPNuFQ7r8cLzlUHkFt3rimYXhP3B6orSjx4URrW+u6NZjGloCd
a9LuOB9xTr8ZTLQlvlBojtdWqTEzNFwarHEOG43aZmk/LZFtJzNYwZpwqcuaa65VMYqxTW1I
35YaSEM7J5MrdI4msHOio6M/O7k8WMPHs0I3wvKeW1xRmkNDdFqPSktzbn5fd765Qqefzs5c
chOFLt6YmjzhTLn9/cduEYTa/e98/rFLdoB6+24lBF53q7JTd0l2Z5ATjqU/zc8IwSkIyK6r
1G+xZuTi6y/gs2+8YijqbHOoMDqTILOVkvRzwtbQUM6uL3yfj4Uf5Up3xe9tbhjrz77tuTzX
ZzDRrqAcHdRNMGlo7k3g1uih0o2Yc/dt9oCy/lUXWP5rmpCQSN9N2qBbqnd2/hvEqo4BFx/l
lsMl17oS7m0/0h//E4d6O/R2bYNQtnx+d9HKX+kc67BMlxiR+GRTrGyeuUR6T05b+/C5coCv
mcLxlDL37aFcZaZigEw+cm9lnXN2W4XhqVemGNns+vEt3D0pJxwFSEca0lywJkV08wEGfSYu
j3O424/Trs9trj8eP2y946vLkr42irH5zalUX/WhonJnkv02ku/+FYYomu6t4ElHS4+XWT31
6a9XZhTPXaP2+UcaqU9ZrA9etWmu92IMSS5bv4ySfDE0fot/wl7GWXBVGCK3ynVA3uFGioBv
vcOMJmaQuPp4TjPDblMxc6fpcIN+9PzEkoPS2SIXNQb373/ScauJMoRfu+4RMU5/40FrfWIm
WneFncnI0srHwIH+uc/yoJzjM98QD04QCMMNe28f+islLYkP3z0ndqVs6C7qjtzyc4//zCMo
1cLSb58U7SnOKVB70drs1W3kGXYkLbmxKGzMwF1IboRm2u4znDzUXOAupH3fs6A7gt05wx3u
nzQJ5jruDm9uWe/g16tKm0t8mMnAGRagzZiMWiznVWOqUzQpicTOibEHvTAe9cuJjVBhsLia
4XDSVeS0HzFTuUJnu6Bxi8aVtTdmfUZ8thWgfXqn5ChRU0ue+J1JfeV2ZjYrW1WyTZxwoH54
LMX8NY2Zr++p+1ktok4aSFpsqB/r64TC+l2K6FGWe9sbxF2PRtOovV9riOh7lfxCjMrO8y4Q
7qs3Rle1HWbN7klB2FQbWn/T3CEqQ98WM2o7gWmKjaPfFNPmWna2RGcYztr8Nt5Z/eQLcB3h
0nO5cSNC4dJjkflnDl6TGJ6os+UM+F+iTyEjnOM3ogqvWk19drzwSUVdhufrAWHxtrJyuj5R
NSl83BybfJEUNZOB/HKl+jDRrqk9XtgnROQeeChMlvIOyc1PyAzLxnT9HGp7jH3Ql9jH9qhw
PKarqvPIPNPXlUHJPFNNOTG1SsoxOxIbNaUJ3kC6/VW/r50rxmnqaA4Ou+mZ/JWaYIdNA9WO
2fbjpRlWpuObiNeQ40vufAncY691OnNeJ7LcR+qq1YxTfgombwXeZ5ZLM6txnmOSNjMjJFD+
M+mc81fPuWmLZuJfqEas8Z5J4jioHX7u0UNtpjDuXeqLOK9QO3K+6iwQ9899/plWvQw7/qDZ
F6m+/b7a6TX2FK/8atzy3A4dWyVPF2rFuIxn4uDSuHM+ceuzfVRzyp8lZuWbrIrMmtx/OibF
d7TWfpxunkRlxVDpUhylL+Bjw1Z04BLTOgcxrn7p1A4b0nh0S8BP2vTrYCKIxGiirVo1UNId
5OEdVFUzhJFs+bVnbZ2fL0374HqRFl0jdEVmjdhIqcoaKOavzo//EW4kuF6noaLIffCFzUzq
HuW1f8z9m0crZjC6CaYU/LTNa27w3hN/U8pfYRN63u/7BqHK3TU/6BC09KzZAQXNO7r3ugUm
9oEpW/IemSTE0u3eCi/vDiqP/poj32thnfwi64wX5oxGjF2+d8CtmMRNFzns6NiAoQmS1rj+
xkOrhYRX97Ard+4s7fDJfuxWEr/Ga27MaHeuFotKU3a+sTVeiIUXU3OdHJvuS9dXZCdJSIHJ
sCDbh/W3sZOFKdXFVwqxrJqE9np1v/F6JnbMZdoSLzbAzS8jyWbHxAulKR9Ank5zCSB1NahI
lqWwGyKT+nJ8MzIUGsbM3VtSXVJzZjLQprqfb2kw0vnCulNXpdk6797W/ATXcvBe8zPGlMR8
sb6ABM+eeNvAHaEZo48YijY06YL7S/Zpm/lZEUK02jDyx8KQ++PzPT2z13xrLXrtSWqEeJDm
NCnQmxjpMzaRGu+e96MezYcTlmmTjqWC6THxGisk04kim2eISpeuaZDTItT6X38p1dSBvkwV
d67vfCaSb8sqCXQzrtRX640hHBRHuVwveW55WxLMiS2NnMnDSd4dOXhZw+ZzVdKZ2PyNIV7W
iRpzMdxtO/uy8zZKGviNokITWlbjPa3Mk+N3SUsrJN6NEFLyO1kucy4u2c4odq4frGm3kih4
9Jo0fdUR7qP6IzuYqbqWn9H/ivH/Ps0/9DAmMWpSgXDaiM11ydk7L48Sc38KDdvf8ZS0dZjk
XJS6k3UxQquyKazuqcHNfJNBAR3puPzNu38sbDeXHPOzykGmdDrmfZ/h8FVxM81Publ+hxEu
TLK7TEpppxWtuSmVbjKwFN465y2hEvi4RyvTw8BjRPNIaUksNzAgPdNQk+YTy/mBjVwjr+ff
FyHM7uewL8mlnjlrD9YT1RQOgxtTcUMNBNltHN80q1R8vVU5yZ5C7gPPMtsSYhy0+tSICzE/
LLjPiX4uC1zYEHPmu2RyvirnZKVldrsBDf0GIWYwyb/Ke3Fk8LGRgej6G5zWbDQ109RK/Gkt
WsXAjyJbvUqqEkyugImtlDjQfDfghr1SdNjrZXEsejKHOrJK2cTZXqZLlkDKQFuLYsaQes2U
IEexgu/rveWFzYpevLacnTr2U/xVsKgiU4zTr5BIomxLyN0WIa9iaqb3tCTmhIRJWbyZ8dee
7ntqJ2wkaXO6DkN5Ll6NaZqquZ6vW6xtNfWZO6udd1hRX7/oB/dHBB12KAg+YJynVam9b10r
Zjk6NhZfN+UzdDR1e0LumYcUrWtSLzXGLm94NnzwLFOfc/xSrEFNJkpcr2G/uL8YTvUNoo52
xQCfLcvoImf6jlYaXF8dXW2jRYwgpjRdAU+j9NeQefzbznrrq3etKFpusxmrDNmvppDKjCZy
nqmhYXGuva2MPYWStKl+tblPrltzAqU/1TbGCdyhXjmdIC1RW2sXqRV+7OE3625wavONHqnl
MetoRO+S7igfp9Bx1Q2zpvoq9WiTAXOfh6PFu77wQHwTYWZtjgPrBI+ZakG/1XbL+nrMuDtb
3HCrabdiFFKixo9oK0odTaOttiRpZSCdnS4OWcglSXaX+6rF/sCWxbNYeA1qwI2wZL814ymC
217VRsRjbs2veFrin+1za+wl6+Ktli6ZbST7aGH8ywbTeVO/dHLjtMKjrY0xxWeS88kYi3Ht
1egBxm6T1mIz3zHDBiPrFuXze06M0M/P3I0urVXPf/CAo+dnanWF8BVbO//Ra1bUgIhsfs4T
tnvIQ297zC1tV7oiyp+oHpOSxwrlcCxKYgZRhQe29xMxab6+Ulfj7ufYPK5TpvuboC/HNcVj
5E8Z5YTX9mnqHM1GDljlMB9GqKyuZyYJPc3BsvsjrehWaPCgPDTabDKGFDiGHCjVBNf0Yo6o
VDlPVZ+jbV43l598p8FdF9e32pdEXOtp3mNWP2CVr6hsIuU37Uw3NDmkrEJ+edLJYi3Tmhjm
sn6VCGPt1IS86eoa55bVxco1hgYx4NLGzX0C7y+y//3Q+0nOf2j6UlT4hdupY6nFs2aWNGx0
Qu52kkxMchRHUVHHL2q5v38PO+IwGx8+k9WQHopVTaVZMcxdgee+RIdY4aZLLgw02CePeBvc
spWjZup7fD5tP87Cg77Th+7rBvtOcUO0EVhesrVjKEpnBh3OfdThOCMTf98/obBOyeUpKRav
SV/aEJGDZflvwrkaVKDNDG5xCoQoeXE9Q63JX8xm+OewQwi2ptG0qbEHSptS2+JsXuzoaAuf
x0y4G0lsbr+z4eahzohlymE6SfV+hQ88Uox0JC6Xstbe6OVwJimvDE4YhCuP/8A+eEHjzIzq
IId6cV2LZC+NzOmzZ0dTG2NG+y5mrPYdY4ibm088ELrQRSQay43Z5TuymidlWmWiyYxyZTfR
rxzqcr0pJM2JIXYONm15vAjb+hjdwJEURYoSuX4x+lYNIi/1ZuBdB+z0E9crbxCPvMrTfbPm
EupnGxuSOTjj2uQhVcW+0NFabJoQxjJiS0nA1qjQbGmiNLBzVZqOVJ7OjvkyJZ1x6b75/9vn
e5w/Vv0DJ4WCc9pQ0tQRbq8a4YurpY+qcp1q0H1jXAJle4ISqduRZjU/buj3aMSQIaaoTT0b
d/uT7vo/z/jPY1eEyP0uhZu3NuKQRVrz6zwFhewZQ9XDSI6pVFIttkNGrjQDOVDiHxqhYsYw
q/5l7z6tamzwMxF0thFD9kxPtlKm5iTpioKn7TGKB653rFbMfE6ytRWP5mb63GoV16b83Ptl
0IAk3vI5B21n9AKXLm8+ZmZRmtqigk83LPEI0uhP5Xhb5vweXMBTbuz3DtUqMw4eq1PMvLIe
VVZdVUk3uuxq6YK2ogewTZkxcglR0RTwYCE9A/9lGV6ve4nE9HEjtfC84l7V5Bcj9rFxAq7W
F9Pq1DbhayJvDvj1jNW4VLxEOVOm/S45CiuDySJzFtcrp05NJz15hHzjihJYnG/YVvHCJ26V
URIdG0hrexLNMQRxjkJFNudVMla12p5FG2ckuqz3RZf/Nrk8MprkbKHmnBEZEm1LVRuwjNAW
rzHTN6uXqgPV2YVAfGUaGfSdejtjzd2wJKcY7ZbsB10PY+MYyY2UMHGTNnbiulDOEaOgoBpU
uV6JM/WORGjFkEKsGpsa4he7uz31pqqiPCq8sjKfeS9ln4ztJupk/8UIoWSOmJgYeEgP+Bf7
UqTif+4V/60E0xIF7uUx2Uz/mces2eCQaD/8cffBe/nOgy9T2Wkm1k+Hh8zt6Wj9M/2U7nK9
4xdjeoc7i0hRl+jLis7+t3LfZgoROhq+CSzHSBHG1H6KSE895SZpF2DB8sKsLc1Ye+N+1xy9
wf7R+JSnVcHNxMcxthRS+Gvw3MTzLz8mWxJVmS0fqNV17acmLc22xnFmjPP4/miKXS2K4sVK
Cq/xYVXfktGKNNH5ITk6YstElNDWLvdrxiqj6aktJW2aQV32LTlBbr2z15azGs7dRBEiL1HC
52VelcxJVtW2yhYOJ2htFbkEPGbCJ5zRQgcLerYcq6tZNHm8BYNaWFJYO0ItCHg1i1xds0o7
sRrZdXG0+sRx803a8hyPCtPah0WV9jpSQV1PKZfjZN1q0Grpmc3pbNKEkUkrMTs5Xl65Fqm/
SkoioI/zctnPsHJ/8+R6e9HN1Egm+bPdySWd2q3fvnRwkxdAbtfUe5x9BYscZDT7Oia80Ksu
N1nT8QoVYljfztiINCBIW/h9DM9/Y5pOUEF25sqGO6fd5moSTjjPWLtJKcgK6667HCaRNHOM
07DKyAQ8RmXl1N3nmpGSbxCRvoeb18bMg+e2mDUoO0bXWO8At9dNYLfmrC6ZyOpL2Nx41uuG
774UKXYv1agLpVQcL1ymP5dsxKTjrcV3exkQqM0vBTcztb96+D35lYlvoCfRu/9IMkXGzanR
YiYQLVXHCNLBo+o40lFaouyNN1OtesLydrRnxZH7TFHBuCNlww/GhTrsMksoOxnoGsNZ5Rrl
2vElLGkArECKemGFw9KH06HGamseOiRihK+bvjxWmYNx7TpG7nUsoym3knTumIuNLxHzTdMf
tKLRJx9kWc+2Ep2p15BGl4Ysqkpo41svcWqxdi05Oj0aQ5t/fRaPLo01Pj0q3zzEJnXVkHI4
g89O6/pt9MV46bWnyjO3tbC8WMzIpPgbZOPnI8POURMJGDQ+u1j6lw3f9haUK3yutMP5mPuK
FIy8qZQtBTkp31u3LTRCuZiSsEMPXMliyzJEZXR9Fk1zrg8zs0jHEH04tatN9MWYMU4RW/T0
/G9Lnfg3OsxbnXRVfyU7zTxaOYc8UljCKCpPcLMpKaUZVZg7ghU7UzND9CqO4dKtnqi7BbJc
4wLCoZLGaaKa7qZkSt6VdKJ6pu9M1HgtTurizPXms14iOTWCtqdsKCm0Eg5+aSWX8TXz29jc
xBZKWFZCkJxg5ZMe3N0aH9lDXeDJsanzx1w529zQioNVp238JMn3Z1SxRVlDzRWtx+ZHWsZr
FFXsXjkcLypO1U4mFa9uiTjf8+2k8JTsE2thJ2TCMDUkV6bpWeqmnVUi8sotBc0MNUw1/qZD
X4NZ6e77/2K0F1VbRGARgUUEFhFYRGARgUUEFhFYRGARgUUEFhFYRGARgUUEFhFYRGARgUUE
FhH4/4+A6JsmfqFnC97+6sLfNx9+wC1dCASkOVuw4r18SAs/S8D2PgugA3LOFrzh8fFI/vT1
+Vue3zO2wD0eH+TVhTLh9n7au31exie+UAhQrqApwgtxGuGEwIBvV5gCt5VmCCzCG6RIIw6B
vdMIHNgwCDvwDXKX70KoIFQRSPC3e4FD7EM6acQpQA1l24FvdyAFcL5BLzdD+CM8QKrGR2T/
mUcTUOkB7dwABwZo4QQkwV9phBzCEHz7gc387e8BxFaeVCRC8W2KImIX0JFPtbDvBmRBqYeA
JF8gFQv2caCuHuDPFei2AxzzNT8JSnPlSTyIMEZYgHRbQIfjcZu+1QfWSxphBo7sEI5AM3fA
4Y5wAHJg/Q4ACQ4gXRphz0PRk4cpxNGfJ2Xv21KdQMpJgBK/dlADqMtJkMrH6Xsg+RSQC0vj
l/9pTiyPzo1Xvh1PCg7wLKRC2a48bb2ALtCy0kC/kyDNlVdziO5phDwoHyKDA7IwgMId6G8P
tIP6QAnuvHwMjw7q+TEax7d1lweonQT1lQZon+SV6Aj4IY58WR483U6BFOgnfAQgXrD2EH8n
Xir0QFiyHU8je552Cx4pzZPgDuwqjVAAG/QV6HnQpx3A8ft1h2VDn3T9IB3iz0fjfWqolRdP
9/dTIZ0dj/qdzf5Yyile2QvlL+DL1w4HJJ7k4Ql5YL3gMbQFxNHrbS0hD9R+Qcb75bvwMIH+
BhGANYU1gujggF2gj3iBvT/ala/zaZD/DmOIFfRWW/DH93tzxD6QBtOhrXCghPfL/bj9/uyb
MIVfK+hV72ME2y/UFbYN6Et8+8J6whb5KT5IvY9nd8gDffU0aA1QRyegHx8hyH8AsR94JA7U
BZZ+GvgB5FQDyCiBXwOQH8ArR58nAXobrB0GSLAD+TjwDWWfBGgs+B2/FR8FsvitzgjsQdyh
bfhtFvrRpzmNgXyomRH49QY873wS2o4fG7x4WkINV0lLg8gF9/gRCvXWWm6AF/q221+QsgOh
/ju/HigD4vB+u+J7FUQQYoMEUXwX+L3/NhpBS8A8fouXBvXkx4GFWPFnHlNQK2gTF4A89CJp
IMEbHGOBhSD1O+z28aT9Ed2FctxAHg7I4NsSpsJ2J807hm3JB2ywLUL7QLxPg1L4PQL0dFjO
AtKHedpAG8H2ANsU5Id8kKoRbIqg74JYwh5EEXiHGu/oAeg7oKX+yA9bJsQEtjNou78rB8a4
9/vQv6bLp/tgfuSAEdLx93rt/r1WqgjlP9TJjNdSYCSFfRHEFSIIo8YC3mYIfcRe0MYOfGCz
/8QJ6/HOc3cBX4Le5Ap6ZYilGZAPrfRheZALyaOEetiBI77n7wKjCb73Q72ghO8A4jBmQJr3
9Yc+6gM26A32wC9gjwprA1szlP7O6xZ67g+p+F5zCOAB+wN34L0wtsB4tdDH8KMDTIE9IfSm
v6MN5DMEmi0g/05zmHMAcYSH+4LHe/D8Hubw4x0/ikLfkwd6LEhZsBq/L1zQ88OS+G2IL1Ea
eIQfrw57gRQskL/gkXDkA32Trw2MM7ClwSgN2/L7MiDFn8d4H1LoAYtBTtiHwBi5UO8P8YfS
YHzyBZq4A7qFns8MpLm9jTqw51gYo7xfDvQMc56OcGTFH5PxrQZHcRAn2Gb/6AemQO47j4e9
I4wpJ3lU+sBTTUEKHO3YA6qFfg7q+B2QB8fB0Eegp/Djyncgjd8jvNMDoggjNIy4H/oQ1GUh
Qn3Pqyv0Kb79YPz8lPd+DxCXB5T8PnShVjBVCbQfiIMRLw9KexedDgGdYbuBLcKOR7UXaAZ7
NX4ck+bp+GeUoZaw/cLWqMzbuw/8EJYCvRGOFKA1IJUvwIHfk3+YCzE7DHzakEe3G0iB4+4F
TTFAAn9kt2BZLEIWaArtCfuMhTEQv9+Fcdof6Axz+GgfAUdw/11LX2jf8oCWj+eHY4T3NT2E
QAN9oI4w3hnzdIQ13QV6AXVQZ6jrn85s4HmLyD5Ar4ew+UP+ToQz8DcHmL8Ktgx3Xh/lAtBV
/DTlwvnSh7/LoM2gTXAf5vxfHq9YiECneFY4hdgJ/AhqCer8sU0A0v9+Fvkxir+VtoTHJYr4
q+9cWQLOeF8F8U974T5iKQIhwT/8/XsKnD3/lc/wX6T7K7L+Hs0OwPbV/wNrFKDdCzZ4Sewy
Ht+ePT/yfvkzE2B2oMALHH/Chp9M54l4+wV5/9Pny08SiH08Z8UniwbFfbYLOB9sqmBfgL//
YQX4UrsFePZG/BdKHtgT
    SensorDataFile = <blob elided: 365386 chars, md5=6bdf4b68>
    Type Image = RLX_056339.jpg
    URL = http://relux.com
    VarID = var1
    Voltage = 0 V
    Weight = 0.00 kg
    Width = 100 mm  [stored 0.328084 ft]

note: [stored X ft] marks values corroborated as IEEE doubles in the binary element streams (Revit-internal decimal feet)

## geometry (parser evidence)
native form markers: Blend x4, Sweep x28
no freeform markers — native parametric forms only
